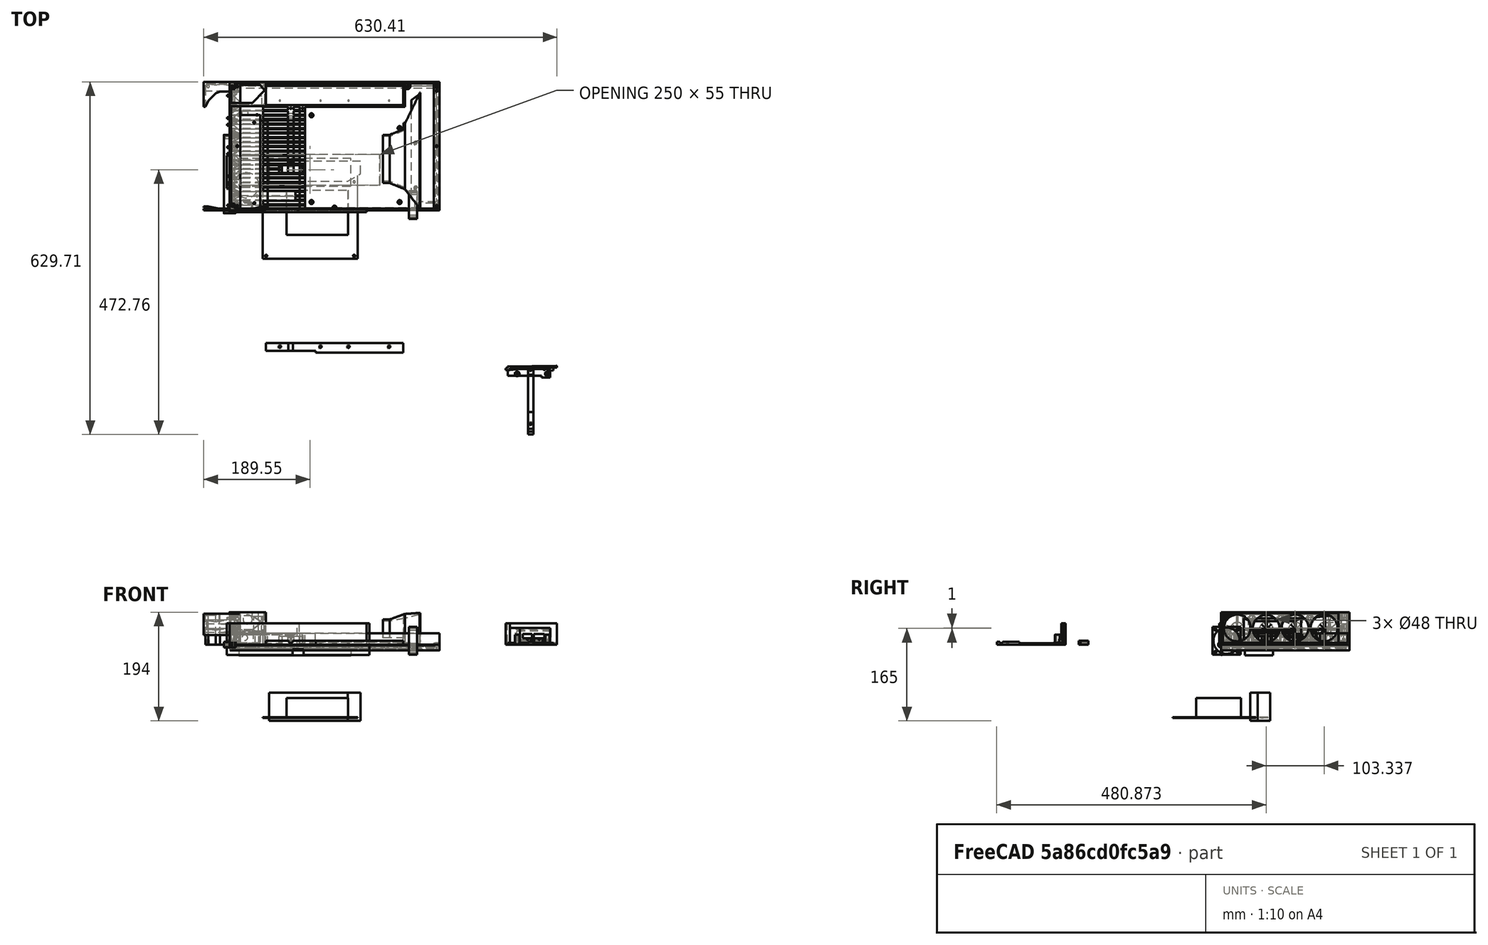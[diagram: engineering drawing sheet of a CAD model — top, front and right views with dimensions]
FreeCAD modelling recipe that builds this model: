
FCSTD DOCUMENT  (FreeCAD 1.0R39109 (Git))
Label: 4_fan_duct_version
License: All rights reserved
LicenseURL: https://en.wikipedia.org/wiki/All_rights_reserved
objects: Sketcher::SketchObject×94, PartDesign::Pad×51, PartDesign::Pocket×39, PartDesign::Plane×24, PartDesign::Body×20, App::Part×20, App::Link×14, PartDesign::Chamfer×13, App::FeaturePython×12, PartDesign::Fillet×4, PartDesign::LinearPattern×3, PartDesign::AdditiveLoft×3, Spreadsheet::Sheet×2, PartDesign::Mirrored×2, PartDesign::SubtractiveLoft×1, Assembly::JointGroup×1, Assembly::AssemblyObject×1
note: 575 computed .brp shape members not serialized (recipe doc carries the construction recipe); baked Part::Feature solids carry a one-line shape summary decoded from their .brp

FEATURE [Spreadsheet::Sheet] Spreadsheet  label="components"
  cells = B1='weight; C1='width; D1='height; E1='depth; F1='corner radius; J1='radius; K1='depth; A2='screen; B2=930; C2(screen_w)=367.9; D2(screen_h)=222.4; E2(screen_glass_d)=1.5; F2(screen_glass_corner_radius)=1; I2='m3 cutout; J2(m3_hole)=3.5; A3='panel; E3(screen_panel_d)=6.5; I3='m3 insert; J3(m3_insert_r)=4.5; K3(m3_insert_depth)=7; A4='pcb; C4(screen_pcb_w)=200; D4(screen_pcb_h)=50; E4(screen_pcb_d)=19; I4='m3 for threading; J4(m3_threadhole)=2.5; I5='m3 countersunk head; J5(m3_countersunk_head)=6; A6='motherboard; B6=790; C6(mb_w)=170; D6(mb_h)=170; E6(mb_d)=51; A7='+cpu and ram and ssd; B7=100; A8='cooler; B8=400; A9='gpu; C9(gpu_w)=68; D9(gpu_h)=160; E9(gpu_d)=20; A11='psu; B11=360; C11(psu_w)=55; D11(psu_h)=170; E11(psu_d)=25; F12='mounting hole spacing; G12='mounting hole dia; A13='fan; C13(fan_w)=17; D13(fan_h)=50; E13(fan_d)=50; F13(fan_spacing)=40; A15='screen frame; C15(frame_w)==screen_w + <<choices>>.bezel * 2 + <<choices>>.margin * 2; D15(frame_h)==screen_h + <<choices>>.bezel * 2 + <<choices>>.margin * 2; E15(frame_d)==screen_panel_d + <<choices>>.frame_protective_height + <<choices>>.frame_support_thickness + <<choices>>.screen_panel_foam_thickness
FEATURE [Spreadsheet::Sheet] Spreadsheet001  label="choices"
  cells = A1='screen margin; B1(margin)=0.55; E1='old metal parts:; F1='alu density; G1=0.0027; H1='g/mm3; A2='bezel width; B2(bezel)=3; F2='frame volume; G2=222697.53; H2==G1 * G2; I2='<11mm thick; A3='corner; B3(corner)=1; F3='heatsink base volume; G3=540524.42; H3==G1 * G3; I3='<10mm thick; A4='frame-panel foam thickenss; B4(screen_panel_foam_thickness)=0.75; F4='original 3mm base; G4=266800; H4==G1 * G4; I4==H2 + H3; A5='frame height over screen; B5(frame_protective_height)=1.5; A6='frame support area thickness; B6(frame_support_thickness)=1.25; C6='<the bottom layer of frame that the foam pads are glued to, has space for the motherboard ports block and possibly the fans?; E7='fins; F7='end fins:; G7(fin_end)=3; I7='25t+25s=229.5-2*e-s; J7==B22 + 170 + 5 + 3; A8='edge screwhole margin; B8(screwhole_edge_margin)=5; E8='thickness; G8(fin_thick)=2; I8='26s = 229.5 - 2e-25t; E9='space; G9=6; I9(fin_gap)==(J7 - 2 * G7 - I10 * G8) / (1 + I10); A10='base height (under mb); B10(base_under_mb_thickness)=1.25; E10='count; G10==(J7 - 2 * G7 - G9) / (G8 + G9); I10(fin_count)=22; A11='base height total; B11(base_max_thickness)=20; A13='exit duct length; B13(exit_w)=19; A14='exit_cone_dia; B14(exit_cone)=24.5; A15='exit_fan_circle_dia; B15(exit_fan_dia)=49; A16='fan gap; B16(fan_gap)=2; A17='exit vane thickness; B17(exit_vane_thinnest)=1; C17(exit_vane_thickest)=3; A18='shroud to mb space; B18(shroud_mb_space)=29; A19='exit duct height; B19(exit_height)=55; A20='shroud_wall_thickness; B20(shroud_wall_thickness)=3; A21='shroud base screws; B21(shroud_base_screw_x)=332.5; C21(shroud_base_screw_y1)=40; D21(shroud_base_screw_y2)=120; A22='motherboard to front edge gap; B22(mb_front_edge_gap)=10; A26='left edge to psu; B26(psu_left_gap)=5; A27='top edge to psu; B27(psu_top_gap)=15; A30='leg; B30(leg_axis_dist_from_front)=75; C30(leg_length)=130; D30(leg_bracket_axis_dist)=42.5; E30(leg_bracket_length)=52.5; F30(leg_bracket_slot_end_dist_from_front)==B30 + D30 + E30; B31(leg_axle_hole_dia)=5.2; C31(leg_width)=10; F31(leg_bracket_slot_start_dist_from_front)=115; C32(leg_betweens)=5; D32(leg_clearance)=0.5
FEATURE [Sketcher::SketchObject] Sketch
  ArcFitTolerance = 1e-06
  AttachmentSupport = -> [XY_Plane001]
  FullyConstrained = true
  MakeInternals = false
  MapMode = 5
  expr: Constraints[10] = <<components>>.psu_h
  expr: Constraints[30] = <<components>>.m3_hole
  expr: Constraints[9] = <<components>>.psu_w
  sketch-geometry (13):
    g0: LineSegment StartX=0 StartY=0 StartZ=0 EndX=55 EndY=0 EndZ=0
    g1: LineSegment StartX=55 StartY=0 StartZ=0 EndX=55 EndY=170 EndZ=0
    g2: LineSegment StartX=55 StartY=170 StartZ=0 EndX=0 EndY=170 EndZ=0
    g3: LineSegment StartX=0 StartY=170 StartZ=0 EndX=0 EndY=0 EndZ=0
    g4: LineSegment [constr] StartX=10.85 StartY=13 StartZ=0 EndX=44.15 EndY=13 EndZ=0
    g5: LineSegment [constr] StartX=44.15 StartY=13 StartZ=0 EndX=44.15 EndY=157 EndZ=0
    g6: LineSegment [constr] StartX=44.15 StartY=157 StartZ=0 EndX=10.85 EndY=157 EndZ=0
    g7: LineSegment [constr] StartX=10.85 StartY=157 StartZ=0 EndX=10.85 EndY=13 EndZ=0
    g8: GeomPoint [constr] X=27.5 Y=85 Z=0
    g9: Circle CenterX=10.85 CenterY=157 CenterZ=0 NormalX=0 NormalY=0 NormalZ=1 AngleXU=0 Radius=1.75
    g10: Circle CenterX=44.15 CenterY=157 CenterZ=0 NormalX=0 NormalY=0 NormalZ=1 AngleXU=0 Radius=1.75
    g11: Circle CenterX=10.85 CenterY=13 CenterZ=0 NormalX=0 NormalY=0 NormalZ=1 AngleXU=0 Radius=1.75
    g12: Circle CenterX=44.15 CenterY=13 CenterZ=0 NormalX=0 NormalY=0 NormalZ=1 AngleXU=0 Radius=1.75
  constraints (31):
    c: Coincident(g0,g1)
    c: Coincident(g1,g2)
    c: Coincident(g2,g3)
    c: Coincident(g3,g0)
    c: Horizontal(g0)
    c: Horizontal(g2)
    c: Vertical(g1)
    c: Vertical(g3)
    c: Coincident(g0,g-1)
    c: DistanceX(g2,g2) = 55
    c: DistanceY(g1,g1) = 170
    c: Coincident(g4,g5)
    c: Coincident(g5,g6)
    c: Coincident(g6,g7)
    c: Coincident(g7,g4)
    c: Horizontal(g4)
    c: Horizontal(g6)
    c: Vertical(g5)
    c: Vertical(g7)
    c: Symmetric(g6,g4,g8)
    c: Distance(g5,g7) = 33.3
    c: Distance(g4,g6) = 144
    c: Symmetric(g2,g0,g8)
    c: Coincident(g9,g6)
    c: Coincident(g10,g5)
    c: Coincident(g11,g4)
    c: Coincident(g12,g4)
    c: Equal(g9,g10)
    c: Equal(g10,g11)
    c: Equal(g11,g12)
    c: Diameter(g11) = 3.5
FEATURE [PartDesign::Pad] Pad
  Direction = (0,0,1)
  Length = 25
  Length2 = 10
  Profile = -> Sketch
  ReferenceAxis = -> Sketch [N_Axis]
  Refine = true
  Suppressed = false
  Type = 0
  expr: Length = <<components>>.psu_d
FEATURE [PartDesign::Plane] DatumPlane
  AttachmentSupport = -> [Pad]
  Length = 92.6491
  MapMode = 5
  Placement = pos=(0,170,0) rot=(0,0.707107,0.707107;3.14159rad)
  ResizeMode = 0
  Width = 62.6491
FEATURE [Sketcher::SketchObject] Sketch001
  ArcFitTolerance = 1e-06
  AttachmentSupport = -> [DatumPlane]
  FullyConstrained = true
  MakeInternals = false
  MapMode = 5
  Placement = pos=(0,170,0) rot=(0,0.707107,0.707107;3.14159rad)
  expr: Constraints[10] = <<components>>.psu_d
  expr: Constraints[9] = <<components>>.psu_w
  sketch-geometry (5):
    g0: LineSegment [constr] StartX=-55 StartY=25 StartZ=0 EndX=-55 EndY=0 EndZ=0
    g1: LineSegment [constr] StartX=-55 StartY=0 StartZ=0 EndX=0 EndY=0 EndZ=0
    g2: LineSegment [constr] StartX=0 StartY=0 StartZ=0 EndX=0 EndY=25 EndZ=0
    g3: LineSegment [constr] StartX=0 StartY=25 StartZ=0 EndX=-55 EndY=25 EndZ=0
    g4: Circle CenterX=-27.5 CenterY=12.5 CenterZ=0 NormalX=0 NormalY=0 NormalZ=1 AngleXU=0 Radius=5
  constraints (13):
    c: Coincident(g0,g1)
    c: Coincident(g1,g2)
    c: Coincident(g2,g3)
    c: Coincident(g3,g0)
    c: Vertical(g0)
    c: Vertical(g2)
    c: Horizontal(g1)
    c: Horizontal(g3)
    c: Coincident(g1,g-1)
    c: DistanceX(g3,g3) = 55
    c: DistanceY(g0,g0) = 25
    c: Diameter(g4) = 10
    c: Symmetric(g0,g1,g4)
FEATURE [PartDesign::Pad] Pad001
  BaseFeature = -> Pad
  Direction = (0,1,-2e-16)
  Length = 7
  Length2 = 10
  Profile = -> Sketch001
  ReferenceAxis = -> Sketch001 [N_Axis]
  Refine = true
  Suppressed = false
  Type = 0
FEATURE [PartDesign::Body] Body
  AllowCompound = false
  Group = -> [Sketch,Pad,DatumPlane,Sketch001,Pad001]
  Origin = -> Origin001
  Tip = -> Pad001
FEATURE [App::Part] Part  label="PSU"
  Group = -> [Body]
  Origin = -> Origin
FEATURE [Sketcher::SketchObject] Sketch002
  ArcFitTolerance = 1e-06
  AttachmentSupport = -> [XY_Plane003]
  FullyConstrained = true
  MakeInternals = false
  MapMode = 5
  expr: Constraints[26] = <<components>>.screen_glass_corner_radius
  expr: Constraints[5] = <<components>>.screen_w
  expr: Constraints[6] = <<components>>.screen_h
  sketch-geometry (12):
    g0: LineSegment StartX=1 StartY=4.954e-13 StartZ=0 EndX=366.9 EndY=4.954e-13 EndZ=0
    g1: LineSegment StartX=367.9 StartY=1 StartZ=0 EndX=367.9 EndY=221.4 EndZ=0
    g2: LineSegment StartX=366.9 StartY=222.4 StartZ=0 EndX=1 EndY=222.4 EndZ=0
    g3: LineSegment StartX=4.954e-13 StartY=221.4 StartZ=0 EndX=4.954e-13 EndY=1 EndZ=0
    g4: ArcOfCircle CenterX=1 CenterY=1 CenterZ=0 NormalX=0 NormalY=0 NormalZ=1 AngleXU=0 Radius=1 StartAngle=3.14159 EndAngle=4.71239
    g5: GeomPoint [constr] X=0 Y=0 Z=0
    g6: ArcOfCircle CenterX=1 CenterY=221.4 CenterZ=0 NormalX=0 NormalY=0 NormalZ=1 AngleXU=0 Radius=1 StartAngle=1.5708 EndAngle=3.14159
    g7: GeomPoint [constr] X=0 Y=222.4 Z=0
    g8: ArcOfCircle CenterX=366.9 CenterY=221.4 CenterZ=0 NormalX=0 NormalY=0 NormalZ=1 AngleXU=0 Radius=1 StartAngle=-3.1388e-12 EndAngle=1.5708
    g9: GeomPoint [constr] X=367.9 Y=222.4 Z=0
    g10: ArcOfCircle CenterX=366.9 CenterY=1 CenterZ=0 NormalX=0 NormalY=0 NormalZ=1 AngleXU=0 Radius=1 StartAngle=4.71239 EndAngle=6.28319
    g11: GeomPoint [constr] X=367.9 Y=0 Z=0
  constraints (27):
    c: Horizontal(g0)
    c: Horizontal(g2)
    c: Vertical(g1)
    c: Vertical(g3)
    c: Coincident(g5,g-1)
    c: DistanceX(g5,g11) = 367.9
    c: DistanceY(g5,g7) = 222.4
    c: PointOnObject(g5,g0)
    c: PointOnObject(g5,g3)
    c: Tangent(g0,g4) = -1.5708
    c: Tangent(g3,g4) = -1.5708
    c: PointOnObject(g7,g3)
    c: PointOnObject(g7,g2)
    c: Tangent(g3,g6) = -1.5708
    c: Tangent(g2,g6) = -1.5708
    c: PointOnObject(g9,g2)
    c: PointOnObject(g9,g1)
    c: Tangent(g2,g8) = -1.5708
    c: Tangent(g1,g8) = -1.5708
    c: PointOnObject(g11,g0)
    c: PointOnObject(g11,g1)
    c: Tangent(g0,g10) = -1.5708
    c: Tangent(g1,g10) = -1.5708
    c: Equal(g4,g6)
    c: Equal(g6,g8)
    c: Equal(g8,g10)
    c: Radius(g4) = 1
FEATURE [PartDesign::Pad] Pad002
  Direction = (0,0,1)
  Length = 1.5
  Length2 = 10
  Profile = -> Sketch002
  ReferenceAxis = -> Sketch002 [N_Axis]
  Refine = true
  Reversed = true
  Suppressed = false
  Type = 0
  expr: Length = <<components>>.screen_glass_d
FEATURE [Sketcher::SketchObject] Sketch003
  ArcFitTolerance = 1e-06
  AttachmentSupport = -> [XY_Plane003]
  FullyConstrained = true
  MakeInternals = false
  MapMode = 5
  expr: Constraints[22] = <<components>>.screen_h - 4
  expr: Constraints[23] = <<components>>.screen_w - 2.5
  sketch-geometry (8):
    g0: LineSegment StartX=6.5 StartY=12.5 StartZ=0 EndX=6.5 EndY=218.4 EndZ=0
    g1: LineSegment StartX=6.5 StartY=218.4 StartZ=0 EndX=365.4 EndY=218.4 EndZ=0
    g2: LineSegment StartX=365.4 StartY=218.4 StartZ=0 EndX=365.4 EndY=12.5 EndZ=0
    g3: LineSegment StartX=365.4 StartY=12.5 StartZ=0 EndX=330.4 EndY=12.5 EndZ=0
    g4: LineSegment StartX=330.4 StartY=12.5 StartZ=0 EndX=330.4 EndY=1 EndZ=0
    g5: LineSegment StartX=330.4 StartY=1 StartZ=0 EndX=41.5 EndY=1 EndZ=0
    g6: LineSegment StartX=41.5 StartY=1 StartZ=0 EndX=41.5 EndY=12.5 EndZ=0
    g7: LineSegment StartX=41.5 StartY=12.5 StartZ=0 EndX=6.5 EndY=12.5 EndZ=0
  constraints (24):
    c: Vertical(g0)
    c: Coincident(g0,g1)
    c: Horizontal(g1)
    c: Coincident(g1,g2)
    c: Vertical(g2)
    c: Coincident(g2,g3)
    c: Horizontal(g3)
    c: Coincident(g3,g4)
    c: Vertical(g4)
    c: Coincident(g4,g5)
    c: Coincident(g5,g6)
    c: Vertical(g6)
    c: Coincident(g6,g7)
    c: Coincident(g7,g0)
    c: Horizontal(g7)
    c: Horizontal(g5)
    c: Equal(g7,g3)
    c: DistanceX(g3,g3) = 35
    c: DistanceY(g2) = 12.5
    c: DistanceY(g4) = 1
    c: Equal(g6,g4)
    c: DistanceX(g0) = 6.5
    c: DistanceY(g0) = 218.4
    c: DistanceX(g1) = 365.4
FEATURE [PartDesign::Pad] Pad003
  BaseFeature = -> Pad002
  Direction = (0,0,1)
  Length = 6.5
  Length2 = 10
  Profile = -> Sketch003
  ReferenceAxis = -> Sketch003 [N_Axis]
  Refine = true
  Reversed = true
  Suppressed = false
  Type = 0
  expr: Length = <<components>>.screen_panel_d
FEATURE [Sketcher::SketchObject] Sketch004
  ArcFitTolerance = 1e-06
  AttachmentSupport = -> [XY_Plane005]
  FullyConstrained = true
  MakeInternals = false
  MapMode = 5
  expr: Constraints[10] = <<components>>.mb_h
  expr: Constraints[9] = <<components>>.mb_w
  sketch-geometry (12):
    g0: LineSegment StartX=0 StartY=0 StartZ=0 EndX=170 EndY=0 EndZ=0
    g1: LineSegment StartX=170 StartY=0 StartZ=0 EndX=170 EndY=170 EndZ=0
    g2: LineSegment StartX=170 StartY=170 StartZ=0 EndX=0 EndY=170 EndZ=0
    g3: LineSegment StartX=0 StartY=170 StartZ=0 EndX=0 EndY=0 EndZ=0
    g4: Circle CenterX=6.35 CenterY=4.8997 CenterZ=0 NormalX=0 NormalY=0 NormalZ=1 AngleXU=0 Radius=2
    g5: Circle CenterX=163.65 CenterY=4.8997 CenterZ=0 NormalX=0 NormalY=0 NormalZ=1 AngleXU=0 Radius=2
    g6: Circle CenterX=6.35 CenterY=159.84 CenterZ=0 NormalX=0 NormalY=0 NormalZ=1 AngleXU=0 Radius=2
    g7: Circle CenterX=163.65 CenterY=136.98 CenterZ=0 NormalX=0 NormalY=0 NormalZ=1 AngleXU=0 Radius=2
    g8: LineSegment [constr] StartX=6.35 StartY=159.84 StartZ=0 EndX=6.35 EndY=4.8997 EndZ=0
    g9: LineSegment [constr] StartX=6.35 StartY=4.8997 StartZ=0 EndX=163.65 EndY=4.8997 EndZ=0
    g10: LineSegment [constr] StartX=163.65 StartY=4.8997 StartZ=0 EndX=163.65 EndY=136.98 EndZ=0
    g11: LineSegment [constr] StartX=163.65 StartY=136.98 StartZ=0 EndX=6.35 EndY=136.98 EndZ=0
  constraints (32):
    c: Coincident(g0,g1)
    c: Coincident(g1,g2)
    c: Coincident(g2,g3)
    c: Coincident(g3,g0)
    c: Horizontal(g0)
    c: Horizontal(g2)
    c: Vertical(g1)
    c: Vertical(g3)
    c: Coincident(g0,g-1)
    c: DistanceX(g2,g2) = 170
    c: DistanceY(g1,g1) = 170
    c: Diameter(g4) = 4
    c: Diameter(g5) = 4
    c: Diameter(g6) = 4
    c: Diameter(g7) = 4
    c: Coincident(g8,g6)
    c: Coincident(g8,g4)
    c: Vertical(g8)
    c: Coincident(g9,g4)
    c: Coincident(g9,g5)
    c: Horizontal(g9)
    c: Coincident(g10,g5)
    c: Coincident(g10,g7)
    c: Vertical(g10)
    c: Distance(g6,g2) = 10.16
    c: Distance(g6,g3) = 6.35
    c: Distance(g7,g1) = 6.35
    c: DistanceY(g5) = 4.8997
    c: Coincident(g11,g7)
    c: PointOnObject(g11,g8)
    c: Horizontal(g11)
    c: Distance(g6,g11) = 22.86
FEATURE [PartDesign::Pad] Pad004
  Direction = (0,0,1)
  Length = 1.6
  Length2 = 10
  Profile = -> Sketch004
  ReferenceAxis = -> Sketch004 [N_Axis]
  Refine = true
  Suppressed = false
  Type = 0
FEATURE [Sketcher::SketchObject] Sketch005
  ArcFitTolerance = 1e-06
  AttachmentSupport = -> [XY_Plane003]
  FullyConstrained = true
  MakeInternals = false
  MapMode = 5
  sketch-geometry (4):
    g0: LineSegment StartX=17 StartY=43 StartZ=0 EndX=217 EndY=43 EndZ=0
    g1: LineSegment StartX=217 StartY=43 StartZ=0 EndX=217 EndY=93 EndZ=0
    g2: LineSegment StartX=217 StartY=93 StartZ=0 EndX=17 EndY=93 EndZ=0
    g3: LineSegment StartX=17 StartY=93 StartZ=0 EndX=17 EndY=43 EndZ=0
  constraints (12):
    c: Coincident(g0,g1)
    c: Coincident(g1,g2)
    c: Coincident(g2,g3)
    c: Coincident(g3,g0)
    c: Horizontal(g0)
    c: Horizontal(g2)
    c: Vertical(g1)
    c: Vertical(g3)
    c: Distance(g1,g3) = 200
    c: Distance(g0,g2) = 50
    c: DistanceX(g0) = 17
    c: DistanceY(g0) = 43
FEATURE [PartDesign::Pad] Pad005
  BaseFeature = -> Pad003
  Direction = (0,0,1)
  Length = 19
  Length2 = 10
  Profile = -> Sketch005
  ReferenceAxis = -> Sketch005 [N_Axis]
  Refine = true
  Reversed = true
  Suppressed = false
  Type = 0
  expr: Length = <<components>>.screen_pcb_d
FEATURE [PartDesign::Body] Body001
  AllowCompound = false
  Group = -> [Sketch002,Pad002,Sketch003,Pad003,Sketch005,Pad005]
  Origin = -> Origin003
  Tip = -> Pad005
FEATURE [App::Part] Part001  label="SCREEN"
  Group = -> [Body001]
  Origin = -> Origin002
FEATURE [Sketcher::SketchObject] Sketch006
  ArcFitTolerance = 1e-06
  AttachmentSupport = -> [XY_Plane007]
  FullyConstrained = false
  MakeInternals = false
  MapMode = 5
  expr: Constraints[20] = <<components>>.frame_w
  expr: Constraints[21] = <<components>>.frame_h
  expr: Constraints[22] = <<choices>>.corner
  sketch-geometry (12):
    g0: LineSegment StartX=1 StartY=1.7071e-12 StartZ=0 EndX=374 EndY=1.7071e-12 EndZ=0
    g1: LineSegment StartX=375 StartY=1 StartZ=0 EndX=375 EndY=228.5 EndZ=0
    g2: LineSegment StartX=374 StartY=229.5 StartZ=0 EndX=1 EndY=229.5 EndZ=0
    g3: LineSegment StartX=1.7071e-12 StartY=228.5 StartZ=0 EndX=1.7071e-12 EndY=1 EndZ=0
    g4: ArcOfCircle CenterX=1 CenterY=1 CenterZ=0 NormalX=0 NormalY=0 NormalZ=1 AngleXU=0 Radius=1 StartAngle=3.14159 EndAngle=4.71239
    g5: ArcOfCircle CenterX=374 CenterY=1 CenterZ=0 NormalX=0 NormalY=0 NormalZ=1 AngleXU=0 Radius=1 StartAngle=4.71239 EndAngle=6.28319
    g6: ArcOfCircle CenterX=374 CenterY=228.5 CenterZ=0 NormalX=0 NormalY=0 NormalZ=1 AngleXU=0 Radius=1 StartAngle=-2.76916e-11 EndAngle=1.5708
    g7: ArcOfCircle CenterX=1 CenterY=228.5 CenterZ=0 NormalX=0 NormalY=0 NormalZ=1 AngleXU=0 Radius=1 StartAngle=1.5708 EndAngle=3.14159
    g8: GeomPoint [constr] X=0 Y=0 Z=0
    g9: GeomPoint [constr] X=375 Y=229.5 Z=0
    g10: GeomPoint [constr] X=14.2421 Y=11.9526 Z=0
    g11: GeomPoint [constr] X=324.973 Y=165.011 Z=0
  constraints (23):
    c: Tangent(g0,g4) = -1.5708
    c: Tangent(g0,g5) = -1.5708
    c: Tangent(g1,g5) = -1.5708
    c: Tangent(g1,g6) = -1.5708
    c: Tangent(g2,g6) = -1.5708
    c: Tangent(g2,g7) = -1.5708
    c: Tangent(g3,g7) = -1.5708
    c: Tangent(g3,g4) = -1.5708
    c: Horizontal(g0)
    c: Horizontal(g2)
    c: Vertical(g1)
    c: Vertical(g3)
    c: Equal(g4,g5)
    c: Equal(g5,g6)
    c: Equal(g6,g7)
    c: PointOnObject(g8,g0)
    c: PointOnObject(g8,g3)
    c: PointOnObject(g9,g1)
    c: PointOnObject(g9,g2)
    c: Coincident(g8,g-1)
    c: DistanceX(g9) = 375
    c: DistanceY(g9) = 229.5
    c: Radius(g6) = 1
FEATURE [PartDesign::Pad] Pad006
  Direction = (0,0,1)
  Length = 10
  Length2 = 10
  Profile = -> Sketch006
  ReferenceAxis = -> Sketch006 [N_Axis]
  Refine = true
  Reversed = true
  Suppressed = false
  Type = 0
  expr: Length = <<components>>.frame_d
FEATURE [Sketcher::SketchObject] Sketch007
  ArcFitTolerance = 1e-06
  AttachmentSupport = -> [XY_Plane007]
  FullyConstrained = true
  MakeInternals = false
  MapMode = 5
  expr: Constraints[19] = <<components>>.screen_w + 2 * <<choices>>.margin
  expr: Constraints[20] = <<components>>.screen_h + 2 * <<choices>>.margin
  expr: Constraints[21] = <<components>>.screen_glass_corner_radius
  expr: Constraints[22] = <<choices>>.bezel
  expr: Constraints[23] = <<choices>>.bezel
  sketch-geometry (10):
    g0: LineSegment StartX=4 StartY=3 StartZ=0 EndX=371 EndY=3 EndZ=0
    g1: LineSegment StartX=372 StartY=4 StartZ=0 EndX=372 EndY=225.5 EndZ=0
    g2: LineSegment StartX=371 StartY=226.5 StartZ=0 EndX=4 EndY=226.5 EndZ=0
    g3: LineSegment StartX=3 StartY=225.5 StartZ=0 EndX=3 EndY=4 EndZ=0
    g4: ArcOfCircle CenterX=4 CenterY=4 CenterZ=0 NormalX=0 NormalY=0 NormalZ=1 AngleXU=0 Radius=1 StartAngle=3.14159 EndAngle=4.71239
    g5: ArcOfCircle CenterX=371 CenterY=4 CenterZ=0 NormalX=0 NormalY=0 NormalZ=1 AngleXU=0 Radius=1 StartAngle=4.71239 EndAngle=6.28319
    g6: ArcOfCircle CenterX=371 CenterY=225.5 CenterZ=0 NormalX=0 NormalY=0 NormalZ=1 AngleXU=0 Radius=1 StartAngle=-1.15e-14 EndAngle=1.5708
    g7: ArcOfCircle CenterX=4 CenterY=225.5 CenterZ=0 NormalX=0 NormalY=0 NormalZ=1 AngleXU=0 Radius=1 StartAngle=1.5708 EndAngle=3.14159
    g8: GeomPoint [constr] X=3 Y=3 Z=0
    g9: GeomPoint [constr] X=372 Y=226.5 Z=0
  constraints (24):
    c: Tangent(g0,g4) = -1.5708
    c: Tangent(g0,g5) = -1.5708
    c: Tangent(g1,g5) = -1.5708
    c: Tangent(g1,g6) = -1.5708
    c: Tangent(g2,g6) = -1.5708
    c: Tangent(g2,g7) = -1.5708
    c: Tangent(g3,g7) = -1.5708
    c: Tangent(g3,g4) = -1.5708
    c: Horizontal(g0)
    c: Horizontal(g2)
    c: Vertical(g1)
    c: Vertical(g3)
    c: Equal(g4,g5)
    c: Equal(g5,g6)
    c: Equal(g6,g7)
    c: PointOnObject(g8,g0)
    c: PointOnObject(g8,g3)
    c: PointOnObject(g9,g1)
    c: PointOnObject(g9,g2)
    c: Distance(g1,g3) = 369
    c: Distance(g2,g0) = 223.5
    c: Radius(g4) = 1
    c: DistanceY(g8) = 3
    c: DistanceX(g8) = 3
FEATURE [PartDesign::Pocket] Pocket
  BaseFeature = -> Pad006
  Direction = (0,0,-1)
  Length = 3
  Length2 = 5
  Profile = -> Sketch007
  ReferenceAxis = -> Sketch007 [N_Axis]
  Refine = true
  Suppressed = false
  Type = 0
  expr: Length = <<choices>>.frame_protective_height + <<components>>.screen_glass_d
FEATURE [Sketcher::SketchObject] Sketch008
  ArcFitTolerance = 1e-06
  AttachmentSupport = -> [XY_Plane007]
  FullyConstrained = true
  MakeInternals = false
  MapMode = 5
  expr: Constraints[10] = <<choices>>.bezel + <<choices>>.margin + 11
  expr: Constraints[11] = <<components>>.frame_h - <<choices>>.bezel - <<choices>>.margin - 3.5
  expr: Constraints[12] = <<choices>>.bezel + <<choices>>.margin + 6
  expr: Constraints[13] = <<components>>.frame_w - <<choices>>.bezel - <<choices>>.margin - 2
  expr: Constraints[9] = <<choices>>.bezel + <<choices>>.margin + 0.8
  sketch-geometry (24):
    g0: LineSegment StartX=10.05 StartY=222.45 StartZ=0 EndX=368.95 EndY=222.45 EndZ=0
    g1: LineSegment StartX=369.45 StartY=221.95 StartZ=0 EndX=369.45 EndY=15.55 EndZ=0
    g2: LineSegment StartX=368.95 StartY=15.05 StartZ=0 EndX=339.95 EndY=15.05 EndZ=0
    g3: LineSegment StartX=339.45 StartY=14.55 StartZ=0 EndX=339.45 EndY=4.85 EndZ=0
    g4: LineSegment StartX=338.95 StartY=4.35 StartZ=0 EndX=40.05 EndY=4.35 EndZ=0
    g5: LineSegment StartX=39.55 StartY=4.85 StartZ=0 EndX=39.55 EndY=14.05 EndZ=0
    g6: LineSegment StartX=39.05 StartY=14.55 StartZ=0 EndX=10.05 EndY=14.55 EndZ=0
    g7: LineSegment StartX=9.55 StartY=15.05 StartZ=0 EndX=9.55 EndY=221.95 EndZ=0
    g8: ArcOfCircle CenterX=10.05 CenterY=221.95 CenterZ=0 NormalX=0 NormalY=0 NormalZ=1 AngleXU=0 Radius=0.5 StartAngle=1.5708 EndAngle=3.14159
    g9: GeomPoint [constr] X=9.55 Y=222.45 Z=0
    g10: ArcOfCircle CenterX=368.95 CenterY=221.95 CenterZ=0 NormalX=0 NormalY=0 NormalZ=1 AngleXU=0 Radius=0.5 StartAngle=-1.87e-14 EndAngle=1.5708
    g11: GeomPoint [constr] X=369.45 Y=222.45 Z=0
    g12: ArcOfCircle CenterX=368.95 CenterY=15.55 CenterZ=0 NormalX=0 NormalY=0 NormalZ=1 AngleXU=0 Radius=0.5 StartAngle=4.71239 EndAngle=6.28319
    g13: GeomPoint [constr] X=369.45 Y=15.05 Z=0
    g14: ArcOfCircle CenterX=339.95 CenterY=14.55 CenterZ=0 NormalX=0 NormalY=0 NormalZ=1 AngleXU=0 Radius=0.5 StartAngle=1.5708 EndAngle=3.14159
    g15: GeomPoint [constr] X=339.45 Y=15.05 Z=0
    g16: ArcOfCircle CenterX=338.95 CenterY=4.85 CenterZ=0 NormalX=0 NormalY=0 NormalZ=1 AngleXU=0 Radius=0.5 StartAngle=4.71239 EndAngle=6.28319
    g17: GeomPoint [constr] X=339.45 Y=4.35 Z=0
    g18: ArcOfCircle CenterX=40.05 CenterY=4.85 CenterZ=0 NormalX=0 NormalY=0 NormalZ=1 AngleXU=0 Radius=0.5 StartAngle=3.14159 EndAngle=4.71239
    g19: GeomPoint [constr] X=39.55 Y=4.35 Z=0
    g20: ArcOfCircle CenterX=39.05 CenterY=14.05 CenterZ=0 NormalX=0 NormalY=0 NormalZ=1 AngleXU=0 Radius=0.5 StartAngle=5e-16 EndAngle=1.5708
    g21: GeomPoint [constr] X=39.55 Y=14.55 Z=0
    g22: ArcOfCircle CenterX=10.05 CenterY=15.05 CenterZ=0 NormalX=0 NormalY=0 NormalZ=1 AngleXU=0 Radius=0.5 StartAngle=3.14159 EndAngle=4.71239
    g23: GeomPoint [constr] X=9.55 Y=14.55 Z=0
  constraints (56):
    c: Horizontal(g0)
    c: Vertical(g1)
    c: Horizontal(g2)
    c: Vertical(g3)
    c: Horizontal(g4)
    c: Vertical(g5)
    c: Horizontal(g6)
    c: Vertical(g7)
    c: DistanceX(g23,g21) = 30
    c: DistanceY(g19) = 4.35
    c: DistanceY(g21) = 14.55
    c: DistanceY(g9) = 222.45
    c: DistanceX(g9) = 9.55
    c: DistanceX(g11) = 369.45
    c: PointOnObject(g9,g7)
    c: PointOnObject(g9,g0)
    c: Tangent(g7,g8) = 1.5708
    c: Tangent(g0,g8) = 1.5708
    c: PointOnObject(g11,g0)
    c: PointOnObject(g11,g1)
    c: Tangent(g0,g10) = 1.5708
    c: Tangent(g1,g10) = 1.5708
    c: PointOnObject(g13,g2)
    c: PointOnObject(g13,g1)
    c: Tangent(g2,g12) = 1.5708
    c: Tangent(g1,g12) = 1.5708
    c: PointOnObject(g15,g2)
    c: PointOnObject(g15,g3)
    c: Tangent(g2,g14) = -1.5708
    c: Tangent(g3,g14) = -1.5708
    c: PointOnObject(g17,g3)
    c: PointOnObject(g17,g4)
    c: Tangent(g3,g16) = 1.5708
    c: Tangent(g4,g16) = 1.5708
    c: PointOnObject(g19,g4)
    c: PointOnObject(g19,g5)
    c: Tangent(g4,g18) = 1.5708
    c: Tangent(g5,g18) = 1.5708
    c: PointOnObject(g21,g5)
    c: PointOnObject(g21,g6)
    c: Tangent(g5,g20) = -1.5708
    c: Tangent(g6,g20) = -1.5708
    c: PointOnObject(g23,g6)
    c: PointOnObject(g23,g7)
    c: Tangent(g6,g22) = 1.5708
    c: Tangent(g7,g22) = 1.5708
    c: Equal(g22,g8)
    c: Radius(g8) = 0.5
    c: Equal(g20,g18)
    c: Equal(g18,g22)
    c: Equal(g16,g14)
    c: Equal(g14,g12)
    c: Equal(g12,g10)
    c: Equal(g10,g8)
    c: PointOnObject(g14,g6)
    c: Equal(g2,g6)
FEATURE [PartDesign::Pocket] Pocket001
  BaseFeature = -> Pocket
  Direction = (0,0,-1)
  Length = 8.75
  Length2 = 5
  Profile = -> Sketch008
  ReferenceAxis = -> Sketch008 [N_Axis]
  Refine = true
  Suppressed = false
  Type = 0
  expr: Length = <<components>>.screen_panel_d + <<choices>>.frame_protective_height + <<choices>>.screen_panel_foam_thickness
FEATURE [Sketcher::SketchObject] Sketch009
  ArcFitTolerance = 1e-06
  AttachmentSupport = -> [XY_Plane007]
  FullyConstrained = true
  MakeInternals = false
  MapMode = 5
  expr: Constraints[22] = <<choices>>.bezel + <<choices>>.margin + 41.5
  expr: Constraints[23] = <<choices>>.bezel + <<choices>>.margin + 15
  sketch-geometry (10):
    g0: LineSegment StartX=19.55 StartY=45.05 StartZ=0 EndX=267.55 EndY=45.05 EndZ=0
    g1: LineSegment StartX=268.55 StartY=46.05 StartZ=0 EndX=268.55 EndY=99.05 EndZ=0
    g2: LineSegment StartX=267.55 StartY=100.05 StartZ=0 EndX=19.55 EndY=100.05 EndZ=0
    g3: LineSegment StartX=18.55 StartY=99.05 StartZ=0 EndX=18.55 EndY=46.05 EndZ=0
    g4: ArcOfCircle CenterX=19.55 CenterY=46.05 CenterZ=0 NormalX=0 NormalY=0 NormalZ=1 AngleXU=0 Radius=1 StartAngle=3.14159 EndAngle=4.71239
    g5: ArcOfCircle CenterX=267.55 CenterY=46.05 CenterZ=0 NormalX=0 NormalY=0 NormalZ=1 AngleXU=0 Radius=1 StartAngle=4.71239 EndAngle=6.28319
    g6: ArcOfCircle CenterX=267.55 CenterY=99.05 CenterZ=0 NormalX=0 NormalY=0 NormalZ=1 AngleXU=0 Radius=1 StartAngle=8e-16 EndAngle=1.5708
    g7: ArcOfCircle CenterX=19.55 CenterY=99.05 CenterZ=0 NormalX=0 NormalY=0 NormalZ=1 AngleXU=0 Radius=1 StartAngle=1.5708 EndAngle=3.14159
    g8: GeomPoint [constr] X=18.55 Y=45.05 Z=0
    g9: GeomPoint [constr] X=268.55 Y=100.05 Z=0
  constraints (24):
    c: Tangent(g0,g4) = -1.5708
    c: Tangent(g0,g5) = -1.5708
    c: Tangent(g1,g5) = -1.5708
    c: Tangent(g1,g6) = -1.5708
    c: Tangent(g2,g6) = -1.5708
    c: Tangent(g2,g7) = -1.5708
    c: Tangent(g3,g7) = -1.5708
    c: Tangent(g3,g4) = -1.5708
    c: Horizontal(g0)
    c: Horizontal(g2)
    c: Vertical(g1)
    c: Vertical(g3)
    c: Equal(g4,g5)
    c: Equal(g5,g6)
    c: Equal(g6,g7)
    c: PointOnObject(g8,g0)
    c: PointOnObject(g8,g3)
    c: PointOnObject(g9,g1)
    c: PointOnObject(g9,g2)
    c: Distance(g1,g3) = 250
    c: Distance(g0,g2) = 55
    c: Radius(g5) = 1
    c: DistanceY(g0) = 45.05
    c: DistanceX(g8) = 18.55
FEATURE [PartDesign::Pocket] Pocket002
  BaseFeature = -> Pocket001
  Direction = (0,0,-1)
  Length = 0
  Length2 = 5
  Profile = -> Sketch009
  ReferenceAxis = -> Sketch009 [N_Axis]
  Refine = true
  Suppressed = false
  Type = 1
FEATURE [Sketcher::SketchObject] Sketch010
  ArcFitTolerance = 1e-06
  AttachmentSupport = -> [XY_Plane005]
  FullyConstrained = false
  MakeInternals = false
  MapMode = 5
  sketch-geometry (11):
    g0: LineSegment [constr] StartX=0 StartY=0 StartZ=0 EndX=170 EndY=0 EndZ=0
    g1: LineSegment [constr] StartX=170 StartY=0 StartZ=0 EndX=170 EndY=170 EndZ=0
    g2: LineSegment [constr] StartX=170 StartY=170 StartZ=0 EndX=0 EndY=170 EndZ=0
    g3: LineSegment [constr] StartX=0 StartY=170 StartZ=0 EndX=0 EndY=0 EndZ=0
    g4: LineSegment StartX=12 StartY=174 StartZ=0 EndX=12 EndY=138 EndZ=0
    g5: LineSegment StartX=175 StartY=174 StartZ=0 EndX=12 EndY=174 EndZ=0
    g6: LineSegment [constr] StartX=175 StartY=138 StartZ=0 EndX=175 EndY=151.25 EndZ=0
    g7: LineSegment StartX=175 StartY=151.25 StartZ=0 EndX=175 EndY=174 EndZ=0
    g8: LineSegment StartX=12 StartY=138 StartZ=0 EndX=151.759 EndY=138 EndZ=0
    g9: LineSegment [constr] StartX=151.759 StartY=138 StartZ=0 EndX=175 EndY=138 EndZ=0
    g10: LineSegment StartX=151.759 StartY=138 StartZ=0 EndX=175 EndY=151.25 EndZ=0
  constraints (29):
    c: Coincident(g0,g1)
    c: Coincident(g1,g2)
    c: Coincident(g2,g3)
    c: Coincident(g3,g0)
    c: Horizontal(g0)
    c: Horizontal(g2)
    c: Vertical(g1)
    c: Vertical(g3)
    c: Distance(g1,g3) = 170
    c: Distance(g0,g2) = 170
    c: Coincident(g0,g-1)
    c: Coincident(g4,g8)
    c: Coincident(g9,g6)
    c: Coincident(g7,g5)
    c: Coincident(g5,g4)
    c: Vertical(g4)
    c: Horizontal(g5)
    c: DistanceX(g4) = 12
    c: Distance(g4,g2) = 4
    c: Distance(g7,g1) = 5
    c: DistanceY(g6,g7) = 36
    c: Coincident(g6,g7)
    c: Vertical(g6)
    c: Vertical(g7)
    c: Coincident(g8,g9)
    c: Horizontal(g8)
    c: Horizontal(g9)
    c: Coincident(g10,g8)
    c: Coincident(g10,g6)
FEATURE [PartDesign::Pad] Pad007
  BaseFeature = -> Pad004
  Direction = (0,0,1)
  Length = 45
  Length2 = 10
  Profile = -> Sketch010
  ReferenceAxis = -> Sketch010 [N_Axis]
  Refine = true
  Suppressed = false
  Type = 0
FEATURE [Sketcher::SketchObject] Sketch011
  ArcFitTolerance = 1e-06
  AttachmentSupport = -> [XY_Plane009]
  FullyConstrained = true
  MakeInternals = false
  MapMode = 5
  expr: Constraints[10] = <<components>>.gpu_w
  expr: Constraints[9] = <<components>>.gpu_h
  sketch-geometry (5):
    g0: LineSegment StartX=0 StartY=0 StartZ=0 EndX=68 EndY=0 EndZ=0
    g1: LineSegment StartX=68 StartY=0 StartZ=0 EndX=68 EndY=160 EndZ=0
    g2: LineSegment StartX=68 StartY=160 StartZ=0 EndX=0 EndY=160 EndZ=0
    g3: LineSegment StartX=0 StartY=160 StartZ=0 EndX=0 EndY=0 EndZ=0
    g4: Circle CenterX=30 CenterY=45 CenterZ=0 NormalX=0 NormalY=0 NormalZ=1 AngleXU=0 Radius=22.5
  constraints (14):
    c: Coincident(g0,g1)
    c: Coincident(g1,g2)
    c: Coincident(g2,g3)
    c: Coincident(g3,g0)
    c: Horizontal(g0)
    c: Horizontal(g2)
    c: Vertical(g1)
    c: Vertical(g3)
    c: Coincident(g0,g-1)
    c: DistanceY(g1,g1) = 160
    c: DistanceX(g2,g2) = 68
    c: Diameter(g4) = 45
    c: DistanceX(g4) = 30
    c: DistanceY(g4) = 45
FEATURE [PartDesign::Pad] Pad009
  Direction = (0,0,1)
  Length = 20
  Length2 = 10
  Profile = -> Sketch011
  ReferenceAxis = -> Sketch011 [N_Axis]
  Refine = true
  Suppressed = false
  Type = 0
  expr: Length = <<components>>.gpu_d
FEATURE [Sketcher::SketchObject] Sketch012
  ArcFitTolerance = 1e-06
  AttachmentSupport = -> [XY_Plane011]
  FullyConstrained = true
  MakeInternals = false
  MapMode = 5
  sketch-geometry (4):
    g0: LineSegment StartX=0 StartY=0 StartZ=0 EndX=15 EndY=0 EndZ=0
    g1: LineSegment StartX=15 StartY=0 StartZ=0 EndX=15 EndY=50 EndZ=0
    g2: LineSegment StartX=15 StartY=50 StartZ=0 EndX=0 EndY=50 EndZ=0
    g3: LineSegment StartX=0 StartY=50 StartZ=0 EndX=0 EndY=0 EndZ=0
  constraints (11):
    c: Coincident(g0,g1)
    c: Coincident(g1,g2)
    c: Coincident(g2,g3)
    c: Coincident(g3,g0)
    c: Horizontal(g0)
    c: Horizontal(g2)
    c: Vertical(g1)
    c: Vertical(g3)
    c: Distance(g1,g3) = 15
    c: Distance(g0,g2) = 50
    c: Coincident(g0,g-1)
FEATURE [PartDesign::Pad] Pad010
  Direction = (0,0,1)
  Length = 50
  Length2 = 10
  Profile = -> Sketch012
  ReferenceAxis = -> Sketch012 [N_Axis]
  Refine = true
  Suppressed = false
  Type = 0
FEATURE [Sketcher::SketchObject] Sketch013
  ArcFitTolerance = 1e-06
  AttachmentSupport = -> [YZ_Plane011]
  FullyConstrained = true
  MakeInternals = false
  MapMode = 5
  Placement = pos=(0,0,0) rot=(0.57735,0.57735,0.57735;2.0944rad)
  expr: Constraints[20] = <<components>>.m3_hole
  expr: Constraints[9] = <<components>>.fan_spacing
  sketch-geometry (10):
    g0: LineSegment [constr] StartX=5 StartY=5 StartZ=0 EndX=45 EndY=5 EndZ=0
    g1: LineSegment [constr] StartX=45 StartY=5 StartZ=0 EndX=45 EndY=45 EndZ=0
    g2: LineSegment [constr] StartX=45 StartY=45 StartZ=0 EndX=5 EndY=45 EndZ=0
    g3: LineSegment [constr] StartX=5 StartY=45 StartZ=0 EndX=5 EndY=5 EndZ=0
    g4: GeomPoint [constr] X=25 Y=25 Z=0
    g5: Circle CenterX=5 CenterY=45 CenterZ=0 NormalX=0 NormalY=0 NormalZ=1 AngleXU=0 Radius=1.75
    g6: Circle CenterX=45 CenterY=45 CenterZ=0 NormalX=0 NormalY=0 NormalZ=1 AngleXU=0 Radius=1.75
    g7: Circle CenterX=45 CenterY=5 CenterZ=0 NormalX=0 NormalY=0 NormalZ=1 AngleXU=0 Radius=1.75
    g8: Circle CenterX=5 CenterY=5 CenterZ=0 NormalX=0 NormalY=0 NormalZ=1 AngleXU=0 Radius=1.75
    g9: Circle CenterX=25 CenterY=25 CenterZ=0 NormalX=0 NormalY=0 NormalZ=1 AngleXU=0 Radius=23.5
  constraints (23):
    c: Coincident(g0,g1)
    c: Coincident(g1,g2)
    c: Coincident(g2,g3)
    c: Coincident(g3,g0)
    c: Horizontal(g0)
    c: Horizontal(g2)
    c: Vertical(g1)
    c: Vertical(g3)
    c: Symmetric(g2,g0,g4)
    c: Distance(g1,g3) = 40
    c: Equal(g3,g0)
    c: DistanceX(g4) = 25
    c: DistanceY(g4) = 25
    c: Coincident(g5,g2)
    c: Coincident(g6,g1)
    c: Coincident(g7,g0)
    c: Coincident(g8,g0)
    c: Equal(g5,g6)
    c: Equal(g6,g8)
    c: Equal(g8,g7)
    c: Diameter(g6) = 3.5
    c: Coincident(g9,g4)
    c: Diameter(g9) = 47
FEATURE [PartDesign::Pocket] Pocket003
  BaseFeature = -> Pad010
  Direction = (-1,0,0)
  Length = 5
  Length2 = 5
  Profile = -> Sketch013
  ReferenceAxis = -> Sketch013 [N_Axis]
  Refine = true
  Reversed = true
  Suppressed = false
  Type = 1
FEATURE [PartDesign::Body] Body005
  AllowCompound = false
  Group = -> [Sketch012,Pad010,Sketch013,Pocket003]
  Origin = -> Origin011
  Placement = pos=(320,-15,-18) rot=(0,0,1;0rad)
  Tip = -> Pocket003
FEATURE [App::Part] Part005  label="FAN"
  Group = -> [Body005]
  Origin = -> Origin010
FEATURE [Sketcher::SketchObject] Sketch014
  ArcFitTolerance = 1e-06
  AttachmentSupport = -> [XY_Plane013]
  FullyConstrained = true
  MakeInternals = false
  MapMode = 5
  expr: Constraints[20] = <<components>>.frame_w
  expr: Constraints[21] = <<components>>.frame_h
  expr: Constraints[22] = <<choices>>.corner
  expr: Constraints[25] = <<choices>>.shroud_base_screw_x
  expr: Constraints[26] = <<choices>>.shroud_base_screw_y2
  expr: Constraints[30] = <<choices>>.shroud_base_screw_y1
  expr: Constraints[31] = <<components>>.m3_threadhole
  expr: Constraints[33] = <<components>>.m3_hole
  expr: Constraints[34] = <<components>>.frame_w / 2
  sketch-geometry (14):
    g0: LineSegment StartX=1 StartY=0 StartZ=0 EndX=374 EndY=0 EndZ=0
    g1: LineSegment StartX=375 StartY=1 StartZ=0 EndX=375 EndY=228.5 EndZ=0
    g2: LineSegment StartX=374 StartY=229.5 StartZ=0 EndX=1 EndY=229.5 EndZ=0
    g3: LineSegment StartX=0 StartY=228.5 StartZ=0 EndX=0 EndY=1 EndZ=0
    g4: ArcOfCircle CenterX=1 CenterY=1 CenterZ=0 NormalX=0 NormalY=0 NormalZ=1 AngleXU=0 Radius=1 StartAngle=3.14159 EndAngle=4.71239
    g5: ArcOfCircle CenterX=374 CenterY=1 CenterZ=0 NormalX=0 NormalY=0 NormalZ=1 AngleXU=0 Radius=1 StartAngle=4.71239 EndAngle=6.28319
    g6: ArcOfCircle CenterX=374 CenterY=228.5 CenterZ=0 NormalX=0 NormalY=0 NormalZ=1 AngleXU=0 Radius=1 StartAngle=1.7e-15 EndAngle=1.5708
    g7: ArcOfCircle CenterX=1 CenterY=228.5 CenterZ=0 NormalX=0 NormalY=0 NormalZ=1 AngleXU=0 Radius=1 StartAngle=1.5708 EndAngle=3.14159
    g8: GeomPoint [constr] X=0 Y=0 Z=0
    g9: GeomPoint [constr] X=375 Y=229.5 Z=0
    g10: LineSegment [constr] StartX=332.5 StartY=0 StartZ=0 EndX=332.5 EndY=120 EndZ=0
    g11: Circle CenterX=332.5 CenterY=120 CenterZ=0 NormalX=0 NormalY=0 NormalZ=1 AngleXU=0 Radius=1.25
    g12: Circle CenterX=332.5 CenterY=40 CenterZ=0 NormalX=0 NormalY=0 NormalZ=1 AngleXU=0 Radius=1.25
    g13: Circle CenterX=187.5 CenterY=5 CenterZ=0 NormalX=0 NormalY=0 NormalZ=1 AngleXU=0 Radius=1.75
  constraints (35):
    c: Tangent(g0,g4) = -1.5708
    c: Tangent(g0,g5) = -1.5708
    c: Tangent(g1,g5) = -1.5708
    c: Tangent(g1,g6) = -1.5708
    c: Tangent(g2,g6) = -1.5708
    c: Tangent(g2,g7) = -1.5708
    c: Tangent(g3,g7) = -1.5708
    c: Tangent(g3,g4) = -1.5708
    c: Horizontal(g0)
    c: Horizontal(g2)
    c: Vertical(g1)
    c: Vertical(g3)
    c: Equal(g4,g5)
    c: Equal(g5,g6)
    c: Equal(g6,g7)
    c: PointOnObject(g8,g0)
    c: PointOnObject(g8,g3)
    c: PointOnObject(g9,g1)
    c: PointOnObject(g9,g2)
    c: Coincident(g8,g-1)
    c: DistanceX(g9) = 375
    c: DistanceY(g9) = 229.5
    c: Radius(g5) = 1
    c: PointOnObject(g10,g0)
    c: Vertical(g10)
    c: DistanceX(g10) = 332.5
    c: DistanceY(g10) = 120
    c: Coincident(g11,g10)
    c: PointOnObject(g12,g10)
    c: Equal(g12,g11)
    c: DistanceY(g12) = 40
    c: Diameter(g11) = 2.5
    c: DistanceY(g13) = 5
    c: Diameter(g13) = 3.5
    c: DistanceX(g13) = 187.5
FEATURE [PartDesign::Pad] Pad011
  Direction = (0,0,1)
  Length = 1.5
  Length2 = 10
  Profile = -> Sketch014
  ReferenceAxis = -> Sketch014 [N_Axis]
  Refine = true
  Suppressed = false
  Type = 0
FEATURE [Sketcher::SketchObject] Sketch015
  ArcFitTolerance = 1e-06
  AttachmentSupport = -> [XY_Plane015]
  FullyConstrained = true
  MakeInternals = false
  MapMode = 5
  expr: Constraints[18] = <<choices>>.corner
  expr: Constraints[7] = <<choices>>.exit_w
  expr: Constraints[8] = <<components>>.frame_h
  sketch-geometry (8):
    g0: LineSegment StartX=0 StartY=0 StartZ=0 EndX=18 EndY=0 EndZ=0
    g1: LineSegment StartX=19 StartY=1 StartZ=0 EndX=19 EndY=228.5 EndZ=0
    g2: LineSegment StartX=18 StartY=229.5 StartZ=0 EndX=0 EndY=229.5 EndZ=0
    g3: LineSegment StartX=0 StartY=229.5 StartZ=0 EndX=0 EndY=0 EndZ=0
    g4: ArcOfCircle CenterX=18 CenterY=228.5 CenterZ=0 NormalX=0 NormalY=0 NormalZ=1 AngleXU=0 Radius=1 StartAngle=9.6e-15 EndAngle=1.5708
    g5: GeomPoint [constr] X=19 Y=229.5 Z=0
    g6: ArcOfCircle CenterX=18 CenterY=1 CenterZ=0 NormalX=0 NormalY=0 NormalZ=1 AngleXU=0 Radius=1 StartAngle=4.71239 EndAngle=6.28319
    g7: GeomPoint [constr] X=19 Y=0 Z=0
  constraints (19):
    c: Coincident(g2,g3)
    c: Coincident(g3,g0)
    c: Horizontal(g0)
    c: Horizontal(g2)
    c: Vertical(g1)
    c: Vertical(g3)
    c: Coincident(g0,g-1)
    c: DistanceX(g2,g5) = 19
    c: DistanceY(g7,g5) = 229.5
    c: PointOnObject(g5,g1)
    c: PointOnObject(g5,g2)
    c: Tangent(g1,g4) = -1.5708
    c: Tangent(g2,g4) = -1.5708
    c: PointOnObject(g7,g0)
    c: PointOnObject(g7,g1)
    c: Tangent(g0,g6) = -1.5708
    c: Tangent(g1,g6) = -1.5708
    c: Equal(g4,g6)
    c: Radius(g4) = 1
FEATURE [PartDesign::Pad] Pad012
  Direction = (0,0,1)
  Length = 55
  Length2 = 10
  Profile = -> Sketch015
  ReferenceAxis = -> Sketch015 [N_Axis]
  Refine = true
  Suppressed = false
  Type = 0
  expr: Length = <<choices>>.exit_height
FEATURE [Sketcher::SketchObject] Sketch016  label="motherboard standoffs"
  ArcFitTolerance = 1e-06
  AttachmentSupport = -> [XY_Plane013]
  FullyConstrained = false
  MakeInternals = false
  MapMode = 5
  expr: Constraints[10] = <<components>>.frame_w
  expr: Constraints[21] = <<choices>>.shroud_mb_space + <<components>>.fan_w + <<choices>>.exit_w
  expr: Constraints[42] = <<components>>.m3_threadhole
  expr: Constraints[51] = <<choices>>.mb_front_edge_gap
  expr: Constraints[57] = <<components>>.frame_w / 2
  expr: Constraints[62] = <<choices>>.screwhole_edge_margin
  expr: Constraints[63] = <<components>>.m3_hole
  expr: Constraints[9] = <<components>>.frame_h
  sketch-geometry (25):
    g0: LineSegment [constr] StartX=0 StartY=0 StartZ=0 EndX=375 EndY=0 EndZ=0
    g1: LineSegment [constr] StartX=375 StartY=0 StartZ=0 EndX=375 EndY=229.5 EndZ=0
    g2: LineSegment [constr] StartX=375 StartY=229.5 StartZ=0 EndX=0 EndY=229.5 EndZ=0
    g3: LineSegment [constr] StartX=0 StartY=229.5 StartZ=0 EndX=0 EndY=0 EndZ=0
    g4: LineSegment [constr] StartX=140 StartY=180 StartZ=0 EndX=140 EndY=10 EndZ=0
    g5: LineSegment [constr] StartX=140 StartY=10 StartZ=0 EndX=310 EndY=10 EndZ=0
    g6: LineSegment [constr] StartX=310 StartY=10 StartZ=0 EndX=310 EndY=180 EndZ=0
    g7: LineSegment [constr] StartX=310 StartY=180 StartZ=0 EndX=140 EndY=180 EndZ=0
    g8: LineSegment [constr] StartX=146.35 StartY=169.84 StartZ=0 EndX=146.35 EndY=14.8997 EndZ=0
    g9: LineSegment [constr] StartX=146.35 StartY=14.8997 StartZ=0 EndX=303.65 EndY=14.8997 EndZ=0
    g10: LineSegment [constr] StartX=303.65 StartY=14.8997 StartZ=0 EndX=303.65 EndY=146.98 EndZ=0
    g11: LineSegment [constr] StartX=303.65 StartY=146.98 StartZ=0 EndX=146.35 EndY=146.98 EndZ=0
    g12: Circle CenterX=146.35 CenterY=169.84 CenterZ=0 NormalX=0 NormalY=0 NormalZ=1 AngleXU=0 Radius=1.25
    g13: Circle CenterX=303.65 CenterY=146.98 CenterZ=0 NormalX=0 NormalY=0 NormalZ=1 AngleXU=0 Radius=1.25
    g14: Circle CenterX=303.65 CenterY=14.8997 CenterZ=0 NormalX=0 NormalY=0 NormalZ=1 AngleXU=0 Radius=1.25
    g15: Circle CenterX=146.35 CenterY=14.8997 CenterZ=0 NormalX=0 NormalY=0 NormalZ=1 AngleXU=0 Radius=1.25
    g16: Circle CenterX=146.35 CenterY=169.84 CenterZ=0 NormalX=0 NormalY=0 NormalZ=1 AngleXU=0 Radius=3.5
    g17: Circle CenterX=303.65 CenterY=146.98 CenterZ=0 NormalX=0 NormalY=0 NormalZ=1 AngleXU=0 Radius=3.5
    g18: Circle CenterX=303.65 CenterY=14.8997 CenterZ=0 NormalX=0 NormalY=0 NormalZ=1 AngleXU=0 Radius=3.5
    g19: Circle CenterX=146.35 CenterY=14.8997 CenterZ=0 NormalX=0 NormalY=0 NormalZ=1 AngleXU=0 Radius=3.5
    g20: Circle CenterX=187.5 CenterY=5 CenterZ=0 NormalX=0 NormalY=0 NormalZ=1 AngleXU=0 Radius=1.75
    g21: ArcOfCircle CenterX=187.5 CenterY=5 CenterZ=0 NormalX=0 NormalY=0 NormalZ=1 AngleXU=0 Radius=3.5 StartAngle=2e-16 EndAngle=3.14609
    g22: LineSegment StartX=191 StartY=5 StartZ=0 EndX=191 EndY=0 EndZ=0
    g23: LineSegment StartX=184 StartY=4.98426 StartZ=0 EndX=184.022 EndY=0 EndZ=0
    g24: LineSegment StartX=184.022 StartY=0 StartZ=0 EndX=191 EndY=0 EndZ=0
  constraints (64):
    c: Coincident(g0,g1)
    c: Coincident(g1,g2)
    c: Coincident(g2,g3)
    c: Coincident(g3,g0)
    c: Horizontal(g0)
    c: Horizontal(g2)
    c: Vertical(g1)
    c: Vertical(g3)
    c: Coincident(g0,g-1)
    c: DistanceY(g1,g1) = 229.5
    c: DistanceX(g2,g2) = 375
    c: Coincident(g4,g5)
    c: Coincident(g5,g6)
    c: Coincident(g6,g7)
    c: Coincident(g7,g4)
    c: Vertical(g4)
    c: Vertical(g6)
    c: Horizontal(g5)
    c: Horizontal(g7)
    c: Distance(g4,g6) = 170
    c: Distance(g5,g7) = 170
    c: Distance(g5,g1) = 65
    c: Vertical(g8)
    c: Coincident(g8,g9)
    c: Horizontal(g9)
    c: Coincident(g9,g10)
    c: Vertical(g10)
    c: Coincident(g10,g11)
    c: PointOnObject(g11,g8)
    c: Horizontal(g11)
    c: Distance(g8,g5) = 4.8997
    c: Distance(g8,g4) = 6.35
    c: Distance(g9,g6) = 6.35
    c: Distance(g8,g7) = 10.16
    c: Distance(g8,g11) = 22.86
    c: Coincident(g12,g8)
    c: Coincident(g13,g10)
    c: Coincident(g14,g9)
    c: Coincident(g15,g8)
    c: Equal(g12,g15)
    c: Equal(g15,g13)
    c: Equal(g13,g14)
    c: Diameter(g12) = 2.5
    c: Diameter(g16) = 7
    c: Coincident(g16,g8)
    c: Coincident(g17,g10)
    c: Coincident(g18,g9)
    c: Coincident(g19,g8)
    c: Equal(g18,g19)
    c: Equal(g19,g17)
    c: Equal(g17,g16)
    c: Distance(g4,g0) = 10
    c: Tangent(g21,g22) = 1.5708
    c: Tangent(g21,g23) = -1.5708
    c: Coincident(g21,g20)
    c: Vertical(g22)
    c: Equal(g19,g21)
    c: DistanceX(g20) = 187.5
    c: Coincident(g24,g23)
    c: Coincident(g24,g22)
    c: Horizontal(g24)
    c: PointOnObject(g23,g0)
    c: DistanceY(g20) = 5
    c: Diameter(g20) = 3.5
FEATURE [PartDesign::Pad] Pad013  label="mb_standoffs"
  BaseFeature = -> Pad011
  Direction = (0,0,1)
  Length = 7.25
  Length2 = 10
  Profile = -> Sketch016
  ReferenceAxis = -> Sketch016 [N_Axis]
  Refine = true
  Suppressed = false
  Type = 0
  expr: Length = <<choices>>.base_under_mb_thickness + 6
FEATURE [Sketcher::SketchObject] Sketch017
  ArcFitTolerance = 1e-06
  AttachmentSupport = -> [XY_Plane013]
  FullyConstrained = false
  MakeInternals = false
  MapMode = 5
  expr: Constraints[121] = <<choices>>.corner
  expr: Constraints[17] = <<components>>.fan_w + <<choices>>.exit_w + <<choices>>.shroud_mb_space + <<components>>.mb_w + 5
  expr: Constraints[31] = <<components>>.frame_h
  expr: Constraints[37] = <<choices>>.corner
  expr: Constraints[45] = <<choices>>.corner
  expr: Constraints[8] = <<components>>.frame_w
  expr: Constraints[9] = <<choices>>.mb_front_edge_gap + 170 + 5 + 3
  sketch-geometry (57):
    g0: LineSegment [constr] StartX=0 StartY=0 StartZ=0 EndX=375 EndY=0 EndZ=0
    g1: LineSegment [constr] StartX=375 StartY=0 StartZ=0 EndX=375 EndY=188 EndZ=0
    g2: LineSegment [constr] StartX=375 StartY=188 StartZ=0 EndX=0 EndY=188 EndZ=0
    g3: LineSegment [constr] StartX=0 StartY=188 StartZ=0 EndX=0 EndY=0 EndZ=0
    g4: LineSegment StartX=1 StartY=0 StartZ=0 EndX=374 EndY=0 EndZ=0
    g5: LineSegment StartX=375 StartY=1 StartZ=0 EndX=375 EndY=3 EndZ=0
    g6: LineSegment StartX=375 StartY=3 StartZ=0 EndX=135 EndY=3 EndZ=0
    g7: ArcOfCircle CenterX=1 CenterY=1 CenterZ=0 NormalX=0 NormalY=0 NormalZ=1 AngleXU=0 Radius=1 StartAngle=3.14159 EndAngle=4.71239
    g8: GeomPoint [constr] X=0 Y=0 Z=0
    g9: GeomPoint [constr] X=0 Y=188 Z=0
    g10: ArcOfCircle CenterX=374 CenterY=1 CenterZ=0 NormalX=0 NormalY=0 NormalZ=1 AngleXU=0 Radius=1 StartAngle=4.71239 EndAngle=6.28319
    g11: GeomPoint [constr] X=375 Y=0 Z=0
    g12: LineSegment StartX=375 StartY=228.5 StartZ=0 EndX=375 EndY=226.5 EndZ=0
    g13: LineSegment [constr] StartX=2 StartY=221.5 StartZ=0 EndX=2 EndY=192.907 EndZ=0
    g14: ArcOfCircle CenterX=1 CenterY=228.5 CenterZ=0 NormalX=0 NormalY=0 NormalZ=1 AngleXU=0 Radius=1 StartAngle=1.5708 EndAngle=3.14159
    g15: GeomPoint [constr] X=0 Y=229.5 Z=0
    g16: ArcOfCircle [constr] CenterX=7 CenterY=221.5 CenterZ=0 NormalX=0 NormalY=0 NormalZ=1 AngleXU=0 Radius=5 StartAngle=1.5708 EndAngle=3.14159
    g17: GeomPoint [constr] X=2 Y=226.5 Z=0
    g18: ArcOfCircle CenterX=374 CenterY=228.5 CenterZ=0 NormalX=0 NormalY=0 NormalZ=1 AngleXU=0 Radius=1 StartAngle=5.5e-15 EndAngle=1.5708
    g19: GeomPoint [constr] X=375 Y=229.5 Z=0
    g20: ArcOfCircle [constr] CenterX=7 CenterY=192.907 CenterZ=0 NormalX=0 NormalY=0 NormalZ=1 AngleXU=0 Radius=5 StartAngle=3.14159 EndAngle=4.90523
    g21: GeomPoint [constr] X=2 Y=188 Z=0
    g22: LineSegment StartX=313 StartY=226.5 StartZ=0 EndX=313 EndY=185 EndZ=0
    g23: LineSegment StartX=313 StartY=185 StartZ=0 EndX=310 EndY=185 EndZ=0
    g24: LineSegment StartX=310 StartY=185 StartZ=0 EndX=310 EndY=226.5 EndZ=0
    g25: LineSegment StartX=375 StartY=226.5 StartZ=0 EndX=313 EndY=226.5 EndZ=0
    g26: LineSegment [constr] StartX=313 StartY=226.5 StartZ=0 EndX=310 EndY=226.5 EndZ=0
    g27: LineSegment StartX=1 StartY=229.5 StartZ=0 EndX=308.406 EndY=229.5 EndZ=0
    g28: LineSegment [constr] StartX=308.406 StartY=229.5 StartZ=0 EndX=310 EndY=229.5 EndZ=0
    g29: LineSegment StartX=310 StartY=229.5 StartZ=0 EndX=374 EndY=229.5 EndZ=0
    g30: LineSegment [constr] StartX=310 StartY=226.5 StartZ=0 EndX=307.803 EndY=226.5 EndZ=0
    g31: LineSegment StartX=308.406 StartY=229.5 StartZ=0 EndX=307.803 EndY=226.5 EndZ=0
    g32: LineSegment StartX=310 StartY=229.5 StartZ=0 EndX=310 EndY=226.5 EndZ=0
    g33: LineSegment StartX=58 StartY=226.5 StartZ=0 EndX=7 EndY=226.5 EndZ=0
    g34: LineSegment StartX=307.803 StartY=226.5 StartZ=0 EndX=65 EndY=226.5 EndZ=0
    g35: LineSegment [constr] StartX=65 StartY=226.5 StartZ=0 EndX=63 EndY=226.5 EndZ=0
    g36: LineSegment StartX=58 StartY=188 StartZ=0 EndX=7.95824 EndY=188 EndZ=0
    g37: LineSegment StartX=135 StartY=188 StartZ=0 EndX=65 EndY=188 EndZ=0
    g38: LineSegment [constr] StartX=65 StartY=188 StartZ=0 EndX=63 EndY=188 EndZ=0
    g39: LineSegment StartX=63 StartY=221.5 StartZ=0 EndX=63 EndY=193 EndZ=0
    g40: LineSegment StartX=65 StartY=188 StartZ=0 EndX=65 EndY=226.5 EndZ=0
    g41: ArcOfCircle CenterX=58 CenterY=193 CenterZ=0 NormalX=0 NormalY=0 NormalZ=1 AngleXU=0 Radius=5 StartAngle=4.71239 EndAngle=6.28319
    g42: GeomPoint [constr] X=63 Y=188 Z=0
    g43: ArcOfCircle CenterX=58 CenterY=221.5 CenterZ=0 NormalX=0 NormalY=0 NormalZ=1 AngleXU=0 Radius=5 StartAngle=1.3e-15 EndAngle=1.5708
    g44: GeomPoint [constr] X=63 Y=226.5 Z=0
    g45: LineSegment StartX=135 StartY=3 StartZ=0 EndX=135 EndY=185 EndZ=0
    g46: LineSegment [constr] StartX=135 StartY=185 StartZ=0 EndX=135 EndY=188 EndZ=0
    g47: LineSegment StartX=135 StartY=188 StartZ=0 EndX=152 EndY=188 EndZ=0
    g48: LineSegment StartX=153 StartY=187 StartZ=0 EndX=153 EndY=185 EndZ=0
    g49: LineSegment StartX=153 StartY=185 StartZ=0 EndX=135 EndY=185 EndZ=0
    g50: ArcOfCircle CenterX=152 CenterY=187 CenterZ=0 NormalX=0 NormalY=0 NormalZ=1 AngleXU=0 Radius=1 StartAngle=1e-14 EndAngle=1.5708
    g51: GeomPoint [constr] X=153 Y=188 Z=0
    g52: LineSegment StartX=0 StartY=228.5 StartZ=0 EndX=0 EndY=226.5 EndZ=0
    g53: LineSegment [constr] StartX=0 StartY=226.5 StartZ=0 EndX=0 EndY=188 EndZ=0
    g54: LineSegment StartX=0 StartY=188 StartZ=0 EndX=-6e-16 EndY=1 EndZ=0
    g55: LineSegment StartX=0 StartY=226.5 StartZ=0 EndX=7 EndY=226.5 EndZ=0
    g56: LineSegment StartX=0 StartY=188 StartZ=0 EndX=7.95824 EndY=188 EndZ=0
  constraints (135):
    c: Coincident(g0,g1)
    c: Coincident(g2,g3)
    c: Coincident(g3,g0)
    c: Horizontal(g0)
    c: Horizontal(g2)
    c: Vertical(g1)
    c: Vertical(g3)
    c: Coincident(g0,g-1)
    c: DistanceX(g2,g2) = 375
    c: DistanceY(g1,g1) = 188
    c: Coincident(g9,g2)
    c: Coincident(g8,g0)
    c: Coincident(g11,g0)
    c: PointOnObject(g5,g1)
    c: Coincident(g5,g6)
    c: Horizontal(g6)
    c: Coincident(g6,g45)
    c: Distance(g6,g1) = 240
    c: PointOnObject(g8,g4)
    c: Tangent(g4,g7) = -1.5708
    c: Coincident(g54,g7) = -1.5708
    c: PointOnObject(g11,g5)
    c: PointOnObject(g11,g4)
    c: Tangent(g5,g10) = -1.5708
    c: Tangent(g4,g10) = -1.5708
    c: PointOnObject(g46,g2)
    c: Coincident(g37,g46)
    c: Radius(g10) = 1
    c: Coincident(g2,g1)
    c: DistanceY(g6) = 3
    c: DistanceX(g21) = 2
    c: DistanceY(g15) = 229.5
    c: Coincident(g12,g25)
    c: Vertical(g13)
    c: Coincident(g52,g14) = -1.5708
    c: Coincident(g27,g14) = 1.5708
    c: Equal(g14,g7)
    c: Radius(g7) = 1
    c: PointOnObject(g17,g13)
    c: Tangent(g13,g16) = -1.5708
    c: Vertical(g12)
    c: PointOnObject(g12,g1)
    c: PointOnObject(g19,g12)
    c: Coincident(g29,g18) = 1.5708
    c: Tangent(g12,g18) = 1.5708
    c: Radius(g18) = 1
    c: PointOnObject(g21,g13)
    c: Coincident(g36,g20) = 1.5708
    c: Tangent(g13,g20) = -1.5708
    c: Equal(g20,g16)
    c: Radius(g16) = 5
    c: Vertical(g22)
    c: Coincident(g22,g23)
    c: Horizontal(g23)
    c: Coincident(g23,g24)
    c: Vertical(g24)
    c: Coincident(g26,g30)
    c: Coincident(g25,g26)
    c: Horizontal(g25)
    c: Horizontal(g26)
    c: PointOnObject(g17,g25)
    c: Coincident(g25,g22)
    c: Coincident(g30,g24)
    c: Distance(g22,g1) = 62
    c: Distance(g46,g23) = 3
    c: DistanceX(g23,g23) = 3
    c: Coincident(g27,g28)
    c: Horizontal(g27)
    c: Distance(g17,g27) = 3
    c: PointOnObject(g15,g27)
    c: PointOnObject(g19,g27)
    c: Coincident(g28,g29)
    c: Horizontal(g28)
    c: Horizontal(g29)
    c: Coincident(g30,g34)
    c: Horizontal(g30)
    c: Coincident(g31,g27)
    c: Coincident(g31,g30)
    c: Coincident(g32,g28)
    c: Coincident(g32,g24)
    c: Vertical(g32)
    c: Coincident(g35,g44)
    c: Horizontal(g33)
    c: Coincident(g34,g35)
    c: Horizontal(g34)
    c: Horizontal(g35)
    c: Coincident(g38,g42)
    c: Horizontal(g36)
    c: Coincident(g37,g38)
    c: Horizontal(g37)
    c: Horizontal(g38)
    c: PointOnObject(g21,g37)
    c: Vertical(g39)
    c: Coincident(g40,g37)
    c: Coincident(g40,g34)
    c: Vertical(g40)
    c: Distance(g42,g40) = 2
    c: DistanceX(g34) = 65
    c: PointOnObject(g42,g36)
    c: PointOnObject(g42,g39)
    c: Tangent(g36,g41) = 1.5708
    c: Tangent(g39,g41) = 1.5708
    c: PointOnObject(g44,g39)
    c: Tangent(g39,g43) = 1.5708
    c: Equal(g16,g43)
    c: Equal(g43,g41)
    c: Coincident(g45,g46)
    c: Vertical(g45)
    c: Vertical(g46)
    c: Coincident(g37,g47)
    c: PointOnObject(g51,g2)
    c: Vertical(g48)
    c: Coincident(g48,g49)
    c: Coincident(g49,g45)
    c: Horizontal(g49)
    c: DistanceY(g48,g51) = 3
    c: DistanceX(g47,g51) = 18
    c: PointOnObject(g51,g47)
    c: PointOnObject(g51,g48)
    c: Tangent(g47,g50) = 1.5708
    c: Tangent(g48,g50) = 1.5708
    c: Radius(g50) = 1
    c: Tangent(g43,g33) = -1.5708
    c: Tangent(g16,g33) = -1.5708
    c: Distance(g16,g27) = 3
    c: Coincident(g52,g53)
    c: PointOnObject(g8,g52)
    c: PointOnObject(g9,g52)
    c: PointOnObject(g15,g52)
    c: Coincident(g53,g54)
    c: Coincident(g55,g52)
    c: Tangent(g55,g16) = 1.5708
    c: Coincident(g56,g53)
    c: Coincident(g56,g20)
    c: Horizontal(g56)
FEATURE [PartDesign::Pad] Pad014  label="thick_area"
  BaseFeature = -> Pad013
  Direction = (0,0,1)
  Length = 20
  Length2 = 10
  Profile = -> Sketch017
  ReferenceAxis = -> Sketch017 [N_Axis]
  Refine = true
  Suppressed = false
  Type = 0
  expr: Length = <<choices>>.base_max_thickness
FEATURE [Sketcher::SketchObject] Sketch018
  ArcFitTolerance = 1e-06
  AttachmentSupport = -> [XY_Plane013]
  FullyConstrained = true
  MakeInternals = false
  MapMode = 5
  expr: Constraints[30] = <<components>>.m3_hole
  expr: Constraints[31] = <<choices>>.psu_left_gap
  sketch-geometry (14):
    g0: LineSegment [constr] StartX=60 StartY=183 StartZ=0 EndX=5 EndY=183 EndZ=0
    g1: LineSegment [constr] StartX=5 StartY=183 StartZ=0 EndX=5 EndY=13 EndZ=0
    g2: LineSegment [constr] StartX=5 StartY=13 StartZ=0 EndX=60 EndY=13 EndZ=0
    g3: LineSegment [constr] StartX=60 StartY=13 StartZ=0 EndX=60 EndY=183 EndZ=0
    g4: GeomPoint [constr] X=32.5 Y=98 Z=0
    g5: LineSegment [constr] StartX=49.15 StartY=170 StartZ=0 EndX=15.85 EndY=170 EndZ=0
    g6: LineSegment [constr] StartX=15.85 StartY=170 StartZ=0 EndX=15.85 EndY=26 EndZ=0
    g7: LineSegment [constr] StartX=15.85 StartY=26 StartZ=0 EndX=49.15 EndY=26 EndZ=0
    g8: LineSegment [constr] StartX=49.15 StartY=26 StartZ=0 EndX=49.15 EndY=170 EndZ=0
    g9: GeomPoint [constr] X=32.5 Y=98 Z=0
    g10: Circle CenterX=15.85 CenterY=170 CenterZ=0 NormalX=0 NormalY=0 NormalZ=1 AngleXU=0 Radius=1.75
    g11: Circle CenterX=49.15 CenterY=170 CenterZ=0 NormalX=0 NormalY=0 NormalZ=1 AngleXU=0 Radius=1.75
    g12: Circle CenterX=15.85 CenterY=26 CenterZ=0 NormalX=0 NormalY=0 NormalZ=1 AngleXU=0 Radius=1.75
    g13: Circle CenterX=49.15 CenterY=26 CenterZ=0 NormalX=0 NormalY=0 NormalZ=1 AngleXU=0 Radius=1.75
  constraints (33):
    c: Coincident(g0,g1)
    c: Coincident(g1,g2)
    c: Coincident(g2,g3)
    c: Coincident(g3,g0)
    c: Horizontal(g0)
    c: Horizontal(g2)
    c: Vertical(g1)
    c: Vertical(g3)
    c: Symmetric(g2,g0,g4)
    c: Coincident(g5,g6)
    c: Coincident(g6,g7)
    c: Coincident(g7,g8)
    c: Coincident(g8,g5)
    c: Horizontal(g5)
    c: Horizontal(g7)
    c: Vertical(g6)
    c: Vertical(g8)
    c: Symmetric(g7,g5,g9)
    c: Coincident(g9,g4)
    c: DistanceX(g5,g5) = 33.3
    c: DistanceY(g6,g6) = 144
    c: DistanceY(g1,g1) = 170
    c: DistanceX(g0,g0) = 55
    c: Coincident(g10,g5)
    c: Coincident(g11,g5)
    c: Coincident(g12,g6)
    c: Coincident(g13,g7)
    c: Equal(g10,g11)
    c: Equal(g11,g12)
    c: Equal(g12,g13)
    c: Diameter(g10) = 3.5
    c: DistanceX(g-2,g1) = 5
    c: DistanceY(g1) = 13
FEATURE [PartDesign::Pocket] Pocket004  label="psu_mounts"
  BaseFeature = -> Pad014
  Direction = (0,0,-1)
  Length = 5
  Length2 = 5
  Profile = -> Sketch018
  ReferenceAxis = -> Sketch018 [N_Axis]
  Refine = true
  Reversed = true
  Suppressed = false
  Type = 1
FEATURE [Sketcher::SketchObject] Sketch019
  ArcFitTolerance = 1e-06
  AttachmentSupport = -> [XY_Plane013]
  FullyConstrained = true
  MakeInternals = false
  MapMode = 5
  expr: Constraints[10] = <<components>>.frame_h
  expr: Constraints[20] = <<choices>>.mb_front_edge_gap + 170 + 5 + 3
  expr: Constraints[21] = <<choices>>.exit_w + <<components>>.fan_w + <<choices>>.shroud_mb_space
  expr: Constraints[9] = <<components>>.frame_w
  sketch-geometry (8):
    g0: LineSegment [constr] StartX=0 StartY=0 StartZ=0 EndX=375 EndY=0 EndZ=0
    g1: LineSegment [constr] StartX=375 StartY=0 StartZ=0 EndX=375 EndY=229.5 EndZ=0
    g2: LineSegment [constr] StartX=375 StartY=229.5 StartZ=0 EndX=0 EndY=229.5 EndZ=0
    g3: LineSegment [constr] StartX=0 StartY=229.5 StartZ=0 EndX=0 EndY=0 EndZ=0
    g4: LineSegment StartX=65 StartY=188 StartZ=0 EndX=310 EndY=188 EndZ=0
    g5: LineSegment StartX=310 StartY=188 StartZ=0 EndX=310 EndY=229.5 EndZ=0
    g6: LineSegment StartX=310 StartY=229.5 StartZ=0 EndX=65 EndY=229.5 EndZ=0
    g7: LineSegment StartX=65 StartY=229.5 StartZ=0 EndX=65 EndY=188 EndZ=0
  constraints (23):
    c: Coincident(g0,g1)
    c: Coincident(g1,g2)
    c: Coincident(g2,g3)
    c: Coincident(g3,g0)
    c: Horizontal(g0)
    c: Horizontal(g2)
    c: Vertical(g1)
    c: Vertical(g3)
    c: Coincident(g0,g-1)
    c: DistanceX(g2,g2) = 375
    c: DistanceY(g1,g1) = 229.5
    c: Coincident(g4,g5)
    c: Coincident(g5,g6)
    c: Coincident(g6,g7)
    c: Coincident(g7,g4)
    c: Horizontal(g4)
    c: Horizontal(g6)
    c: Vertical(g5)
    c: Vertical(g7)
    c: PointOnObject(g5,g2)
    c: Distance(g4,g0) = 188
    c: Distance(g4,g1) = 65
    c: DistanceX(g6) = 65
FEATURE [PartDesign::Pocket] Pocket005  label="back_hole"
  BaseFeature = -> Pocket004
  Direction = (0,0,-1)
  Length = 5
  Length2 = 5
  Profile = -> Sketch019
  ReferenceAxis = -> Sketch019 [N_Axis]
  Refine = true
  Reversed = true
  Suppressed = false
  Type = 1
FEATURE [Sketcher::SketchObject] Sketch020
  ArcFitTolerance = 1e-06
  AttachmentSupport = -> [XY_Plane013]
  FullyConstrained = false
  MakeInternals = false
  MapMode = 5
  expr: Constraints[20] = <<choices>>.fin_gap
  expr: Constraints[21] = <<choices>>.fin_end
  expr: Constraints[9] = <<components>>.frame_h
  sketch-geometry (8):
    g0: LineSegment [constr] StartX=0 StartY=0 StartZ=0 EndX=125.373 EndY=0 EndZ=0
    g1: LineSegment [constr] StartX=125.373 StartY=0 StartZ=0 EndX=125.373 EndY=229.5 EndZ=0
    g2: LineSegment [constr] StartX=125.373 StartY=229.5 StartZ=0 EndX=0 EndY=229.5 EndZ=0
    g3: LineSegment [constr] StartX=0 StartY=229.5 StartZ=0 EndX=0 EndY=0 EndZ=0
    g4: LineSegment StartX=0 StartY=3 StartZ=0 EndX=125.373 EndY=3 EndZ=0
    g5: LineSegment StartX=125.373 StartY=3 StartZ=0 EndX=125.373 EndY=9 EndZ=0
    g6: LineSegment StartX=125.373 StartY=9 StartZ=0 EndX=0 EndY=9 EndZ=0
    g7: LineSegment StartX=0 StartY=9 StartZ=0 EndX=0 EndY=3 EndZ=0
  constraints (22):
    c: Coincident(g0,g1)
    c: Coincident(g1,g2)
    c: Coincident(g2,g3)
    c: Coincident(g3,g0)
    c: Horizontal(g0)
    c: Horizontal(g2)
    c: Vertical(g1)
    c: Vertical(g3)
    c: Coincident(g0,g-1)
    c: DistanceY(g1,g1) = 229.5
    c: Coincident(g4,g5)
    c: Coincident(g5,g6)
    c: Coincident(g6,g7)
    c: Coincident(g7,g4)
    c: Horizontal(g4)
    c: Horizontal(g6)
    c: Vertical(g5)
    c: Vertical(g7)
    c: PointOnObject(g4,g3)
    c: PointOnObject(g5,g1)
    c: DistanceY(g5,g5) = 6
    c: Distance(g4,g0) = 3
FEATURE [PartDesign::Pocket] Pocket006
  BaseFeature = -> Pocket005
  Direction = (0,0,-1)
  Length = 18
  Length2 = 5
  Profile = -> Sketch020
  ReferenceAxis = -> Sketch020 [N_Axis]
  Refine = true
  Reversed = true
  Suppressed = false
  Type = 0
  expr: Length = <<choices>>.base_max_thickness - 2
FEATURE [PartDesign::Plane] DatumPlane001  label="just_above_base_thinnest"
  AttachmentOffset = pos=(0,0,2) rot=(0,0,1;0rad)
  AttachmentSupport = -> [XY_Plane013]
  Length = 463.812
  MapMode = 5
  Placement = pos=(0,0,2) rot=(0,0,1;0rad)
  ResizeMode = 0
  Width = 318.312
FEATURE [Sketcher::SketchObject] Sketch021
  ArcFitTolerance = 1e-06
  AttachmentSupport = -> [DatumPlane001]
  FullyConstrained = true
  MakeInternals = false
  MapMode = 5
  Placement = pos=(0,0,2) rot=(0,0,1;0rad)
  expr: Constraints[19] = <<choices>>.fin_gap
  expr: Constraints[20] = <<choices>>.fin_end
  expr: Constraints[21] = <<choices>>.psu_left_gap + <<components>>.psu_w
  expr: Constraints[22] = <<components>>.frame_w - <<components>>.fan_w - <<choices>>.exit_w - <<choices>>.shroud_mb_space - 170 - 5
  expr: Constraints[9] = <<components>>.frame_h
  sketch-geometry (8):
    g0: LineSegment [constr] StartX=0 StartY=0 StartZ=0 EndX=135 EndY=0 EndZ=0
    g1: LineSegment [constr] StartX=135 StartY=0 StartZ=0 EndX=135 EndY=229.5 EndZ=0
    g2: LineSegment [constr] StartX=135 StartY=229.5 StartZ=0 EndX=0 EndY=229.5 EndZ=0
    g3: LineSegment [constr] StartX=0 StartY=229.5 StartZ=0 EndX=0 EndY=0 EndZ=0
    g4: LineSegment StartX=60 StartY=3 StartZ=0 EndX=135 EndY=3 EndZ=0
    g5: LineSegment StartX=135 StartY=3 StartZ=0 EndX=135 EndY=9 EndZ=0
    g6: LineSegment StartX=135 StartY=9 StartZ=0 EndX=60 EndY=9 EndZ=0
    g7: LineSegment StartX=60 StartY=9 StartZ=0 EndX=60 EndY=3 EndZ=0
  constraints (23):
    c: Coincident(g0,g1)
    c: Coincident(g1,g2)
    c: Coincident(g2,g3)
    c: Coincident(g3,g0)
    c: Horizontal(g0)
    c: Horizontal(g2)
    c: Vertical(g1)
    c: Vertical(g3)
    c: Coincident(g0,g-1)
    c: DistanceY(g1,g1) = 229.5
    c: Coincident(g4,g5)
    c: Coincident(g5,g6)
    c: Coincident(g6,g7)
    c: Coincident(g7,g4)
    c: Horizontal(g4)
    c: Horizontal(g6)
    c: Vertical(g5)
    c: Vertical(g7)
    c: PointOnObject(g5,g1)
    c: DistanceY(g5,g5) = 6
    c: Distance(g4,g0) = 3
    c: Distance(g4,g3) = 60
    c: DistanceX(g0) = 135
FEATURE [PartDesign::Pocket] Pocket007
  BaseFeature = -> Pocket006
  Direction = (0,0,-1)
  Length = 5
  Length2 = 5
  Profile = -> Sketch021
  ReferenceAxis = -> Sketch021 [N_Axis]
  Refine = true
  Reversed = true
  Suppressed = false
  Type = 1
FEATURE [PartDesign::LinearPattern] LinearPattern
  BaseFeature = -> Pocket007
  Direction = -> Sketch020 [V_Axis]
  Length = 176
  Mode = 1
  Occurrences = 23
  Offset = 8
  Originals = -> [Pocket006,Pocket007]
  Refine = true
  Suppressed = false
  TransformMode = 0
  expr: Occurrences = <<choices>>.fin_count + 1
  expr: Offset = <<choices>>.fin_thick + <<choices>>.fin_gap
FEATURE [Sketcher::SketchObject] Sketch022
  ArcFitTolerance = 1e-06
  AttachmentSupport = -> [YZ_Plane015]
  FullyConstrained = true
  MakeInternals = false
  MapMode = 5
  Placement = pos=(0,0,0) rot=(0.57735,0.57735,0.57735;2.0944rad)
  expr: Constraints[21] = <<components>>.frame_h
  expr: Constraints[9] = <<choices>>.base_max_thickness - 3
  sketch-geometry (8):
    g0: LineSegment StartX=0 StartY=0 StartZ=0 EndX=3 EndY=0 EndZ=0
    g1: LineSegment StartX=3 StartY=0 StartZ=0 EndX=3 EndY=17 EndZ=0
    g2: LineSegment StartX=3 StartY=17 StartZ=0 EndX=0 EndY=17 EndZ=0
    g3: LineSegment StartX=0 StartY=17 StartZ=0 EndX=0 EndY=0 EndZ=0
    g4: LineSegment StartX=226.5 StartY=0 StartZ=0 EndX=229.5 EndY=0 EndZ=0
    g5: LineSegment StartX=229.5 StartY=0 StartZ=0 EndX=229.5 EndY=17 EndZ=0
    g6: LineSegment StartX=229.5 StartY=17 StartZ=0 EndX=226.5 EndY=17 EndZ=0
    g7: LineSegment StartX=226.5 StartY=17 StartZ=0 EndX=226.5 EndY=0 EndZ=0
  constraints (23):
    c: Coincident(g0,g1)
    c: Coincident(g1,g2)
    c: Coincident(g2,g3)
    c: Coincident(g3,g0)
    c: Horizontal(g0)
    c: Horizontal(g2)
    c: Vertical(g1)
    c: Vertical(g3)
    c: Distance(g1,g3) = 3
    c: Distance(g0,g2) = 17
    c: Coincident(g0,g-1)
    c: Coincident(g4,g5)
    c: Coincident(g5,g6)
    c: Coincident(g6,g7)
    c: Coincident(g7,g4)
    c: Horizontal(g4)
    c: Horizontal(g6)
    c: Vertical(g5)
    c: Vertical(g7)
    c: Distance(g5,g7) = 3
    c: PointOnObject(g4,g-1)
    c: DistanceX(g4) = 229.5
    c: PointOnObject(g6,g2)
FEATURE [PartDesign::Plane] DatumPlane002
  AttachmentOffset = pos=(0,0,19) rot=(0,0,1;0rad)
  AttachmentSupport = -> [YZ_Plane015]
  Length = 283.038
  MapMode = 5
  Placement = pos=(19,0,0) rot=(0.57735,0.57735,0.57735;2.0944rad)
  ResizeMode = 0
  Width = 108.538
  expr: .AttachmentOffset.Base.z = <<choices>>.exit_w
FEATURE [Sketcher::SketchObject] Sketch023
  ArcFitTolerance = 1e-06
  AttachmentSupport = -> [YZ_Plane015]
  FullyConstrained = true
  MakeInternals = false
  MapMode = 5
  Placement = pos=(0,0,0) rot=(0.57735,0.57735,0.57735;2.0944rad)
  expr: Constraints[104] = <<components>>.fan_spacing
  expr: Constraints[10] = <<choices>>.exit_height
  expr: Constraints[136] = <<components>>.m3_hole
  expr: Constraints[137] = <<choices>>.fan_gap
  expr: Constraints[138] = <<choices>>.fan_gap
  expr: Constraints[139] = <<choices>>.fan_gap
  expr: Constraints[21] = <<choices>>.exit_height
  expr: Constraints[32] = <<choices>>.exit_height
  expr: Constraints[43] = <<choices>>.exit_height
  expr: Constraints[56] = <<choices>>.exit_fan_dia
  sketch-geometry (60):
    g0: LineSegment [constr] StartX=4 StartY=0 StartZ=0 EndX=54 EndY=0 EndZ=0
    g1: LineSegment [constr] StartX=54 StartY=0 StartZ=0 EndX=54 EndY=55 EndZ=0
    g2: LineSegment [constr] StartX=54 StartY=55 StartZ=0 EndX=4 EndY=55 EndZ=0
    g3: LineSegment [constr] StartX=4 StartY=55 StartZ=0 EndX=4 EndY=0 EndZ=0
    g4: GeomPoint [constr] X=29 Y=27.5 Z=0
    g5: LineSegment [constr] StartX=56 StartY=0 StartZ=0 EndX=106 EndY=0 EndZ=0
    g6: LineSegment [constr] StartX=106 StartY=0 StartZ=0 EndX=106 EndY=55 EndZ=0
    g7: LineSegment [constr] StartX=106 StartY=55 StartZ=0 EndX=56 EndY=55 EndZ=0
    g8: LineSegment [constr] StartX=56 StartY=55 StartZ=0 EndX=56 EndY=0 EndZ=0
    g9: GeomPoint [constr] X=81 Y=27.5 Z=0
    g10: LineSegment [constr] StartX=108 StartY=0 StartZ=0 EndX=158 EndY=0 EndZ=0
    g11: LineSegment [constr] StartX=158 StartY=0 StartZ=0 EndX=158 EndY=55 EndZ=0
    g12: LineSegment [constr] StartX=158 StartY=55 StartZ=0 EndX=108 EndY=55 EndZ=0
    g13: LineSegment [constr] StartX=108 StartY=55 StartZ=0 EndX=108 EndY=0 EndZ=0
    g14: GeomPoint [constr] X=133 Y=27.5 Z=0
    g15: LineSegment [constr] StartX=160 StartY=0 StartZ=0 EndX=210 EndY=0 EndZ=0
    g16: LineSegment [constr] StartX=210 StartY=0 StartZ=0 EndX=210 EndY=55 EndZ=0
    g17: LineSegment [constr] StartX=210 StartY=55 StartZ=0 EndX=160 EndY=55 EndZ=0
    g18: LineSegment [constr] StartX=160 StartY=55 StartZ=0 EndX=160 EndY=0 EndZ=0
    g19: GeomPoint [constr] X=185 Y=27.5 Z=0
    g20: Circle CenterX=29 CenterY=27.5 CenterZ=0 NormalX=0 NormalY=0 NormalZ=1 AngleXU=0 Radius=24.5
    g21: Circle CenterX=81 CenterY=27.5 CenterZ=0 NormalX=0 NormalY=0 NormalZ=1 AngleXU=0 Radius=24.5
    g22: Circle CenterX=133 CenterY=27.5 CenterZ=0 NormalX=0 NormalY=0 NormalZ=1 AngleXU=0 Radius=24.5
    g23: Circle CenterX=185 CenterY=27.5 CenterZ=0 NormalX=0 NormalY=0 NormalZ=1 AngleXU=0 Radius=24.5
    g24: LineSegment [constr] StartX=49 StartY=7.5 StartZ=0 EndX=49 EndY=47.5 EndZ=0
    g25: LineSegment [constr] StartX=49 StartY=47.5 StartZ=0 EndX=9 EndY=47.5 EndZ=0
    g26: LineSegment [constr] StartX=9 StartY=47.5 StartZ=0 EndX=9 EndY=7.5 EndZ=0
    g27: LineSegment [constr] StartX=9 StartY=7.5 StartZ=0 EndX=49 EndY=7.5 EndZ=0
    g28: GeomPoint [constr] X=29 Y=27.5 Z=0
    g29: LineSegment [constr] StartX=101 StartY=7.5 StartZ=0 EndX=101 EndY=47.5 EndZ=0
    g30: LineSegment [constr] StartX=101 StartY=47.5 StartZ=0 EndX=61 EndY=47.5 EndZ=0
    g31: LineSegment [constr] StartX=61 StartY=47.5 StartZ=0 EndX=61 EndY=7.5 EndZ=0
    g32: LineSegment [constr] StartX=61 StartY=7.5 StartZ=0 EndX=101 EndY=7.5 EndZ=0
    g33: GeomPoint [constr] X=81 Y=27.5 Z=0
    g34: LineSegment [constr] StartX=153 StartY=7.5 StartZ=0 EndX=153 EndY=47.5 EndZ=0
    g35: LineSegment [constr] StartX=153 StartY=47.5 StartZ=0 EndX=113 EndY=47.5 EndZ=0
    g36: LineSegment [constr] StartX=113 StartY=47.5 StartZ=0 EndX=113 EndY=7.5 EndZ=0
    g37: LineSegment [constr] StartX=113 StartY=7.5 StartZ=0 EndX=153 EndY=7.5 EndZ=0
    g38: GeomPoint [constr] X=133 Y=27.5 Z=0
    g39: LineSegment [constr] StartX=205 StartY=7.5 StartZ=0 EndX=205 EndY=47.5 EndZ=0
    g40: LineSegment [constr] StartX=205 StartY=47.5 StartZ=0 EndX=165 EndY=47.5 EndZ=0
    g41: LineSegment [constr] StartX=165 StartY=47.5 StartZ=0 EndX=165 EndY=7.5 EndZ=0
    g42: LineSegment [constr] StartX=165 StartY=7.5 StartZ=0 EndX=205 EndY=7.5 EndZ=0
    g43: GeomPoint [constr] X=185 Y=27.5 Z=0
    g44: Circle [constr] CenterX=9 CenterY=47.5 CenterZ=0 NormalX=0 NormalY=0 NormalZ=1 AngleXU=0 Radius=1.75
    g45: Circle [constr] CenterX=49 CenterY=47.5 CenterZ=0 NormalX=0 NormalY=0 NormalZ=1 AngleXU=0 Radius=1.75
    g46: Circle [constr] CenterX=61 CenterY=47.5 CenterZ=0 NormalX=0 NormalY=0 NormalZ=1 AngleXU=0 Radius=1.75
    g47: Circle [constr] CenterX=9 CenterY=7.5 CenterZ=0 NormalX=0 NormalY=0 NormalZ=1 AngleXU=0 Radius=1.75
    g48: Circle [constr] CenterX=49 CenterY=7.5 CenterZ=0 NormalX=0 NormalY=0 NormalZ=1 AngleXU=0 Radius=1.75
    g49: Circle [constr] CenterX=61 CenterY=7.5 CenterZ=0 NormalX=0 NormalY=0 NormalZ=1 AngleXU=0 Radius=1.75
    g50: Circle [constr] CenterX=101 CenterY=7.5 CenterZ=0 NormalX=0 NormalY=0 NormalZ=1 AngleXU=0 Radius=1.75
    g51: Circle [constr] CenterX=113 CenterY=7.5 CenterZ=0 NormalX=0 NormalY=0 NormalZ=1 AngleXU=0 Radius=1.75
    g52: Circle [constr] CenterX=153 CenterY=7.5 CenterZ=0 NormalX=0 NormalY=0 NormalZ=1 AngleXU=0 Radius=1.75
    g53: Circle [constr] CenterX=165 CenterY=7.5 CenterZ=0 NormalX=0 NormalY=0 NormalZ=1 AngleXU=0 Radius=1.75
    g54: Circle [constr] CenterX=205 CenterY=7.5 CenterZ=0 NormalX=0 NormalY=0 NormalZ=1 AngleXU=0 Radius=1.75
    g55: Circle [constr] CenterX=205 CenterY=47.5 CenterZ=0 NormalX=0 NormalY=0 NormalZ=1 AngleXU=0 Radius=1.75
    g56: Circle [constr] CenterX=165 CenterY=47.5 CenterZ=0 NormalX=0 NormalY=0 NormalZ=1 AngleXU=0 Radius=1.75
    g57: Circle [constr] CenterX=153 CenterY=47.5 CenterZ=0 NormalX=0 NormalY=0 NormalZ=1 AngleXU=0 Radius=1.75
    g58: Circle [constr] CenterX=113 CenterY=47.5 CenterZ=0 NormalX=0 NormalY=0 NormalZ=1 AngleXU=0 Radius=1.75
    g59: Circle [constr] CenterX=101 CenterY=47.5 CenterZ=0 NormalX=0 NormalY=0 NormalZ=1 AngleXU=0 Radius=1.75
  constraints (140):
    c: Coincident(g0,g1)
    c: Coincident(g1,g2)
    c: Coincident(g2,g3)
    c: Coincident(g3,g0)
    c: Horizontal(g0)
    c: Horizontal(g2)
    c: Vertical(g1)
    c: Vertical(g3)
    c: Symmetric(g2,g0,g4)
    c: Distance(g1,g3) = 50
    c: Distance(g0,g2) = 55
    c: Coincident(g5,g6)
    c: Coincident(g6,g7)
    c: Coincident(g7,g8)
    c: Coincident(g8,g5)
    c: Horizontal(g5)
    c: Horizontal(g7)
    c: Vertical(g6)
    c: Vertical(g8)
    c: Symmetric(g7,g5,g9)
    c: Distance(g6,g8) = 50
    c: Distance(g5,g7) = 55
    c: Coincident(g10,g11)
    c: Coincident(g11,g12)
    c: Coincident(g12,g13)
    c: Coincident(g13,g10)
    c: Horizontal(g10)
    c: Horizontal(g12)
    c: Vertical(g11)
    c: Vertical(g13)
    c: Symmetric(g12,g10,g14)
    c: Distance(g11,g13) = 50
    c: Distance(g10,g12) = 55
    c: Coincident(g15,g16)
    c: Coincident(g16,g17)
    c: Coincident(g17,g18)
    c: Coincident(g18,g15)
    c: Horizontal(g15)
    c: Horizontal(g17)
    c: Vertical(g16)
    c: Vertical(g18)
    c: Symmetric(g17,g15,g19)
    c: Distance(g16,g18) = 50
    c: Distance(g15,g17) = 55
    c: PointOnObject(g0,g-1)
    c: PointOnObject(g5,g-1)
    c: PointOnObject(g10,g-1)
    c: PointOnObject(g15,g-1)
    c: DistanceX(g0) = 4
    c: Coincident(g20,g4)
    c: Coincident(g21,g9)
    c: Coincident(g22,g14)
    c: Coincident(g23,g19)
    c: Equal(g23,g22)
    c: Equal(g22,g21)
    c: Equal(g21,g20)
    c: Diameter(g20) = 49
    c: Coincident(g24,g25)
    c: Coincident(g25,g26)
    c: Coincident(g26,g27)
    c: Coincident(g27,g24)
    c: Vertical(g24)
    c: Vertical(g26)
    c: Horizontal(g25)
    c: Horizontal(g27)
    c: Symmetric(g26,g24,g28)
    c: Coincident(g28,g4)
    c: Coincident(g29,g30)
    c: Coincident(g30,g31)
    c: Coincident(g31,g32)
    c: Coincident(g32,g29)
    c: Vertical(g29)
    c: Vertical(g31)
    c: Horizontal(g30)
    c: Horizontal(g32)
    c: Symmetric(g31,g29,g33)
    c: Coincident(g33,g9)
    c: Coincident(g34,g35)
    c: Coincident(g35,g36)
    c: Coincident(g36,g37)
    c: Coincident(g37,g34)
    c: Vertical(g34)
    c: Vertical(g36)
    c: Horizontal(g35)
    c: Horizontal(g37)
    c: Symmetric(g36,g34,g38)
    c: Coincident(g38,g14)
    c: Coincident(g39,g40)
    c: Coincident(g40,g41)
    c: Coincident(g41,g42)
    c: Coincident(g42,g39)
    c: Vertical(g39)
    c: Vertical(g41)
    c: Horizontal(g40)
    c: Horizontal(g42)
    c: Symmetric(g41,g39,g43)
    c: Coincident(g43,g19)
    c: Equal(g40,g39)
    c: Equal(g39,g35)
    c: Equal(g35,g34)
    c: Equal(g34,g30)
    c: Equal(g30,g29)
    c: Equal(g29,g25)
    c: Equal(g25,g24)
    c: DistanceX(g25,g25) = 40
    c: Coincident(g44,g25)
    c: Coincident(g45,g24)
    c: Coincident(g46,g30)
    c: Coincident(g47,g26)
    c: Coincident(g48,g24)
    c: Coincident(g49,g31)
    c: Coincident(g50,g29)
    c: Coincident(g51,g36)
    c: Coincident(g52,g34)
    c: Coincident(g53,g41)
    c: Coincident(g54,g39)
    c: Coincident(g55,g39)
    c: Coincident(g56,g40)
    c: Coincident(g57,g34)
    c: Coincident(g58,g35)
    c: Coincident(g59,g29)
    c: Equal(g44,g45)
    c: Equal(g45,g46)
    c: Equal(g46,g47)
    c: Equal(g47,g48)
    c: Equal(g48,g49)
    c: Equal(g49,g50)
    c: Equal(g50,g51)
    c: Equal(g51,g52)
    c: Equal(g52,g53)
    c: Equal(g53,g54)
    c: Equal(g54,g55)
    c: Equal(g55,g56)
    c: Equal(g56,g57)
    c: Equal(g57,g58)
    c: Equal(g58,g59)
    c: Diameter(g47) = 3.5
    c: Distance(g1,g8) = 2
    c: Distance(g6,g13) = 2
    c: Distance(g11,g18) = 2
FEATURE [Sketcher::SketchObject] Sketch024  label="fanholes"
  ArcFitTolerance = 1e-06
  AttachmentSupport = -> [YZ_Plane015]
  FullyConstrained = true
  MakeInternals = false
  MapMode = 5
  Placement = pos=(0,0,0) rot=(0.57735,0.57735,0.57735;2.0944rad)
  expr: Constraints[104] = <<components>>.fan_spacing
  expr: Constraints[10] = <<choices>>.exit_height
  expr: Constraints[137] = <<choices>>.fan_gap
  expr: Constraints[138] = <<choices>>.fan_gap
  expr: Constraints[139] = <<choices>>.fan_gap
  expr: Constraints[21] = <<choices>>.exit_height
  expr: Constraints[32] = <<choices>>.exit_height
  expr: Constraints[43] = <<choices>>.exit_height
  expr: Constraints[56] = <<choices>>.exit_fan_dia
  sketch-geometry (60):
    g0: LineSegment [constr] StartX=4 StartY=0 StartZ=0 EndX=54 EndY=0 EndZ=0
    g1: LineSegment [constr] StartX=54 StartY=0 StartZ=0 EndX=54 EndY=55 EndZ=0
    g2: LineSegment [constr] StartX=54 StartY=55 StartZ=0 EndX=4 EndY=55 EndZ=0
    g3: LineSegment [constr] StartX=4 StartY=55 StartZ=0 EndX=4 EndY=0 EndZ=0
    g4: GeomPoint [constr] X=29 Y=27.5 Z=0
    g5: LineSegment [constr] StartX=56 StartY=0 StartZ=0 EndX=106 EndY=0 EndZ=0
    g6: LineSegment [constr] StartX=106 StartY=0 StartZ=0 EndX=106 EndY=55 EndZ=0
    g7: LineSegment [constr] StartX=106 StartY=55 StartZ=0 EndX=56 EndY=55 EndZ=0
    g8: LineSegment [constr] StartX=56 StartY=55 StartZ=0 EndX=56 EndY=0 EndZ=0
    g9: GeomPoint [constr] X=81 Y=27.5 Z=0
    g10: LineSegment [constr] StartX=108 StartY=0 StartZ=0 EndX=158 EndY=0 EndZ=0
    g11: LineSegment [constr] StartX=158 StartY=0 StartZ=0 EndX=158 EndY=55 EndZ=0
    g12: LineSegment [constr] StartX=158 StartY=55 StartZ=0 EndX=108 EndY=55 EndZ=0
    g13: LineSegment [constr] StartX=108 StartY=55 StartZ=0 EndX=108 EndY=0 EndZ=0
    g14: GeomPoint [constr] X=133 Y=27.5 Z=0
    g15: LineSegment [constr] StartX=160 StartY=0 StartZ=0 EndX=210 EndY=0 EndZ=0
    g16: LineSegment [constr] StartX=210 StartY=0 StartZ=0 EndX=210 EndY=55 EndZ=0
    g17: LineSegment [constr] StartX=210 StartY=55 StartZ=0 EndX=160 EndY=55 EndZ=0
    g18: LineSegment [constr] StartX=160 StartY=55 StartZ=0 EndX=160 EndY=0 EndZ=0
    g19: GeomPoint [constr] X=185 Y=27.5 Z=0
    g20: Circle [constr] CenterX=29 CenterY=27.5 CenterZ=0 NormalX=0 NormalY=0 NormalZ=1 AngleXU=0 Radius=24.5
    g21: Circle [constr] CenterX=81 CenterY=27.5 CenterZ=0 NormalX=0 NormalY=0 NormalZ=1 AngleXU=0 Radius=24.5
    g22: Circle [constr] CenterX=133 CenterY=27.5 CenterZ=0 NormalX=0 NormalY=0 NormalZ=1 AngleXU=0 Radius=24.5
    g23: Circle [constr] CenterX=185 CenterY=27.5 CenterZ=0 NormalX=0 NormalY=0 NormalZ=1 AngleXU=0 Radius=24.5
    g24: LineSegment [constr] StartX=49 StartY=7.5 StartZ=0 EndX=49 EndY=47.5 EndZ=0
    g25: LineSegment [constr] StartX=49 StartY=47.5 StartZ=0 EndX=9 EndY=47.5 EndZ=0
    g26: LineSegment [constr] StartX=9 StartY=47.5 StartZ=0 EndX=9 EndY=7.5 EndZ=0
    g27: LineSegment [constr] StartX=9 StartY=7.5 StartZ=0 EndX=49 EndY=7.5 EndZ=0
    g28: GeomPoint [constr] X=29 Y=27.5 Z=0
    g29: LineSegment [constr] StartX=101 StartY=7.5 StartZ=0 EndX=101 EndY=47.5 EndZ=0
    g30: LineSegment [constr] StartX=101 StartY=47.5 StartZ=0 EndX=61 EndY=47.5 EndZ=0
    g31: LineSegment [constr] StartX=61 StartY=47.5 StartZ=0 EndX=61 EndY=7.5 EndZ=0
    g32: LineSegment [constr] StartX=61 StartY=7.5 StartZ=0 EndX=101 EndY=7.5 EndZ=0
    g33: GeomPoint [constr] X=81 Y=27.5 Z=0
    g34: LineSegment [constr] StartX=153 StartY=7.5 StartZ=0 EndX=153 EndY=47.5 EndZ=0
    g35: LineSegment [constr] StartX=153 StartY=47.5 StartZ=0 EndX=113 EndY=47.5 EndZ=0
    g36: LineSegment [constr] StartX=113 StartY=47.5 StartZ=0 EndX=113 EndY=7.5 EndZ=0
    g37: LineSegment [constr] StartX=113 StartY=7.5 StartZ=0 EndX=153 EndY=7.5 EndZ=0
    g38: GeomPoint [constr] X=133 Y=27.5 Z=0
    g39: LineSegment [constr] StartX=205 StartY=7.5 StartZ=0 EndX=205 EndY=47.5 EndZ=0
    g40: LineSegment [constr] StartX=205 StartY=47.5 StartZ=0 EndX=165 EndY=47.5 EndZ=0
    g41: LineSegment [constr] StartX=165 StartY=47.5 StartZ=0 EndX=165 EndY=7.5 EndZ=0
    g42: LineSegment [constr] StartX=165 StartY=7.5 StartZ=0 EndX=205 EndY=7.5 EndZ=0
    g43: GeomPoint [constr] X=185 Y=27.5 Z=0
    g44: Circle CenterX=9 CenterY=47.5 CenterZ=0 NormalX=0 NormalY=0 NormalZ=1 AngleXU=0 Radius=1.5
    g45: Circle CenterX=49 CenterY=47.5 CenterZ=0 NormalX=0 NormalY=0 NormalZ=1 AngleXU=0 Radius=1.5
    g46: Circle CenterX=61 CenterY=47.5 CenterZ=0 NormalX=0 NormalY=0 NormalZ=1 AngleXU=0 Radius=1.5
    g47: Circle CenterX=9 CenterY=7.5 CenterZ=0 NormalX=0 NormalY=0 NormalZ=1 AngleXU=0 Radius=1.5
    g48: Circle CenterX=49 CenterY=7.5 CenterZ=0 NormalX=0 NormalY=0 NormalZ=1 AngleXU=0 Radius=1.5
    g49: Circle CenterX=61 CenterY=7.5 CenterZ=0 NormalX=0 NormalY=0 NormalZ=1 AngleXU=0 Radius=1.5
    g50: Circle CenterX=101 CenterY=7.5 CenterZ=0 NormalX=0 NormalY=0 NormalZ=1 AngleXU=0 Radius=1.5
    g51: Circle CenterX=113 CenterY=7.5 CenterZ=0 NormalX=0 NormalY=0 NormalZ=1 AngleXU=0 Radius=1.5
    g52: Circle CenterX=153 CenterY=7.5 CenterZ=0 NormalX=0 NormalY=0 NormalZ=1 AngleXU=0 Radius=1.5
    g53: Circle CenterX=165 CenterY=7.5 CenterZ=0 NormalX=0 NormalY=0 NormalZ=1 AngleXU=0 Radius=1.5
    g54: Circle CenterX=205 CenterY=7.5 CenterZ=0 NormalX=0 NormalY=0 NormalZ=1 AngleXU=0 Radius=1.5
    g55: Circle CenterX=205 CenterY=47.5 CenterZ=0 NormalX=0 NormalY=0 NormalZ=1 AngleXU=0 Radius=1.5
    g56: Circle CenterX=165 CenterY=47.5 CenterZ=0 NormalX=0 NormalY=0 NormalZ=1 AngleXU=0 Radius=1.5
    g57: Circle CenterX=153 CenterY=47.5 CenterZ=0 NormalX=0 NormalY=0 NormalZ=1 AngleXU=0 Radius=1.5
    g58: Circle CenterX=113 CenterY=47.5 CenterZ=0 NormalX=0 NormalY=0 NormalZ=1 AngleXU=0 Radius=1.5
    g59: Circle CenterX=101 CenterY=47.5 CenterZ=0 NormalX=0 NormalY=0 NormalZ=1 AngleXU=0 Radius=1.5
  constraints (140):
    c: Coincident(g0,g1)
    c: Coincident(g1,g2)
    c: Coincident(g2,g3)
    c: Coincident(g3,g0)
    c: Horizontal(g0)
    c: Horizontal(g2)
    c: Vertical(g1)
    c: Vertical(g3)
    c: Symmetric(g2,g0,g4)
    c: Distance(g1,g3) = 50
    c: Distance(g0,g2) = 55
    c: Coincident(g5,g6)
    c: Coincident(g6,g7)
    c: Coincident(g7,g8)
    c: Coincident(g8,g5)
    c: Horizontal(g5)
    c: Horizontal(g7)
    c: Vertical(g6)
    c: Vertical(g8)
    c: Symmetric(g7,g5,g9)
    c: Distance(g6,g8) = 50
    c: Distance(g5,g7) = 55
    c: Coincident(g10,g11)
    c: Coincident(g11,g12)
    c: Coincident(g12,g13)
    c: Coincident(g13,g10)
    c: Horizontal(g10)
    c: Horizontal(g12)
    c: Vertical(g11)
    c: Vertical(g13)
    c: Symmetric(g12,g10,g14)
    c: Distance(g11,g13) = 50
    c: Distance(g10,g12) = 55
    c: Coincident(g15,g16)
    c: Coincident(g16,g17)
    c: Coincident(g17,g18)
    c: Coincident(g18,g15)
    c: Horizontal(g15)
    c: Horizontal(g17)
    c: Vertical(g16)
    c: Vertical(g18)
    c: Symmetric(g17,g15,g19)
    c: Distance(g16,g18) = 50
    c: Distance(g15,g17) = 55
    c: PointOnObject(g0,g-1)
    c: PointOnObject(g5,g-1)
    c: PointOnObject(g10,g-1)
    c: PointOnObject(g15,g-1)
    c: DistanceX(g0) = 4
    c: Coincident(g20,g4)
    c: Coincident(g21,g9)
    c: Coincident(g22,g14)
    c: Coincident(g23,g19)
    c: Equal(g23,g22)
    c: Equal(g22,g21)
    c: Equal(g21,g20)
    c: Diameter(g20) = 49
    c: Coincident(g24,g25)
    c: Coincident(g25,g26)
    c: Coincident(g26,g27)
    c: Coincident(g27,g24)
    c: Vertical(g24)
    c: Vertical(g26)
    c: Horizontal(g25)
    c: Horizontal(g27)
    c: Symmetric(g26,g24,g28)
    c: Coincident(g28,g4)
    c: Coincident(g29,g30)
    c: Coincident(g30,g31)
    c: Coincident(g31,g32)
    c: Coincident(g32,g29)
    c: Vertical(g29)
    c: Vertical(g31)
    c: Horizontal(g30)
    c: Horizontal(g32)
    c: Symmetric(g31,g29,g33)
    c: Coincident(g33,g9)
    c: Coincident(g34,g35)
    c: Coincident(g35,g36)
    c: Coincident(g36,g37)
    c: Coincident(g37,g34)
    c: Vertical(g34)
    c: Vertical(g36)
    c: Horizontal(g35)
    c: Horizontal(g37)
    c: Symmetric(g36,g34,g38)
    c: Coincident(g38,g14)
    c: Coincident(g39,g40)
    c: Coincident(g40,g41)
    c: Coincident(g41,g42)
    c: Coincident(g42,g39)
    c: Vertical(g39)
    c: Vertical(g41)
    c: Horizontal(g40)
    c: Horizontal(g42)
    c: Symmetric(g41,g39,g43)
    c: Coincident(g43,g19)
    c: Equal(g40,g39)
    c: Equal(g39,g35)
    c: Equal(g35,g34)
    c: Equal(g34,g30)
    c: Equal(g30,g29)
    c: Equal(g29,g25)
    c: Equal(g25,g24)
    c: DistanceX(g25,g25) = 40
    c: Coincident(g44,g25)
    c: Coincident(g45,g24)
    c: Coincident(g46,g30)
    c: Coincident(g47,g26)
    c: Coincident(g48,g24)
    c: Coincident(g49,g31)
    c: Coincident(g50,g29)
    c: Coincident(g51,g36)
    c: Coincident(g52,g34)
    c: Coincident(g53,g41)
    c: Coincident(g54,g39)
    c: Coincident(g55,g39)
    c: Coincident(g56,g40)
    c: Coincident(g57,g34)
    c: Coincident(g58,g35)
    c: Coincident(g59,g29)
    c: Equal(g44,g45)
    c: Equal(g45,g46)
    c: Equal(g46,g47)
    c: Equal(g47,g48)
    c: Equal(g48,g49)
    c: Equal(g49,g50)
    c: Equal(g50,g51)
    c: Equal(g51,g52)
    c: Equal(g52,g53)
    c: Equal(g53,g54)
    c: Equal(g54,g55)
    c: Equal(g55,g56)
    c: Equal(g56,g57)
    c: Equal(g57,g58)
    c: Equal(g58,g59)
    c: Diameter(g47) = 3
    c: Distance(g1,g8) = 2
    c: Distance(g6,g13) = 2
    c: Distance(g11,g18) = 2
FEATURE [Sketcher::SketchObject] Sketch025
  ArcFitTolerance = 1e-06
  AttachmentSupport = -> [DatumPlane002]
  FullyConstrained = true
  MakeInternals = false
  MapMode = 5
  Placement = pos=(19,0,0) rot=(0.57735,0.57735,0.57735;2.0944rad)
  expr: Constraints[89] = <<choices>>.exit_vane_thinnest
  expr: Constraints[90] = <<choices>>.exit_height - <<choices>>.exit_vane_thinnest * 2
  expr: Constraints[91] = 3 + <<choices>>.exit_vane_thinnest
  expr: Constraints[92] = <<choices>>.exit_vane_thinnest
  expr: Constraints[93] = <<choices>>.exit_vane_thinnest
  expr: Constraints[94] = <<choices>>.exit_vane_thinnest
  expr: Constraints[95] = 50 + <<choices>>.fan_gap
  sketch-geometry (40):
    g0: LineSegment StartX=5 StartY=1 StartZ=0 EndX=54 EndY=1 EndZ=0
    g1: LineSegment StartX=55 StartY=2 StartZ=0 EndX=55 EndY=53 EndZ=0
    g2: LineSegment StartX=54 StartY=54 StartZ=0 EndX=5 EndY=54 EndZ=0
    g3: LineSegment StartX=4 StartY=53 StartZ=0 EndX=4 EndY=2 EndZ=0
    g4: ArcOfCircle CenterX=5 CenterY=2 CenterZ=0 NormalX=0 NormalY=0 NormalZ=1 AngleXU=0 Radius=1 StartAngle=3.14159 EndAngle=4.71239
    g5: ArcOfCircle CenterX=54 CenterY=2 CenterZ=0 NormalX=0 NormalY=0 NormalZ=1 AngleXU=0 Radius=1 StartAngle=4.71239 EndAngle=6.28319
    g6: ArcOfCircle CenterX=54 CenterY=53 CenterZ=0 NormalX=0 NormalY=0 NormalZ=1 AngleXU=0 Radius=1 StartAngle=0 EndAngle=1.5708
    g7: ArcOfCircle CenterX=5 CenterY=53 CenterZ=0 NormalX=0 NormalY=0 NormalZ=1 AngleXU=0 Radius=1 StartAngle=1.5708 EndAngle=3.14159
    g8: GeomPoint [constr] X=4 Y=1 Z=0
    g9: GeomPoint [constr] X=55 Y=54 Z=0
    g10: LineSegment StartX=56 StartY=53 StartZ=0 EndX=56 EndY=2 EndZ=0
    g11: LineSegment StartX=57 StartY=1 StartZ=0 EndX=106 EndY=1 EndZ=0
    g12: LineSegment StartX=107 StartY=2 StartZ=0 EndX=107 EndY=53 EndZ=0
    g13: LineSegment StartX=106 StartY=54 StartZ=0 EndX=57 EndY=54 EndZ=0
    g14: ArcOfCircle CenterX=57 CenterY=53 CenterZ=0 NormalX=0 NormalY=0 NormalZ=1 AngleXU=0 Radius=1 StartAngle=1.5708 EndAngle=3.14159
    g15: ArcOfCircle CenterX=57 CenterY=2 CenterZ=0 NormalX=0 NormalY=0 NormalZ=1 AngleXU=0 Radius=1 StartAngle=3.14159 EndAngle=4.71239
    g16: ArcOfCircle CenterX=106 CenterY=2 CenterZ=0 NormalX=0 NormalY=0 NormalZ=1 AngleXU=0 Radius=1 StartAngle=4.71239 EndAngle=6.28319
    g17: ArcOfCircle CenterX=106 CenterY=53 CenterZ=0 NormalX=0 NormalY=0 NormalZ=1 AngleXU=0 Radius=1 StartAngle=-9e-16 EndAngle=1.5708
    g18: GeomPoint [constr] X=56 Y=54 Z=0
    g19: GeomPoint [constr] X=107 Y=1 Z=0
    g20: LineSegment StartX=109 StartY=1 StartZ=0 EndX=158 EndY=1 EndZ=0
    g21: LineSegment StartX=159 StartY=2 StartZ=0 EndX=159 EndY=53 EndZ=0
    g22: LineSegment StartX=158 StartY=54 StartZ=0 EndX=109 EndY=54 EndZ=0
    g23: LineSegment StartX=108 StartY=53 StartZ=0 EndX=108 EndY=2 EndZ=0
    g24: ArcOfCircle CenterX=109 CenterY=2 CenterZ=0 NormalX=0 NormalY=0 NormalZ=1 AngleXU=0 Radius=1 StartAngle=3.14159 EndAngle=4.71239
    g25: ArcOfCircle CenterX=158 CenterY=2 CenterZ=0 NormalX=0 NormalY=0 NormalZ=1 AngleXU=0 Radius=1 StartAngle=4.71239 EndAngle=6.28319
    g26: ArcOfCircle CenterX=158 CenterY=53 CenterZ=0 NormalX=0 NormalY=0 NormalZ=1 AngleXU=0 Radius=1 StartAngle=-1.8e-15 EndAngle=1.5708
    g27: ArcOfCircle CenterX=109 CenterY=53 CenterZ=0 NormalX=0 NormalY=0 NormalZ=1 AngleXU=0 Radius=1 StartAngle=1.5708 EndAngle=3.14159
    g28: GeomPoint [constr] X=108 Y=1 Z=0
    g29: GeomPoint [constr] X=159 Y=54 Z=0
    g30: LineSegment StartX=160 StartY=53 StartZ=0 EndX=160 EndY=2 EndZ=0
    g31: LineSegment StartX=161 StartY=1 StartZ=0 EndX=210 EndY=1 EndZ=0
    g32: LineSegment StartX=211 StartY=2 StartZ=0 EndX=211 EndY=53 EndZ=0
    g33: LineSegment StartX=210 StartY=54 StartZ=0 EndX=161 EndY=54 EndZ=0
    g34: ArcOfCircle CenterX=161 CenterY=53 CenterZ=0 NormalX=0 NormalY=0 NormalZ=1 AngleXU=0 Radius=1 StartAngle=1.5708 EndAngle=3.14159
    g35: ArcOfCircle CenterX=161 CenterY=2 CenterZ=0 NormalX=0 NormalY=0 NormalZ=1 AngleXU=0 Radius=1 StartAngle=3.14159 EndAngle=4.71239
    g36: ArcOfCircle CenterX=210 CenterY=2 CenterZ=0 NormalX=0 NormalY=0 NormalZ=1 AngleXU=0 Radius=1 StartAngle=4.71239 EndAngle=6.28319
    g37: ArcOfCircle CenterX=210 CenterY=53 CenterZ=0 NormalX=0 NormalY=0 NormalZ=1 AngleXU=0 Radius=1 StartAngle=1.9e-15 EndAngle=1.5708
    g38: GeomPoint [constr] X=160 Y=54 Z=0
    g39: GeomPoint [constr] X=211 Y=1 Z=0
  constraints (96):
    c: Tangent(g0,g4) = -1.5708
    c: Tangent(g0,g5) = -1.5708
    c: Tangent(g1,g5) = -1.5708
    c: Tangent(g1,g6) = -1.5708
    c: Tangent(g2,g6) = -1.5708
    c: Tangent(g2,g7) = -1.5708
    c: Tangent(g3,g7) = -1.5708
    c: Tangent(g3,g4) = -1.5708
    c: Horizontal(g0)
    c: Horizontal(g2)
    c: Vertical(g1)
    c: Vertical(g3)
    c: Equal(g4,g5)
    c: Equal(g5,g6)
    c: Equal(g6,g7)
    c: PointOnObject(g8,g0)
    c: PointOnObject(g8,g3)
    c: PointOnObject(g9,g1)
    c: PointOnObject(g9,g2)
    c: Tangent(g10,g14) = -1.5708
    c: Tangent(g10,g15) = -1.5708
    c: Tangent(g11,g15) = -1.5708
    c: Tangent(g11,g16) = -1.5708
    c: Tangent(g12,g16) = -1.5708
    c: Tangent(g12,g17) = -1.5708
    c: Tangent(g13,g17) = -1.5708
    c: Tangent(g13,g14) = -1.5708
    c: Vertical(g10)
    c: Vertical(g12)
    c: Horizontal(g11)
    c: Horizontal(g13)
    c: Equal(g14,g15)
    c: Equal(g15,g16)
    c: Equal(g16,g17)
    c: PointOnObject(g18,g10)
    c: PointOnObject(g18,g13)
    c: PointOnObject(g19,g11)
    c: PointOnObject(g19,g12)
    c: Tangent(g20,g24) = -1.5708
    c: Tangent(g20,g25) = -1.5708
    c: Tangent(g21,g25) = -1.5708
    c: Tangent(g21,g26) = -1.5708
    c: Tangent(g22,g26) = -1.5708
    c: Tangent(g22,g27) = -1.5708
    c: Tangent(g23,g27) = -1.5708
    c: Tangent(g23,g24) = -1.5708
    c: Horizontal(g20)
    c: Horizontal(g22)
    c: Vertical(g21)
    c: Vertical(g23)
    c: Equal(g24,g25)
    c: Equal(g25,g26)
    c: Equal(g26,g27)
    c: PointOnObject(g28,g20)
    c: PointOnObject(g28,g23)
    c: PointOnObject(g29,g21)
    c: PointOnObject(g29,g22)
    c: Tangent(g30,g34) = -1.5708
    c: Tangent(g30,g35) = -1.5708
    c: Tangent(g31,g35) = -1.5708
    c: Tangent(g31,g36) = -1.5708
    c: Tangent(g32,g36) = -1.5708
    c: Tangent(g32,g37) = -1.5708
    c: Tangent(g33,g37) = -1.5708
    c: Tangent(g33,g34) = -1.5708
    c: Vertical(g30)
    c: Vertical(g32)
    c: Horizontal(g31)
    c: Horizontal(g33)
    c: Equal(g34,g35)
    c: Equal(g35,g36)
    c: Equal(g36,g37)
    c: PointOnObject(g38,g30)
    c: PointOnObject(g38,g33)
    c: PointOnObject(g39,g31)
    c: PointOnObject(g39,g32)
    c: Equal(g7,g14)
    c: Equal(g14,g27)
    c: Equal(g27,g34)
    c: Radius(g34) = 1
    c: Equal(g2,g13)
    c: Equal(g13,g22)
    c: Equal(g22,g33)
    c: Equal(g1,g10)
    c: Equal(g10,g23)
    c: Equal(g23,g30)
    c: PointOnObject(g11,g0)
    c: PointOnObject(g20,g11)
    c: PointOnObject(g31,g20)
    c: DistanceY(g0) = 1
    c: Distance(g2,g0) = 53
    c: DistanceX(g3) = 4
    c: Distance(g1,g10) = 1
    c: Distance(g12,g23) = 1
    c: Distance(g29,g30) = 1
    c: Distance(g3,g10) = 52
FEATURE [Sketcher::SketchObject] Sketch026
  ArcFitTolerance = 1e-06
  AttachmentSupport = -> [DatumPlane002]
  FullyConstrained = true
  MakeInternals = false
  MapMode = 5
  Placement = pos=(19,0,0) rot=(0.57735,0.57735,0.57735;2.0944rad)
  expr: Constraints[31] = 4 - 0.5 * <<choices>>.fan_gap
  expr: Constraints[32] = <<choices>>.exit_vane_thinnest
  expr: Constraints[34] = <<choices>>.exit_height
  expr: Constraints[35] = 50 + <<choices>>.fan_gap
  sketch-geometry (12):
    g0: LineSegment StartX=3 StartY=27 StartZ=0 EndX=28.5 EndY=27 EndZ=0
    g1: LineSegment StartX=28.5 StartY=27 StartZ=0 EndX=28.5 EndY=0 EndZ=0
    g2: LineSegment StartX=28.5 StartY=0 StartZ=0 EndX=29.5 EndY=0 EndZ=0
    g3: LineSegment StartX=29.5 StartY=0 StartZ=0 EndX=29.5 EndY=27 EndZ=0
    g4: LineSegment StartX=29.5 StartY=27 StartZ=0 EndX=55 EndY=27 EndZ=0
    g5: LineSegment StartX=55 StartY=27 StartZ=0 EndX=55 EndY=28 EndZ=0
    g6: LineSegment StartX=55 StartY=28 StartZ=0 EndX=29.5 EndY=28 EndZ=0
    g7: LineSegment StartX=29.5 StartY=28 StartZ=0 EndX=29.5 EndY=55 EndZ=0
    g8: LineSegment StartX=29.5 StartY=55 StartZ=0 EndX=28.5 EndY=55 EndZ=0
    g9: LineSegment StartX=28.5 StartY=55 StartZ=0 EndX=28.5 EndY=28 EndZ=0
    g10: LineSegment StartX=28.5 StartY=28 StartZ=0 EndX=3 EndY=28 EndZ=0
    g11: LineSegment StartX=3 StartY=28 StartZ=0 EndX=3 EndY=27 EndZ=0
  constraints (36):
    c: Horizontal(g0)
    c: Coincident(g0,g1)
    c: Vertical(g1)
    c: Coincident(g1,g2)
    c: PointOnObject(g2,g-1)
    c: Horizontal(g2)
    c: Coincident(g2,g3)
    c: Vertical(g3)
    c: Coincident(g3,g4)
    c: Horizontal(g4)
    c: Coincident(g4,g5)
    c: Vertical(g5)
    c: Coincident(g5,g6)
    c: Horizontal(g6)
    c: Coincident(g6,g7)
    c: Vertical(g7)
    c: Coincident(g7,g8)
    c: Horizontal(g8)
    c: Coincident(g8,g9)
    c: Vertical(g9)
    c: Coincident(g9,g10)
    c: Horizontal(g10)
    c: Coincident(g10,g11)
    c: Coincident(g11,g0)
    c: Vertical(g11)
    c: Equal(g10,g0)
    c: Equal(g6,g4)
    c: Equal(g4,g0)
    c: Equal(g7,g9)
    c: Equal(g9,g1)
    c: Equal(g1,g3)
    c: DistanceX(g0) = 3
    c: DistanceY(g11,g11) = 1
    c: Equal(g2,g5)
    c: DistanceY(g7) = 55
    c: Distance(g5,g11) = 52
FEATURE [Sketcher::SketchObject] Sketch027
  ArcFitTolerance = 1e-06
  AttachmentSupport = -> [YZ_Plane015]
  FullyConstrained = true
  MakeInternals = false
  MapMode = 5
  Placement = pos=(0,0,0) rot=(0.57735,0.57735,0.57735;2.0944rad)
  expr: Constraints[20] = <<choices>>.exit_height / 2
  expr: Constraints[22] = <<choices>>.exit_cone
  expr: Constraints[24] = <<choices>>.exit_height
  expr: Constraints[31] = <<choices>>.exit_vane_thickest
  expr: Constraints[49] = <<choices>>.exit_vane_thickest
  sketch-geometry (16):
    g0: ArcOfCircle CenterX=29 CenterY=27.5 CenterZ=0 NormalX=0 NormalY=0 NormalZ=1 AngleXU=0 Radius=12.25 StartAngle=3.26435 EndAngle=4.58963
    g1: LineSegment StartX=4 StartY=29 StartZ=0 EndX=16.8422 EndY=29 EndZ=0
    g2: LineSegment StartX=4 StartY=29 StartZ=0 EndX=4 EndY=26 EndZ=0
    g3: LineSegment StartX=4 StartY=26 StartZ=0 EndX=16.8422 EndY=26 EndZ=0
    g4: LineSegment StartX=27.5 StartY=15.3422 StartZ=0 EndX=27.5 EndY=0 EndZ=0
    g5: LineSegment StartX=27.5 StartY=0 StartZ=0 EndX=30.5 EndY=0 EndZ=0
    g6: LineSegment StartX=30.5 StartY=0 StartZ=0 EndX=30.5 EndY=15.3422 EndZ=0
    g7: LineSegment StartX=41.1578 StartY=26 StartZ=0 EndX=55 EndY=26 EndZ=0
    g8: LineSegment StartX=55 StartY=26 StartZ=0 EndX=55 EndY=29 EndZ=0
    g9: LineSegment StartX=55 StartY=29 StartZ=0 EndX=41.1578 EndY=29 EndZ=0
    g10: LineSegment StartX=30.5 StartY=39.6578 StartZ=0 EndX=30.5 EndY=55 EndZ=0
    g11: LineSegment StartX=30.5 StartY=55 StartZ=0 EndX=27.5 EndY=55 EndZ=0
    g12: LineSegment StartX=27.5 StartY=55 StartZ=0 EndX=27.5 EndY=39.6578 EndZ=0
    g13: ArcOfCircle CenterX=29 CenterY=27.5 CenterZ=0 NormalX=0 NormalY=0 NormalZ=1 AngleXU=0 Radius=12.25 StartAngle=4.83515 EndAngle=6.16043
    g14: ArcOfCircle CenterX=29 CenterY=27.5 CenterZ=0 NormalX=0 NormalY=0 NormalZ=1 AngleXU=0 Radius=12.25 StartAngle=1.69355 EndAngle=3.01884
    g15: ArcOfCircle CenterX=29 CenterY=27.5 CenterZ=0 NormalX=0 NormalY=0 NormalZ=1 AngleXU=0 Radius=12.25 StartAngle=0.122757 EndAngle=1.44804
  constraints (50):
    c: Horizontal(g1)
    c: Coincident(g1,g2)
    c: Vertical(g2)
    c: Coincident(g2,g3)
    c: Horizontal(g3)
    c: PointOnObject(g4,g-1)
    c: Vertical(g4)
    c: Coincident(g4,g5)
    c: PointOnObject(g5,g-1)
    c: Coincident(g5,g6)
    c: PointOnObject(g6,g13)
    c: Horizontal(g7)
    c: Coincident(g7,g8)
    c: Vertical(g8)
    c: Coincident(g8,g9)
    c: Horizontal(g9)
    c: Vertical(g10)
    c: Coincident(g10,g11)
    c: Coincident(g11,g12)
    c: Vertical(g12)
    c: DistanceY(g0) = 27.5
    c: DistanceX(g0) = 29
    c: Diameter(g0) = 24.5
    c: Horizontal(g11)
    c: DistanceY(g11) = 55
    c: Vertical(g6)
    c: Symmetric(g6,g12,g0)
    c: PointOnObject(g12,g4)
    c: PointOnObject(g6,g10)
    c: PointOnObject(g9,g1)
    c: PointOnObject(g3,g7)
    c: Distance(g1,g3) = 3
    c: Symmetric(g3,g9,g0)
    c: DistanceX(g2) = 4
    c: DistanceX(g7) = 55
    c: Coincident(g14,g1)
    c: Coincident(g0,g3)
    c: Equal(g0,g13)
    c: Coincident(g0,g4)
    c: PointOnObject(g13,g6)
    c: Coincident(g0,g13)
    c: Equal(g13,g14)
    c: Coincident(g15,g10)
    c: PointOnObject(g14,g12)
    c: Coincident(g13,g14)
    c: Equal(g13,g15)
    c: Coincident(g13,g7)
    c: PointOnObject(g15,g9)
    c: Coincident(g13,g15)
    c: Distance(g5) = 3
FEATURE [Sketcher::SketchObject] Sketch028
  ArcFitTolerance = 1e-06
  AttachmentSupport = -> [DatumPlane002]
  FullyConstrained = false
  MakeInternals = false
  MapMode = 5
  Placement = pos=(19,0,0) rot=(0.57735,0.57735,0.57735;2.0944rad)
  expr: Constraints[7] = <<components>>.frame_h - 12.5
  sketch-geometry (15):
    g0: ArcOfCircle CenterX=229.5 CenterY=40 CenterZ=0 NormalX=0 NormalY=0 NormalZ=1 AngleXU=0 Radius=3.5 StartAngle=4.71239 EndAngle=7.85398
    g1: ArcOfCircle CenterX=217 CenterY=40 CenterZ=0 NormalX=0 NormalY=0 NormalZ=1 AngleXU=0 Radius=3.5 StartAngle=1.5708 EndAngle=4.71239
    g2: LineSegment StartX=229.5 StartY=36.5 StartZ=0 EndX=217 EndY=36.5 EndZ=0
    g3: LineSegment StartX=229.5 StartY=43.5 StartZ=0 EndX=217 EndY=43.5 EndZ=0
    g4: LineSegment [constr] StartX=217 StartY=40 StartZ=0 EndX=217 EndY=56.7823 EndZ=0
    g5: LineSegment [constr] StartX=229.5 StartY=40 StartZ=0 EndX=229.5 EndY=56.7823 EndZ=0
    g6: LineSegment [constr] StartX=229.5 StartY=56.7823 StartZ=0 EndX=217 EndY=56.7823 EndZ=0
    g7: ArcOfCircle CenterX=217 CenterY=25 CenterZ=0 NormalX=0 NormalY=0 NormalZ=1 AngleXU=0 Radius=3.5 StartAngle=1.5708 EndAngle=4.71239
    g8: ArcOfCircle CenterX=229.5 CenterY=25 CenterZ=0 NormalX=0 NormalY=0 NormalZ=1 AngleXU=0 Radius=3.5 StartAngle=4.71239 EndAngle=7.85398
    g9: LineSegment StartX=217 StartY=28.5 StartZ=0 EndX=229.5 EndY=28.5 EndZ=0
    g10: LineSegment StartX=217 StartY=21.5 StartZ=0 EndX=229.5 EndY=21.5 EndZ=0
    g11: ArcOfCircle [constr] CenterX=217 CenterY=40 CenterZ=0 NormalX=0 NormalY=0 NormalZ=1 AngleXU=0 Radius=2.5 StartAngle=1.5708 EndAngle=4.71239
    g12: ArcOfCircle [constr] CenterX=229.5 CenterY=40 CenterZ=0 NormalX=0 NormalY=0 NormalZ=1 AngleXU=0 Radius=2.5 StartAngle=4.71239 EndAngle=7.85398
    g13: LineSegment [constr] StartX=217 StartY=42.5 StartZ=0 EndX=229.5 EndY=42.5 EndZ=0
    g14: LineSegment [constr] StartX=217 StartY=37.5 StartZ=0 EndX=229.5 EndY=37.5 EndZ=0
  constraints (37):
    c: Tangent(g0,g2) = 1.5708
    c: Tangent(g0,g3) = -1.5708
    c: Tangent(g1,g2) = 1.5708
    c: Tangent(g1,g3) = -1.5708
    c: Equal(g0,g1)
    c: Radius(g0) = 3.5
    c: Horizontal(g2)
    c: DistanceX(g1) = 217
    c: DistanceY(g1) = 40
    c: Coincident(g4,g1)
    c: Vertical(g4)
    c: Coincident(g5,g0)
    c: Vertical(g5)
    c: Coincident(g6,g5)
    c: Coincident(g6,g4)
    c: Horizontal(g6)
    c: Tangent(g7,g9) = 1.5708
    c: Tangent(g7,g10) = -1.5708
    c: Tangent(g8,g9) = 1.5708
    c: Tangent(g8,g10) = -1.5708
    c: Equal(g7,g8)
    c: Radius(g7) = 3.5
    c: PointOnObject(g7,g4)
    c: PointOnObject(g8,g5)
    c: Horizontal(g9)
    c: Tangent(g11,g13) = 1.5708
    c: Tangent(g11,g14) = -1.5708
    c: Tangent(g12,g13) = 1.5708
    c: Tangent(g12,g14) = -1.5708
    c: Equal(g11,g12)
    c: Horizontal(g14)
    c: Radius(g11) = 2.5
    c: PointOnObject(g11,g4)
    c: PointOnObject(g12,g5)
    c: DistanceY(g7) = 25
    c: DistanceY(g11) = 40
    c: DistanceX(g6,g6) = 12.5
FEATURE [Sketcher::SketchObject] Sketch030
  ArcFitTolerance = 1e-06
  AttachmentSupport = -> [YZ_Plane018]
  FullyConstrained = true
  MakeInternals = false
  MapMode = 5
  Placement = pos=(0,0,0) rot=(0.57735,0.57735,0.57735;2.0944rad)
  expr: Constraints[12] = <<components>>.m3_threadhole
  expr: Constraints[13] = <<choices>>.leg_axle_hole_dia
  expr: Constraints[14] = <<choices>>.leg_bracket_axis_dist
  expr: Constraints[8] = <<choices>>.leg_length
  sketch-geometry (7):
    g0: ArcOfCircle CenterX=0 CenterY=0 CenterZ=0 NormalX=0 NormalY=0 NormalZ=1 AngleXU=0 Radius=5 StartAngle=1.5708 EndAngle=4.71239
    g1: ArcOfCircle CenterX=130 CenterY=-5e-16 CenterZ=0 NormalX=0 NormalY=0 NormalZ=1 AngleXU=0 Radius=5 StartAngle=4.71239 EndAngle=7.85398
    g2: LineSegment StartX=-2.328e-13 StartY=5 StartZ=0 EndX=130 EndY=5 EndZ=0
    g3: LineSegment StartX=1.501e-13 StartY=-5 StartZ=0 EndX=130 EndY=-5 EndZ=0
    g4: Circle CenterX=0 CenterY=0 CenterZ=0 NormalX=0 NormalY=0 NormalZ=1 AngleXU=0 Radius=2.6
    g5: Circle [constr] CenterX=42.5 CenterY=0 CenterZ=0 NormalX=0 NormalY=0 NormalZ=1 AngleXU=0 Radius=1.25
    g6: Circle CenterX=130 CenterY=-5e-16 CenterZ=0 NormalX=0 NormalY=0 NormalZ=1 AngleXU=0 Radius=1.25
  constraints (16):
    c: Tangent(g0,g2) = 1.5708
    c: Tangent(g0,g3) = -1.5708
    c: Tangent(g1,g2) = 1.5708
    c: Tangent(g1,g3) = -1.5708
    c: Equal(g0,g1)
    c: Horizontal(g3)
    c: Radius(g0) = 5
    c: Coincident(g0,g-1)
    c: DistanceX(g2,g2) = 130
    c: Coincident(g4,g0)
    c: PointOnObject(g5,g-1)
    c: Coincident(g6,g1)
    c: Diameter(g6) = 2.5
    c: Diameter(g4) = 5.2
    c: DistanceX(g5) = 42.5
    c: Equal(g5,g6)
FEATURE [PartDesign::Pad] Pad015
  Direction = (1,0,0)
  Length = 10
  Length2 = 10
  Placement = pos=(0,0,0) rot=(1,1,1;2.0944rad)
  Profile = -> Sketch030 [Edge5,Edge1,Edge2,Edge4,Edge3]
  ReferenceAxis = -> Sketch030 [N_Axis]
  Refine = true
  Suppressed = false
  Type = 0
  expr: Length = <<choices>>.leg_width
FEATURE [Sketcher::SketchObject] Sketch031
  ArcFitTolerance = 1e-06
  AttachmentSupport = -> [YZ_Plane020]
  FullyConstrained = true
  MakeInternals = false
  MapMode = 5
  Placement = pos=(0,0,0) rot=(0.57735,0.57735,0.57735;2.0944rad)
  expr: Constraints[13] = <<components>>.m3_hole
  expr: Constraints[14] = <<choices>>.leg_axle_hole_dia
  expr: Constraints[15] = <<choices>>.leg_bracket_axis_dist
  expr: Constraints[8] = <<choices>>.leg_length
  sketch-geometry (7):
    g0: ArcOfCircle CenterX=0 CenterY=0 CenterZ=0 NormalX=0 NormalY=0 NormalZ=1 AngleXU=0 Radius=5 StartAngle=1.5708 EndAngle=4.71239
    g1: ArcOfCircle CenterX=130 CenterY=-3e-16 CenterZ=0 NormalX=0 NormalY=0 NormalZ=1 AngleXU=0 Radius=5 StartAngle=4.71239 EndAngle=7.85398
    g2: LineSegment StartX=1.346e-13 StartY=5 StartZ=0 EndX=130 EndY=5 EndZ=0
    g3: LineSegment StartX=-9e-16 StartY=-5 StartZ=0 EndX=130 EndY=-5 EndZ=0
    g4: Circle CenterX=0 CenterY=0 CenterZ=0 NormalX=0 NormalY=0 NormalZ=1 AngleXU=0 Radius=2.6
    g5: Circle CenterX=42.5 CenterY=0 CenterZ=0 NormalX=0 NormalY=0 NormalZ=1 AngleXU=0 Radius=1.75
    g6: Circle CenterX=130 CenterY=-3e-16 CenterZ=0 NormalX=0 NormalY=0 NormalZ=1 AngleXU=0 Radius=1.75
  constraints (16):
    c: Tangent(g0,g2) = 1.5708
    c: Tangent(g0,g3) = -1.5708
    c: Tangent(g1,g2) = 1.5708
    c: Tangent(g1,g3) = -1.5708
    c: Equal(g0,g1)
    c: Horizontal(g3)
    c: Radius(g0) = 5
    c: Coincident(g0,g-1)
    c: Distance(g2) = 130
    c: Coincident(g4,g0)
    c: PointOnObject(g5,g-1)
    c: Coincident(g6,g1)
    c: Equal(g6,g5)
    c: Diameter(g5) = 3.5
    c: Diameter(g4) = 5.2
    c: DistanceX(g5) = 42.5
FEATURE [Sketcher::SketchObject] Sketch032
  ArcFitTolerance = 1e-06
  AttachmentSupport = -> [YZ_Plane022]
  FullyConstrained = true
  MakeInternals = false
  MapMode = 5
  Placement = pos=(0,0,0) rot=(0.57735,0.57735,0.57735;2.0944rad)
  expr: Constraints[12] = <<components>>.m3_hole
  expr: Constraints[8] = <<choices>>.leg_bracket_length
  sketch-geometry (6):
    g0: ArcOfCircle CenterX=0 CenterY=0 CenterZ=0 NormalX=0 NormalY=0 NormalZ=1 AngleXU=0 Radius=5 StartAngle=1.5708 EndAngle=4.71239
    g1: ArcOfCircle CenterX=52.5 CenterY=4e-16 CenterZ=0 NormalX=0 NormalY=0 NormalZ=1 AngleXU=0 Radius=5 StartAngle=4.71239 EndAngle=7.85398
    g2: LineSegment StartX=-2.8097e-12 StartY=5 StartZ=0 EndX=52.5 EndY=5 EndZ=0
    g3: LineSegment StartX=-9e-16 StartY=-5 StartZ=0 EndX=52.5 EndY=-5 EndZ=0
    g4: Circle CenterX=0 CenterY=0 CenterZ=0 NormalX=0 NormalY=0 NormalZ=1 AngleXU=0 Radius=2.65
    g5: Circle CenterX=52.5 CenterY=4e-16 CenterZ=0 NormalX=0 NormalY=0 NormalZ=1 AngleXU=0 Radius=1.75
  constraints (13):
    c: Tangent(g0,g2) = 1.5708
    c: Tangent(g0,g3) = -1.5708
    c: Tangent(g1,g2) = 1.5708
    c: Tangent(g1,g3) = -1.5708
    c: Equal(g0,g1)
    c: Horizontal(g3)
    c: Radius(g0) = 5
    c: Coincident(g0,g-1)
    c: DistanceX(g2,g2) = 52.5
    c: Coincident(g4,g0)
    c: Coincident(g5,g1)
    c: Diameter(g4) = 5.3
    c: Diameter(g5) = 3.5
FEATURE [PartDesign::Pad] Pad017
  Direction = (1,0,0)
  Length = 4.8
  Length2 = 10
  Placement = pos=(0,0,0) rot=(1,1,1;2.0944rad)
  Profile = -> Sketch032
  ReferenceAxis = -> Sketch032 [N_Axis]
  Refine = true
  Suppressed = false
  Type = 0
FEATURE [Sketcher::SketchObject] Sketch033
  ArcFitTolerance = 1e-06
  AttachmentSupport = -> [YZ_Plane024]
  FullyConstrained = true
  MakeInternals = false
  MapMode = 5
  Placement = pos=(0,0,0) rot=(0.57735,0.57735,0.57735;2.0944rad)
  expr: Constraints[2] = <<components>>.m3_hole
  sketch-geometry (2):
    g0: Circle CenterX=0 CenterY=0 CenterZ=0 NormalX=0 NormalY=0 NormalZ=1 AngleXU=0 Radius=5
    g1: Circle CenterX=0 CenterY=0 CenterZ=0 NormalX=0 NormalY=0 NormalZ=1 AngleXU=0 Radius=1.75
  constraints (4):
    c: Coincident(g0,g-1)
    c: Coincident(g1,g0)
    c: Diameter(g1) = 3.5
    c: Diameter(g0) = 10
FEATURE [PartDesign::Pad] Pad018
  Direction = (1,0,0)
  Length = 11
  Length2 = 10
  Placement = pos=(0,0,0) rot=(1,1,1;2.0944rad)
  Profile = -> Sketch033
  ReferenceAxis = -> Sketch033 [N_Axis]
  Refine = true
  Suppressed = false
  Type = 0
  expr: Length = 2 * (<<choices>>.leg_betweens + <<choices>>.leg_clearance)
FEATURE [PartDesign::Body] Body011
  AllowCompound = false
  Group = -> [Sketch033,Pad018]
  Origin = -> Origin024
  Tip = -> Pad018
FEATURE [App::Part] Part011  label="FOOT"
  Group = -> [Body011]
  Origin = -> Origin023
FEATURE [Sketcher::SketchObject] Sketch034
  ArcFitTolerance = 1e-06
  AttachmentSupport = -> [YZ_Plane026]
  FullyConstrained = true
  MakeInternals = false
  MapMode = 5
  Placement = pos=(0,0,0) rot=(0.57735,0.57735,0.57735;2.0944rad)
  expr: Constraints[2] = <<components>>.m3_hole
  expr: Constraints[3] = <<choices>>.leg_axle_hole_dia - 0.4
  sketch-geometry (2):
    g0: Circle CenterX=0 CenterY=0 CenterZ=0 NormalX=0 NormalY=0 NormalZ=1 AngleXU=0 Radius=1.75
    g1: Circle CenterX=0 CenterY=0 CenterZ=0 NormalX=0 NormalY=0 NormalZ=1 AngleXU=0 Radius=2.4
  constraints (4):
    c: Coincident(g0,g-1)
    c: Coincident(g1,g0)
    c: Diameter(g0) = 3.5
    c: Diameter(g1) = 4.8
FEATURE [PartDesign::Pad] Pad019
  Direction = (1,0,0)
  Length = 11
  Length2 = 10
  Placement = pos=(0,0,0) rot=(1,1,1;2.0944rad)
  Profile = -> Sketch034
  ReferenceAxis = -> Sketch034 [N_Axis]
  Refine = true
  Suppressed = false
  Type = 0
  expr: Length = 2 * <<choices>>.leg_betweens + 1
FEATURE [PartDesign::Body] Body012
  AllowCompound = false
  Group = -> [Sketch034,Pad019]
  Origin = -> Origin026
  Tip = -> Pad019
FEATURE [App::Part] Part012  label="LEG_BRACKET_AXLE"
  Group = -> [Body012]
  Origin = -> Origin025
FEATURE [Sketcher::SketchObject] Sketch035
  ArcFitTolerance = 1e-06
  AttachmentSupport = -> [XY_Plane013]
  FullyConstrained = false
  MakeInternals = false
  MapMode = 5
  expr: Constraints[10] = <<components>>.frame_w - 62
  expr: Constraints[8] = 170 + <<choices>>.mb_front_edge_gap + 5 + 3
  sketch-geometry (4):
    g0: LineSegment StartX=127.279 StartY=188 StartZ=0 EndX=127.279 EndY=185 EndZ=0
    g1: LineSegment StartX=127.279 StartY=185 StartZ=0 EndX=313 EndY=185 EndZ=0
    g2: LineSegment StartX=313 StartY=185 StartZ=0 EndX=313 EndY=188 EndZ=0
    g3: LineSegment StartX=313 StartY=188 StartZ=0 EndX=127.279 EndY=188 EndZ=0
  constraints (11):
    c: Coincident(g0,g1)
    c: Coincident(g1,g2)
    c: Coincident(g2,g3)
    c: Coincident(g3,g0)
    c: Vertical(g0)
    c: Vertical(g2)
    c: Horizontal(g1)
    c: Horizontal(g3)
    c: DistanceY(g0) = 188
    c: DistanceY(g0,g0) = 3
    c: DistanceX(g2) = 313
FEATURE [PartDesign::Pad] Pad020  label="lip in front of rear ports"
  BaseFeature = -> LinearPattern
  Direction = (0,0,1)
  Length = 4.25
  Length2 = 10
  Profile = -> Sketch035
  ReferenceAxis = -> Sketch035 [N_Axis]
  Refine = true
  Suppressed = false
  Type = 0
  expr: Length = 3 + <<choices>>.base_under_mb_thickness
FEATURE [Sketcher::SketchObject] Sketch036
  ArcFitTolerance = 1e-06
  AttachmentSupport = -> [YZ_Plane015]
  FullyConstrained = true
  MakeInternals = false
  MapMode = 5
  Placement = pos=(0,0,0) rot=(0.57735,0.57735,0.57735;2.0944rad)
  expr: Constraints[10] = <<components>>.frame_h
  expr: Constraints[32] = 4 + 4 * <<components>>.fan_h + 4 * <<choices>>.fan_gap
  expr: Constraints[9] = <<choices>>.exit_height
  sketch-geometry (12):
    g0: LineSegment [constr] StartX=0 StartY=0 StartZ=0 EndX=229.5 EndY=0 EndZ=0
    g1: LineSegment [constr] StartX=229.5 StartY=0 StartZ=0 EndX=229.5 EndY=55 EndZ=0
    g2: LineSegment [constr] StartX=229.5 StartY=55 StartZ=0 EndX=0 EndY=55 EndZ=0
    g3: LineSegment [constr] StartX=0 StartY=55 StartZ=0 EndX=0 EndY=0 EndZ=0
    g4: LineSegment StartX=229.5 StartY=0 StartZ=0 EndX=229.5 EndY=55 EndZ=0
    g5: LineSegment StartX=229.5 StartY=55 StartZ=0 EndX=212 EndY=55 EndZ=0
    g6: LineSegment StartX=212 StartY=55 StartZ=0 EndX=212 EndY=0 EndZ=0
    g7: LineSegment StartX=212 StartY=0 StartZ=0 EndX=229.5 EndY=0 EndZ=0
    g8: LineSegment StartX=0 StartY=0 StartZ=0 EndX=3 EndY=0 EndZ=0
    g9: LineSegment StartX=3 StartY=0 StartZ=0 EndX=3 EndY=55 EndZ=0
    g10: LineSegment StartX=3 StartY=55 StartZ=0 EndX=0 EndY=55 EndZ=0
    g11: LineSegment StartX=0 StartY=55 StartZ=0 EndX=0 EndY=0 EndZ=0
  constraints (33):
    c: Coincident(g0,g1)
    c: Coincident(g1,g2)
    c: Coincident(g2,g3)
    c: Coincident(g3,g0)
    c: Horizontal(g0)
    c: Horizontal(g2)
    c: Vertical(g1)
    c: Vertical(g3)
    c: Coincident(g0,g-1)
    c: DistanceY(g1,g1) = 55
    c: DistanceX(g1) = 229.5
    c: Coincident(g4,g5)
    c: Coincident(g5,g6)
    c: Coincident(g6,g7)
    c: Coincident(g7,g4)
    c: Vertical(g4)
    c: Vertical(g6)
    c: Horizontal(g5)
    c: Horizontal(g7)
    c: Coincident(g4,g0)
    c: PointOnObject(g5,g2)
    c: Coincident(g8,g9)
    c: Coincident(g9,g10)
    c: Coincident(g10,g11)
    c: Coincident(g11,g8)
    c: Horizontal(g8)
    c: Horizontal(g10)
    c: Vertical(g9)
    c: Vertical(g11)
    c: Coincident(g8,g0)
    c: PointOnObject(g9,g2)
    c: DistanceX(g9) = 3
    c: DistanceX(g5) = 212
FEATURE [PartDesign::Pad] Pad021
  BaseFeature = -> Pad012
  Direction = (1,0,0)
  Length = 46
  Length2 = 10
  Profile = -> Sketch036
  ReferenceAxis = -> Sketch036 [N_Axis]
  Refine = true
  Reversed = true
  Suppressed = false
  Type = 0
  expr: Length = 65 - <<choices>>.exit_w
FEATURE [PartDesign::Plane] DatumPlane003
  AttachmentOffset = pos=(0,0,-25) rot=(0,0,1;0rad)
  AttachmentSupport = -> [YZ_Plane015]
  Length = 283.038
  MapMode = 5
  Placement = pos=(-25,0,0) rot=(0.57735,0.57735,0.57735;2.0944rad)
  ResizeMode = 0
  Width = 108.538
FEATURE [PartDesign::Plane] DatumPlane004
  AttachmentOffset = pos=(0,0,-47) rot=(0,0,1;0rad)
  AttachmentSupport = -> [YZ_Plane015]
  Length = 283.038
  MapMode = 5
  Placement = pos=(-47,0,0) rot=(0.57735,0.57735,0.57735;2.0944rad)
  ResizeMode = 0
  Width = 108.538
FEATURE [Sketcher::SketchObject] Sketch041
  ArcFitTolerance = 1e-06
  AttachmentSupport = -> [DatumPlane004]
  FullyConstrained = false
  MakeInternals = false
  MapMode = 5
  Placement = pos=(-47,0,0) rot=(0.57735,0.57735,0.57735;2.0944rad)
  expr: Constraints[9] = <<choices>>.base_max_thickness - 3
  sketch-geometry (4):
    g0: LineSegment StartX=0 StartY=0 StartZ=0 EndX=453.094 EndY=0 EndZ=0
    g1: LineSegment StartX=453.094 StartY=0 StartZ=0 EndX=453.094 EndY=17 EndZ=0
    g2: LineSegment StartX=453.094 StartY=17 StartZ=0 EndX=0 EndY=17 EndZ=0
    g3: LineSegment StartX=0 StartY=17 StartZ=0 EndX=0 EndY=0 EndZ=0
  constraints (10):
    c: Coincident(g0,g1)
    c: Coincident(g1,g2)
    c: Coincident(g2,g3)
    c: Coincident(g3,g0)
    c: Horizontal(g0)
    c: Horizontal(g2)
    c: Vertical(g1)
    c: Vertical(g3)
    c: Coincident(g0,g-1)
    c: DistanceY(g3,g3) = 17
FEATURE [Sketcher::SketchObject] Sketch042
  ArcFitTolerance = 1e-06
  AttachmentSupport = -> [XY_Plane005]
  FullyConstrained = true
  MakeInternals = false
  MapMode = 5
  sketch-geometry (8):
    g0: LineSegment [constr] StartX=0 StartY=0 StartZ=0 EndX=170 EndY=0 EndZ=0
    g1: LineSegment [constr] StartX=170 StartY=0 StartZ=0 EndX=170 EndY=170 EndZ=0
    g2: LineSegment [constr] StartX=170 StartY=170 StartZ=0 EndX=0 EndY=170 EndZ=0
    g3: LineSegment [constr] StartX=0 StartY=170 StartZ=0 EndX=0 EndY=0 EndZ=0
    g4: LineSegment StartX=43 StartY=122 StartZ=0 EndX=43 EndY=42 EndZ=0
    g5: LineSegment StartX=43 StartY=42 StartZ=0 EndX=153 EndY=42 EndZ=0
    g6: LineSegment StartX=153 StartY=42 StartZ=0 EndX=153 EndY=122 EndZ=0
    g7: LineSegment StartX=153 StartY=122 StartZ=0 EndX=43 EndY=122 EndZ=0
  constraints (23):
    c: Coincident(g0,g1)
    c: Coincident(g1,g2)
    c: Coincident(g2,g3)
    c: Coincident(g3,g0)
    c: Horizontal(g0)
    c: Horizontal(g2)
    c: Vertical(g1)
    c: Vertical(g3)
    c: Distance(g1,g3) = 170
    c: Distance(g0,g2) = 170
    c: Coincident(g0,g-1)
    c: Coincident(g4,g5)
    c: Coincident(g5,g6)
    c: Coincident(g6,g7)
    c: Coincident(g7,g4)
    c: Vertical(g4)
    c: Vertical(g6)
    c: Horizontal(g5)
    c: Horizontal(g7)
    c: Distance(g4,g6) = 110
    c: Distance(g5,g7) = 80
    c: Distance(g5,g1) = 17
    c: DistanceY(g5) = 42
FEATURE [PartDesign::Pad] Pad022
  BaseFeature = -> Pad007
  Direction = (0,0,1)
  Length = 36
  Length2 = 10
  Profile = -> Sketch042
  ReferenceAxis = -> Sketch042 [N_Axis]
  Refine = true
  Suppressed = false
  Type = 0
FEATURE [Sketcher::SketchObject] Sketch043
  ArcFitTolerance = 1e-06
  AttachmentSupport = -> [XY_Plane015]
  FullyConstrained = false
  MakeInternals = false
  MapMode = 5
  expr: Constraints[10] = <<choices>>.shroud_mb_space + <<components>>.fan_w
  expr: Constraints[22] = <<components>>.fan_w
  expr: Constraints[26] = 4 + 4 * <<components>>.fan_h + 4 * <<choices>>.fan_gap
  expr: Constraints[9] = <<components>>.frame_h
  sketch-geometry (12):
    g0: LineSegment [constr] StartX=0 StartY=229.5 StartZ=0 EndX=-46 EndY=229.5 EndZ=0
    g1: LineSegment [constr] StartX=-46 StartY=229.5 StartZ=0 EndX=-46 EndY=0 EndZ=0
    g2: LineSegment [constr] StartX=-46 StartY=0 StartZ=0 EndX=0 EndY=0 EndZ=0
    g3: LineSegment [constr] StartX=0 StartY=0 StartZ=0 EndX=0 EndY=229.5 EndZ=0
    g4: LineSegment StartX=-46 StartY=224.5 StartZ=0 EndX=0 EndY=224.5 EndZ=0
    g5: LineSegment StartX=0 StartY=224.5 StartZ=0 EndX=0 EndY=212 EndZ=0
    g6: LineSegment StartX=0 StartY=212 StartZ=0 EndX=-17 EndY=212 EndZ=0
    g7: LineSegment StartX=-17 StartY=212 StartZ=0 EndX=-24.2296 EndY=209.005 EndZ=0
    g8: LineSegment StartX=-46 StartY=185 StartZ=0 EndX=-46 EndY=224.5 EndZ=0
    g9: LineSegment StartX=-37.554 StartY=195.681 StartZ=0 EndX=-24.2296 EndY=209.005 EndZ=0
    g10: LineSegment StartX=-46 StartY=185 StartZ=0 EndX=-43 EndY=185 EndZ=0
    g11: LineSegment StartX=-43 StartY=185 StartZ=0 EndX=-37.554 EndY=195.681 EndZ=0
  constraints (33):
    c: Coincident(g0,g1)
    c: Coincident(g1,g2)
    c: Coincident(g2,g3)
    c: Coincident(g3,g0)
    c: Horizontal(g0)
    c: Horizontal(g2)
    c: Vertical(g1)
    c: Vertical(g3)
    c: Coincident(g2,g-1)
    c: DistanceY(g1,g1) = 229.5
    c: DistanceX(g0,g0) = 46
    c: PointOnObject(g4,g1)
    c: PointOnObject(g4,g3)
    c: Horizontal(g4)
    c: Coincident(g4,g5)
    c: PointOnObject(g5,g3)
    c: Coincident(g5,g6)
    c: Horizontal(g6)
    c: Coincident(g6,g7)
    c: PointOnObject(g8,g1)
    c: Coincident(g8,g4)
    c: Distance(g4,g0) = 5
    c: DistanceX(g6,g6) = 17
    c: Angle(g7) = -2.74889
    c: Coincident(g9,g7)
    c: Angle(g9) = 0.785398
    c: DistanceY(g5) = 212
    c: Coincident(g8,g10)
    c: Horizontal(g10)
    c: Coincident(g10,g11)
    c: Coincident(g11,g9)
    c: DistanceY(g10) = 185
    c: DistanceX(g10,g10) = 3
FEATURE [PartDesign::Pad] Pad023
  BaseFeature = -> Pad021
  Direction = (0,0,1)
  Length = 55
  Length2 = 10
  Profile = -> Sketch043
  ReferenceAxis = -> Sketch043 [N_Axis]
  Refine = true
  Suppressed = false
  Type = 0
  expr: Length = <<choices>>.exit_height
FEATURE [PartDesign::Fillet] Fillet
  Base = -> Pad023 [Edge24]
  BaseFeature = -> Pad023
  Radius = 1
  Refine = true
  SupportTransform = false
  Suppressed = false
  UseAllEdges = false
  expr: Radius = <<choices>>.corner
FEATURE [PartDesign::Pocket] Pocket008
  BaseFeature = -> Fillet
  Direction = (-1,0,0)
  Length = 5
  Length2 = 5
  Midplane = true
  Profile = -> Sketch022
  ReferenceAxis = -> Sketch022 [N_Axis]
  Refine = true
  Suppressed = false
  Type = 1
FEATURE [PartDesign::SubtractiveLoft] SubtractiveLoft
  BaseFeature = -> Pocket008
  Closed = false
  Profile = -> Sketch023
  Refine = true
  Ruled = false
  Sections = -> [Sketch025]
  Suppressed = false
FEATURE [PartDesign::AdditiveLoft] AdditiveLoft
  BaseFeature = -> SubtractiveLoft
  Closed = false
  Profile = -> Sketch026
  Refine = true
  Ruled = false
  Sections = -> [Sketch027]
  Suppressed = false
FEATURE [PartDesign::LinearPattern] LinearPattern001
  BaseFeature = -> AdditiveLoft
  Direction = -> Sketch026 [H_Axis]
  Length = 156
  Mode = 1
  Occurrences = 4
  Offset = 52
  Originals = -> [AdditiveLoft]
  Refine = true
  Suppressed = false
  TransformMode = 0
  expr: Offset = <<choices>>.fan_gap + 50
FEATURE [PartDesign::Pocket] Pocket011
  BaseFeature = -> LinearPattern001
  Direction = (-1,0,0)
  Length = 3.9
  Length2 = 5
  Profile = -> Sketch041
  ReferenceAxis = -> Sketch041 [N_Axis]
  Refine = true
  Reversed = true
  Suppressed = false
  Type = 0
FEATURE [Sketcher::SketchObject] Sketch044  label="bottom plate screwholes"
  ArcFitTolerance = 1e-06
  AttachmentSupport = -> [XY_Plane015]
  FullyConstrained = false
  MakeInternals = false
  MapMode = 5
  expr: Constraints[10] = <<choices>>.screwhole_edge_margin + 3
  expr: Constraints[11] = <<choices>>.exit_w - <<choices>>.screwhole_edge_margin
  expr: Constraints[14] = <<components>>.m3_hole
  expr: Constraints[16] = <<components>>.m3_insert_r
  expr: Constraints[23] = <<components>>.fan_w + <<choices>>.exit_w + <<choices>>.shroud_mb_space - 2 * <<choices>>.screwhole_edge_margin - 3
  expr: Constraints[5] = <<components>>.frame_h
  expr: Constraints[6] = <<choices>>.screwhole_edge_margin + 3
  sketch-geometry (9):
    g0: Circle CenterX=14 CenterY=8 CenterZ=0 NormalX=0 NormalY=0 NormalZ=1 AngleXU=0 Radius=1.75
    g1: Circle CenterX=14 CenterY=221.5 CenterZ=0 NormalX=0 NormalY=0 NormalZ=1 AngleXU=0 Radius=3
    g2: LineSegment [constr] StartX=14 StartY=221.5 StartZ=0 EndX=14 EndY=8 EndZ=0
    g3: LineSegment [constr] StartX=-60.7131 StartY=0 StartZ=0 EndX=-60.7131 EndY=229.5 EndZ=0
    g4: LineSegment [constr] StartX=14 StartY=221.5 StartZ=0 EndX=-60.7131 EndY=221.5 EndZ=0
    g5: Circle CenterX=14 CenterY=114.75 CenterZ=0 NormalX=0 NormalY=0 NormalZ=1 AngleXU=0 Radius=1.75
    g6: Circle CenterX=14 CenterY=213.5 CenterZ=0 NormalX=0 NormalY=0 NormalZ=1 AngleXU=0 Radius=2.25
    g7: Circle CenterX=14 CenterY=221.5 CenterZ=0 NormalX=0 NormalY=0 NormalZ=1 AngleXU=0 Radius=1.75
    g8: Circle CenterX=-38 CenterY=221.5 CenterZ=0 NormalX=0 NormalY=0 NormalZ=1 AngleXU=0 Radius=2.25
  constraints (24):
    c: Coincident(g2,g1)
    c: Coincident(g2,g0)
    c: Vertical(g2)
    c: PointOnObject(g3,g-1)
    c: Vertical(g3)
    c: DistanceY(g3,g3) = 229.5
    c: DistanceY(g0) = 8
    c: Coincident(g4,g1)
    c: PointOnObject(g4,g3)
    c: Horizontal(g4)
    c: Distance(g3,g4) = 8
    c: DistanceX(g0) = 14
    c: Equal(g5,g0)
    c: Diameter(g1) = 6
    c: Diameter(g0) = 3.5
    c: PointOnObject(g6,g2)
    c: Diameter(g6) = 4.5
    c: Distance(g1,g6) = 8
    c: Symmetric(g2,g2,g5)
    c: Coincident(g7,g1)
    c: Equal(g7,g5)
    c: PointOnObject(g8,g4)
    c: Equal(g6,g8)
    c: Distance(g8,g2) = 52
FEATURE [Sketcher::SketchObject] Sketch045
  ArcFitTolerance = 1e-06
  AttachmentSupport = -> [XY_Plane013]
  FullyConstrained = false
  MakeInternals = false
  MapMode = 5
  expr: Constraints[19] = <<choices>>.corner
  expr: Constraints[26] = 3 + <<choices>>.screwhole_edge_margin
  expr: Constraints[29] = <<components>>.fan_w + <<choices>>.exit_w + <<choices>>.shroud_mb_space - <<choices>>.screwhole_edge_margin - 3
  expr: Constraints[39] = <<components>>.frame_h
  expr: Constraints[52] = <<choices>>.corner
  expr: Constraints[7] = <<choices>>.screwhole_edge_margin * 2
  expr: Constraints[8] = <<components>>.frame_h
  expr: Constraints[9] = <<components>>.frame_w
  sketch-geometry (21):
    g0: LineSegment StartX=365 StartY=0 StartZ=0 EndX=374 EndY=0 EndZ=0
    g1: LineSegment StartX=375 StartY=1 StartZ=0 EndX=375 EndY=228.5 EndZ=0
    g2: LineSegment StartX=374 StartY=229.5 StartZ=0 EndX=365 EndY=229.5 EndZ=0
    g3: LineSegment StartX=365 StartY=229.5 StartZ=0 EndX=365 EndY=0 EndZ=0
    g4: ArcOfCircle CenterX=374 CenterY=1 CenterZ=0 NormalX=0 NormalY=0 NormalZ=1 AngleXU=0 Radius=1 StartAngle=4.71239 EndAngle=6.28319
    g5: GeomPoint [constr] X=375 Y=0 Z=0
    g6: ArcOfCircle CenterX=374 CenterY=228.5 CenterZ=0 NormalX=0 NormalY=0 NormalZ=1 AngleXU=0 Radius=1 StartAngle=-3.6e-15 EndAngle=1.5708
    g7: GeomPoint [constr] X=375 Y=229.5 Z=0
    g8: LineSegment StartX=323 StartY=221.5 StartZ=0 EndX=323 EndY=228.5 EndZ=0
    g9: LineSegment StartX=323 StartY=228.5 StartZ=0 EndX=313 EndY=228.5 EndZ=0
    g10: LineSegment StartX=313 StartY=228.5 StartZ=0 EndX=313 EndY=221.5 EndZ=0
    g11: LineSegment StartX=0 StartY=228.5 StartZ=0 EndX=0 EndY=185.5 EndZ=0
    g12: LineSegment StartX=0 StartY=185.5 StartZ=0 EndX=10 EndY=185.5 EndZ=0
    g13: LineSegment StartX=10 StartY=185.5 StartZ=0 EndX=10 EndY=229.5 EndZ=0
    g14: LineSegment StartX=10 StartY=229.5 StartZ=0 EndX=1 EndY=229.5 EndZ=0
    g15: ArcOfCircle [constr] CenterX=318 CenterY=221.5 CenterZ=0 NormalX=0 NormalY=0 NormalZ=1 AngleXU=0 Radius=5 StartAngle=3.14159 EndAngle=4.71239
    g16: ArcOfCircle CenterX=318 CenterY=221.5 CenterZ=0 NormalX=0 NormalY=0 NormalZ=1 AngleXU=0 Radius=5 StartAngle=4.71239 EndAngle=6.28319
    g17: LineSegment StartX=313 StartY=221.5 StartZ=0 EndX=313 EndY=216.5 EndZ=0
    g18: LineSegment StartX=313 StartY=216.5 StartZ=0 EndX=318 EndY=216.5 EndZ=0
    g19: ArcOfCircle CenterX=1 CenterY=228.5 CenterZ=0 NormalX=0 NormalY=0 NormalZ=1 AngleXU=0 Radius=1 StartAngle=1.5708 EndAngle=3.14159
    g20: GeomPoint [constr] X=0 Y=229.5 Z=0
  constraints (54):
    c: Coincident(g2,g3)
    c: Coincident(g3,g0)
    c: Horizontal(g0)
    c: Horizontal(g2)
    c: Vertical(g1)
    c: Vertical(g3)
    c: PointOnObject(g0,g-1)
    c: DistanceX(g2,g7) = 10
    c: DistanceY(g5,g7) = 229.5
    c: DistanceX(g5) = 375
    c: PointOnObject(g5,g0)
    c: PointOnObject(g5,g1)
    c: Tangent(g0,g4) = -1.5708
    c: Tangent(g1,g4) = -1.5708
    c: PointOnObject(g7,g1)
    c: PointOnObject(g7,g2)
    c: Tangent(g1,g6) = -1.5708
    c: Tangent(g2,g6) = -1.5708
    c: Equal(g4,g6)
    c: Radius(g4) = 1
    c: Coincident(g8,g9)
    c: Coincident(g9,g10)
    c: Horizontal(g9)
    c: Vertical(g8)
    c: Vertical(g10)
    c: Distance(g8,g2) = 1
    c: Distance(g15,g2) = 8
    c: Tangent(g16,g8) = -1.5708
    c: Tangent(g15,g10) = -1.5708
    c: Distance(g15,g1) = 57
    c: Coincident(g11,g12)
    c: Coincident(g12,g13)
    c: Coincident(g13,g14)
    c: Vertical(g11)
    c: Vertical(g13)
    c: Horizontal(g12)
    c: Horizontal(g14)
    c: Distance(g20,g13) = 10
    c: Distance(g12,g20) = 44
    c: DistanceY(g20) = 229.5
    c: Coincident(g15,g16)
    c: Coincident(g15,g16)
    c: Diameter(g15) = 10
    c: Coincident(g10,g17)
    c: Vertical(g17)
    c: Coincident(g17,g18)
    c: Coincident(g18,g15)
    c: Horizontal(g18)
    c: PointOnObject(g20,g11)
    c: PointOnObject(g20,g14)
    c: Tangent(g11,g19) = -1.5708
    c: Tangent(g14,g19) = -1.5708
    c: Radius(g19) = 1
    c: PointOnObject(g11,g-2)
FEATURE [PartDesign::Pad] Pad024  label="3mm thick at the right end"
  BaseFeature = -> Pad020
  Direction = (0,0,1)
  Length = 3
  Length2 = 10
  Profile = -> Sketch045
  ReferenceAxis = -> Sketch045 [N_Axis]
  Refine = true
  Suppressed = false
  Type = 0
FEATURE [Sketcher::SketchObject] Sketch046
  ArcFitTolerance = 1e-06
  AttachmentSupport = -> [XY_Plane013]
  FullyConstrained = true
  MakeInternals = false
  MapMode = 5
  expr: Constraints[19] = <<components>>.fan_w + <<choices>>.exit_w + <<choices>>.shroud_mb_space - 2 * <<choices>>.screwhole_edge_margin - 3
  expr: Constraints[25] = <<choices>>.screwhole_edge_margin
  expr: Constraints[26] = <<choices>>.screwhole_edge_margin + 3
  expr: Constraints[2] = <<components>>.frame_h
  expr: Constraints[3] = <<components>>.frame_w - <<choices>>.screwhole_edge_margin
  expr: Constraints[6] = <<components>>.m3_hole
  expr: Constraints[7] = 3 + <<choices>>.screwhole_edge_margin
  expr: Constraints[8] = 3 + <<choices>>.screwhole_edge_margin
  sketch-geometry (10):
    g0: LineSegment [constr] StartX=370 StartY=0 StartZ=0 EndX=370 EndY=229.5 EndZ=0
    g1: Circle CenterX=370 CenterY=221.5 CenterZ=0 NormalX=0 NormalY=0 NormalZ=1 AngleXU=0 Radius=3
    g2: Circle CenterX=370 CenterY=8 CenterZ=0 NormalX=0 NormalY=0 NormalZ=1 AngleXU=0 Radius=1.75
    g3: Circle CenterX=370 CenterY=114.75 CenterZ=0 NormalX=0 NormalY=0 NormalZ=1 AngleXU=0 Radius=1.75
    g4: Circle CenterX=370 CenterY=213.5 CenterZ=0 NormalX=0 NormalY=0 NormalZ=1 AngleXU=0 Radius=1.75
    g5: Circle CenterX=318 CenterY=221.5 CenterZ=0 NormalX=0 NormalY=0 NormalZ=1 AngleXU=0 Radius=1.75
    g6: LineSegment [constr] StartX=318 StartY=221.5 StartZ=0 EndX=370 EndY=221.5 EndZ=0
    g7: LineSegment [constr] StartX=5 StartY=0 StartZ=0 EndX=5 EndY=221.5 EndZ=0
    g8: Circle CenterX=5 CenterY=8 CenterZ=0 NormalX=0 NormalY=0 NormalZ=1 AngleXU=0 Radius=1.75
    g9: Circle CenterX=5 CenterY=221.5 CenterZ=0 NormalX=0 NormalY=0 NormalZ=1 AngleXU=0 Radius=1.75
  constraints (29):
    c: PointOnObject(g0,g-1)
    c: Vertical(g0)
    c: DistanceY(g0,g0) = 229.5
    c: DistanceX(g0) = 370
    c: PointOnObject(g1,g0)
    c: PointOnObject(g2,g0)
    c: Diameter(g2) = 3.5
    c: DistanceY(g2) = 8
    c: Distance(g1,g0) = 8
    c: Symmetric(g0,g0,g3)
    c: Equal(g2,g3)
    c: PointOnObject(g4,g0)
    c: Equal(g3,g4)
    c: Distance(g4,g1) = 8
    c: Diameter(g1) = 6
    c: Equal(g5,g4)
    c: Coincident(g6,g5)
    c: Coincident(g6,g1)
    c: Horizontal(g6)
    c: DistanceX(g6,g6) = 52
    c: PointOnObject(g7,g-1)
    c: Vertical(g7)
    c: PointOnObject(g8,g7)
    c: Equal(g8,g9)
    c: Equal(g9,g4)
    c: DistanceX(g8) = 5
    c: DistanceY(g8) = 8
    c: Coincident(g7,g9)
    c: PointOnObject(g7,g6)
FEATURE [PartDesign::Pocket] Pocket012  label="right end screwholes"
  BaseFeature = -> Pad024
  Direction = (0,0,-1)
  Length = 5
  Length2 = 5
  Midplane = true
  Profile = -> Sketch046
  ReferenceAxis = -> Sketch046 [N_Axis]
  Refine = true
  Suppressed = false
  Type = 1
FEATURE [PartDesign::Chamfer] Chamfer001
  Angle = 45
  Base = -> Pocket012 [Edge662,Edge665,Edge667,Edge669,Edge670,Edge664]
  BaseFeature = -> Pocket012
  ChamferType = 0
  FlipDirection = false
  Refine = true
  Size = 1.75
  Size2 = 1
  SupportTransform = false
  Suppressed = false
  UseAllEdges = false
FEATURE [PartDesign::Pocket] Pocket013
  BaseFeature = -> Pocket011
  Direction = (0,0,-1)
  Length = 48
  Length2 = 5
  Profile = -> Sketch044 [Edge2]
  ReferenceAxis = -> Sketch044 [N_Axis]
  Refine = true
  Reversed = true
  Suppressed = false
  Type = 0
FEATURE [PartDesign::Pocket] Pocket014
  BaseFeature = -> Pocket013
  Direction = (0,0,-1)
  Length = 5
  Length2 = 5
  Profile = -> Sketch044 [Edge5]
  ReferenceAxis = -> Sketch044 [N_Axis]
  Refine = true
  Reversed = true
  Suppressed = false
  Type = 1
FEATURE [PartDesign::Pocket] Pocket015
  BaseFeature = -> Pocket014
  Direction = (0,0,-1)
  Length = 7
  Length2 = 5
  Profile = -> Sketch044 [Edge4]
  ReferenceAxis = -> Sketch044 [N_Axis]
  Refine = true
  Reversed = true
  Suppressed = false
  Type = 0
  expr: Length = <<components>>.m3_insert_depth
FEATURE [PartDesign::Pocket] Pocket016
  BaseFeature = -> Pocket015
  Direction = (0,0,-1)
  Length = 10
  Length2 = 5
  Profile = -> Sketch044 [Edge3,Edge1]
  ReferenceAxis = -> Sketch044 [N_Axis]
  Refine = true
  Reversed = true
  Suppressed = false
  Type = 0
FEATURE [PartDesign::Plane] DatumPlane005
  AttachmentOffset = pos=(0,0,1) rot=(0,0,1;0rad)
  AttachmentSupport = -> [XY_Plane015]
  Length = 97.8846
  MapMode = 5
  Placement = pos=(0,0,1) rot=(0,0,1;0rad)
  ResizeMode = 0
  Width = 281.385
FEATURE [Sketcher::SketchObject] Sketch047  label="bottom plate screwholes001"
  ArcFitTolerance = 1e-06
  AttachmentSupport = -> [DatumPlane005]
  FullyConstrained = false
  MakeInternals = false
  MapMode = 5
  Placement = pos=(0,0,1) rot=(0,0,1;0rad)
  expr: Constraints[10] = <<choices>>.screwhole_edge_margin + 3
  expr: Constraints[11] = <<choices>>.exit_w - <<choices>>.screwhole_edge_margin
  expr: Constraints[16] = <<components>>.m3_insert_r
  expr: Constraints[5] = <<components>>.frame_h
  expr: Constraints[6] = <<choices>>.screwhole_edge_margin + 3
  sketch-geometry (8):
    g0: Circle CenterX=14 CenterY=8 CenterZ=0 NormalX=0 NormalY=0 NormalZ=1 AngleXU=0 Radius=2.75
    g1: Circle [constr] CenterX=14 CenterY=221.5 CenterZ=0 NormalX=0 NormalY=0 NormalZ=1 AngleXU=0 Radius=3
    g2: LineSegment [constr] StartX=14 StartY=221.5 StartZ=0 EndX=14 EndY=8 EndZ=0
    g3: LineSegment [constr] StartX=-60.7131 StartY=0 StartZ=0 EndX=-60.7131 EndY=229.5 EndZ=0
    g4: LineSegment [constr] StartX=14 StartY=221.5 StartZ=0 EndX=-60.7131 EndY=221.5 EndZ=0
    g5: Circle CenterX=14 CenterY=114.75 CenterZ=0 NormalX=0 NormalY=0 NormalZ=1 AngleXU=0 Radius=2.75
    g6: Circle [constr] CenterX=14 CenterY=213.5 CenterZ=0 NormalX=0 NormalY=0 NormalZ=1 AngleXU=0 Radius=2.25
    g7: Circle [constr] CenterX=14 CenterY=221.5 CenterZ=0 NormalX=0 NormalY=0 NormalZ=1 AngleXU=0 Radius=2.75
  constraints (21):
    c: Coincident(g2,g1)
    c: Coincident(g2,g0)
    c: Vertical(g2)
    c: PointOnObject(g3,g-1)
    c: Vertical(g3)
    c: DistanceY(g3,g3) = 229.5
    c: DistanceY(g0) = 8
    c: Coincident(g4,g1)
    c: PointOnObject(g4,g3)
    c: Horizontal(g4)
    c: Distance(g3,g4) = 8
    c: DistanceX(g0) = 14
    c: Equal(g5,g0)
    c: Diameter(g1) = 6
    c: Diameter(g0) = 5.5
    c: PointOnObject(g6,g2)
    c: Diameter(g6) = 4.5
    c: Distance(g1,g6) = 8
    c: Symmetric(g2,g2,g5)
    c: Coincident(g7,g1)
    c: Equal(g7,g5)
FEATURE [PartDesign::Pocket] Pocket017
  BaseFeature = -> Pocket016
  Direction = (0,0,-1)
  Length = 4
  Length2 = 5
  Profile = -> Sketch047
  ReferenceAxis = -> Sketch047 [N_Axis]
  Refine = true
  Reversed = true
  Suppressed = false
  Type = 0
FEATURE [PartDesign::Plane] DatumPlane006
  AttachmentOffset = pos=(0,0,27.5) rot=(0,0,1;0rad)
  AttachmentSupport = -> [XY_Plane015]
  Length = 97.8846
  MapMode = 5
  Placement = pos=(0,0,27.5) rot=(0,0,1;0rad)
  ResizeMode = 0
  Width = 281.385
  expr: .AttachmentOffset.Base.z = <<choices>>.exit_height / 2
FEATURE [PartDesign::Mirrored] Mirrored
  BaseFeature = -> Pocket017
  MirrorPlane = -> DatumPlane006
  Originals = -> [Pocket016,Pocket017]
  Refine = true
  Suppressed = false
  TransformMode = 0
FEATURE [App::Link] BASE  label="BASE001"
  LinkPlacement = pos=(433.794,-467.207,-15.3394) rot=(0.075569,0.096295,0.99248;0.012724rad)
  LinkedObject = -> Part006
  Placement = pos=(433.794,-467.207,-15.3394) rot=(0.075569,0.096295,0.99248;0.012724rad)
FEATURE [App::FeaturePython] GroundedJoint  # Assembly grounded joint (typed FeaturePython)
  ObjectToGround = -> BASE
  Placement = pos=(433.794,-467.207,-15.3394) rot=(0.075569,0.096295,0.99248;0.012724rad)
FEATURE [PartDesign::Fillet] Fillet001
  Base = -> Chamfer001 [Edge135]
  BaseFeature = -> Chamfer001
  Radius = 1
  Refine = true
  SupportTransform = false
  Suppressed = false
  UseAllEdges = false
  expr: Radius = <<choices>>.corner
FEATURE [Sketcher::SketchObject] Sketch048
  ArcFitTolerance = 1e-06
  AttachmentSupport = -> [XY_Plane013]
  FullyConstrained = false
  MakeInternals = false
  MapMode = 5
  expr: Constraints[18] = <<choices>>.leg_betweens
  expr: Constraints[19] = <<components>>.frame_w - <<components>>.fan_w - <<choices>>.exit_w - <<choices>>.shroud_mb_space - 170 - 14.5 + <<choices>>.leg_betweens
  expr: Constraints[20] = <<choices>>.leg_width + 2 * <<choices>>.leg_clearance
  expr: Constraints[34] = <<choices>>.leg_bracket_slot_end_dist_from_front + 10 + 1 + 5 + 1
  expr: Constraints[38] = <<components>>.m3_threadhole
  expr: Constraints[41] = <<components>>.m3_threadhole
  sketch-geometry (22):
    g0: LineSegment StartX=130.5 StartY=65.1827 StartZ=0 EndX=125.5 EndY=65.1827 EndZ=0
    g1: LineSegment StartX=125.5 StartY=65.1827 StartZ=0 EndX=125.5 EndY=82.1827 EndZ=0
    g2: LineSegment StartX=125.5 StartY=82.1827 StartZ=0 EndX=130.5 EndY=82.1827 EndZ=0
    g3: LineSegment StartX=130.5 StartY=82.1827 StartZ=0 EndX=130.5 EndY=65.1827 EndZ=0
    g4: LineSegment StartX=114.5 StartY=65.1827 StartZ=0 EndX=109.5 EndY=65.1827 EndZ=0
    g5: LineSegment StartX=114.5 StartY=187 StartZ=0 EndX=114.5 EndY=65.1827 EndZ=0
    g6: LineSegment StartX=109.5 StartY=65.1827 StartZ=0 EndX=104.5 EndY=65.1827 EndZ=0
    g7: LineSegment StartX=104.5 StartY=65.1827 StartZ=0 EndX=104.5 EndY=187 EndZ=0
    g8: LineSegment [constr] StartX=114.5 StartY=65.1827 StartZ=0 EndX=125.5 EndY=65.1827 EndZ=0
    g9: LineSegment [constr] StartX=104.5 StartY=65.1827 StartZ=0 EndX=93.5 EndY=65.1827 EndZ=0
    g10: LineSegment StartX=93.5 StartY=65.1827 StartZ=0 EndX=88.5 EndY=65.1827 EndZ=0
    g11: LineSegment StartX=88.5 StartY=65.1827 StartZ=0 EndX=88.5 EndY=82.1827 EndZ=0
    g12: LineSegment StartX=88.5 StartY=82.1827 StartZ=0 EndX=93.5 EndY=82.1827 EndZ=0
    g13: LineSegment StartX=93.5 StartY=82.1827 StartZ=0 EndX=93.5 EndY=65.1827 EndZ=0
    g14: LineSegment StartX=104.5 StartY=187 StartZ=0 EndX=114.5 EndY=187 EndZ=0
    g15: Circle CenterX=109.5 CenterY=182.5 CenterZ=0 NormalX=0 NormalY=0 NormalZ=1 AngleXU=0 Radius=1.25
    g16: LineSegment [constr] StartX=104.556 StartY=89.8173 StartZ=0 EndX=104.556 EndY=82 EndZ=0
    g17: LineSegment [constr] StartX=114.444 StartY=82.1827 StartZ=0 EndX=114.444 EndY=90.1827 EndZ=0
    g18: Circle CenterX=109.5 CenterY=86 CenterZ=0 NormalX=0 NormalY=0 NormalZ=1 AngleXU=0 Radius=1.25
    g19: LineSegment [constr] StartX=109.5 StartY=86 StartZ=0 EndX=114.5 EndY=86 EndZ=0
    g20: LineSegment [constr] StartX=109.5 StartY=86 StartZ=0 EndX=104.5 EndY=86 EndZ=0
    g21: LineSegment [constr] StartX=109.5 StartY=182.5 StartZ=0 EndX=109.5 EndY=187 EndZ=0
  constraints (61):
    c: Coincident(g0,g1)
    c: Coincident(g1,g2)
    c: Coincident(g2,g3)
    c: Coincident(g3,g0)
    c: Horizontal(g0)
    c: Horizontal(g2)
    c: Vertical(g1)
    c: Vertical(g3)
    c: Coincident(g5,g4)
    c: Horizontal(g4)
    c: Vertical(g5)
    c: Coincident(g6,g7)
    c: Horizontal(g6)
    c: Vertical(g7)
    c: Coincident(g8,g4)
    c: Coincident(g8,g0)
    c: Horizontal(g8)
    c: Equal(g0,g4)
    c: DistanceX(g0,g0) = 5
    c: DistanceX(g0) = 130.5
    c: DistanceX(g8,g8) = 11
    c: Equal(g6,g4)
    c: Coincident(g9,g6)
    c: Horizontal(g9)
    c: Coincident(g10,g11)
    c: Coincident(g11,g12)
    c: Coincident(g12,g13)
    c: Coincident(g13,g10)
    c: Horizontal(g10)
    c: Horizontal(g12)
    c: Vertical(g11)
    c: Vertical(g13)
    c: Coincident(g10,g9)
    c: Equal(g6,g10)
    c: DistanceY(g7) = 187
    c: DistanceY(g3,g3) = 17
    c: Equal(g13,g1)
    c: Horizontal(g14)
    c: Diameter(g15) = 2.5
    c: Vertical(g16)
    c: Vertical(g17)
    c: Diameter(g18) = 2.5
    c: Symmetric(g16,g17,g18)
    c: PointOnObject(g17,g2)
    c: DistanceY(g17,g17) = 8
    c: DistanceY(g18) = 86
    c: Coincident(g19,g18)
    c: PointOnObject(g19,g5)
    c: Horizontal(g19)
    c: Coincident(g20,g18)
    c: PointOnObject(g20,g7)
    c: Horizontal(g20)
    c: Equal(g19,g20)
    c: Coincident(g21,g15)
    c: Symmetric(g14,g14,g21)
    c: DistanceY(g21,g21) = 4.5
    c: Equal(g9,g8)
    c: Coincident(g6,g4)
    c: Coincident(g14,g7)
    c: Coincident(g14,g5)
    c: Vertical(g21)
FEATURE [Sketcher::SketchObject] Sketch049
  ArcFitTolerance = 1e-06
  AttachmentSupport = -> [XY_Plane013]
  FullyConstrained = false
  MakeInternals = false
  MapMode = 5
  expr: Constraints[29] = <<choices>>.leg_betweens
  expr: Constraints[30] = <<components>>.frame_w - <<components>>.fan_w - <<choices>>.exit_w - <<choices>>.shroud_mb_space - 170 - 14.5 + <<choices>>.leg_betweens
  expr: Constraints[31] = <<choices>>.leg_width + 2 * <<choices>>.leg_clearance
  expr: Constraints[45] = <<choices>>.leg_axis_dist_from_front
  sketch-geometry (21):
    g0: LineSegment [constr] StartX=130.5 StartY=68 StartZ=0 EndX=125.5 EndY=68 EndZ=0
    g1: LineSegment StartX=125.5 StartY=68 StartZ=0 EndX=125.5 EndY=194.23 EndZ=0
    g2: LineSegment [constr] StartX=125.5 StartY=194.23 StartZ=0 EndX=130.5 EndY=194.23 EndZ=0
    g3: LineSegment [constr] StartX=130.5 StartY=194.23 StartZ=0 EndX=130.5 EndY=68 EndZ=0
    g4: LineSegment [constr] StartX=114.5 StartY=68 StartZ=0 EndX=109.5 EndY=68 EndZ=0
    g5: LineSegment [constr] StartX=109.5 StartY=68 StartZ=0 EndX=109.5 EndY=194.23 EndZ=0
    g6: LineSegment [constr] StartX=109.5 StartY=194.23 StartZ=0 EndX=114.5 EndY=194.23 EndZ=0
    g7: LineSegment StartX=114.5 StartY=194.23 StartZ=0 EndX=114.5 EndY=68 EndZ=0
    g8: LineSegment [constr] StartX=109.5 StartY=68 StartZ=0 EndX=104.5 EndY=68 EndZ=0
    g9: LineSegment StartX=104.5 StartY=68 StartZ=0 EndX=104.5 EndY=194.23 EndZ=0
    g10: LineSegment [constr] StartX=104.5 StartY=194.23 StartZ=0 EndX=109.5 EndY=194.23 EndZ=0
    g11: LineSegment [constr] StartX=109.5 StartY=194.23 StartZ=0 EndX=109.5 EndY=68 EndZ=0
    g12: LineSegment StartX=114.5 StartY=68 StartZ=0 EndX=125.5 EndY=68 EndZ=0
    g13: LineSegment StartX=104.5 StartY=68 StartZ=0 EndX=93.5 EndY=68 EndZ=0
    g14: LineSegment [constr] StartX=93.5 StartY=68 StartZ=0 EndX=88.5 EndY=68 EndZ=0
    g15: LineSegment [constr] StartX=88.5 StartY=68 StartZ=0 EndX=88.5 EndY=194.23 EndZ=0
    g16: LineSegment [constr] StartX=88.5 StartY=194.23 StartZ=0 EndX=93.5 EndY=194.23 EndZ=0
    g17: LineSegment StartX=93.5 StartY=194.23 StartZ=0 EndX=93.5 EndY=68 EndZ=0
    g18: GeomPoint X=77.5 Y=75 Z=0
    g19: LineSegment StartX=93.5 StartY=194.23 StartZ=0 EndX=104.5 EndY=194.23 EndZ=0
    g20: LineSegment StartX=114.5 StartY=194.23 StartZ=0 EndX=125.5 EndY=194.23 EndZ=0
  constraints (56):
    c: Coincident(g0,g1)
    c: Coincident(g1,g2)
    c: Coincident(g2,g3)
    c: Coincident(g3,g0)
    c: Horizontal(g0)
    c: Horizontal(g2)
    c: Vertical(g1)
    c: Vertical(g3)
    c: Coincident(g4,g5)
    c: Coincident(g5,g6)
    c: Coincident(g6,g7)
    c: Coincident(g7,g4)
    c: Horizontal(g4)
    c: Horizontal(g6)
    c: Vertical(g5)
    c: Vertical(g7)
    c: Coincident(g8,g9)
    c: Coincident(g9,g10)
    c: Coincident(g10,g11)
    c: Coincident(g11,g8)
    c: Horizontal(g8)
    c: Horizontal(g10)
    c: Vertical(g9)
    c: Vertical(g11)
    c: Coincident(g12,g4)
    c: Coincident(g12,g0)
    c: Horizontal(g12)
    c: Equal(g0,g4)
    c: Equal(g11,g5)
    c: DistanceX(g0,g0) = 5
    c: DistanceX(g0) = 130.5
    c: DistanceX(g12,g12) = 11
    c: Equal(g8,g4)
    c: Coincident(g13,g8)
    c: Horizontal(g13)
    c: Coincident(g14,g15)
    c: Coincident(g15,g16)
    c: Coincident(g16,g17)
    c: Coincident(g17,g14)
    c: Horizontal(g14)
    c: Horizontal(g16)
    c: Vertical(g15)
    c: Vertical(g17)
    c: Coincident(g14,g13)
    c: Equal(g8,g14)
    c: DistanceY(g18) = 75
    c: Equal(g17,g1)
    c: Distance(g18,g13) = 7
    c: Coincident(g19,g16)
    c: Coincident(g19,g9)
    c: Coincident(g20,g6)
    c: Coincident(g20,g1)
    c: Horizontal(g19)
    c: DistanceY(g16) = 194.23
    c: Equal(g13,g12)
    c: Coincident(g8,g4)
FEATURE [PartDesign::Plane] DatumPlane007
  AttachmentOffset = pos=(0,0,109.5) rot=(0,0,1;0rad)
  AttachmentSupport = -> [YZ_Plane013]
  Length = 277.061
  MapMode = 5
  Placement = pos=(109.5,0,0) rot=(0.57735,0.57735,0.57735;2.0944rad)
  ResizeMode = 0
  Width = 72.561
FEATURE [Sketcher::SketchObject] Sketch050
  ArcFitTolerance = 1e-06
  AttachmentSupport = -> [DatumPlane007]
  FullyConstrained = false
  MakeInternals = false
  MapMode = 5
  Placement = pos=(109.5,0,0) rot=(0.57735,0.57735,0.57735;2.0944rad)
  expr: Constraints[33] = <<choices>>.leg_axle_hole_dia
  expr: Constraints[77] = <<choices>>.leg_axle_hole_dia / 2
  expr: Constraints[78] = <<choices>>.leg_axis_dist_from_front
  expr: Constraints[8] = <<choices>>.leg_bracket_slot_end_dist_from_front - <<choices>>.leg_bracket_slot_start_dist_from_front - 1
  expr: Constraints[9] = <<choices>>.leg_bracket_slot_end_dist_from_front + 0.5 * <<choices>>.leg_axle_hole_dia + 1
  sketch-geometry (29):
    g0: LineSegment StartX=173.6 StartY=7.5 StartZ=0 EndX=173.6 EndY=12.5 EndZ=0
    g1: LineSegment [constr] StartX=173.6 StartY=12.5 StartZ=0 EndX=112.764 EndY=12.5 EndZ=0
    g2: LineSegment StartX=119.6 StartY=12.5 StartZ=0 EndX=119.6 EndY=7.5 EndZ=0
    g3: LineSegment [constr] StartX=119.6 StartY=7.5 StartZ=0 EndX=173.6 EndY=7.5 EndZ=0
    g4: LineSegment StartX=173.6 StartY=12.5 StartZ=0 EndX=168.4 EndY=12.5 EndZ=0
    g5: LineSegment StartX=168.4 StartY=12.5 StartZ=0 EndX=164.6 EndY=7.5 EndZ=0
    g6: LineSegment StartX=164.6 StartY=7.5 StartZ=0 EndX=164.6 EndY=12.5 EndZ=0
    g7: LineSegment StartX=164.6 StartY=12.5 StartZ=0 EndX=159.4 EndY=12.5 EndZ=0
    g8: LineSegment StartX=159.4 StartY=12.5 StartZ=0 EndX=155.6 EndY=7.5 EndZ=0
    g9: LineSegment StartX=155.6 StartY=7.5 StartZ=0 EndX=155.6 EndY=12.5 EndZ=0
    g10: LineSegment StartX=155.6 StartY=12.5 StartZ=0 EndX=150.4 EndY=12.5 EndZ=0
    g11: LineSegment StartX=150.4 StartY=12.5 StartZ=0 EndX=146.6 EndY=7.5 EndZ=0
    g12: LineSegment StartX=146.6 StartY=7.5 StartZ=0 EndX=146.6 EndY=12.5 EndZ=0
    g13: LineSegment StartX=146.6 StartY=12.5 StartZ=0 EndX=141.4 EndY=12.5 EndZ=0
    g14: LineSegment StartX=141.4 StartY=12.5 StartZ=0 EndX=137.6 EndY=7.5 EndZ=0
    g15: LineSegment StartX=137.6 StartY=7.5 StartZ=0 EndX=137.6 EndY=12.5 EndZ=0
    g16: LineSegment StartX=137.6 StartY=12.5 StartZ=0 EndX=132.4 EndY=12.5 EndZ=0
    g17: LineSegment StartX=132.4 StartY=12.5 StartZ=0 EndX=128.6 EndY=7.5 EndZ=0
    g18: LineSegment StartX=128.6 StartY=7.5 StartZ=0 EndX=128.6 EndY=12.5 EndZ=0
    g19: LineSegment StartX=128.6 StartY=12.5 StartZ=0 EndX=123.4 EndY=12.5 EndZ=0
    g20: LineSegment StartX=123.4 StartY=12.5 StartZ=0 EndX=119.6 EndY=7.5 EndZ=0
    g21: LineSegment StartX=119.6 StartY=12.5 StartZ=0 EndX=107 EndY=12.5 EndZ=0
    g22: LineSegment StartX=107 StartY=12.5 StartZ=0 EndX=107 EndY=-4.82574 EndZ=0
    g23: LineSegment StartX=107 StartY=-4.82574 StartZ=0 EndX=173.6 EndY=-4.82574 EndZ=0
    g24: LineSegment StartX=173.6 StartY=-4.82574 StartZ=0 EndX=173.6 EndY=7.5 EndZ=0
    g25: ArcOfCircle CenterX=75 CenterY=5.87086 CenterZ=0 NormalX=0 NormalY=0 NormalZ=1 AngleXU=0 Radius=2.6 StartAngle=2e-16 EndAngle=3.14159
    g26: ArcOfCircle CenterX=75 CenterY=-13.8999 CenterZ=0 NormalX=0 NormalY=0 NormalZ=1 AngleXU=0 Radius=2.6 StartAngle=3.14159 EndAngle=6.28319
    g27: LineSegment StartX=77.6 StartY=5.87086 StartZ=0 EndX=77.6 EndY=-13.8999 EndZ=0
    g28: LineSegment StartX=72.4 StartY=5.87086 StartZ=0 EndX=72.4 EndY=-13.8999 EndZ=0
  constraints (79):
    c: Vertical(g0)
    c: Coincident(g1,g0)
    c: Horizontal(g1)
    c: PointOnObject(g2,g1)
    c: Vertical(g2)
    c: Coincident(g3,g2)
    c: Coincident(g3,g0)
    c: Horizontal(g3)
    c: DistanceX(g2,g0) = 54
    c: DistanceX(g0) = 173.6
    c: Coincident(g0,g4)
    c: PointOnObject(g4,g1)
    c: Coincident(g4,g5)
    c: PointOnObject(g5,g3)
    c: Coincident(g5,g6)
    c: PointOnObject(g6,g1)
    c: Vertical(g6)
    c: Coincident(g6,g7)
    c: PointOnObject(g7,g1)
    c: Coincident(g7,g8)
    c: PointOnObject(g8,g3)
    c: Coincident(g8,g9)
    c: PointOnObject(g9,g1)
    c: Vertical(g9)
    c: Coincident(g9,g10)
    c: PointOnObject(g10,g1)
    c: Coincident(g10,g11)
    c: PointOnObject(g11,g3)
    c: Coincident(g11,g12)
    c: Coincident(g12,g13)
    c: PointOnObject(g13,g1)
    c: Coincident(g13,g14)
    c: Vertical(g12)
    c: DistanceX(g4,g4) = 5.2
    c: Equal(g4,g7)
    c: Equal(g7,g10)
    c: Equal(g10,g13)
    c: Equal(g5,g8)
    c: Equal(g8,g11)
    c: Equal(g11,g14)
    c: Coincident(g14,g15)
    c: PointOnObject(g15,g1)
    c: Vertical(g15)
    c: Coincident(g15,g16)
    c: PointOnObject(g16,g1)
    c: Coincident(g16,g17)
    c: Coincident(g17,g18)
    c: PointOnObject(g18,g1)
    c: Vertical(g18)
    c: Coincident(g18,g19)
    c: PointOnObject(g19,g1)
    c: Coincident(g19,g20)
    c: Coincident(g20,g2)
    c: Coincident(g2,g21)
    c: PointOnObject(g21,g1)
    c: Coincident(g21,g22)
    c: Vertical(g22)
    c: Coincident(g22,g23)
    c: Horizontal(g23)
    c: Coincident(g23,g24)
    c: Coincident(g24,g0)
    c: Vertical(g24)
    c: Equal(g19,g16)
    c: Equal(g16,g13)
    c: Equal(g20,g17)
    c: Equal(g17,g14)
    c: PointOnObject(g14,g3)
    c: PointOnObject(g17,g3)
    c: DistanceY(g5) = 7.5
    c: Horizontal(g13)
    c: DistanceY(g0) = 12.5
    c: Tangent(g25,g27) = 1.5708
    c: Tangent(g25,g28) = -1.5708
    c: Tangent(g26,g27) = 1.5708
    c: Tangent(g26,g28) = -1.5708
    c: Equal(g25,g26)
    c: Vertical(g27)
    c: Radius(g25) = 2.6
    c: DistanceX(g25) = 75
FEATURE [Sketcher::SketchObject] Sketch051
  ArcFitTolerance = 1e-06
  AttachmentSupport = -> [DatumPlane007]
  FullyConstrained = true
  MakeInternals = false
  MapMode = 5
  Placement = pos=(109.5,0,0) rot=(0.57735,0.57735,0.57735;2.0944rad)
  expr: Constraints[0] = <<choices>>.leg_axle_hole_dia
  expr: Constraints[2] = <<choices>>.leg_axis_dist_from_front
  sketch-geometry (1):
    g0: Circle CenterX=75 CenterY=5 CenterZ=0 NormalX=0 NormalY=0 NormalZ=1 AngleXU=0 Radius=2.6
  constraints (3):
    c: Diameter(g0) = 5.2
    c: DistanceY(g0) = 5
    c: DistanceX(g0) = 75
FEATURE [PartDesign::Plane] DatumPlane008
  AttachmentOffset = pos=(0,0,26) rot=(0,0,1;0rad)
  AttachmentSupport = -> [DatumPlane007]
  Length = 277.061
  MapMode = 5
  Placement = pos=(135.5,0,0) rot=(0.57735,0.57735,0.57735;2.0944rad)
  ResizeMode = 0
  Width = 72.561
FEATURE [Sketcher::SketchObject] Sketch052
  ArcFitTolerance = 1e-06
  AttachmentSupport = -> [DatumPlane008]
  FullyConstrained = false
  MakeInternals = false
  MapMode = 5
  Placement = pos=(135.5,0,0) rot=(0.57735,0.57735,0.57735;2.0944rad)
  expr: Constraints[6] = <<choices>>.leg_axle_hole_dia / 2
  expr: Constraints[8] = <<choices>>.leg_axis_dist_from_front
  sketch-geometry (4):
    g0: ArcOfCircle CenterX=75 CenterY=5 CenterZ=0 NormalX=0 NormalY=0 NormalZ=1 AngleXU=0 Radius=2.6 StartAngle=3.14159 EndAngle=6.28319
    g1: ArcOfCircle CenterX=75 CenterY=26.5817 CenterZ=0 NormalX=0 NormalY=0 NormalZ=1 AngleXU=0 Radius=2.6 StartAngle=0 EndAngle=3.14159
    g2: LineSegment StartX=72.4 StartY=5 StartZ=0 EndX=72.4 EndY=26.5817 EndZ=0
    g3: LineSegment StartX=77.6 StartY=5 StartZ=0 EndX=77.6 EndY=26.5817 EndZ=0
  constraints (9):
    c: Tangent(g0,g2) = 1.5708
    c: Tangent(g0,g3) = -1.5708
    c: Tangent(g1,g2) = 1.5708
    c: Tangent(g1,g3) = -1.5708
    c: Equal(g0,g1)
    c: Vertical(g2)
    c: Radius(g1) = 2.6
    c: DistanceY(g0) = 5
    c: DistanceX(g0) = 75
FEATURE [PartDesign::Plane] DatumPlane009
  AttachmentOffset = pos=(0,0,20) rot=(0,0,1;0rad)
  AttachmentSupport = -> [XY_Plane013]
  Length = 463.812
  MapMode = 5
  Placement = pos=(0,0,20) rot=(0,0,1;0rad)
  ResizeMode = 0
  Width = 318.312
  expr: .AttachmentOffset.Base.z = <<choices>>.base_max_thickness
FEATURE [Sketcher::SketchObject] Sketch053
  ArcFitTolerance = 1e-06
  AttachmentSupport = -> [DatumPlane009]
  FullyConstrained = false
  MakeInternals = false
  MapMode = 5
  Placement = pos=(0,0,20) rot=(0,0,1;0rad)
  sketch-geometry (4):
    g0: LineSegment StartX=60 StartY=78.4987 StartZ=0 EndX=60 EndY=68.7712 EndZ=0
    g1: LineSegment StartX=60 StartY=68.7712 StartZ=0 EndX=137.287 EndY=68.7712 EndZ=0
    g2: LineSegment StartX=137.287 StartY=68.7712 StartZ=0 EndX=137.287 EndY=78.4987 EndZ=0
    g3: LineSegment StartX=137.287 StartY=78.4987 StartZ=0 EndX=60 EndY=78.4987 EndZ=0
  constraints (9):
    c: Coincident(g0,g1)
    c: Coincident(g1,g2)
    c: Coincident(g2,g3)
    c: Coincident(g3,g0)
    c: Vertical(g0)
    c: Vertical(g2)
    c: Horizontal(g1)
    c: Horizontal(g3)
    c: DistanceX(g0) = 60
FEATURE [PartDesign::Pocket] Pocket022
  BaseFeature = -> Fillet001
  Direction = (0,0,-1)
  Length = 17.6
  Length2 = 5
  Profile = -> Sketch053
  ReferenceAxis = -> Sketch053 [N_Axis]
  Refine = true
  Suppressed = false
  Type = 0
  expr: Length = <<choices>>.base_max_thickness - 2.4
FEATURE [PartDesign::Pocket] Pocket023
  BaseFeature = -> Pocket022
  Direction = (0,0,-1)
  Length = 15
  Length2 = 5
  Profile = -> Sketch049 [Edge3,Edge1,Edge5,Edge7,Edge6,Edge4,Edge2,Edge8]
  ReferenceAxis = -> Sketch049 [N_Axis]
  Refine = true
  Reversed = true
  Suppressed = false
  Type = 0
FEATURE [PartDesign::Pad] Pad025
  BaseFeature = -> Pocket023
  Direction = (0,0,1)
  Length = 15
  Length2 = 10
  Profile = -> Sketch048
  ReferenceAxis = -> Sketch048 [N_Axis]
  Refine = true
  Suppressed = false
  Type = 0
FEATURE [Sketcher::SketchObject] Sketch054
  ArcFitTolerance = 1e-06
  AttachmentSupport = -> [XY_Plane013]
  FullyConstrained = false
  MakeInternals = false
  MapMode = 5
  sketch-geometry (4):
    g0: LineSegment StartX=95.1754 StartY=192.602 StartZ=0 EndX=95.1754 EndY=67 EndZ=0
    g1: LineSegment StartX=95.1754 StartY=67 StartZ=0 EndX=114.794 EndY=67 EndZ=0
    g2: LineSegment StartX=114.794 StartY=67 StartZ=0 EndX=114.794 EndY=192.602 EndZ=0
    g3: LineSegment StartX=114.794 StartY=192.602 StartZ=0 EndX=95.1754 EndY=192.602 EndZ=0
  constraints (9):
    c: Coincident(g0,g1)
    c: Coincident(g1,g2)
    c: Coincident(g2,g3)
    c: Coincident(g3,g0)
    c: Vertical(g0)
    c: Vertical(g2)
    c: Horizontal(g1)
    c: Horizontal(g3)
    c: DistanceY(g0) = 67
FEATURE [Sketcher::SketchObject] Sketch055
  ArcFitTolerance = 1e-06
  AttachmentSupport = -> [XY_Plane029]
  FullyConstrained = false
  MakeInternals = false
  MapMode = 5
  expr: Constraints[10] = <<components>>.m3_hole
  sketch-geometry (8):
    g0: LineSegment StartX=532.782 StartY=-279.207 StartZ=0 EndX=532.782 EndY=-400.207 EndZ=0
    g1: LineSegment StartX=532.782 StartY=-400.207 StartZ=0 EndX=542.782 EndY=-400.207 EndZ=0
    g2: LineSegment StartX=542.782 StartY=-400.207 StartZ=0 EndX=542.782 EndY=-279.207 EndZ=0
    g3: LineSegment StartX=542.782 StartY=-279.207 StartZ=0 EndX=532.782 EndY=-279.207 EndZ=0
    g4: LineSegment [constr] StartX=542.782 StartY=-290.207 StartZ=0 EndX=532.782 EndY=-290.207 EndZ=0
    g5: Circle CenterX=537.782 CenterY=-381.209 CenterZ=0 NormalX=0 NormalY=0 NormalZ=1 AngleXU=0 Radius=1.75
    g6: Circle CenterX=537.782 CenterY=-284.707 CenterZ=0 NormalX=0 NormalY=0 NormalZ=1 AngleXU=0 Radius=1.75
    g7: LineSegment [constr] StartX=537.782 StartY=-284.707 StartZ=0 EndX=537.782 EndY=-381.209 EndZ=0
  constraints (19):
    c: Coincident(g0,g1)
    c: Coincident(g1,g2)
    c: Coincident(g2,g3)
    c: Coincident(g3,g0)
    c: Vertical(g0)
    c: Vertical(g2)
    c: Horizontal(g1)
    c: Horizontal(g3)
    c: Horizontal(g4)
    c: Equal(g5,g6)
    c: Diameter(g6) = 3.5
    c: Coincident(g7,g6)
    c: Coincident(g7,g5)
    c: DistanceX(g4,g4) = 10
    c: Distance(g4,g3) = 11
    c: Symmetric(g4,g4,g7)
    c: DistanceY(g2,g2) = 121
    c: PointOnObject(g4,g2)
    c: PointOnObject(g4,g0)
FEATURE [PartDesign::Pad] Pad026
  Direction = (0,0,1)
  Length = 5
  Length2 = 10
  Profile = -> Sketch055
  ReferenceAxis = -> Sketch055 [N_Axis]
  Refine = true
  Suppressed = false
  Type = 0
FEATURE [Sketcher::SketchObject] Sketch056
  ArcFitTolerance = 1e-06
  AttachmentSupport = -> [YZ_Plane029]
  FullyConstrained = false
  MakeInternals = false
  MapMode = 5
  Placement = pos=(0,0,0) rot=(0.57735,0.57735,0.57735;2.0944rad)
  expr: Constraints[0] = <<choices>>.leg_axle_hole_dia
  expr: Constraints[8] = <<choices>>.leg_axle_hole_dia / 2
  sketch-geometry (5):
    g0: Circle CenterX=-392.256 CenterY=5 CenterZ=0 NormalX=0 NormalY=0 NormalZ=1 AngleXU=0 Radius=2.6
    g1: ArcOfCircle CenterX=-357.458 CenterY=5 CenterZ=0 NormalX=0 NormalY=0 NormalZ=1 AngleXU=0 Radius=2.6 StartAngle=1.5708 EndAngle=4.71239
    g2: ArcOfCircle CenterX=-296.003 CenterY=5 CenterZ=0 NormalX=0 NormalY=0 NormalZ=1 AngleXU=0 Radius=2.6 StartAngle=4.71239 EndAngle=7.85398
    g3: LineSegment StartX=-357.458 StartY=7.6 StartZ=0 EndX=-296.003 EndY=7.6 EndZ=0
    g4: LineSegment StartX=-357.458 StartY=2.4 StartZ=0 EndX=-296.003 EndY=2.4 EndZ=0
  constraints (10):
    c: Diameter(g0) = 5.2
    c: DistanceY(g0) = 5
    c: Tangent(g1,g3) = 1.5708
    c: Tangent(g1,g4) = -1.5708
    c: Tangent(g2,g3) = 1.5708
    c: Tangent(g2,g4) = -1.5708
    c: Equal(g1,g2)
    c: Horizontal(g3)
    c: Radius(g2) = 2.6
    c: DistanceY(g2) = 5
FEATURE [PartDesign::Pocket] Pocket026
  BaseFeature = -> Pad026
  Direction = (-1,0,0)
  Length = 5
  Length2 = 5
  Midplane = true
  Profile = -> Sketch056
  ReferenceAxis = -> Sketch056 [N_Axis]
  Refine = true
  Suppressed = false
  Type = 1
FEATURE [PartDesign::Chamfer] Chamfer002
  Angle = 45
  Base = -> Pocket026 [Edge15,Edge14]
  BaseFeature = -> Pocket026
  ChamferType = 0
  FlipDirection = false
  Refine = true
  Size = 1.75
  Size2 = 1
  SupportTransform = false
  Suppressed = false
  UseAllEdges = false
FEATURE [PartDesign::Body] Body013
  AllowCompound = false
  Group = -> [Sketch055,Pad026,Sketch056,Pocket026,Chamfer002]
  Origin = -> Origin029
  Tip = -> Chamfer002
FEATURE [App::Part] Part013  label="LEG_CLAMP"
  Group = -> [Body013]
  Origin = -> Origin028
FEATURE [Sketcher::SketchObject] Sketch057
  ArcFitTolerance = 1e-06
  AttachmentSupport = -> [XY_Plane031]
  FullyConstrained = false
  MakeInternals = false
  MapMode = 5
  expr: Constraints[10] = <<components>>.frame_h
  expr: Constraints[21] = <<choices>>.mb_front_edge_gap
  expr: Constraints[25] = 10.16 + 22.86
  expr: Constraints[27] = <<components>>.fan_w + <<choices>>.exit_w + <<choices>>.shroud_mb_space
  expr: Constraints[37] = <<components>>.fan_w
  expr: Constraints[38] = <<components>>.fan_h * 4 + 3 * <<choices>>.fan_gap
  expr: Constraints[40] = <<choices>>.exit_w
  expr: Constraints[71] = <<components>>.fan_h + <<choices>>.fan_gap
  expr: Constraints[9] = <<components>>.frame_w
  sketch-geometry (28):
    g0: LineSegment [constr] StartX=0 StartY=0 StartZ=0 EndX=375 EndY=0 EndZ=0
    g1: LineSegment [constr] StartX=375 StartY=0 StartZ=0 EndX=375 EndY=229.5 EndZ=0
    g2: LineSegment [constr] StartX=375 StartY=229.5 StartZ=0 EndX=0 EndY=229.5 EndZ=0
    g3: LineSegment [constr] StartX=0 StartY=229.5 StartZ=0 EndX=0 EndY=0 EndZ=0
    g4: LineSegment [constr] StartX=140 StartY=180 StartZ=0 EndX=140 EndY=10 EndZ=0
    g5: LineSegment [constr] StartX=140 StartY=10 StartZ=0 EndX=310 EndY=10 EndZ=0
    g6: LineSegment [constr] StartX=310 StartY=10 StartZ=0 EndX=310 EndY=180 EndZ=0
    g7: LineSegment [constr] StartX=310 StartY=180 StartZ=0 EndX=140 EndY=180 EndZ=0
    g8: LineSegment [constr] StartX=303.65 StartY=146.98 StartZ=0 EndX=303.65 EndY=10 EndZ=0
    g9: Circle CenterX=303.65 CenterY=146.98 CenterZ=0 NormalX=0 NormalY=0 NormalZ=1 AngleXU=0 Radius=1.75
    g10: LineSegment [constr] StartX=339 StartY=4 StartZ=0 EndX=356 EndY=4 EndZ=0
    g11: LineSegment [constr] StartX=356 StartY=4 StartZ=0 EndX=356 EndY=210 EndZ=0
    g12: LineSegment [constr] StartX=356 StartY=210 StartZ=0 EndX=339 EndY=210 EndZ=0
    g13: LineSegment [constr] StartX=339 StartY=210 StartZ=0 EndX=339 EndY=4 EndZ=0
    g14: LineSegment [constr] StartX=183 StartY=132 StartZ=0 EndX=183 EndY=52 EndZ=0
    g15: LineSegment [constr] StartX=183 StartY=52 StartZ=0 EndX=293 EndY=52 EndZ=0
    g16: LineSegment [constr] StartX=293 StartY=52 StartZ=0 EndX=293 EndY=132 EndZ=0
    g17: LineSegment [constr] StartX=293 StartY=132 StartZ=0 EndX=183 EndY=132 EndZ=0
    g18: LineSegment StartX=273.053 StartY=132 StartZ=0 EndX=286 EndY=132 EndZ=0
    g19: LineSegment StartX=286 StartY=132 StartZ=0 EndX=309.823 EndY=145.872 EndZ=0
    g20: LineSegment StartX=309.823 StartY=145.872 StartZ=0 EndX=339 EndY=158 EndZ=0
    g21: LineSegment StartX=339 StartY=158 StartZ=0 EndX=356 EndY=158 EndZ=0
    g22: LineSegment StartX=356 StartY=158 StartZ=0 EndX=356 EndY=4 EndZ=0
    g23: LineSegment StartX=356 StartY=4 StartZ=0 EndX=339 EndY=4 EndZ=0
    g24: LineSegment StartX=339 StartY=4 StartZ=0 EndX=309.823 EndY=36.5092 EndZ=0
    g25: LineSegment StartX=309.823 StartY=36.5092 StartZ=0 EndX=286 EndY=52 EndZ=0
    g26: LineSegment StartX=286 StartY=52 StartZ=0 EndX=273.053 EndY=52 EndZ=0
    g27: LineSegment StartX=273.053 StartY=52 StartZ=0 EndX=273.053 EndY=132 EndZ=0
  constraints (76):
    c: Coincident(g0,g1)
    c: Coincident(g1,g2)
    c: Coincident(g2,g3)
    c: Coincident(g3,g0)
    c: Horizontal(g0)
    c: Horizontal(g2)
    c: Vertical(g1)
    c: Vertical(g3)
    c: Coincident(g0,g-1)
    c: DistanceX(g2,g2) = 375
    c: DistanceY(g1,g1) = 229.5
    c: Coincident(g4,g5)
    c: Coincident(g5,g6)
    c: Coincident(g6,g7)
    c: Coincident(g7,g4)
    c: Vertical(g4)
    c: Vertical(g6)
    c: Horizontal(g5)
    c: Horizontal(g7)
    c: Distance(g4,g6) = 170
    c: Distance(g5,g7) = 170
    c: DistanceY(g5) = 10
    c: Vertical(g8)
    c: PointOnObject(g8,g5)
    c: Distance(g8,g6) = 6.35
    c: Distance(g8,g7) = 33.02
    c: Diameter(g9) = 3.5
    c: Distance(g5,g1) = 65
    c: Coincident(g9,g8)
    c: Coincident(g10,g11)
    c: Coincident(g11,g12)
    c: Coincident(g12,g13)
    c: Coincident(g13,g10)
    c: Horizontal(g10)
    c: Horizontal(g12)
    c: Vertical(g11)
    c: Vertical(g13)
    c: DistanceX(g12,g12) = 17
    c: DistanceY(g13,g13) = 206
    c: DistanceY(g10) = 4
    c: Distance(g10,g1) = 19
    c: Coincident(g14,g15)
    c: Coincident(g15,g16)
    c: Coincident(g16,g17)
    c: Coincident(g17,g14)
    c: Vertical(g14)
    c: Vertical(g16)
    c: Horizontal(g15)
    c: Horizontal(g17)
    c: Distance(g14,g16) = 110
    c: Distance(g15,g17) = 80
    c: Distance(g15,g6) = 17
    c: Distance(g15,g5) = 42
    c: Horizontal(g18)
    c: Coincident(g18,g19)
    c: Coincident(g19,g20)
    c: PointOnObject(g20,g13)
    c: Coincident(g20,g21)
    c: PointOnObject(g21,g11)
    c: Horizontal(g21)
    c: Coincident(g21,g22)
    c: Coincident(g22,g10)
    c: Coincident(g22,g23)
    c: Coincident(g23,g10)
    c: Coincident(g23,g24)
    c: Coincident(g24,g25)
    c: Coincident(g25,g26)
    c: Horizontal(g26)
    c: Coincident(g26,g27)
    c: Coincident(g27,g18)
    c: Vertical(g27)
    c: Distance(g20,g12) = 52
    c: PointOnObject(g25,g15)
    c: PointOnObject(g18,g17)
    c: Equal(g18,g26)
    c: Distance(g18,g6) = 24
FEATURE [PartDesign::Plane] DatumPlane010
  AttachmentOffset = pos=(0,0,340) rot=(0,0,1;0rad)
  AttachmentSupport = -> [YZ_Plane031]
  Length = 262.721
  MapMode = 5
  Placement = pos=(340,0,0) rot=(0.57735,0.57735,0.57735;2.0944rad)
  ResizeMode = 0
  Width = 109.471
  expr: .AttachmentOffset.Base.z = <<components>>.frame_w - <<choices>>.exit_w - <<components>>.fan_w + 1
FEATURE [PartDesign::Plane] DatumPlane011
  AttachmentOffset = pos=(0,0,313) rot=(0,0,1;0rad)
  AttachmentSupport = -> [YZ_Plane031]
  Length = 262.721
  MapMode = 5
  Placement = pos=(313,0,0) rot=(0.57735,0.57735,0.57735;2.0944rad)
  ResizeMode = 0
  Width = 109.471
  expr: .AttachmentOffset.Base.z = <<components>>.frame_w - <<choices>>.exit_w - <<components>>.fan_w - <<choices>>.shroud_mb_space + 3
FEATURE [PartDesign::Plane] DatumPlane012
  AttachmentOffset = pos=(0,0,286) rot=(0,0,1;0rad)
  AttachmentSupport = -> [YZ_Plane031]
  Length = 262.721
  MapMode = 5
  Placement = pos=(286,0,0) rot=(0.57735,0.57735,0.57735;2.0944rad)
  ResizeMode = 0
  Width = 109.471
  expr: .AttachmentOffset.Base.z = <<components>>.frame_w - <<choices>>.exit_w - <<components>>.fan_w - <<choices>>.shroud_mb_space - 24
FEATURE [PartDesign::Plane] DatumPlane013
  AttachmentOffset = pos=(0,0,276) rot=(0,0,1;0rad)
  AttachmentSupport = -> [YZ_Plane031]
  Length = 262.721
  MapMode = 5
  Placement = pos=(276,0,0) rot=(0.57735,0.57735,0.57735;2.0944rad)
  ResizeMode = 0
  Width = 109.471
  expr: .AttachmentOffset.Base.z = <<components>>.frame_w - <<choices>>.exit_w - <<components>>.fan_w - <<choices>>.shroud_mb_space - 24 - 10
FEATURE [Sketcher::SketchObject] Sketch058
  ArcFitTolerance = 1e-06
  AttachmentSupport = -> [DatumPlane012]
  FullyConstrained = true
  MakeInternals = false
  MapMode = 5
  Placement = pos=(286,0,0) rot=(0.57735,0.57735,0.57735;2.0944rad)
  expr: Constraints[16] = <<choices>>.shroud_wall_thickness
  sketch-geometry (8):
    g0: LineSegment StartX=49 StartY=12 StartZ=0 EndX=49 EndY=45 EndZ=0
    g1: LineSegment StartX=49 StartY=45 StartZ=0 EndX=135 EndY=45 EndZ=0
    g2: LineSegment StartX=135 StartY=45 StartZ=0 EndX=135 EndY=19 EndZ=0
    g3: LineSegment StartX=135 StartY=19 StartZ=0 EndX=132 EndY=19 EndZ=0
    g4: LineSegment StartX=132 StartY=19 StartZ=0 EndX=132 EndY=42 EndZ=0
    g5: LineSegment StartX=132 StartY=42 StartZ=0 EndX=52 EndY=42 EndZ=0
    g6: LineSegment StartX=52 StartY=42 StartZ=0 EndX=52 EndY=12 EndZ=0
    g7: LineSegment StartX=52 StartY=12 StartZ=0 EndX=49 EndY=12 EndZ=0
  constraints (24):
    c: Vertical(g0)
    c: Coincident(g0,g1)
    c: Horizontal(g1)
    c: Coincident(g1,g2)
    c: Vertical(g2)
    c: Coincident(g2,g3)
    c: Horizontal(g3)
    c: Coincident(g3,g4)
    c: Vertical(g4)
    c: Coincident(g4,g5)
    c: Horizontal(g5)
    c: Coincident(g5,g6)
    c: Vertical(g6)
    c: Coincident(g6,g7)
    c: Coincident(g7,g0)
    c: Horizontal(g7)
    c: DistanceX(g3,g3) = 3
    c: Equal(g7,g3)
    c: DistanceY(g5) = 42
    c: DistanceY(g6,g6) = 30
    c: DistanceY(g4,g4) = 23
    c: DistanceX(g5) = 52
    c: DistanceX(g5,g5) = 80
    c: Distance(g5,g1) = 3
FEATURE [Sketcher::SketchObject] Sketch059
  ArcFitTolerance = 1e-06
  AttachmentSupport = -> [DatumPlane012]
  FullyConstrained = true
  MakeInternals = false
  MapMode = 5
  Placement = pos=(286,0,0) rot=(0.57735,0.57735,0.57735;2.0944rad)
  expr: Constraints[16] = <<choices>>.shroud_wall_thickness
  sketch-geometry (8):
    g0: LineSegment StartX=49 StartY=12 StartZ=0 EndX=49 EndY=45 EndZ=0
    g1: LineSegment StartX=49 StartY=45 StartZ=0 EndX=135 EndY=45 EndZ=0
    g2: LineSegment StartX=135 StartY=45 StartZ=0 EndX=135 EndY=19 EndZ=0
    g3: LineSegment StartX=135 StartY=19 StartZ=0 EndX=132 EndY=19 EndZ=0
    g4: LineSegment StartX=132 StartY=19 StartZ=0 EndX=132 EndY=42 EndZ=0
    g5: LineSegment StartX=132 StartY=42 StartZ=0 EndX=52 EndY=42 EndZ=0
    g6: LineSegment StartX=52 StartY=42 StartZ=0 EndX=52 EndY=12 EndZ=0
    g7: LineSegment StartX=52 StartY=12 StartZ=0 EndX=49 EndY=12 EndZ=0
  constraints (24):
    c: Vertical(g0)
    c: Coincident(g0,g1)
    c: Horizontal(g1)
    c: Coincident(g1,g2)
    c: Vertical(g2)
    c: Coincident(g2,g3)
    c: Horizontal(g3)
    c: Coincident(g3,g4)
    c: Vertical(g4)
    c: Coincident(g4,g5)
    c: Horizontal(g5)
    c: Coincident(g5,g6)
    c: Vertical(g6)
    c: Coincident(g6,g7)
    c: Coincident(g7,g0)
    c: Horizontal(g7)
    c: DistanceX(g3,g3) = 3
    c: Equal(g7,g3)
    c: DistanceY(g5) = 42
    c: DistanceY(g6,g6) = 30
    c: DistanceY(g4,g4) = 23
    c: DistanceX(g5) = 52
    c: DistanceX(g5,g5) = 80
    c: Distance(g0,g5) = 3
FEATURE [PartDesign::Pad] Pad027
  Direction = (1,0,0)
  Length = 12
  Length2 = 10
  Placement = pos=(286,0,0) rot=(0.57735,0.57735,0.57735;2.0944rad)
  Profile = -> Sketch058
  ReferenceAxis = -> Sketch058 [N_Axis]
  Refine = true
  Reversed = true
  Suppressed = false
  Type = 0
FEATURE [Sketcher::SketchObject] Sketch060
  ArcFitTolerance = 1e-06
  AttachmentSupport = -> [DatumPlane011]
  FullyConstrained = false
  MakeInternals = false
  MapMode = 5
  Placement = pos=(313,0,0) rot=(0.57735,0.57735,0.57735;2.0944rad)
  expr: Constraints[17] = <<choices>>.shroud_wall_thickness
  expr: Constraints[25] = <<choices>>.exit_height + 3 - <<choices>>.base_under_mb_thickness - 2
  sketch-geometry (9):
    g0: LineSegment StartX=41 StartY=12 StartZ=0 EndX=41 EndY=47 EndZ=0
    g1: LineSegment StartX=41 StartY=47 StartZ=0 EndX=143 EndY=47 EndZ=0
    g2: LineSegment StartX=143 StartY=47 StartZ=0 EndX=143 EndY=19 EndZ=0
    g3: LineSegment StartX=143 StartY=19 StartZ=0 EndX=146 EndY=19 EndZ=0
    g4: LineSegment StartX=146 StartY=19 StartZ=0 EndX=146 EndY=54.75 EndZ=0
    g5: LineSegment StartX=146 StartY=54.75 StartZ=0 EndX=38 EndY=54.75 EndZ=0
    g6: LineSegment StartX=38 StartY=54.75 StartZ=0 EndX=38 EndY=12 EndZ=0
    g7: LineSegment StartX=38 StartY=12 StartZ=0 EndX=41 EndY=12 EndZ=0
    g8: LineSegment [constr] StartX=0 StartY=42 StartZ=0 EndX=33 EndY=42 EndZ=0
  constraints (27):
    c: Vertical(g0)
    c: Coincident(g0,g1)
    c: Horizontal(g1)
    c: Coincident(g1,g2)
    c: Vertical(g2)
    c: Coincident(g2,g3)
    c: Horizontal(g3)
    c: Coincident(g3,g4)
    c: Vertical(g4)
    c: Coincident(g4,g5)
    c: Horizontal(g5)
    c: Coincident(g5,g6)
    c: Vertical(g6)
    c: Coincident(g6,g7)
    c: Coincident(g7,g0)
    c: Horizontal(g7)
    c: Equal(g7,g3)
    c: DistanceX(g3,g3) = 3
    c: PointOnObject(g8,g-2)
    c: Horizontal(g8)
    c: DistanceY(g8) = 42
    c: Distance(g6,g8) = 30
    c: Distance(g2,g8) = 23
    c: DistanceX(g0) = 41
    c: DistanceX(g2) = 143
    c: DistanceY(g5) = 54.75
    c: Distance(g0,g8) = 5
FEATURE [Sketcher::SketchObject] Sketch061
  ArcFitTolerance = 1e-06
  AttachmentSupport = -> [DatumPlane011]
  FullyConstrained = false
  MakeInternals = false
  MapMode = 5
  Placement = pos=(313,0,0) rot=(0.57735,0.57735,0.57735;2.0944rad)
  expr: Constraints[13] = <<choices>>.shroud_wall_thickness
  expr: Constraints[19] = <<choices>>.exit_height + 3 - <<choices>>.base_under_mb_thickness - 2
  sketch-geometry (20):
    g0: LineSegment StartX=41 StartY=0 StartZ=0 EndX=41 EndY=45.7422 EndZ=0
    g1: LineSegment StartX=42.2578 StartY=47 StartZ=0 EndX=141.742 EndY=47 EndZ=0
    g2: LineSegment [constr] StartX=143 StartY=45.7422 StartZ=0 EndX=143 EndY=0 EndZ=0
    g3: LineSegment [constr] StartX=143 StartY=0 StartZ=0 EndX=146 EndY=0 EndZ=0
    g4: LineSegment [constr] StartX=146 StartY=0 StartZ=0 EndX=146 EndY=53.4922 EndZ=0
    g5: LineSegment StartX=144.742 StartY=54.75 StartZ=0 EndX=39.2578 EndY=54.75 EndZ=0
    g6: LineSegment StartX=38 StartY=53.4922 StartZ=0 EndX=38 EndY=0 EndZ=0
    g7: LineSegment StartX=38 StartY=0 StartZ=0 EndX=41 EndY=0 EndZ=0
    g8: LineSegment [constr] StartX=0 StartY=42 StartZ=0 EndX=33 EndY=42 EndZ=0
    g9: ArcOfCircle CenterX=39.2578 CenterY=53.4922 CenterZ=0 NormalX=0 NormalY=0 NormalZ=1 AngleXU=0 Radius=1.25784 StartAngle=1.5708 EndAngle=3.14159
    g10: GeomPoint [constr] X=38 Y=54.75 Z=0
    g11: ArcOfCircle [constr] CenterX=144.742 CenterY=53.4922 CenterZ=0 NormalX=0 NormalY=0 NormalZ=1 AngleXU=0 Radius=1.25784 StartAngle=-9e-16 EndAngle=1.5708
    g12: GeomPoint [constr] X=146 Y=54.75 Z=0
    g13: ArcOfCircle [constr] CenterX=141.742 CenterY=45.7422 CenterZ=0 NormalX=0 NormalY=0 NormalZ=1 AngleXU=0 Radius=1.25784 StartAngle=-1.8e-15 EndAngle=1.5708
    g14: GeomPoint [constr] X=143 Y=47 Z=0
    g15: ArcOfCircle CenterX=42.2578 CenterY=45.7422 CenterZ=0 NormalX=0 NormalY=0 NormalZ=1 AngleXU=0 Radius=1.25784 StartAngle=1.5708 EndAngle=3.14159
    g16: GeomPoint [constr] X=41 Y=47 Z=0
    g17: LineSegment StartX=141.742 StartY=47 StartZ=0 EndX=154.715 EndY=47 EndZ=0
    g18: LineSegment StartX=154.715 StartY=47 StartZ=0 EndX=154.715 EndY=54.75 EndZ=0
    g19: LineSegment StartX=154.715 StartY=54.75 StartZ=0 EndX=144.742 EndY=54.75 EndZ=0
  constraints (49):
    c: Vertical(g0)
    c: Horizontal(g1)
    c: Vertical(g2)
    c: Coincident(g2,g3)
    c: Horizontal(g3)
    c: Coincident(g3,g4)
    c: Vertical(g4)
    c: Horizontal(g5)
    c: Vertical(g6)
    c: Coincident(g6,g7)
    c: Coincident(g7,g0)
    c: Horizontal(g7)
    c: Equal(g7,g3)
    c: DistanceX(g3,g3) = 3
    c: PointOnObject(g8,g-2)
    c: Horizontal(g8)
    c: DistanceY(g8) = 42
    c: DistanceX(g0) = 41
    c: DistanceX(g2) = 143
    c: DistanceY(g10) = 54.75
    c: PointOnObject(g3,g-1)
    c: PointOnObject(g0,g-1)
    c: PointOnObject(g10,g5)
    c: PointOnObject(g10,g6)
    c: Tangent(g5,g9) = -1.5708
    c: Tangent(g6,g9) = -1.5708
    c: PointOnObject(g12,g4)
    c: PointOnObject(g12,g5)
    c: Tangent(g4,g11) = -1.5708
    c: Tangent(g5,g11) = -1.5708
    c: PointOnObject(g14,g1)
    c: PointOnObject(g14,g2)
    c: Tangent(g1,g13) = 1.5708
    c: Tangent(g2,g13) = 1.5708
    c: PointOnObject(g16,g0)
    c: PointOnObject(g16,g1)
    c: Tangent(g0,g15) = 1.5708
    c: Tangent(g1,g15) = 1.5708
    c: Equal(g15,g9)
    c: Equal(g9,g11)
    c: Equal(g11,g13)
    c: Distance(g1,g8) = 5
    c: Coincident(g1,g17)
    c: Horizontal(g17)
    c: Coincident(g17,g18)
    c: Vertical(g18)
    c: Coincident(g18,g19)
    c: Coincident(g19,g5)
    c: Horizontal(g19)
FEATURE [PartDesign::AdditiveLoft] AdditiveLoft001
  BaseFeature = -> Pad027
  Closed = false
  Placement = pos=(286,0,0) rot=(0.57735,0.57735,0.57735;2.0944rad)
  Profile = -> Sketch060
  Refine = true
  Ruled = false
  Sections = -> [Sketch059]
  Suppressed = false
FEATURE [Sketcher::SketchObject] Sketch062
  ArcFitTolerance = 1e-06
  AttachmentSupport = -> [DatumPlane010]
  FullyConstrained = true
  MakeInternals = false
  MapMode = 5
  Placement = pos=(340,0,0) rot=(0.57735,0.57735,0.57735;2.0944rad)
  expr: Constraints[14] = <<choices>>.exit_height + 3 - <<choices>>.base_under_mb_thickness
  expr: Constraints[17] = <<components>>.fan_h + 4
  sketch-geometry (19):
    g0: LineSegment StartX=3.2 StartY=0 StartZ=0 EndX=3.2 EndY=33.75 EndZ=0
    g1: LineSegment StartX=26.2 StartY=56.75 StartZ=0 EndX=187 EndY=56.75 EndZ=0
    g2: LineSegment [constr] StartX=210 StartY=33.75 StartZ=0 EndX=210 EndY=0 EndZ=0
    g3: LineSegment [constr] StartX=210 StartY=0 StartZ=0 EndX=208 EndY=0 EndZ=0
    g4: LineSegment [constr] StartX=208 StartY=0 StartZ=0 EndX=208 EndY=29 EndZ=0
    g5: LineSegment StartX=183 StartY=54 StartZ=0 EndX=30 EndY=54 EndZ=0
    g6: LineSegment StartX=5 StartY=29 StartZ=0 EndX=5 EndY=0 EndZ=0
    g7: LineSegment StartX=5 StartY=0 StartZ=0 EndX=3.2 EndY=0 EndZ=0
    g8: ArcOfCircle CenterX=30 CenterY=29 CenterZ=0 NormalX=0 NormalY=0 NormalZ=1 AngleXU=0 Radius=25 StartAngle=1.5708 EndAngle=3.14159
    g9: GeomPoint [constr] X=5 Y=54 Z=0
    g10: ArcOfCircle [constr] CenterX=183 CenterY=29 CenterZ=0 NormalX=0 NormalY=0 NormalZ=1 AngleXU=0 Radius=25 StartAngle=0 EndAngle=1.5708
    g11: GeomPoint [constr] X=208 Y=54 Z=0
    g12: ArcOfCircle CenterX=26.2 CenterY=33.75 CenterZ=0 NormalX=0 NormalY=0 NormalZ=1 AngleXU=0 Radius=23 StartAngle=1.5708 EndAngle=3.14159
    g13: GeomPoint [constr] X=3.2 Y=56.75 Z=0
    g14: ArcOfCircle [constr] CenterX=187 CenterY=33.75 CenterZ=0 NormalX=0 NormalY=0 NormalZ=1 AngleXU=0 Radius=23 StartAngle=0 EndAngle=1.5708
    g15: GeomPoint [constr] X=210 Y=56.75 Z=0
    g16: LineSegment StartX=183 StartY=54 StartZ=0 EndX=210 EndY=54 EndZ=0
    g17: LineSegment StartX=210 StartY=54 StartZ=0 EndX=210 EndY=56.75 EndZ=0
    g18: LineSegment StartX=210 StartY=56.75 StartZ=0 EndX=187 EndY=56.75 EndZ=0
  constraints (48):
    c: PointOnObject(g0,g-1)
    c: Vertical(g0)
    c: Horizontal(g1)
    c: PointOnObject(g2,g-1)
    c: Vertical(g2)
    c: Coincident(g2,g3)
    c: PointOnObject(g3,g-1)
    c: Coincident(g3,g4)
    c: Vertical(g4)
    c: Horizontal(g5)
    c: PointOnObject(g6,g-1)
    c: Vertical(g6)
    c: Coincident(g6,g7)
    c: Coincident(g7,g0)
    c: DistanceY(g13) = 56.75
    c: DistanceX(g0) = 3.2
    c: DistanceX(g6) = 5
    c: DistanceY(g9) = 54
    c: DistanceX(g3) = 208
    c: PointOnObject(g9,g5)
    c: PointOnObject(g9,g6)
    c: Tangent(g5,g8) = -1.5708
    c: Tangent(g6,g8) = -1.5708
    c: DistanceX(g3,g3) = 2
    c: PointOnObject(g11,g4)
    c: PointOnObject(g11,g5)
    c: Tangent(g4,g10) = -1.5708
    c: Tangent(g5,g10) = -1.5708
    c: Equal(g8,g10)
    c: PointOnObject(g13,g0)
    c: PointOnObject(g13,g1)
    c: Tangent(g0,g12) = 1.5708
    c: Tangent(g1,g12) = 1.5708
    c: PointOnObject(g15,g1)
    c: PointOnObject(g15,g2)
    c: Tangent(g1,g14) = 1.5708
    c: Tangent(g2,g14) = 1.5708
    c: Equal(g14,g12)
    c: Radius(g12) = 23
    c: Radius(g8) = 25
    c: Coincident(g5,g16)
    c: Horizontal(g16)
    c: Coincident(g16,g17)
    c: Vertical(g17)
    c: Coincident(g17,g18)
    c: Coincident(g18,g1)
    c: Horizontal(g18)
    c: PointOnObject(g16,g2)
FEATURE [PartDesign::AdditiveLoft] AdditiveLoft002
  BaseFeature = -> AdditiveLoft001
  Closed = false
  Placement = pos=(286,0,0) rot=(0.57735,0.57735,0.57735;2.0944rad)
  Profile = -> Sketch062
  Refine = true
  Ruled = false
  Sections = -> [Sketch061]
  Suppressed = false
FEATURE [PartDesign::Plane] DatumPlane014
  AttachmentOffset = pos=(0,0,8) rot=(0,0,1;0rad)
  AttachmentSupport = -> [XY_Plane031]
  Length = 424.115
  MapMode = 5
  Placement = pos=(0,0,8) rot=(0,0,1;0rad)
  ResizeMode = 0
  Width = 293.615
FEATURE [Sketcher::SketchObject] Sketch063
  ArcFitTolerance = 1e-06
  AttachmentSupport = -> [DatumPlane014]
  FullyConstrained = false
  MakeInternals = false
  MapMode = 5
  Placement = pos=(0,0,8) rot=(0,0,1;0rad)
  expr: Constraints[0] = <<components>>.m3_hole
  expr: Constraints[6] = 2 + <<components>>.m3_hole / 2
  sketch-geometry (5):
    g0: Circle CenterX=303.65 CenterY=146.98 CenterZ=0 NormalX=0 NormalY=0 NormalZ=1 AngleXU=0 Radius=1.75
    g1: ArcOfCircle CenterX=303.65 CenterY=146.98 CenterZ=0 NormalX=0 NormalY=0 NormalZ=1 AngleXU=0 Radius=3.75 StartAngle=1.38735 EndAngle=4.15092
    g2: LineSegment StartX=304.334 StartY=150.667 StartZ=0 EndX=319.712 EndY=147.814 EndZ=0
    g3: LineSegment StartX=301.653 StartY=143.806 StartZ=0 EndX=305.391 EndY=141.455 EndZ=0
    g4: LineSegment StartX=305.391 StartY=141.455 StartZ=0 EndX=319.712 EndY=147.814 EndZ=0
  constraints (9):
    c: Diameter(g0) = 3.5
    c: DistanceX(g0) = 303.65
    c: DistanceY(g0) = 146.98
    c: Tangent(g1,g2) = 1.5708
    c: Tangent(g1,g3) = -1.5708
    c: Coincident(g1,g0)
    c: Radius(g1) = 3.75
    c: Coincident(g4,g2)
    c: Coincident(g3,g4)
FEATURE [App::Link] MOTHERBOARD  label="MOTHERBOARD001"
  LinkPlacement = pos=(513.746,-370.323,122.905) rot=(0.075569,0.096295,0.99248;0.012724rad)
  LinkedObject = -> Part002
  Placement = pos=(513.746,-370.323,122.905) rot=(0.075569,0.096295,0.99248;0.012724rad)
FEATURE [App::FeaturePython] Joint004  label="Fixed001"  # Assembly joint (typed FeaturePython)
  Activated = true
  AngleMax = 0
  AngleMin = 0
  Detach1 = false
  Detach2 = false
  Distance = 0
  Distance2 = 0
  EnableAngleMax = false
  EnableAngleMin = false
  EnableLengthMax = false
  EnableLengthMin = false
  JointType = 0 (Fixed)
  LengthMax = 0
  LengthMin = 0
  Placement1 = pos=(6.35,4.8997,0) rot=(0,0,1;0rad)
  Placement2 = pos=(146.35,14.8997,7.25) rot=(0,0,1;0rad)
  Reference1 = -> Assembly [MOTHERBOARD.Body002.Edge16,MOTHERBOARD.Body002.Edge16]
  Reference2 = -> Assembly [BASE.Body006.Edge1130,BASE.Body006.Edge1130]
FEATURE [PartDesign::Pad] Pad029
  BaseFeature = -> Pad022
  Direction = (0,0,1)
  Length = 5
  Length2 = 10
  Profile = -> Sketch010
  ReferenceAxis = -> Sketch010 [N_Axis]
  Refine = true
  Reversed = true
  Suppressed = false
  Type = 0
FEATURE [PartDesign::Body] Body002
  AllowCompound = false
  Group = -> [Sketch004,Pad004,Sketch010,Pad007,Sketch042,Pad022,Pad029]
  Origin = -> Origin005
  Placement = pos=(59,-86,-131) rot=(0,0,1;0rad)
  Tip = -> Pad029
FEATURE [App::Part] Part002  label="MOTHERBOARD"
  Group = -> [Body002]
  Origin = -> Origin004
FEATURE [Sketcher::SketchObject] Sketch064
  ArcFitTolerance = 1e-06
  AttachmentSupport = -> [YZ_Plane018]
  FullyConstrained = true
  MakeInternals = false
  MapMode = 5
  Placement = pos=(0,0,0) rot=(0.57735,0.57735,0.57735;2.0944rad)
  expr: Constraints[24] = <<choices>>.leg_bracket_axis_dist
  expr: Constraints[6] = <<choices>>.leg_bracket_length
  sketch-geometry (11):
    g0: LineSegment StartX=42.5 StartY=5.3 StartZ=0 EndX=95 EndY=5.3 EndZ=0
    g1: LineSegment StartX=42.5 StartY=-5.3 StartZ=0 EndX=95 EndY=-5.3 EndZ=0
    g2: ArcOfCircle [constr] CenterX=95 CenterY=-1e-15 CenterZ=0 NormalX=0 NormalY=0 NormalZ=1 AngleXU=0 Radius=5.3 StartAngle=4.71239 EndAngle=6.28318
    g3: ArcOfCircle CenterX=95 CenterY=-1e-15 CenterZ=0 NormalX=0 NormalY=0 NormalZ=1 AngleXU=0 Radius=5.3 StartAngle=6.28318 EndAngle=7.85398
    g4: LineSegment StartX=100.3 StartY=-2.87042e-05 StartZ=0 EndX=100.3 EndY=-5.3 EndZ=0
    g5: LineSegment StartX=100.3 StartY=-5.3 StartZ=0 EndX=95 EndY=-5.3 EndZ=0
    g6: ArcOfCircle CenterX=42.5 CenterY=0 CenterZ=0 NormalX=0 NormalY=0 NormalZ=1 AngleXU=0 Radius=5.3 StartAngle=1.5708 EndAngle=3.14159
    g7: ArcOfCircle [constr] CenterX=42.5 CenterY=0 CenterZ=0 NormalX=0 NormalY=0 NormalZ=1 AngleXU=0 Radius=5.3 StartAngle=3.14159 EndAngle=4.71239
    g8: LineSegment StartX=42.5 StartY=-5.3 StartZ=0 EndX=37.2 EndY=-5.3 EndZ=0
    g9: LineSegment StartX=37.2 StartY=-5.3 StartZ=0 EndX=37.2 EndY=9e-16 EndZ=0
    g10: Circle CenterX=42.5 CenterY=0 CenterZ=0 NormalX=0 NormalY=0 NormalZ=1 AngleXU=0 Radius=2.5
  constraints (27):
    c: Tangent(g6,g0) = 1.5708
    c: Tangent(g7,g1) = -1.5708
    c: Tangent(g3,g0) = 1.5708
    c: Tangent(g2,g1) = -1.5708
    c: Horizontal(g1)
    c: PointOnObject(g6,g-1)
    c: DistanceX(g0,g0) = 52.5
    c: Coincident(g2,g3)
    c: Coincident(g2,g3)
    c: Coincident(g2,g4)
    c: Coincident(g4,g5)
    c: Coincident(g5,g1)
    c: Horizontal(g5)
    c: Vertical(g4)
    c: Tangent(g4,g3)
    c: Coincident(g6,g7)
    c: Coincident(g6,g7)
    c: Radius(g6) = 5.3
    c: Equal(g6,g2)
    c: Coincident(g1,g8)
    c: Horizontal(g8)
    c: Coincident(g8,g9)
    c: Vertical(g9)
    c: Tangent(g9,g6) = 1.5708
    c: DistanceX(g6) = 42.5
    c: Coincident(g10,g6)
    c: Diameter(g10) = 5
FEATURE [PartDesign::Pocket] Pocket027
  BaseFeature = -> Pad015
  Direction = (-1,0,0)
  Length = 5
  Length2 = 5
  Placement = pos=(0,0,0) rot=(1,1,1;2.0944rad)
  Profile = -> Sketch064
  ReferenceAxis = -> Sketch064 [N_Axis]
  Refine = true
  Reversed = true
  Suppressed = false
  Type = 0
FEATURE [Sketcher::SketchObject] Sketch065
  ArcFitTolerance = 1e-06
  AttachmentSupport = -> [YZ_Plane020]
  FullyConstrained = true
  MakeInternals = false
  MapMode = 5
  Placement = pos=(0,0,0) rot=(0.57735,0.57735,0.57735;2.0944rad)
  expr: Constraints[6] = <<choices>>.leg_bracket_axis_dist
  expr: Constraints[7] = <<choices>>.leg_bracket_length
  sketch-geometry (11):
    g0: LineSegment StartX=42.5 StartY=5.3 StartZ=0 EndX=95 EndY=5.3 EndZ=0
    g1: LineSegment StartX=42.5 StartY=-5.3 StartZ=0 EndX=95 EndY=-5.3 EndZ=0
    g2: ArcOfCircle CenterX=42.5 CenterY=0 CenterZ=0 NormalX=0 NormalY=0 NormalZ=1 AngleXU=0 Radius=5.3 StartAngle=1.5708 EndAngle=3.14159
    g3: ArcOfCircle [constr] CenterX=42.5 CenterY=0 CenterZ=0 NormalX=0 NormalY=0 NormalZ=1 AngleXU=0 Radius=5.3 StartAngle=3.14159 EndAngle=4.71239
    g4: ArcOfCircle [constr] CenterX=95 CenterY=4.6e-15 CenterZ=0 NormalX=0 NormalY=0 NormalZ=1 AngleXU=0 Radius=5.3 StartAngle=4.71239 EndAngle=6.28318
    g5: ArcOfCircle CenterX=95 CenterY=4.6e-15 CenterZ=0 NormalX=0 NormalY=0 NormalZ=1 AngleXU=0 Radius=5.3 StartAngle=6.28318 EndAngle=7.85398
    g6: LineSegment StartX=37.2 StartY=6e-16 StartZ=0 EndX=37.2 EndY=-5.3 EndZ=0
    g7: LineSegment StartX=37.2 StartY=-5.3 StartZ=0 EndX=42.5 EndY=-5.3 EndZ=0
    g8: LineSegment StartX=100.3 StartY=-2.31368e-05 StartZ=0 EndX=100.3 EndY=-5.3 EndZ=0
    g9: LineSegment StartX=100.3 StartY=-5.3 StartZ=0 EndX=95 EndY=-5.3 EndZ=0
    g10: Circle CenterX=42.5 CenterY=0 CenterZ=0 NormalX=0 NormalY=0 NormalZ=1 AngleXU=0 Radius=2.5
  constraints (27):
    c: Tangent(g2,g0) = 1.5708
    c: Tangent(g3,g1) = -1.5708
    c: Tangent(g5,g0) = 1.5708
    c: Tangent(g4,g1) = -1.5708
    c: Horizontal(g1)
    c: PointOnObject(g2,g-1)
    c: DistanceX(g2) = 42.5
    c: DistanceX(g1,g1) = 52.5
    c: Coincident(g2,g3)
    c: Coincident(g2,g3)
    c: Coincident(g4,g5)
    c: Coincident(g4,g5)
    c: Radius(g4) = 5.3
    c: Equal(g2,g4)
    c: Tangent(g2,g6) = -1.5708
    c: Coincident(g6,g7)
    c: Coincident(g7,g1)
    c: Horizontal(g7)
    c: Vertical(g6)
    c: Coincident(g4,g8)
    c: Coincident(g8,g9)
    c: Coincident(g9,g1)
    c: Horizontal(g9)
    c: Vertical(g8)
    c: Tangent(g8,g5)
    c: Coincident(g10,g2)
    c: Diameter(g10) = 5
FEATURE [PartDesign::Pad] Pad030
  Direction = (1,0,0)
  Length = 10
  Length2 = 10
  Placement = pos=(0,0,0) rot=(1,1,1;2.0944rad)
  Profile = -> Sketch031 [Edge1,Edge4,Edge2,Edge5,Edge3,Edge7]
  ReferenceAxis = -> Sketch031 [N_Axis]
  Refine = true
  Reversed = true
  Suppressed = false
  Type = 0
  expr: Length = <<choices>>.leg_width
FEATURE [PartDesign::Pocket] Pocket029
  BaseFeature = -> Pad030
  Direction = (-1,0,0)
  Length = 5
  Length2 = 5
  Placement = pos=(0,0,0) rot=(1,1,1;2.0944rad)
  Profile = -> Sketch065
  ReferenceAxis = -> Sketch065 [N_Axis]
  Refine = true
  Suppressed = false
  Type = 0
FEATURE [App::Link] PSU  label="PSU001"
  LinkPlacement = pos=(438.654,-454.164,4.66713) rot=(0.075569,0.096295,0.99248;0.012724rad)
  LinkedObject = -> Part
  Placement = pos=(438.654,-454.164,4.66713) rot=(0.075569,0.096295,0.99248;0.012724rad)
FEATURE [App::Link] GPU  label="GPU001"
  LinkPlacement = pos=(509.664,-440.688,9.46321) rot=(0,0,1;0rad)
  LinkedObject = -> Part004
  Placement = pos=(509.664,-440.688,9.46321) rot=(0,0,1;0rad)
FEATURE [App::FeaturePython] Joint  label="Fixed"  # Assembly joint (typed FeaturePython)
  Activated = true
  AngleMax = 0
  AngleMin = 0
  Detach1 = false
  Detach2 = false
  Distance = 0
  Distance2 = 0
  EnableAngleMax = false
  EnableAngleMin = false
  EnableLengthMax = false
  EnableLengthMin = false
  JointType = 0 (Fixed)
  LengthMax = 0
  LengthMin = 0
  Placement1 = pos=(44.15,13,0) rot=(0,0,1;0rad)
  Placement2 = pos=(49.15,26,20) rot=(1,0,0;3.14159rad)
  Reference1 = -> Assembly [PSU.Body.Edge15,PSU.Body.Edge15]
  Reference2 = -> Assembly [BASE.Body006.Edge1143,BASE.Body006.Edge1143]
FEATURE [PartDesign::Chamfer] Chamfer
  Angle = 45
  Base = -> Pocket029 [Edge24]
  BaseFeature = -> Pocket029
  ChamferType = 0
  FlipDirection = false
  Placement = pos=(0,0,0) rot=(1,1,1;2.0944rad)
  Refine = true
  Size = 1.75
  Size2 = 1
  SupportTransform = false
  Suppressed = false
  UseAllEdges = false
FEATURE [PartDesign::Chamfer] Chamfer003
  Angle = 45
  Base = -> Pad017 [Edge17]
  BaseFeature = -> Pad017
  ChamferType = 0
  FlipDirection = false
  Placement = pos=(0,0,0) rot=(1,1,1;2.0944rad)
  Refine = true
  Size = 1.75
  Size2 = 1
  SupportTransform = false
  Suppressed = false
  UseAllEdges = false
FEATURE [PartDesign::Body] Body010
  AllowCompound = false
  Group = -> [Sketch032,Pad017,Chamfer003]
  Origin = -> Origin022
  Tip = -> Chamfer003
FEATURE [App::Part] Part010  label="LEG_BRACKET"
  Group = -> [Body010]
  Origin = -> Origin021
FEATURE [Sketcher::SketchObject] Sketch066
  ArcFitTolerance = 1e-06
  AttachmentSupport = -> [YZ_Plane033]
  FullyConstrained = true
  MakeInternals = false
  MapMode = 5
  Placement = pos=(0,0,0) rot=(0.57735,0.57735,0.57735;2.0944rad)
  expr: Constraints[11] = <<components>>.m3_threadhole
  expr: Constraints[8] = <<choices>>.leg_bracket_length
  sketch-geometry (6):
    g0: ArcOfCircle CenterX=0 CenterY=0 CenterZ=0 NormalX=0 NormalY=0 NormalZ=1 AngleXU=0 Radius=5 StartAngle=1.5708 EndAngle=4.71239
    g1: ArcOfCircle CenterX=52.5 CenterY=1e-16 CenterZ=0 NormalX=0 NormalY=0 NormalZ=1 AngleXU=0 Radius=5 StartAngle=4.71239 EndAngle=7.85398
    g2: LineSegment StartX=-8e-16 StartY=5 StartZ=0 EndX=52.5 EndY=5 EndZ=0
    g3: LineSegment StartX=-9e-16 StartY=-5 StartZ=0 EndX=52.5 EndY=-5 EndZ=0
    g4: Circle CenterX=0 CenterY=0 CenterZ=0 NormalX=0 NormalY=0 NormalZ=1 AngleXU=0 Radius=1.25
    g5: Circle CenterX=52.5 CenterY=1e-16 CenterZ=0 NormalX=0 NormalY=0 NormalZ=1 AngleXU=0 Radius=2.65
  constraints (13):
    c: Tangent(g0,g2) = 1.5708
    c: Tangent(g0,g3) = -1.5708
    c: Tangent(g1,g2) = 1.5708
    c: Tangent(g1,g3) = -1.5708
    c: Equal(g0,g1)
    c: Horizontal(g3)
    c: Coincident(g0,g-1)
    c: Radius(g1) = 5
    c: DistanceX(g1) = 52.5
    c: Coincident(g4,g0)
    c: Coincident(g5,g1)
    c: Diameter(g4) = 2.5
    c: Diameter(g5) = 5.3
FEATURE [PartDesign::Pad] Pad031
  Direction = (1,0,0)
  Length = 4.8
  Length2 = 10
  Placement = pos=(0,0,0) rot=(1,1,1;2.0944rad)
  Profile = -> Sketch066
  ReferenceAxis = -> Sketch066 [N_Axis]
  Refine = true
  Suppressed = false
  Type = 0
FEATURE [PartDesign::Body] Body015
  AllowCompound = false
  Group = -> [Sketch066,Pad031]
  Origin = -> Origin033
  Tip = -> Pad031
FEATURE [App::Part] Part015  label="LEG_BRACKET_B"
  Group = -> [Body015]
  Origin = -> Origin032
FEATURE [Sketcher::SketchObject] Sketch067
  ArcFitTolerance = 1e-06
  AttachmentSupport = -> [XY_Plane013]
  FullyConstrained = true
  MakeInternals = false
  MapMode = 5
  sketch-geometry (28):
    g0: LineSegment [constr] StartX=15.85 StartY=26 StartZ=0 EndX=49.15 EndY=26 EndZ=0
    g1: LineSegment [constr] StartX=49.15 StartY=26 StartZ=0 EndX=49.15 EndY=170 EndZ=0
    g2: LineSegment [constr] StartX=49.15 StartY=170 StartZ=0 EndX=15.85 EndY=170 EndZ=0
    g3: LineSegment [constr] StartX=15.85 StartY=170 StartZ=0 EndX=15.85 EndY=26 EndZ=0
    g4: LineSegment StartX=19.1 StartY=173.25 StartZ=0 EndX=19.1 EndY=166.75 EndZ=0
    g5: LineSegment StartX=19.1 StartY=166.75 StartZ=0 EndX=12.6 EndY=166.75 EndZ=0
    g6: LineSegment StartX=12.6 StartY=166.75 StartZ=0 EndX=12.6 EndY=173.25 EndZ=0
    g7: LineSegment StartX=12.6 StartY=173.25 StartZ=0 EndX=19.1 EndY=173.25 EndZ=0
    g8: GeomPoint [constr] X=15.85 Y=170 Z=0
    g9: LineSegment StartX=45.9 StartY=173.25 StartZ=0 EndX=45.9 EndY=166.75 EndZ=0
    g10: LineSegment StartX=45.9 StartY=166.75 StartZ=0 EndX=52.4 EndY=166.75 EndZ=0
    g11: LineSegment StartX=52.4 StartY=166.75 StartZ=0 EndX=52.4 EndY=173.25 EndZ=0
    g12: LineSegment StartX=52.4 StartY=173.25 StartZ=0 EndX=45.9 EndY=173.25 EndZ=0
    g13: GeomPoint [constr] X=49.15 Y=170 Z=0
    g14: LineSegment StartX=45.9 StartY=22.75 StartZ=0 EndX=52.4 EndY=22.75 EndZ=0
    g15: LineSegment StartX=52.4 StartY=22.75 StartZ=0 EndX=52.4 EndY=29.25 EndZ=0
    g16: LineSegment StartX=52.4 StartY=29.25 StartZ=0 EndX=45.9 EndY=29.25 EndZ=0
    g17: LineSegment StartX=45.9 StartY=29.25 StartZ=0 EndX=45.9 EndY=22.75 EndZ=0
    g18: GeomPoint [constr] X=49.15 Y=26 Z=0
    g19: LineSegment StartX=19.1 StartY=22.75 StartZ=0 EndX=12.6 EndY=22.75 EndZ=0
    g20: LineSegment StartX=12.6 StartY=22.75 StartZ=0 EndX=12.6 EndY=29.25 EndZ=0
    g21: LineSegment StartX=12.6 StartY=29.25 StartZ=0 EndX=19.1 EndY=29.25 EndZ=0
    g22: LineSegment StartX=19.1 StartY=29.25 StartZ=0 EndX=19.1 EndY=22.75 EndZ=0
    g23: GeomPoint [constr] X=15.85 Y=26 Z=0
    g24: LineSegment StartX=0 StartY=5 StartZ=0 EndX=9 EndY=5 EndZ=0
    g25: LineSegment StartX=9 StartY=5 StartZ=0 EndX=9 EndY=11 EndZ=0
    g26: LineSegment StartX=9 StartY=11 StartZ=0 EndX=0 EndY=11 EndZ=0
    g27: LineSegment StartX=0 StartY=11 StartZ=0 EndX=0 EndY=5 EndZ=0
  constraints (72):
    c: Coincident(g0,g1)
    c: Coincident(g1,g2)
    c: Coincident(g2,g3)
    c: Coincident(g3,g0)
    c: Horizontal(g0)
    c: Horizontal(g2)
    c: Vertical(g1)
    c: Vertical(g3)
    c: Coincident(g4,g5)
    c: Coincident(g5,g6)
    c: Coincident(g6,g7)
    c: Coincident(g7,g4)
    c: Vertical(g4)
    c: Vertical(g6)
    c: Horizontal(g5)
    c: Horizontal(g7)
    c: Symmetric(g6,g4,g8)
    c: Coincident(g8,g2)
    c: Coincident(g9,g10)
    c: Coincident(g10,g11)
    c: Coincident(g11,g12)
    c: Coincident(g12,g9)
    c: Vertical(g9)
    c: Vertical(g11)
    c: Horizontal(g10)
    c: Horizontal(g12)
    c: Symmetric(g11,g9,g13)
    c: Coincident(g13,g1)
    c: Coincident(g14,g15)
    c: Coincident(g15,g16)
    c: Coincident(g16,g17)
    c: Coincident(g17,g14)
    c: Horizontal(g14)
    c: Horizontal(g16)
    c: Vertical(g15)
    c: Vertical(g17)
    c: Symmetric(g16,g14,g18)
    c: Coincident(g18,g0)
    c: Coincident(g19,g20)
    c: Coincident(g20,g21)
    c: Coincident(g21,g22)
    c: Coincident(g22,g19)
    c: Horizontal(g19)
    c: Horizontal(g21)
    c: Vertical(g20)
    c: Vertical(g22)
    c: Symmetric(g21,g19,g23)
    c: Coincident(g23,g0)
    c: Equal(g21,g5)
    c: Equal(g5,g6)
    c: Equal(g6,g10)
    c: Equal(g10,g22)
    c: Equal(g22,g17)
    c: Equal(g17,g16)
    c: Equal(g16,g11)
    c: DistanceX(g12,g12) = 6.5
    c: DistanceY(g3,g3) = 144
    c: DistanceX(g0,g0) = 33.3
    c: DistanceY(g0) = 26
    c: DistanceX(g0) = 15.85
    c: Coincident(g24,g25)
    c: Coincident(g25,g26)
    c: Coincident(g26,g27)
    c: Coincident(g27,g24)
    c: Horizontal(g24)
    c: Horizontal(g26)
    c: Vertical(g25)
    c: Vertical(g27)
    c: Distance(g25,g27) = 9
    c: Distance(g24,g26) = 6
    c: PointOnObject(g24,g-2)
    c: DistanceY(g24) = 5
FEATURE [PartDesign::Plane] DatumPlane015
  AttachmentOffset = pos=(0,0,20) rot=(0,0,1;0rad)
  AttachmentSupport = -> [XY_Plane035]
  Length = 120.269
  MapMode = 5
  Placement = pos=(0,0,20) rot=(0,0,1;0rad)
  ResizeMode = 0
  Width = 284.769
  expr: .AttachmentOffset.Base.z = <<choices>>.base_max_thickness
FEATURE [Sketcher::SketchObject] Sketch068
  ArcFitTolerance = 1e-06
  AttachmentSupport = -> [DatumPlane015]
  FullyConstrained = false
  MakeInternals = false
  MapMode = 5
  Placement = pos=(0,0,20) rot=(0,0,1;0rad)
  expr: Constraints[22] = <<choices>>.corner
  expr: Constraints[23] = <<components>>.m3_hole
  expr: Constraints[24] = <<choices>>.screwhole_edge_margin
  expr: Constraints[26] = <<choices>>.screwhole_edge_margin
  expr: Constraints[7] = <<components>>.frame_h
  sketch-geometry (31):
    g0: LineSegment StartX=1 StartY=0 StartZ=0 EndX=65 EndY=0 EndZ=0
    g1: LineSegment [constr] StartX=65 StartY=0 StartZ=0 EndX=65 EndY=228.5 EndZ=0
    g2: LineSegment StartX=64 StartY=229.5 StartZ=0 EndX=1 EndY=229.5 EndZ=0
    g3: LineSegment StartX=0 StartY=228.5 StartZ=0 EndX=0 EndY=1 EndZ=0
    g4: ArcOfCircle CenterX=1 CenterY=228.5 CenterZ=0 NormalX=0 NormalY=0 NormalZ=1 AngleXU=0 Radius=1 StartAngle=1.5708 EndAngle=3.14159
    g5: GeomPoint [constr] X=0 Y=229.5 Z=0
    g6: ArcOfCircle CenterX=64 CenterY=228.5 CenterZ=0 NormalX=0 NormalY=0 NormalZ=1 AngleXU=0 Radius=1 StartAngle=-1.33e-14 EndAngle=1.5708
    g7: GeomPoint [constr] X=65 Y=229.5 Z=0
    g8: ArcOfCircle CenterX=1 CenterY=1 CenterZ=0 NormalX=0 NormalY=0 NormalZ=1 AngleXU=0 Radius=1 StartAngle=3.14159 EndAngle=4.71239
    g9: GeomPoint [constr] X=0 Y=0 Z=0
    g10: Circle CenterX=5 CenterY=8 CenterZ=0 NormalX=0 NormalY=0 NormalZ=1 AngleXU=0 Radius=1.75
    g11: Circle CenterX=5 CenterY=221.5 CenterZ=0 NormalX=0 NormalY=0 NormalZ=1 AngleXU=0 Radius=1.75
    g12: LineSegment StartX=65 StartY=228.5 StartZ=0 EndX=65 EndY=186 EndZ=0
    g13: LineSegment StartX=65 StartY=186 StartZ=0 EndX=3 EndY=186 EndZ=0
    g14: LineSegment StartX=3 StartY=186 StartZ=0 EndX=3 EndY=12 EndZ=0
    g15: LineSegment StartX=65 StartY=0 StartZ=0 EndX=65 EndY=3 EndZ=0
    g16: LineSegment StartX=65 StartY=3 StartZ=0 EndX=9 EndY=3 EndZ=0
    g17: LineSegment StartX=9 StartY=3 StartZ=0 EndX=9 EndY=12 EndZ=0
    g18: LineSegment StartX=9 StartY=12 StartZ=0 EndX=3 EndY=12 EndZ=0
    g19: LineSegment StartX=3 StartY=192 StartZ=0 EndX=40.5999 EndY=192 EndZ=0
    g20: LineSegment StartX=62 StartY=213.4 StartZ=0 EndX=62 EndY=216.254 EndZ=0
    g21: LineSegment StartX=51.754 StartY=226.5 StartZ=0 EndX=10 EndY=226.5 EndZ=0
    g22: LineSegment StartX=10 StartY=226.5 StartZ=0 EndX=10 EndY=216.5 EndZ=0
    g23: LineSegment StartX=10 StartY=216.5 StartZ=0 EndX=3 EndY=216.5 EndZ=0
    g24: LineSegment StartX=3 StartY=216.5 StartZ=0 EndX=3 EndY=192 EndZ=0
    g25: ArcOfCircle [constr] CenterX=51.754 CenterY=216.254 CenterZ=0 NormalX=0 NormalY=0 NormalZ=1 AngleXU=0 Radius=10.246 StartAngle=3e-16 EndAngle=1.5708
    g26: GeomPoint [constr] X=62 Y=226.5 Z=0
    g27: LineSegment StartX=62 StartY=216.254 StartZ=0 EndX=51.754 EndY=226.5 EndZ=0
    g28: ArcOfCircle [constr] CenterX=40.5999 CenterY=213.4 CenterZ=0 NormalX=0 NormalY=0 NormalZ=1 AngleXU=0 Radius=21.4001 StartAngle=4.71239 EndAngle=6.28319
    g29: GeomPoint [constr] X=62 Y=192 Z=0
    g30: LineSegment StartX=40.5999 StartY=192 StartZ=0 EndX=62 EndY=213.4 EndZ=0
  constraints (77):
    c: Coincident(g0,g1)
    c: Horizontal(g0)
    c: Horizontal(g2)
    c: Vertical(g1)
    c: Vertical(g3)
    c: Distance(g1,g9) = 65
    c: Coincident(g9,g-1)
    c: DistanceY(g9,g5) = 229.5
    c: PointOnObject(g5,g2)
    c: PointOnObject(g5,g3)
    c: Tangent(g2,g4) = -1.5708
    c: Tangent(g3,g4) = -1.5708
    c: PointOnObject(g7,g1)
    c: PointOnObject(g7,g2)
    c: Tangent(g1,g6) = -1.5708
    c: Tangent(g2,g6) = -1.5708
    c: PointOnObject(g9,g3)
    c: PointOnObject(g9,g0)
    c: Tangent(g3,g8) = -1.5708
    c: Tangent(g0,g8) = -1.5708
    c: Equal(g8,g4)
    c: Equal(g4,g6)
    c: Radius(g4) = 1
    c: Diameter(g10) = 3.5
    c: DistanceX(g10) = 5
    c: DistanceY(g10) = 8
    c: DistanceX(g11) = 5
    c: Distance(g11,g2) = 8
    c: Equal(g10,g11)
    c: Coincident(g12,g1)
    c: PointOnObject(g12,g1)
    c: Coincident(g13,g12)
    c: Horizontal(g13)
    c: Coincident(g14,g13)
    c: Vertical(g14)
    c: Distance(g15) = 3
    c: Coincident(g15,g0)
    c: PointOnObject(g15,g1)
    c: Coincident(g16,g15)
    c: Horizontal(g16)
    c: Coincident(g17,g16)
    c: Vertical(g17)
    c: Coincident(g18,g17)
    c: Horizontal(g18)
    c: Coincident(g14,g18)
    c: DistanceY(g14) = 12
    c: DistanceX(g17) = 9
    c: Horizontal(g19)
    c: Vertical(g20)
    c: Horizontal(g21)
    c: Coincident(g21,g22)
    c: Vertical(g22)
    c: Coincident(g22,g23)
    c: Horizontal(g23)
    c: Coincident(g23,g24)
    c: Coincident(g24,g19)
    c: Vertical(g24)
    c: Distance(g21,g2) = 3
    c: DistanceX(g22) = 10
    c: Distance(g22,g2) = 13
    c: DistanceX(g19) = 3
    c: Distance(g29,g12) = 3
    c: Distance(g13,g3) = 3
    c: Distance(g13,g19) = 6
    c: DistanceY(g13) = 186
    c: PointOnObject(g26,g21)
    c: PointOnObject(g26,g20)
    c: Tangent(g21,g25) = -1.5708
    c: Tangent(g20,g25) = -1.5708
    c: Coincident(g27,g21)
    c: Coincident(g27,g20)
    c: PointOnObject(g29,g19)
    c: PointOnObject(g29,g20)
    c: Tangent(g19,g28) = -1.5708
    c: Tangent(g20,g28) = -1.5708
    c: Coincident(g30,g19)
    c: Coincident(g30,g20)
FEATURE [PartDesign::Pad] Pad032
  Direction = (0,0,1)
  Length = 38
  Length2 = 10
  Placement = pos=(0,0,20) rot=(0,0,1;0rad)
  Profile = -> Sketch068
  ReferenceAxis = -> Sketch068 [N_Axis]
  Refine = true
  Suppressed = false
  Type = 0
  expr: Length = <<choices>>.exit_height - <<choices>>.base_max_thickness + 3
FEATURE [Sketcher::SketchObject] Sketch069
  ArcFitTolerance = 1e-06
  AttachmentSupport = -> [DatumPlane015]
  FullyConstrained = true
  MakeInternals = false
  MapMode = 5
  Placement = pos=(0,0,20) rot=(0,0,1;0rad)
  expr: Constraints[10] = <<components>>.m3_hole
  expr: Constraints[12] = <<components>>.frame_h - 8
  expr: Constraints[7] = <<components>>.frame_h - 3
  sketch-geometry (13):
    g0: LineSegment StartX=0 StartY=226.5 StartZ=0 EndX=0 EndY=188 EndZ=0
    g1: LineSegment StartX=10 StartY=226.5 StartZ=0 EndX=0 EndY=226.5 EndZ=0
    g2: Circle CenterX=5 CenterY=221.5 CenterZ=0 NormalX=0 NormalY=0 NormalZ=1 AngleXU=0 Radius=1.75
    g3: LineSegment [constr] StartX=10 StartY=188 StartZ=0 EndX=10 EndY=216.5 EndZ=0
    g4: LineSegment StartX=0 StartY=188 StartZ=0 EndX=3 EndY=188 EndZ=0
    g5: LineSegment [constr] StartX=3 StartY=188 StartZ=0 EndX=10 EndY=188 EndZ=0
    g6: LineSegment StartX=10 StartY=216.5 StartZ=0 EndX=3 EndY=216.5 EndZ=0
    g7: LineSegment StartX=3 StartY=216.5 StartZ=0 EndX=3 EndY=188 EndZ=0
    g8: LineSegment StartX=10 StartY=216.5 StartZ=0 EndX=10 EndY=224.5 EndZ=0
    g9: LineSegment [constr] StartX=10 StartY=224.5 StartZ=0 EndX=10 EndY=226.5 EndZ=0
    g10: LineSegment StartX=10 StartY=224.5 StartZ=0 EndX=55 EndY=224.5 EndZ=0
    g11: LineSegment StartX=55 StartY=224.5 StartZ=0 EndX=55 EndY=226.5 EndZ=0
    g12: LineSegment StartX=55 StartY=226.5 StartZ=0 EndX=10 EndY=226.5 EndZ=0
  constraints (37):
    c: Coincident(g0,g4)
    c: Coincident(g5,g3)
    c: Coincident(g9,g1)
    c: Coincident(g1,g0)
    c: Vertical(g0)
    c: Horizontal(g1)
    c: PointOnObject(g0,g-2)
    c: DistanceY(g0) = 226.5
    c: DistanceX(g1,g1) = 10
    c: DistanceY(g0) = 188
    c: Diameter(g2) = 3.5
    c: DistanceX(g2) = 5
    c: DistanceY(g2) = 221.5
    c: Coincident(g3,g8)
    c: Vertical(g3)
    c: Coincident(g4,g5)
    c: Horizontal(g4)
    c: Horizontal(g5)
    c: Coincident(g3,g6)
    c: Horizontal(g6)
    c: Coincident(g6,g7)
    c: Coincident(g7,g4)
    c: Vertical(g7)
    c: DistanceX(g4,g4) = 3
    c: DistanceY(g8,g9) = 10
    c: Coincident(g8,g9)
    c: Vertical(g8)
    c: Vertical(g9)
    c: Coincident(g8,g10)
    c: Horizontal(g10)
    c: Coincident(g10,g11)
    c: Vertical(g11)
    c: Coincident(g11,g12)
    c: Coincident(g12,g1)
    c: Horizontal(g12)
    c: DistanceY(g11,g11) = 2
    c: DistanceX(g11) = 55
FEATURE [PartDesign::Pad] Pad033
  BaseFeature = -> Pad032
  Direction = (0,0,1)
  Length = 17
  Length2 = 10
  Placement = pos=(0,0,20) rot=(0,0,1;0rad)
  Profile = -> Sketch069
  ReferenceAxis = -> Sketch069 [N_Axis]
  Refine = true
  Reversed = true
  Suppressed = false
  Type = 0
  expr: Length = <<choices>>.base_max_thickness - 3
FEATURE [Sketcher::SketchObject] Sketch070
  ArcFitTolerance = 1e-06
  AttachmentSupport = -> [YZ_Plane035]
  FullyConstrained = true
  MakeInternals = false
  MapMode = 5
  Placement = pos=(0,0,0) rot=(0.57735,0.57735,0.57735;2.0944rad)
  expr: Constraints[1] = <<components>>.m3_hole
  sketch-geometry (16):
    g0: Circle CenterX=204.62 CenterY=50 CenterZ=0 NormalX=0 NormalY=0 NormalZ=1 AngleXU=0 Radius=1.75
    g1: Circle CenterX=204.62 CenterY=10 CenterZ=0 NormalX=0 NormalY=0 NormalZ=1 AngleXU=0 Radius=1.75
    g2: LineSegment [constr] StartX=204.62 StartY=50 StartZ=0 EndX=204.62 EndY=10 EndZ=0
    g3: LineSegment StartX=194.62 StartY=14.55 StartZ=0 EndX=214.62 EndY=14.55 EndZ=0
    g4: LineSegment StartX=215.62 StartY=15.55 StartZ=0 EndX=215.62 EndY=44.45 EndZ=0
    g5: LineSegment StartX=214.62 StartY=45.45 StartZ=0 EndX=194.62 EndY=45.45 EndZ=0
    g6: LineSegment StartX=193.62 StartY=44.45 StartZ=0 EndX=193.62 EndY=15.55 EndZ=0
    g7: GeomPoint [constr] X=204.62 Y=30 Z=0
    g8: ArcOfCircle CenterX=194.62 CenterY=44.45 CenterZ=0 NormalX=0 NormalY=0 NormalZ=1 AngleXU=0 Radius=1 StartAngle=1.5708 EndAngle=3.14159
    g9: GeomPoint [constr] X=193.62 Y=45.45 Z=0
    g10: ArcOfCircle CenterX=194.62 CenterY=15.55 CenterZ=0 NormalX=0 NormalY=0 NormalZ=1 AngleXU=0 Radius=1 StartAngle=3.14159 EndAngle=4.71239
    g11: GeomPoint [constr] X=193.62 Y=14.55 Z=0
    g12: ArcOfCircle CenterX=214.62 CenterY=15.55 CenterZ=0 NormalX=0 NormalY=0 NormalZ=1 AngleXU=0 Radius=1 StartAngle=4.71239 EndAngle=6.28319
    g13: GeomPoint [constr] X=215.62 Y=14.55 Z=0
    g14: ArcOfCircle CenterX=214.62 CenterY=44.45 CenterZ=0 NormalX=0 NormalY=0 NormalZ=1 AngleXU=0 Radius=1 StartAngle=-3.6e-15 EndAngle=1.5708
    g15: GeomPoint [constr] X=215.62 Y=45.45 Z=0
  constraints (36):
    c: Equal(g0,g1)
    c: Diameter(g0) = 3.5
    c: Coincident(g2,g0)
    c: Coincident(g2,g1)
    c: Vertical(g2)
    c: DistanceY(g2,g2) = 40
    c: Horizontal(g3)
    c: Horizontal(g5)
    c: Vertical(g4)
    c: Vertical(g6)
    c: Symmetric(g15,g11,g7)
    c: Distance(g13,g11) = 22
    c: Distance(g11,g9) = 30.9
    c: Symmetric(g2,g2,g7)
    c: DistanceY(g1) = 10
    c: PointOnObject(g9,g5)
    c: PointOnObject(g9,g6)
    c: Tangent(g5,g8) = -1.5708
    c: Tangent(g6,g8) = -1.5708
    c: PointOnObject(g11,g6)
    c: PointOnObject(g11,g3)
    c: Tangent(g6,g10) = -1.5708
    c: Tangent(g3,g10) = -1.5708
    c: PointOnObject(g13,g3)
    c: PointOnObject(g13,g4)
    c: Tangent(g3,g12) = -1.5708
    c: Tangent(g4,g12) = -1.5708
    c: PointOnObject(g15,g4)
    c: PointOnObject(g15,g5)
    c: Tangent(g4,g14) = -1.5708
    c: Tangent(g5,g14) = -1.5708
    c: DistanceX(g7) = 204.62
    c: Equal(g12,g14)
    c: Equal(g14,g8)
    c: Equal(g8,g10)
    c: Radius(g10) = 1
FEATURE [App::Link] EXIT_DUCT  label="EXIT_DUCT001"
  LinkPlacement = pos=(789.769,-462.714,-12.7734) rot=(0.075569,0.096295,0.99248;0.012724rad)
  LinkedObject = -> Part007
  Placement = pos=(789.769,-462.714,-12.7734) rot=(0.075569,0.096295,0.99248;0.012724rad)
FEATURE [PartDesign::Plane] DatumPlane016
  AttachmentOffset = pos=(0,0,-10) rot=(0,0,1;0rad)
  AttachmentSupport = -> [XY_Plane007]
  Length = 463.812
  MapMode = 5
  Placement = pos=(0,0,-10) rot=(0,0,1;0rad)
  ResizeMode = 0
  Width = 318.312
FEATURE [Sketcher::SketchObject] Sketch071
  ArcFitTolerance = 1e-06
  AttachmentSupport = -> [DatumPlane016]
  FullyConstrained = true
  MakeInternals = false
  MapMode = 5
  Placement = pos=(0,0,-10) rot=(0,0,1;0rad)
  expr: Constraints[10] = <<components>>.frame_h
  expr: Constraints[30] = <<components>>.m3_threadhole
  expr: Constraints[43] = 188 + 8
  expr: Constraints[54] = <<components>>.m3_threadhole
  expr: Constraints[9] = <<components>>.frame_w
  sketch-geometry (22):
    g0: LineSegment [constr] StartX=0 StartY=0 StartZ=0 EndX=375 EndY=0 EndZ=0
    g1: LineSegment [constr] StartX=375 StartY=0 StartZ=0 EndX=375 EndY=229.5 EndZ=0
    g2: LineSegment [constr] StartX=375 StartY=229.5 StartZ=0 EndX=0 EndY=229.5 EndZ=0
    g3: LineSegment [constr] StartX=0 StartY=229.5 StartZ=0 EndX=0 EndY=0 EndZ=0
    g4: LineSegment [constr] StartX=5 StartY=8 StartZ=0 EndX=370 EndY=8 EndZ=0
    g5: LineSegment [constr] StartX=370 StartY=8 StartZ=0 EndX=370 EndY=221.5 EndZ=0
    g6: LineSegment [constr] StartX=370 StartY=221.5 StartZ=0 EndX=5 EndY=221.5 EndZ=0
    g7: LineSegment [constr] StartX=5 StartY=221.5 StartZ=0 EndX=5 EndY=8 EndZ=0
    g8: Circle CenterX=5 CenterY=221.5 CenterZ=0 NormalX=0 NormalY=0 NormalZ=1 AngleXU=0 Radius=1.25
    g9: Circle CenterX=5 CenterY=8 CenterZ=0 NormalX=0 NormalY=0 NormalZ=1 AngleXU=0 Radius=1.25
    g10: Circle CenterX=370 CenterY=8 CenterZ=0 NormalX=0 NormalY=0 NormalZ=1 AngleXU=0 Radius=1.25
    g11: Circle CenterX=370 CenterY=221.5 CenterZ=0 NormalX=0 NormalY=0 NormalZ=1 AngleXU=0 Radius=1.25
    g12: Circle CenterX=370 CenterY=114.75 CenterZ=0 NormalX=0 NormalY=0 NormalZ=1 AngleXU=0 Radius=1.25
    g13: LineSegment [constr] StartX=5 StartY=196 StartZ=0 EndX=370 EndY=196 EndZ=0
    g14: GeomPoint [constr] X=187.5 Y=196 Z=0
    g15: LineSegment [constr] StartX=162.5 StartY=196 StartZ=0 EndX=212.5 EndY=196 EndZ=0
    g16: Circle CenterX=162.5 CenterY=196 CenterZ=0 NormalX=0 NormalY=0 NormalZ=1 AngleXU=0 Radius=1.25
    g17: Circle CenterX=212.5 CenterY=196 CenterZ=0 NormalX=0 NormalY=0 NormalZ=1 AngleXU=0 Radius=1.25
    g18: Circle CenterX=90 CenterY=196 CenterZ=0 NormalX=0 NormalY=0 NormalZ=1 AngleXU=0 Radius=1.25
    g19: Circle CenterX=285 CenterY=196 CenterZ=0 NormalX=0 NormalY=0 NormalZ=1 AngleXU=0 Radius=1.25
    g20: Circle CenterX=187.5 CenterY=5 CenterZ=0 NormalX=0 NormalY=0 NormalZ=1 AngleXU=0 Radius=1.25
    g21: LineSegment [constr] StartX=187.5 StartY=0 StartZ=0 EndX=187.5 EndY=5 EndZ=0
  constraints (55):
    c: Coincident(g0,g1)
    c: Coincident(g1,g2)
    c: Coincident(g2,g3)
    c: Coincident(g3,g0)
    c: Horizontal(g0)
    c: Horizontal(g2)
    c: Vertical(g1)
    c: Vertical(g3)
    c: Coincident(g0,g-1)
    c: DistanceX(g2,g2) = 375
    c: DistanceY(g1,g1) = 229.5
    c: Coincident(g4,g5)
    c: Coincident(g5,g6)
    c: Coincident(g6,g7)
    c: Coincident(g7,g4)
    c: Horizontal(g4)
    c: Horizontal(g6)
    c: Vertical(g5)
    c: Vertical(g7)
    c: DistanceX(g4) = 5
    c: DistanceY(g4) = 8
    c: Distance(g6,g2) = 8
    c: Distance(g5,g1) = 5
    c: Coincident(g8,g6)
    c: Coincident(g9,g4)
    c: Coincident(g10,g4)
    c: Coincident(g11,g5)
    c: Equal(g11,g8)
    c: Equal(g8,g9)
    c: Equal(g9,g10)
    c: Diameter(g10) = 2.5
    c: Symmetric(g5,g5,g12)
    c: Equal(g12,g10)
    c: PointOnObject(g13,g7)
    c: PointOnObject(g13,g5)
    c: Horizontal(g13)
    c: Symmetric(g13,g13,g14)
    c: PointOnObject(g15,g13)
    c: Symmetric(g15,g15,g14)
    c: Coincident(g16,g15)
    c: Coincident(g17,g15)
    c: Equal(g17,g16)
    c: Equal(g16,g8)
    c: DistanceY(g14) = 196
    c: DistanceX(g15,g15) = 50
    c: PointOnObject(g18,g13)
    c: Equal(g19,g18)
    c: Equal(g18,g17)
    c: Symmetric(g18,g19,g14)
    c: DistanceX(g18) = 90
    c: Symmetric(g0,g0,g21)
    c: Coincident(g21,g20)
    c: Vertical(g21)
    c: DistanceY(g21,g21) = 5
    c: Diameter(g20) = 2.5
FEATURE [PartDesign::Pocket] Pocket032
  BaseFeature = -> Pocket002
  Direction = (0,0,-1)
  Length = 5
  Length2 = 5
  Profile = -> Sketch071
  ReferenceAxis = -> Sketch071 [N_Axis]
  Refine = true
  Reversed = true
  Suppressed = false
  Type = 0
FEATURE [PartDesign::Body] Body003
  AllowCompound = false
  Group = -> [Sketch006,Pad006,Sketch007,Pocket,Sketch008,Pocket001,Sketch009,Pocket002,DatumPlane016,Sketch071,Pocket032]
  Origin = -> Origin007
  Tip = -> Pocket032
FEATURE [App::Part] Part003  label="FRAME"
  Group = -> [Body003]
  Origin = -> Origin006
FEATURE [PartDesign::Plane] DatumPlane017
  AttachmentOffset = pos=(0,0,-229.5) rot=(0,0,1;0rad)
  AttachmentSupport = -> [XZ_Plane035]
  Length = 107.286
  MapMode = 5
  Placement = pos=(0,229.5,-5.1e-14) rot=(1,0,0;1.5708rad)
  ResizeMode = 0
  Width = 100.286
  expr: .AttachmentOffset.Base.z = -<<components>>.frame_h
FEATURE [PartDesign::Plane] DatumPlane018
  AttachmentOffset = pos=(0,0,-188) rot=(0,0,1;0rad)
  AttachmentSupport = -> [XZ_Plane035]
  Length = 107.286
  MapMode = 5
  Placement = pos=(0,188,-4.17e-14) rot=(1,0,0;1.5708rad)
  ResizeMode = 0
  Width = 100.286
FEATURE [Sketcher::SketchObject] Sketch072
  ArcFitTolerance = 1e-06
  AttachmentSupport = -> [DatumPlane017]
  FullyConstrained = true
  MakeInternals = false
  MapMode = 5
  Placement = pos=(0,229.5,-5.1e-14) rot=(1,0,0;1.5708rad)
  expr: Constraints[1] = 65 / 2
  expr: Constraints[2] = (<<choices>>.exit_height - <<choices>>.base_max_thickness) * 0.5 + <<choices>>.base_max_thickness + 7.5
  sketch-geometry (1):
    g0: Circle CenterX=32.5 CenterY=45 CenterZ=0 NormalX=0 NormalY=0 NormalZ=1 AngleXU=0 Radius=8.15
  constraints (3):
    c: Diameter(g0) = 16.3
    c: DistanceX(g-1,g0) = 32.5
    c: DistanceY(g0) = 45
FEATURE [PartDesign::Pad] Pad034
  BaseFeature = -> Pad033
  Direction = (0,0,1)
  Length = 3
  Length2 = 10
  Placement = pos=(0,0,20) rot=(0,0,1;0rad)
  Profile = -> Sketch069
  ReferenceAxis = -> Sketch069 [N_Axis]
  Refine = true
  Suppressed = false
  Type = 0
FEATURE [PartDesign::Pocket] Pocket031
  BaseFeature = -> Pad034
  Direction = (-1,0,0)
  Length = 5
  Length2 = 5
  Placement = pos=(0,0,20) rot=(0,0,1;0rad)
  Profile = -> Sketch070
  ReferenceAxis = -> Sketch070 [N_Axis]
  Refine = true
  Reversed = true
  Suppressed = false
  Type = 0
FEATURE [PartDesign::Pocket] Pocket033
  BaseFeature = -> Pocket031
  Direction = (0,1,-2e-16)
  Length = 5
  Length2 = 5
  Placement = pos=(0,0,20) rot=(0,0,1;0rad)
  Profile = -> Sketch072
  ReferenceAxis = -> Sketch072 [N_Axis]
  Refine = true
  Reversed = true
  Suppressed = false
  Type = 0
FEATURE [Sketcher::SketchObject] Sketch073
  ArcFitTolerance = 1e-06
  AttachmentSupport = -> [DatumPlane018]
  FullyConstrained = false
  MakeInternals = false
  MapMode = 5
  Placement = pos=(0,188,-4.17e-14) rot=(1,0,0;1.5708rad)
  sketch-geometry (5):
    g0: LineSegment StartX=8.21147 StartY=51.4718 StartZ=0 EndX=8.21147 EndY=26.7757 EndZ=0
    g1: LineSegment StartX=8.21147 StartY=26.7757 StartZ=0 EndX=41.1685 EndY=26.7757 EndZ=0
    g2: LineSegment StartX=41.1685 StartY=26.7757 StartZ=0 EndX=57.8674 EndY=40.0932 EndZ=0
    g3: LineSegment StartX=57.8674 StartY=40.0932 StartZ=0 EndX=40.5009 EndY=51.4718 EndZ=0
    g4: LineSegment StartX=40.5009 StartY=51.4718 StartZ=0 EndX=8.21147 EndY=51.4718 EndZ=0
  constraints (8):
    c: Vertical(g0)
    c: Coincident(g0,g1)
    c: Horizontal(g1)
    c: Coincident(g1,g2)
    c: Coincident(g2,g3)
    c: Coincident(g3,g4)
    c: Horizontal(g4)
    c: Coincident(g4,g0)
FEATURE [PartDesign::Pocket] Pocket034
  BaseFeature = -> Pocket033
  Direction = (0,1,-2e-16)
  Length = 33
  Length2 = 5
  Midplane = true
  Placement = pos=(0,0,20) rot=(0,0,1;0rad)
  Profile = -> Sketch073
  ReferenceAxis = -> Sketch073 [N_Axis]
  Refine = true
  Suppressed = false
  Type = 0
FEATURE [PartDesign::Chamfer] Chamfer007
  Angle = 45
  Base = -> Pocket034 [Edge72,Edge81]
  BaseFeature = -> Pocket034
  ChamferType = 0
  FlipDirection = false
  Placement = pos=(0,0,20) rot=(0,0,1;0rad)
  Refine = true
  Size = 1.75
  Size2 = 1
  SupportTransform = false
  Suppressed = false
  UseAllEdges = false
FEATURE [Sketcher::SketchObject] Sketch074
  ArcFitTolerance = 1e-06
  AttachmentSupport = -> [XZ_Plane037]
  FullyConstrained = true
  MakeInternals = false
  MapMode = 5
  Placement = pos=(0,0,0) rot=(1,0,0;1.5708rad)
  expr: Constraints[10] = <<choices>>.exit_height + 3 - <<choices>>.base_max_thickness
  expr: Constraints[9] = <<components>>.frame_w - 2 * 65
  sketch-geometry (4):
    g0: LineSegment StartX=0 StartY=0 StartZ=0 EndX=245 EndY=0 EndZ=0
    g1: LineSegment StartX=245 StartY=0 StartZ=0 EndX=245 EndY=38 EndZ=0
    g2: LineSegment StartX=245 StartY=38 StartZ=0 EndX=0 EndY=38 EndZ=0
    g3: LineSegment StartX=0 StartY=38 StartZ=0 EndX=0 EndY=0 EndZ=0
  constraints (11):
    c: Coincident(g0,g1)
    c: Coincident(g1,g2)
    c: Coincident(g2,g3)
    c: Coincident(g3,g0)
    c: Horizontal(g0)
    c: Horizontal(g2)
    c: Vertical(g1)
    c: Vertical(g3)
    c: Coincident(g0,g-1)
    c: DistanceX(g2,g2) = 245
    c: DistanceY(g1,g1) = 38
FEATURE [PartDesign::Pad] Pad035
  Direction = (0,-1,2e-16)
  Length = 3
  Length2 = 10
  Placement = pos=(0,0,0) rot=(1,0,0;1.5708rad)
  Profile = -> Sketch074
  ReferenceAxis = -> Sketch074 [N_Axis]
  Refine = true
  Suppressed = false
  Type = 0
FEATURE [Sketcher::SketchObject] Sketch075
  ArcFitTolerance = 1e-06
  AttachmentSupport = -> [XZ_Plane037]
  FullyConstrained = false
  MakeInternals = false
  MapMode = 5
  Placement = pos=(0,0,0) rot=(1,0,0;1.5708rad)
  expr: Constraints[10] = 5 + <<components>>.frame_w - 2 * 65
  expr: Constraints[7] = <<choices>>.exit_height + 3 - <<choices>>.base_max_thickness
  expr: Constraints[9] = -<<choices>>.base_max_thickness + <<choices>>.base_under_mb_thickness + 0.5
  sketch-geometry (14):
    g0: LineSegment StartX=-5 StartY=38 StartZ=0 EndX=-5 EndY=-18.25 EndZ=0
    g1: LineSegment StartX=250 StartY=-18.25 StartZ=0 EndX=250 EndY=38 EndZ=0
    g2: LineSegment StartX=250 StartY=38 StartZ=0 EndX=-5 EndY=38 EndZ=0
    g3: LineSegment [constr] StartX=112.5 StartY=-28.25 StartZ=0 EndX=132.5 EndY=-28.25 EndZ=0
    g4: LineSegment StartX=132.5 StartY=-8.25 StartZ=0 EndX=112.5 EndY=-8.25 EndZ=0
    g5: GeomPoint [constr] X=122.5 Y=-18.25 Z=0
    g6: LineSegment StartX=112.5 StartY=-8.25 StartZ=0 EndX=112.5 EndY=-18.25 EndZ=0
    g7: LineSegment [constr] StartX=112.5 StartY=-18.25 StartZ=0 EndX=112.5 EndY=-28.25 EndZ=0
    g8: LineSegment [constr] StartX=132.5 StartY=-28.25 StartZ=0 EndX=132.5 EndY=-18.25 EndZ=0
    g9: LineSegment StartX=132.5 StartY=-18.25 StartZ=0 EndX=132.5 EndY=-8.25 EndZ=0
    g10: LineSegment [constr] StartX=122.5 StartY=-18.25 StartZ=0 EndX=132.5 EndY=-18.25 EndZ=0
    g11: LineSegment StartX=132.5 StartY=-18.25 StartZ=0 EndX=250 EndY=-18.25 EndZ=0
    g12: LineSegment StartX=-5 StartY=-18.25 StartZ=0 EndX=112.5 EndY=-18.25 EndZ=0
    g13: LineSegment [constr] StartX=112.5 StartY=-18.25 StartZ=0 EndX=122.5 EndY=-18.25 EndZ=0
  constraints (36):
    c: Coincident(g0,g12)
    c: Coincident(g11,g1)
    c: Coincident(g1,g2)
    c: Coincident(g2,g0)
    c: Vertical(g0)
    c: Vertical(g1)
    c: Horizontal(g2)
    c: DistanceY(g0) = 38
    c: DistanceX(g0) = -5
    c: DistanceY(g0) = -18.25
    c: DistanceX(g1) = 250
    c: Coincident(g3,g8)
    c: Coincident(g9,g4)
    c: Coincident(g4,g6)
    c: Coincident(g7,g3)
    c: Horizontal(g3)
    c: Horizontal(g4)
    c: Symmetric(g4,g3,g5)
    c: Distance(g8,g7) = 20
    c: Distance(g3,g4) = 20
    c: Symmetric(g12,g11,g5)
    c: Coincident(g6,g7)
    c: Vertical(g6)
    c: Vertical(g7)
    c: Coincident(g8,g9)
    c: Vertical(g8)
    c: Vertical(g9)
    c: Coincident(g13,g10)
    c: Coincident(g10,g11)
    c: Horizontal(g10)
    c: Horizontal(g11)
    c: Coincident(g8,g10)
    c: Coincident(g12,g13)
    c: Horizontal(g12)
    c: Horizontal(g13)
    c: Coincident(g12,g6)
FEATURE [PartDesign::Pad] Pad036
  BaseFeature = -> Pad035
  Direction = (0,-1,2e-16)
  Length = 2
  Length2 = 10
  Placement = pos=(0,0,0) rot=(1,0,0;1.5708rad)
  Profile = -> Sketch075
  ReferenceAxis = -> Sketch075 [N_Axis]
  Refine = true
  Reversed = true
  Suppressed = false
  Type = 0
FEATURE [App::Link] LEFT_END  label="LEFT_END001"
  LinkPlacement = pos=(433.794,-467.207,-15.3394) rot=(0.075569,0.096295,0.99248;0.012724rad)
  LinkedObject = -> Part016
  Placement = pos=(433.794,-467.207,-15.3394) rot=(0.075569,0.096295,0.99248;0.012724rad)
FEATURE [App::Link] FRONT_VENT  label="FRONT_VENT001"
  LinkPlacement = pos=(498.776,-463.405,4.63429) rot=(0.075569,0.096295,0.99248;0.012724rad)
  LinkedObject = -> Part017
  Placement = pos=(498.776,-463.405,4.63429) rot=(0.075569,0.096295,0.99248;0.012724rad)
FEATURE [App::Link] FRAME  label="FRAME001"
  LinkPlacement = pos=(433.878,-467.272,52.6606) rot=(0.075569,0.096295,0.99248;0.012724rad)
  LinkedObject = -> Part003
  Placement = pos=(433.878,-467.272,52.6606) rot=(0.075569,0.096295,0.99248;0.012724rad)
FEATURE [App::Link] SCREEN  label="SCREEN001"
  LinkPlacement = pos=(436.831,-463.683,51.1604) rot=(0.075569,0.096295,0.99248;0.012724rad)
  LinkedObject = -> Part001
  Placement = pos=(436.831,-463.683,51.1604) rot=(0.075569,0.096295,0.99248;0.012724rad)
FEATURE [App::FeaturePython] Joint012  label="Fixed009"  # Assembly joint (typed FeaturePython)
  Activated = true
  AngleMax = 0
  AngleMin = 0
  Detach1 = false
  Detach2 = false
  Distance = 0
  Distance2 = 0
  EnableAngleMax = false
  EnableAngleMin = false
  EnableLengthMax = false
  EnableLengthMin = false
  JointType = 0 (Fixed)
  LengthMax = 0
  LengthMin = 0
  Placement1 = pos=(4.95e-13,111.2,-1.5) rot=(-0.57735,-0.57735,0.57735;4.18879rad)
  Placement2 = pos=(3,114.75,-3) rot=(-0.57735,-0.57735,0.57735;4.18879rad)
  Reference1 = -> Assembly [SCREEN.Body001.Edge11,SCREEN.Body001.Edge11]
  Reference2 = -> Assembly [FRAME.Body003.Edge65,FRAME.Body003.Edge65]
FEATURE [Sketcher::SketchObject] Sketch076
  ArcFitTolerance = 1e-06
  AttachmentSupport = -> [XY_Plane031]
  FullyConstrained = false
  MakeInternals = false
  MapMode = 5
  expr: Constraints[16] = <<choices>>.shroud_base_screw_x
  expr: Constraints[17] = <<choices>>.shroud_base_screw_y1
  expr: Constraints[18] = <<choices>>.shroud_base_screw_y2
  expr: Constraints[9] = <<components>>.m3_hole
  sketch-geometry (8):
    g0: LineSegment StartX=340 StartY=208 StartZ=0 EndX=340 EndY=3.76862 EndZ=0
    g1: LineSegment StartX=340 StartY=3.76862 StartZ=0 EndX=325 EndY=20.5494 EndZ=0
    g2: LineSegment StartX=325 StartY=20.5494 StartZ=0 EndX=325 EndY=196.984 EndZ=0
    g3: LineSegment StartX=325 StartY=196.984 StartZ=0 EndX=340 EndY=208 EndZ=0
    g4: Circle CenterX=332.5 CenterY=40 CenterZ=0 NormalX=0 NormalY=0 NormalZ=1 AngleXU=0 Radius=1.75
    g5: Circle CenterX=332.5 CenterY=120 CenterZ=0 NormalX=0 NormalY=0 NormalZ=1 AngleXU=0 Radius=1.75
    g6: LineSegment [constr] StartX=332.5 StartY=120 StartZ=0 EndX=332.5 EndY=40 EndZ=0
    g7: LineSegment [constr] StartX=332.5 StartY=40 StartZ=0 EndX=332.5 EndY=0 EndZ=0
  constraints (20):
    c: Vertical(g0)
    c: Coincident(g0,g1)
    c: Coincident(g1,g2)
    c: Vertical(g2)
    c: Coincident(g2,g3)
    c: Coincident(g3,g0)
    c: DistanceX(g0) = 340
    c: DistanceX(g2) = 325
    c: Equal(g5,g4)
    c: Diameter(g5) = 3.5
    c: Coincident(g6,g5)
    c: Coincident(g6,g4)
    c: Vertical(g6)
    c: Coincident(g7,g4)
    c: PointOnObject(g7,g-1)
    c: Vertical(g7)
    c: DistanceX(g7) = 332.5
    c: DistanceY(g4) = 40
    c: DistanceY(g5) = 120
    c: DistanceY(g0) = 208
FEATURE [PartDesign::Pad] Pad037
  BaseFeature = -> AdditiveLoft002
  Direction = (0,0,1)
  Length = 2
  Length2 = 10
  Placement = pos=(286,0,0) rot=(0.57735,0.57735,0.57735;2.0944rad)
  Profile = -> Sketch076
  ReferenceAxis = -> Sketch076 [N_Axis]
  Refine = true
  Suppressed = false
  Type = 0
FEATURE [PartDesign::Chamfer] Chamfer008
  Angle = 45
  Base = -> Pad037 [Edge94,Edge93]
  BaseFeature = -> Pad037
  ChamferType = 0
  FlipDirection = false
  Placement = pos=(286,0,0) rot=(0.57735,0.57735,0.57735;2.0944rad)
  Refine = true
  Size = 1.7
  Size2 = 1
  SupportTransform = false
  Suppressed = false
  UseAllEdges = false
FEATURE [PartDesign::Plane] DatumPlane019
  AttachmentOffset = pos=(0,0,-160) rot=(0,0,1;0rad)
  AttachmentSupport = -> [XZ_Plane009]
  Length = 106.638
  MapMode = 5
  Placement = pos=(0,160,-3.55e-14) rot=(1,0,0;1.5708rad)
  ResizeMode = 0
  Width = 63.6382
  expr: .AttachmentOffset.Base.z = -<<components>>.gpu_h
FEATURE [Sketcher::SketchObject] Sketch077  label="this will be the end sockets sketch"
  ArcFitTolerance = 1e-06
  AttachmentSupport = -> [DatumPlane019]
  FullyConstrained = false
  MakeInternals = false
  MapMode = 5
  Placement = pos=(0,160,-3.55e-14) rot=(1,0,0;1.5708rad)
  expr: Constraints[18] = <<components>>.m3_hole
  sketch-geometry (11):
    g0: LineSegment StartX=22.9359 StartY=12.1138 StartZ=0 EndX=39.5359 EndY=12.1138 EndZ=0
    g1: LineSegment StartX=39.5359 StartY=12.1138 StartZ=0 EndX=39.5359 EndY=6.11381 EndZ=0
    g2: LineSegment StartX=39.5359 StartY=6.11381 StartZ=0 EndX=36.2624 EndY=5.21381 EndZ=0
    g3: LineSegment StartX=36.2624 StartY=5.21381 StartZ=0 EndX=26.2095 EndY=5.21381 EndZ=0
    g4: LineSegment StartX=26.2095 StartY=5.21381 StartZ=0 EndX=22.9359 EndY=6.11381 EndZ=0
    g5: LineSegment StartX=22.9359 StartY=6.11381 StartZ=0 EndX=22.9359 EndY=12.1138 EndZ=0
    g6: LineSegment [constr] StartX=31.2359 StartY=12.1138 StartZ=0 EndX=31.2359 EndY=14.49 EndZ=0
    g7: Circle CenterX=31.2359 CenterY=14.49 CenterZ=0 NormalX=0 NormalY=0 NormalZ=1 AngleXU=0 Radius=1.75
    g8: LineSegment [constr] StartX=31.2359 StartY=14.49 StartZ=0 EndX=52.2359 EndY=14.49 EndZ=0
    g9: Circle CenterX=52.2359 CenterY=14.49 CenterZ=0 NormalX=0 NormalY=0 NormalZ=1 AngleXU=0 Radius=1.75
    g10: LineSegment [constr] StartX=52.2359 StartY=14.49 StartZ=0 EndX=66.2359 EndY=14.49 EndZ=0
  constraints (27):
    c: Horizontal(g0)
    c: Coincident(g0,g1)
    c: Vertical(g1)
    c: Coincident(g1,g2)
    c: Coincident(g2,g3)
    c: Coincident(g3,g4)
    c: Coincident(g4,g5)
    c: Coincident(g5,g0)
    c: Vertical(g5)
    c: Horizontal(g3)
    c: Distance(g3,g0) = 6.9
    c: DistanceX(g0,g0) = 16.6
    c: DistanceY(g1,g1) = 6
    c: Equal(g5,g1)
    c: Equal(g4,g2)
    c: Symmetric(g0,g0,g6)
    c: Vertical(g6)
    c: Coincident(g7,g6)
    c: Diameter(g7) = 3.5
    c: Distance(g8) = 21
    c: Coincident(g8,g6)
    c: Horizontal(g8)
    c: Coincident(g9,g8)
    c: Equal(g9,g7)
    c: Coincident(g10,g8)
    c: Horizontal(g10)
    c: DistanceX(g10,g10) = 14
FEATURE [PartDesign::Body] Body004
  AllowCompound = false
  Group = -> [Sketch011,Pad009,DatumPlane019,Sketch077]
  Origin = -> Origin009
  Tip = -> Pad009
FEATURE [App::Part] Part004  label="GPU"
  Group = -> [Body004]
  Origin = -> Origin008
FEATURE [Sketcher::SketchObject] Sketch078
  ArcFitTolerance = 1e-06
  AttachmentSupport = -> [XY_Plane013]
  FullyConstrained = true
  MakeInternals = false
  MapMode = 5
  expr: Constraints[2] = <<choices>>.leg_bracket_slot_end_dist_from_front + 10 + 1 + 5 + 1
  expr: Constraints[4] = <<components>>.m3_threadhole
  sketch-geometry (17):
    g0: LineSegment StartX=114.5 StartY=187 StartZ=0 EndX=114.5 EndY=178 EndZ=0
    g1: LineSegment StartX=104.5 StartY=178 StartZ=0 EndX=104.5 EndY=187 EndZ=0
    g2: LineSegment StartX=104.5 StartY=187 StartZ=0 EndX=114.5 EndY=187 EndZ=0
    g3: Circle CenterX=109.5 CenterY=182.5 CenterZ=0 NormalX=0 NormalY=0 NormalZ=1 AngleXU=0 Radius=1.25
    g4: LineSegment [constr] StartX=109.5 StartY=182.5 StartZ=0 EndX=109.5 EndY=187 EndZ=0
    g5: LineSegment [constr] StartX=104.5 StartY=178 StartZ=0 EndX=114.5 EndY=178 EndZ=0
    g6: LineSegment StartX=125.5 StartY=187 StartZ=0 EndX=125.5 EndY=178 EndZ=0
    g7: LineSegment [constr] StartX=125.5 StartY=178 StartZ=0 EndX=135.5 EndY=178 EndZ=0
    g8: LineSegment [constr] StartX=135.5 StartY=178 StartZ=0 EndX=135.5 EndY=187 EndZ=0
    g9: LineSegment [constr] StartX=135.5 StartY=187 StartZ=0 EndX=125.5 EndY=187 EndZ=0
    g10: Circle CenterX=130.5 CenterY=182.5 CenterZ=0 NormalX=0 NormalY=0 NormalZ=1 AngleXU=0 Radius=1.25
    g11: LineSegment StartX=125.5 StartY=187 StartZ=0 EndX=135 EndY=187 EndZ=0
    g12: LineSegment StartX=135 StartY=187 StartZ=0 EndX=135 EndY=178 EndZ=0
    g13: LineSegment StartX=135 StartY=178 StartZ=0 EndX=125.5 EndY=178 EndZ=0
    g14: LineSegment StartX=104.5 StartY=178 StartZ=0 EndX=104.5 EndY=163 EndZ=0
    g15: LineSegment StartX=104.5 StartY=163 StartZ=0 EndX=114.5 EndY=163 EndZ=0
    g16: LineSegment StartX=114.5 StartY=163 StartZ=0 EndX=114.5 EndY=178 EndZ=0
  constraints (47):
    c: Vertical(g0)
    c: Vertical(g1)
    c: DistanceY(g1) = 187
    c: Horizontal(g2)
    c: Diameter(g3) = 2.5
    c: Coincident(g4,g3)
    c: Symmetric(g2,g2,g4)
    c: DistanceY(g4,g4) = 4.5
    c: Coincident(g2,g1)
    c: Coincident(g2,g0)
    c: Vertical(g4)
    c: Coincident(g5,g1)
    c: Coincident(g5,g0)
    c: Horizontal(g5)
    c: DistanceX(g1) = 104.5
    c: DistanceX(g5,g5) = 10
    c: DistanceY(g0,g0) = 9
    c: Coincident(g6,g7)
    c: Coincident(g7,g8)
    c: Coincident(g8,g9)
    c: Coincident(g9,g6)
    c: Vertical(g6)
    c: Vertical(g8)
    c: Horizontal(g7)
    c: Horizontal(g9)
    c: PointOnObject(g6,g2)
    c: PointOnObject(g0,g7)
    c: Distance(g6,g0) = 11
    c: Symmetric(g6,g7,g10)
    c: Equal(g10,g3)
    c: Equal(g5,g7)
    c: Coincident(g6,g11)
    c: PointOnObject(g11,g9)
    c: Coincident(g11,g12)
    c: PointOnObject(g12,g7)
    c: Vertical(g12)
    c: Coincident(g12,g13)
    c: Coincident(g13,g6)
    c: Distance(g12,g8) = 0.5
    c: Coincident(g1,g14)
    c: Vertical(g14)
    c: Coincident(g14,g15)
    c: Horizontal(g15)
    c: Coincident(g15,g16)
    c: Coincident(g16,g0)
    c: Vertical(g16)
    c: Distance(g15,g2) = 24
FEATURE [PartDesign::Pad] Pad038
  BaseFeature = -> Pad025
  Direction = (0,0,1)
  Length = 20
  Length2 = 10
  Profile = -> Sketch078
  ReferenceAxis = -> Sketch078 [N_Axis]
  Refine = true
  Suppressed = false
  Type = 0
  expr: Length = <<choices>>.base_max_thickness
FEATURE [PartDesign::Pocket] Pocket019
  BaseFeature = -> Pad038
  Direction = (-1,0,0)
  Length = 10
  Length2 = 5
  Midplane = true
  Profile = -> Sketch050
  ReferenceAxis = -> Sketch050 [N_Axis]
  Refine = true
  Suppressed = false
  Type = 0
FEATURE [PartDesign::Pocket] Pocket020
  BaseFeature = -> Pocket019
  Direction = (-1,0,0)
  Length = 62
  Length2 = 5
  Midplane = true
  Profile = -> Sketch051
  ReferenceAxis = -> Sketch051 [N_Axis]
  Refine = true
  Suppressed = false
  Type = 0
FEATURE [PartDesign::Pocket] Pocket021
  BaseFeature = -> Pocket020
  Direction = (-1,0,0)
  Length = 30
  Length2 = 5
  Midplane = true
  Profile = -> Sketch052
  ReferenceAxis = -> Sketch052 [N_Axis]
  Refine = true
  Suppressed = false
  Type = 0
FEATURE [PartDesign::Mirrored] Mirrored001
  BaseFeature = -> Pocket021
  MirrorPlane = -> DatumPlane007
  Originals = -> [Pocket021]
  Refine = true
  Suppressed = false
  TransformMode = 0
FEATURE [PartDesign::Pocket] Pocket025
  BaseFeature = -> Mirrored001
  Direction = (0,0,-1)
  Length = 5
  Length2 = 5
  Profile = -> Sketch054
  ReferenceAxis = -> Sketch054 [N_Axis]
  Refine = true
  Reversed = true
  Suppressed = false
  Type = 0
FEATURE [PartDesign::Pocket] Pocket030
  BaseFeature = -> Pocket025
  Direction = (0,0,-1)
  Length = 18
  Length2 = 5
  Profile = -> Sketch067
  ReferenceAxis = -> Sketch067 [N_Axis]
  Refine = true
  Reversed = true
  Suppressed = false
  Type = 0
FEATURE [Sketcher::SketchObject] Sketch079
  ArcFitTolerance = 1e-06
  AttachmentSupport = -> [XY_Plane039]
  FullyConstrained = false
  MakeInternals = false
  MapMode = 5
  expr: Constraints[18] = <<components>>.m3_insert_r
  sketch-geometry (26):
    g0: LineSegment StartX=496.422 StartY=-278.414 StartZ=0 EndX=496.557 EndY=-289.648 EndZ=0
    g1: LineSegment StartX=577.825 StartY=-280.368 StartZ=0 EndX=584.414 EndY=-280.288 EndZ=0
    g2: LineSegment StartX=584.414 StartY=-280.288 StartZ=0 EndX=584.391 EndY=-278.351 EndZ=0
    g3: LineSegment StartX=583.379 StartY=-277.363 StartZ=0 EndX=496.422 EndY=-278.414 EndZ=0
    g4: ArcOfCircle CenterX=583.391 CenterY=-278.363 CenterZ=0 NormalX=0 NormalY=0 NormalZ=1 AngleXU=0 Radius=1 StartAngle=0.012082 EndAngle=1.58288
    g5: GeomPoint [constr] X=584.378 Y=-277.351 Z=0
    g6: Circle CenterX=561.991 CenterY=-283.107 CenterZ=0 NormalX=0 NormalY=0 NormalZ=1 AngleXU=0 Radius=1.75
    g7: Circle CenterX=540.95 CenterY=-283.354 CenterZ=0 NormalX=0 NormalY=0 NormalZ=1 AngleXU=0 Radius=1.75
    g8: LineSegment [constr] StartX=567.426 StartY=-288.792 StartZ=0 EndX=567.462 EndY=-291.792 EndZ=0
    g9: Circle CenterX=567.462 CenterY=-291.792 CenterZ=0 NormalX=0 NormalY=0 NormalZ=1 AngleXU=0 Radius=2.25
    g10: LineSegment [constr] StartX=567.426 StartY=-288.792 StartZ=0 EndX=567.39 EndY=-285.805 EndZ=0
    g11: LineSegment [constr] StartX=567.39 StartY=-285.805 StartZ=0 EndX=567.366 EndY=-283.805 EndZ=0
    g12: LineSegment [constr] StartX=567.39 StartY=-285.805 StartZ=0 EndX=571.544 EndY=-285.755 EndZ=0
    g13: LineSegment [constr] StartX=577.925 StartY=-288.665 StartZ=0 EndX=577.885 EndY=-285.369 EndZ=0
    g14: LineSegment StartX=577.885 StartY=-285.369 StartZ=0 EndX=577.825 EndY=-280.368 EndZ=0
    g15: LineSegment [constr] StartX=572.498 StartY=-288.731 StartZ=0 EndX=577.925 EndY=-288.665 EndZ=0
    g16: LineSegment StartX=577.885 StartY=-285.369 StartZ=0 EndX=572.498 EndY=-286.538 EndZ=0
    g17: LineSegment StartX=572.498 StartY=-286.538 StartZ=0 EndX=572.498 EndY=-288.731 EndZ=0
    g18: LineSegment StartX=572.498 StartY=-288.731 StartZ=0 EndX=572.615 EndY=-298.391 EndZ=0
    g19: LineSegment StartX=572.615 StartY=-298.391 StartZ=0 EndX=557.218 EndY=-298.577 EndZ=0
    g20: LineSegment [constr] StartX=496.557 StartY=-289.648 StartZ=0 EndX=557.102 EndY=-288.917 EndZ=0
    g21: LineSegment [constr] StartX=557.102 StartY=-288.917 StartZ=0 EndX=572.498 EndY=-288.731 EndZ=0
    g22: LineSegment StartX=496.557 StartY=-289.648 StartZ=0 EndX=496.557 EndY=-295.02 EndZ=0
    g23: LineSegment StartX=496.557 StartY=-295.02 StartZ=0 EndX=557.175 EndY=-295.02 EndZ=0
    g24: LineSegment StartX=557.218 StartY=-298.577 StartZ=0 EndX=557.175 EndY=-295.02 EndZ=0
    g25: LineSegment [constr] StartX=557.175 StartY=-295.02 StartZ=0 EndX=557.102 EndY=-288.917 EndZ=0
  constraints (61):
    c: Coincident(g0,g20)
    c: Coincident(g15,g13)
    c: Coincident(g14,g1)
    c: Coincident(g1,g2)
    c: Coincident(g3,g0)
    c: Perpendicular(g3,g0)
    c: PointOnObject(g5,g2)
    c: PointOnObject(g5,g3)
    c: Tangent(g2,g4) = -1.5708
    c: Tangent(g3,g4) = -1.5708
    c: Radius(g4) = 1
    c: Perpendicular(g1,g2)
    c: Perpendicular(g2,g3)
    c: Diameter(g6) = 3.5
    c: Diameter(g7) = 3.5
    c: DistanceX(g15) = 577.925
    c: DistanceY(g15) = -288.665
    c: Coincident(g9,g8)
    c: Diameter(g9) = 4.5
    c: Coincident(g10,g8)
    c: Coincident(g10,g11)
    c: Parallel(g10,g8)
    c: Parallel(g11,g8)
    c: Coincident(g12,g10)
    c: Perpendicular(g10,g12)
    c: Distance(g11) = 2
    c: Distance(g8) = 3
    c: Coincident(g13,g14)
    c: Perpendicular(g13,g1)
    c: Perpendicular(g14,g1)
    c: Distance(g8,g13) = 10.5
    c: Coincident(g21,g15)
    c: Perpendicular(g0,g15)
    c: Coincident(g13,g16)
    c: Coincident(g16,g17)
    c: Coincident(g17,g21)
    c: Vertical(g17)
    c: Coincident(g17,g18)
    c: Coincident(g18,g19)
    c: Coincident(g19,g24)
    c: Coincident(g20,g21)
    c: Perpendicular(g0,g20)
    c: Perpendicular(g0,g21)
    c: PointOnObject(g8,g20)
    c: Perpendicular(g20,g8)
    c: Coincident(g20,g25)
    c: DistanceX(g0) = 496.422
    c: DistanceY(g0) = -278.414
    c: Perpendicular(g18,g15)
    c: Perpendicular(g18,g19)
    c: Coincident(g0,g22)
    c: Vertical(g22)
    c: Coincident(g22,g23)
    c: Horizontal(g23)
    c: Coincident(g24,g25)
    c: Perpendicular(g24,g20)
    c: Perpendicular(g25,g20)
    c: Coincident(g24,g23)
    c: DistanceX(g0) = 496.557
    c: DistanceX(g19) = 557.218
    c: DistanceY(g19) = -298.577
FEATURE [PartDesign::Pad] Pad039
  Direction = (0,0,1)
  Length = 3
  Length2 = 10
  Profile = -> Sketch079
  ReferenceAxis = -> Sketch079 [N_Axis]
  Refine = true
  Suppressed = false
  Type = 0
FEATURE [Sketcher::SketchObject] Sketch080
  ArcFitTolerance = 1e-06
  AttachmentSupport = -> [XY_Plane039]
  FullyConstrained = false
  MakeInternals = false
  MapMode = 5
  expr: Constraints[1] = <<components>>.m3_insert_r
  expr: Constraints[2] = <<components>>.m3_insert_r + 4
  sketch-geometry (5):
    g0: Circle CenterX=567.5 CenterY=-291.8 CenterZ=0 NormalX=0 NormalY=0 NormalZ=1 AngleXU=0 Radius=2.25
    g1: Circle CenterX=567.5 CenterY=-291.8 CenterZ=0 NormalX=0 NormalY=0 NormalZ=1 AngleXU=0 Radius=4.25
    g2: Circle CenterX=513.5 CenterY=-291.8 CenterZ=0 NormalX=0 NormalY=0 NormalZ=1 AngleXU=0 Radius=2.25
    g3: Circle CenterX=513.5 CenterY=-291.8 CenterZ=0 NormalX=0 NormalY=0 NormalZ=1 AngleXU=0 Radius=4.25
    g4: LineSegment [constr] StartX=567.5 StartY=-291.8 StartZ=0 EndX=486.353 EndY=-291.8 EndZ=0
  constraints (12):
    c: Coincident(g1,g0)
    c: Diameter(g0) = 4.5
    c: Diameter(g1) = 8.5
    c: DistanceX(g0) = 567.5
    c: DistanceY(g0) = -291.8
    c: Coincident(g3,g2)
    c: Equal(g2,g0)
    c: Equal(g3,g1)
    c: Distance(g0,g2) = 54
    c: Coincident(g4,g0)
    c: Horizontal(g4)
    c: PointOnObject(g2,g4)
FEATURE [PartDesign::Pad] Pad040
  BaseFeature = -> Pad039
  Direction = (0,0,1)
  Length = 18
  Length2 = 10
  Profile = -> Sketch080
  ReferenceAxis = -> Sketch080 [N_Axis]
  Refine = true
  Suppressed = false
  Type = 0
FEATURE [Sketcher::SketchObject] Sketch081
  ArcFitTolerance = 1e-06
  AttachmentSupport = -> [XY_Plane039]
  FullyConstrained = false
  MakeInternals = false
  MapMode = 5
  sketch-geometry (15):
    g0: LineSegment StartX=584.414 StartY=-280.301 StartZ=0 EndX=584.394 EndY=-278.452 EndZ=0
    g1: LineSegment StartX=583.383 StartY=-277.463 StartZ=0 EndX=496.422 EndY=-278.414 EndZ=0
    g2: ArcOfCircle CenterX=583.394 CenterY=-278.463 CenterZ=0 NormalX=0 NormalY=0 NormalZ=1 AngleXU=0 Radius=1 StartAngle=0.0109358 EndAngle=1.58173
    g3: GeomPoint [constr] X=584.383 Y=-277.452 Z=0
    g4: LineSegment StartX=496.422 StartY=-278.414 StartZ=0 EndX=496.465 EndY=-281.514 EndZ=0
    g5: LineSegment [constr] StartX=496.465 StartY=-281.514 StartZ=0 EndX=500.406 EndY=-281.46 EndZ=0
    g6: LineSegment StartX=496.465 StartY=-281.514 StartZ=0 EndX=492.964 EndY=-281.563 EndZ=0
    g7: LineSegment StartX=492.964 StartY=-281.563 StartZ=0 EndX=493.008 EndY=-284.801 EndZ=0
    g8: LineSegment StartX=493.008 StartY=-284.801 StartZ=0 EndX=500.451 EndY=-284.698 EndZ=0
    g9: LineSegment StartX=500.451 StartY=-284.698 StartZ=0 EndX=500.406 EndY=-281.46 EndZ=0
    g10: LineSegment StartX=500.406 StartY=-281.46 StartZ=0 EndX=518.146 EndY=-281.215 EndZ=0
    g11: LineSegment StartX=518.146 StartY=-281.215 StartZ=0 EndX=537.146 EndY=-280.953 EndZ=0
    g12: LineSegment StartX=537.146 StartY=-280.953 StartZ=0 EndX=544.404 EndY=-280.853 EndZ=0
    g13: LineSegment StartX=544.404 StartY=-280.853 StartZ=0 EndX=556.056 EndY=-280.692 EndZ=0
    g14: LineSegment StartX=556.056 StartY=-280.692 StartZ=0 EndX=584.414 EndY=-280.301 EndZ=0
  constraints (37):
    c: PointOnObject(g3,g0)
    c: PointOnObject(g3,g1)
    c: Tangent(g0,g2) = -1.5708
    c: Tangent(g1,g2) = -1.5708
    c: Radius(g2) = 1
    c: Perpendicular(g0,g1)
    c: DistanceX(g1) = 496.422
    c: DistanceY(g1) = -278.414
    c: DistanceX(g0) = 584.414
    c: DistanceY(g0) = -280.301
    c: Coincident(g1,g4)
    c: Coincident(g4,g5)
    c: Coincident(g5,g10)
    c: Coincident(g4,g6)
    c: Coincident(g6,g7)
    c: Coincident(g7,g8)
    c: Coincident(g8,g9)
    c: Coincident(g9,g5)
    c: Perpendicular(g8,g9)
    c: Perpendicular(g8,g7)
    c: Perpendicular(g6,g7)
    c: Perpendicular(g4,g6)
    c: DistanceX(g8) = 500.451
    c: DistanceY(g8) = -284.698
    c: Coincident(g14,g0)
    c: Coincident(g10,g11)
    c: Perpendicular(g10,g9)
    c: Parallel(g5,g10)
    c: Coincident(g11,g12)
    c: Perpendicular(g11,g9)
    c: Coincident(g12,g13)
    c: Perpendicular(g12,g9)
    c: Coincident(g13,g14)
    c: Perpendicular(g13,g9)
    c: Perpendicular(g14,g9)
    c: DistanceY(g5) = -281.46
    c: DistanceX(g11,g11) = 19
FEATURE [PartDesign::Pad] Pad041
  BaseFeature = -> Pad040
  Direction = (0,0,1)
  Length = 38
  Length2 = 10
  Profile = -> Sketch081
  ReferenceAxis = -> Sketch081 [N_Axis]
  Refine = true
  Suppressed = false
  Type = 0
  expr: Length = <<choices>>.exit_height + 3 - <<choices>>.base_max_thickness
FEATURE [PartDesign::Plane] DatumPlane020
  AttachmentOffset = pos=(0,0,3) rot=(0,0,1;0rad)
  AttachmentSupport = -> [XY_Plane039]
  Length = 698.227
  MapMode = 5
  Placement = pos=(0,0,3) rot=(0,0,1;0rad)
  ResizeMode = 0
  Width = 412.39
FEATURE [Sketcher::SketchObject] Sketch082
  ArcFitTolerance = 1e-06
  AttachmentSupport = -> [DatumPlane020]
  FullyConstrained = false
  MakeInternals = false
  MapMode = 5
  Placement = pos=(0,0,3) rot=(0,0,1;0rad)
  sketch-geometry (2):
    g0: Circle CenterX=562.014 CenterY=-283.062 CenterZ=0 NormalX=0 NormalY=0 NormalZ=1 AngleXU=0 Radius=3
    g1: Circle CenterX=540.918 CenterY=-283.394 CenterZ=0 NormalX=0 NormalY=0 NormalZ=1 AngleXU=0 Radius=3
  constraints (2):
    c: Diameter(g0) = 6
    c: Equal(g0,g1)
FEATURE [Sketcher::SketchObject] Sketch084
  ArcFitTolerance = 1e-06
  AttachmentSupport = -> [XY_Plane039]
  FullyConstrained = false
  MakeInternals = false
  MapMode = 5
  sketch-geometry (4):
    g0: LineSegment StartX=567.72 StartY=-289.014 StartZ=0 EndX=571.009 EndY=-289.014 EndZ=0
    g1: LineSegment StartX=571.009 StartY=-289.014 StartZ=0 EndX=571.009 EndY=-279.004 EndZ=0
    g2: LineSegment StartX=571.009 StartY=-279.004 StartZ=0 EndX=567.72 EndY=-279.004 EndZ=0
    g3: LineSegment StartX=567.72 StartY=-279.004 StartZ=0 EndX=567.72 EndY=-289.014 EndZ=0
  constraints (8):
    c: Coincident(g0,g1)
    c: Coincident(g1,g2)
    c: Coincident(g2,g3)
    c: Coincident(g3,g0)
    c: Horizontal(g0)
    c: Horizontal(g2)
    c: Vertical(g1)
    c: Vertical(g3)
FEATURE [App::Link] GPU_bracket  label="GPU_bracket001"
  LinkPlacement = pos=(541.006,-283.358,4.70402) rot=(0.18755,0.24333,-0.951638;0.00507rad)
  LinkedObject = -> Part018
  Placement = pos=(541.006,-283.358,4.70402) rot=(0.18755,0.24333,-0.951638;0.00507rad)
FEATURE [App::FeaturePython] Joint014  label="Fixed011"  # Assembly joint (typed FeaturePython)
  Activated = true
  AngleMax = 0
  AngleMin = 0
  Detach1 = false
  Detach2 = false
  Distance = 0
  Distance2 = 0
  EnableAngleMax = false
  EnableAngleMin = false
  EnableLengthMax = false
  EnableLengthMin = false
  JointType = 0 (Fixed)
  LengthMax = 0
  LengthMin = 0
  Offset2 = pos=(0,0,0) rot=(0,0,-1;0.017453rad)
  Placement2 = pos=(109.5,182.5,20) rot=(0,0,-1;0.017453rad)
  Reference1 = -> Assembly [GPU_bracket.Body018.?Edge71,GPU_bracket.Body018.?Edge71]
  Reference2 = -> Assembly [BASE.Body006.Edge1061,BASE.Body006.Edge1061]
FEATURE [Sketcher::SketchObject] Sketch085
  ArcFitTolerance = 1e-06
  AttachmentSupport = -> [XY_Plane041]
  FullyConstrained = false
  MakeInternals = false
  MapMode = 5
  expr: Constraints[18] = <<components>>.m3_hole
  expr: Constraints[9] = <<components>>.frame_w - 2 * 65
  sketch-geometry (10):
    g0: LineSegment StartX=65 StartY=-236.705 StartZ=0 EndX=65 EndY=-250.705 EndZ=0
    g1: LineSegment StartX=65 StartY=-250.705 StartZ=0 EndX=310 EndY=-250.705 EndZ=0
    g2: LineSegment StartX=310 StartY=-250.705 StartZ=0 EndX=310 EndY=-236.705 EndZ=0
    g3: LineSegment StartX=310 StartY=-236.705 StartZ=0 EndX=65 EndY=-236.705 EndZ=0
    g4: LineSegment [constr] StartX=65 StartY=-243.705 StartZ=0 EndX=310 EndY=-243.705 EndZ=0
    g5: GeomPoint X=187.5 Y=-243.705 Z=0
    g6: Circle CenterX=162.5 CenterY=-243.705 CenterZ=0 NormalX=0 NormalY=0 NormalZ=1 AngleXU=0 Radius=1.75
    g7: Circle CenterX=90 CenterY=-243.705 CenterZ=0 NormalX=0 NormalY=0 NormalZ=1 AngleXU=0 Radius=1.75
    g8: Circle CenterX=212.5 CenterY=-243.705 CenterZ=0 NormalX=0 NormalY=0 NormalZ=1 AngleXU=0 Radius=1.75
    g9: Circle CenterX=285 CenterY=-243.705 CenterZ=0 NormalX=0 NormalY=0 NormalZ=1 AngleXU=0 Radius=1.75
  constraints (25):
    c: Coincident(g0,g1)
    c: Coincident(g1,g2)
    c: Coincident(g2,g3)
    c: Coincident(g3,g0)
    c: Vertical(g0)
    c: Vertical(g2)
    c: Horizontal(g1)
    c: Horizontal(g3)
    c: DistanceX(g0) = 65
    c: DistanceX(g3,g3) = 245
    c: PointOnObject(g4,g0)
    c: Horizontal(g4)
    c: Symmetric(g4,g4,g5)
    c: PointOnObject(g6,g4)
    c: PointOnObject(g7,g4)
    c: Equal(g7,g6)
    c: Equal(g6,g8)
    c: Equal(g8,g9)
    c: Diameter(g7) = 3.5
    c: DistanceY(g2,g2) = 14
    c: Symmetric(g2,g2,g4)
    c: DistanceX(g7) = 90
    c: Symmetric(g7,g9,g5)
    c: Symmetric(g8,g6,g5)
    c: Distance(g6,g8) = 50
FEATURE [PartDesign::Pad] Pad043
  Direction = (0,0,1)
  Length = 7
  Length2 = 10
  Profile = -> Sketch085
  ReferenceAxis = -> Sketch085 [N_Axis]
  Refine = true
  Suppressed = false
  Type = 0
FEATURE [PartDesign::Chamfer] Chamfer010
  Angle = 45
  Base = -> Pad043 [Edge23,Edge14,Edge17,Edge20]
  BaseFeature = -> Pad043
  ChamferType = 0
  FlipDirection = false
  Refine = true
  Size = 2
  Size2 = 1
  SupportTransform = false
  Suppressed = false
  UseAllEdges = false
FEATURE [App::Link] top_back_cover001  label="top back cover001"
  LinkPlacement = pos=(453.219,-20.274,39.5631) rot=(0.075569,0.096295,0.99248;0.012724rad)
  LinkedObject = -> Part019
  Placement = pos=(453.219,-20.274,39.5631) rot=(0.075569,0.096295,0.99248;0.012724rad)
FEATURE [App::Link] top_back_cover002  label="Unnamed"
FEATURE [App::FeaturePython] Joint015  label="Fixed012"  # Assembly joint (typed FeaturePython)
  Activated = true
  AngleMax = 0
  AngleMin = 0
  Detach1 = false
  Detach2 = false
  Distance = 0
  Distance2 = 0
  EnableAngleMax = false
  EnableAngleMin = false
  EnableLengthMax = false
  EnableLengthMin = false
  JointType = 0 (Fixed)
  LengthMax = 0
  LengthMin = 0
  Placement1 = pos=(65,-250.705,3.5) rot=(0,0,1;0rad)
  Placement2 = pos=(90,196,-10) rot=(0,0,1;0rad)
  Reference1 = -> Assembly [top_back_cover001.Body019.Edge21,top_back_cover001.Body019.Edge21]
  Reference2 = -> Assembly [FRAME.Body003.Edge41,FRAME.Body003.Edge41]
FEATURE [Sketcher::SketchObject] Sketch086
  ArcFitTolerance = 1e-06
  AttachmentSupport = -> [XY_Plane041]
  FullyConstrained = false
  MakeInternals = false
  MapMode = 5
  sketch-geometry (4):
    g0: LineSegment StartX=309.981 StartY=-253.638 StartZ=0 EndX=309.981 EndY=-250.638 EndZ=0
    g1: LineSegment StartX=309.981 StartY=-250.638 StartZ=0 EndX=154.072 EndY=-250.638 EndZ=0
    g2: LineSegment StartX=154.072 StartY=-250.638 StartZ=0 EndX=154.072 EndY=-253.638 EndZ=0
    g3: LineSegment StartX=154.072 StartY=-253.638 StartZ=0 EndX=309.981 EndY=-253.638 EndZ=0
  constraints (9):
    c: Coincident(g0,g1)
    c: Coincident(g1,g2)
    c: Coincident(g2,g3)
    c: Coincident(g3,g0)
    c: Vertical(g0)
    c: Vertical(g2)
    c: Horizontal(g1)
    c: Horizontal(g3)
    c: DistanceY(g2,g2) = 3
FEATURE [PartDesign::Pad] Pad044
  BaseFeature = -> Chamfer010
  Direction = (0,0,1)
  Length = 7
  Length2 = 10
  Profile = -> Sketch086
  ReferenceAxis = -> Sketch086 [N_Axis]
  Refine = true
  Suppressed = false
  Type = 0
FEATURE [App::Link] LEG_CLAMP  label="LEG_CLAMP001"
  LinkPlacement = pos=(-0.353101,-5.44651,-14.3643) rot=(0.075569,0.096295,0.99248;0.012724rad)
  LinkedObject = -> Part013
  Placement = pos=(-0.353101,-5.44651,-14.3643) rot=(0.075569,0.096295,0.99248;0.012724rad)
FEATURE [App::FeaturePython] Joint016  label="Fixed013"  # Assembly joint (typed FeaturePython)
  Activated = true
  AngleMax = 0
  AngleMin = 0
  Detach1 = false
  Detach2 = false
  Distance = 0
  Distance2 = 0
  EnableAngleMax = false
  EnableAngleMin = false
  EnableLengthMax = false
  EnableLengthMin = false
  JointType = 0 (Fixed)
  LengthMax = 0
  LengthMin = 0
  Placement1 = pos=(537.782,-284.707,5) rot=(0,0,1;0rad)
  Placement2 = pos=(109.5,182.5,5) rot=(1,0,0;3.14159rad)
  Reference1 = -> Assembly [LEG_CLAMP.Body013.Edge39,LEG_CLAMP.Body013.Edge39]
  Reference2 = -> Assembly [BASE.Body006.Edge534,BASE.Body006.Edge534]
FEATURE [Sketcher::SketchObject] Sketch087
  ArcFitTolerance = 1e-06
  AttachmentSupport = -> [XY_Plane037]
  FullyConstrained = true
  MakeInternals = false
  MapMode = 5
  expr: Constraints[2] = 245 / 2
  sketch-geometry (1):
    g0: Circle CenterX=122.5 CenterY=2 CenterZ=0 NormalX=0 NormalY=0 NormalZ=1 AngleXU=0 Radius=1.75
  constraints (3):
    c: Diameter(g0) = 3.5
    c: DistanceY(g0) = 2
    c: DistanceX(g0) = 122.5
FEATURE [PartDesign::Pocket] Pocket037
  BaseFeature = -> Pad036
  Direction = (0,0,-1)
  Length = 5
  Length2 = 5
  Midplane = true
  Placement = pos=(0,0,0) rot=(1,0,0;1.5708rad)
  Profile = -> Sketch087
  ReferenceAxis = -> Sketch087 [N_Axis]
  Refine = true
  Suppressed = false
  Type = 1
FEATURE [PartDesign::Body] Body017
  AllowCompound = false
  Group = -> [Sketch074,Pad035,Sketch075,Pad036,Sketch087,Pocket037]
  Origin = -> Origin037
  Tip = -> Pocket037
FEATURE [App::Part] Part017  label="FRONT_VENT"
  Group = -> [Body017]
  Origin = -> Origin036
FEATURE [App::Link] FAN_SHROUD  label="FAN_SHROUD001"
  LinkPlacement = pos=(433.796,-467.208,-13.8394) rot=(0.075569,0.096295,0.99248;0.012724rad)
  LinkedObject = -> Part014
  Placement = pos=(433.796,-467.208,-13.8394) rot=(0.075569,0.096295,0.99248;0.012724rad)
FEATURE [Sketcher::SketchObject] Sketch088
  ArcFitTolerance = 1e-06
  AttachmentSupport = -> [DatumPlane009]
  FullyConstrained = false
  MakeInternals = false
  MapMode = 5
  Placement = pos=(0,0,20) rot=(0,0,1;0rad)
  sketch-geometry (4):
    g0: LineSegment StartX=59.1897 StartY=34.0906 StartZ=0 EndX=59.1897 EndY=18.1571 EndZ=0
    g1: LineSegment StartX=59.1897 StartY=18.1571 StartZ=0 EndX=117.928 EndY=18.1571 EndZ=0
    g2: LineSegment StartX=117.928 StartY=18.1571 StartZ=0 EndX=117.928 EndY=34.0906 EndZ=0
    g3: LineSegment StartX=117.928 StartY=34.0906 StartZ=0 EndX=59.1897 EndY=34.0906 EndZ=0
  constraints (8):
    c: Coincident(g0,g1)
    c: Coincident(g1,g2)
    c: Coincident(g2,g3)
    c: Coincident(g3,g0)
    c: Vertical(g0)
    c: Vertical(g2)
    c: Horizontal(g1)
    c: Horizontal(g3)
FEATURE [PartDesign::Pad] Pad045
  BaseFeature = -> Pocket030
  Direction = (0,0,1)
  Length = 2
  Length2 = 10
  Profile = -> Sketch088
  ReferenceAxis = -> Sketch088 [N_Axis]
  Refine = true
  Reversed = true
  Suppressed = false
  Type = 0
FEATURE [PartDesign::Body] Body006
  AllowCompound = false
  Group = -> [Sketch014,Pad011,Sketch016,Pad013,Sketch017,Pad014,Sketch018,Pocket004,Sketch019,Pocket005,Sketch020,Pocket006,Pocket007,Sketch021,LinearPattern,DatumPlane001,Sketch035,Pad020,Sketch045,Pad024,Sketch046,Pocket012,Chamfer001,Fillet001,Pocket022,Pocket023,Sketch054,Sketch048,Pad025,Sketch049,DatumPlane007,Sketch050,Pad038,Pocket019,Sketch051,Pocket020,DatumPlane008,Sketch052,Pocket021,Mirrored001,+8 more]
  Origin = -> Origin013
  Tip = -> Pad045
FEATURE [App::Part] Part006  label="BASE"
  Group = -> [Body006]
  Origin = -> Origin012
FEATURE [PartDesign::Pocket] Pocket038
  BaseFeature = -> Mirrored
  Direction = (-1,0,0)
  Length = 5
  Length2 = 5
  Profile = -> Sketch028
  ReferenceAxis = -> Sketch028 [N_Axis]
  Refine = true
  Suppressed = false
  Type = 1
FEATURE [Sketcher::SketchObject] Sketch089
  ArcFitTolerance = 1e-06
  AttachmentSupport = -> [YZ_Plane015]
  FullyConstrained = true
  MakeInternals = false
  MapMode = 5
  Placement = pos=(0,0,0) rot=(0.57735,0.57735,0.57735;2.0944rad)
  sketch-geometry (8):
    g0: LineSegment StartX=229.5 StartY=19 StartZ=0 EndX=229.5 EndY=21.3 EndZ=0
    g1: LineSegment StartX=226.8 StartY=24 StartZ=0 EndX=226.2 EndY=24 EndZ=0
    g2: LineSegment StartX=223.5 StartY=21.3 StartZ=0 EndX=223.5 EndY=19 EndZ=0
    g3: LineSegment StartX=223.5 StartY=19 StartZ=0 EndX=229.5 EndY=19 EndZ=0
    g4: ArcOfCircle CenterX=226.8 CenterY=21.3 CenterZ=0 NormalX=0 NormalY=0 NormalZ=1 AngleXU=0 Radius=2.7 StartAngle=0 EndAngle=1.5708
    g5: GeomPoint [constr] X=229.5 Y=24 Z=0
    g6: ArcOfCircle CenterX=226.2 CenterY=21.3 CenterZ=0 NormalX=0 NormalY=0 NormalZ=1 AngleXU=0 Radius=2.7 StartAngle=1.5708 EndAngle=3.14159
    g7: GeomPoint [constr] X=223.5 Y=24 Z=0
  constraints (20):
    c: Coincident(g2,g3)
    c: Coincident(g3,g0)
    c: Vertical(g0)
    c: Vertical(g2)
    c: Horizontal(g1)
    c: Horizontal(g3)
    c: DistanceX(g0) = 229.5
    c: DistanceY(g0) = 19
    c: PointOnObject(g5,g0)
    c: PointOnObject(g5,g1)
    c: Tangent(g0,g4) = -1.5708
    c: Tangent(g1,g4) = -1.5708
    c: PointOnObject(g7,g1)
    c: PointOnObject(g7,g2)
    c: Tangent(g1,g6) = -1.5708
    c: Tangent(g2,g6) = -1.5708
    c: Equal(g4,g6)
    c: DistanceY(g1) = 24
    c: DistanceY(g0) = 21.3
    c: DistanceX(g3,g3) = 6
FEATURE [PartDesign::Pad] Pad046
  BaseFeature = -> Pocket038
  Direction = (1,0,0)
  Length = 30
  Length2 = 10
  Midplane = true
  Profile = -> Sketch089
  ReferenceAxis = -> Sketch089 [N_Axis]
  Refine = true
  Suppressed = false
  TaperAngle = -9
  Type = 0
FEATURE [Sketcher::SketchObject] Sketch090
  ArcFitTolerance = 1e-06
  AttachmentSupport = -> [DatumPlane003]
  FullyConstrained = false
  MakeInternals = false
  MapMode = 5
  Placement = pos=(-25,0,0) rot=(0.57735,0.57735,0.57735;2.0944rad)
  expr: Constraints[6] = <<components>>.frame_h
  sketch-geometry (8):
    g0: LineSegment StartX=229.5 StartY=31.8586 StartZ=0 EndX=223.5 EndY=31.8586 EndZ=0
    g1: LineSegment StartX=223.5 StartY=31.8586 StartZ=0 EndX=223.5 EndY=28.7 EndZ=0
    g2: LineSegment StartX=226.2 StartY=26 StartZ=0 EndX=226.8 EndY=26 EndZ=0
    g3: LineSegment StartX=229.5 StartY=28.7 StartZ=0 EndX=229.5 EndY=31.8586 EndZ=0
    g4: ArcOfCircle CenterX=226.8 CenterY=28.7 CenterZ=0 NormalX=0 NormalY=0 NormalZ=1 AngleXU=0 Radius=2.7 StartAngle=4.71239 EndAngle=6.28319
    g5: GeomPoint [constr] X=229.5 Y=26 Z=0
    g6: ArcOfCircle CenterX=226.2 CenterY=28.7 CenterZ=0 NormalX=0 NormalY=0 NormalZ=1 AngleXU=0 Radius=2.7 StartAngle=3.14159 EndAngle=4.71239
    g7: GeomPoint [constr] X=223.5 Y=26 Z=0
  constraints (19):
    c: Coincident(g0,g1)
    c: Coincident(g3,g0)
    c: Horizontal(g0)
    c: Horizontal(g2)
    c: Vertical(g1)
    c: Vertical(g3)
    c: DistanceX(g0) = 229.5
    c: DistanceY(g5) = 26
    c: PointOnObject(g5,g2)
    c: PointOnObject(g5,g3)
    c: Tangent(g2,g4) = -1.5708
    c: Tangent(g3,g4) = -1.5708
    c: PointOnObject(g7,g1)
    c: PointOnObject(g7,g2)
    c: Tangent(g1,g6) = -1.5708
    c: Tangent(g2,g6) = -1.5708
    c: Equal(g6,g4)
    c: DistanceY(g3) = 28.7
    c: DistanceX(g0,g0) = 6
FEATURE [PartDesign::Pad] Pad047
  BaseFeature = -> Pad046
  Direction = (1,0,0)
  Length = 30
  Length2 = 10
  Midplane = true
  Profile = -> Sketch090
  ReferenceAxis = -> Sketch090 [N_Axis]
  Refine = true
  Suppressed = false
  TaperAngle = -9
  Type = 0
FEATURE [PartDesign::LinearPattern] LinearPattern002
  BaseFeature = -> Pad047
  Direction = -> Sketch090 [V_Axis]
  Length = 15
  Mode = 0
  Occurrences = 2
  Offset = 15
  Originals = -> [Pad047,Pad046]
  Refine = true
  Suppressed = false
  TransformMode = 0
FEATURE [PartDesign::Pad] Pad048
  BaseFeature = -> LinearPattern002
  Direction = (1,0,0)
  Length = 4
  Length2 = 10
  Profile = -> Sketch024
  ReferenceAxis = -> Sketch024 [N_Axis]
  Refine = true
  Reversed = true
  Suppressed = false
  Type = 0
FEATURE [PartDesign::Pocket] Pocket039
  BaseFeature = -> Pad048
  Direction = (0,0,-1)
  Length = 8
  Length2 = 5
  Profile = -> Sketch044 [Edge6]
  ReferenceAxis = -> Sketch044 [N_Axis]
  Refine = true
  Reversed = true
  Suppressed = false
  Type = 0
FEATURE [App::FeaturePython] Joint018  label="Fixed015"  # Assembly joint (typed FeaturePython)
  Activated = true
  AngleMax = 0
  AngleMin = 0
  Detach1 = false
  Detach2 = false
  Distance = 0
  Distance2 = 0
  EnableAngleMax = false
  EnableAngleMin = false
  EnableLengthMax = false
  EnableLengthMin = false
  JointType = 0 (Fixed)
  LengthMax = 0
  LengthMin = 0
  Placement1 = pos=(14,8,0) rot=(0,0,1;0rad)
  Placement2 = pos=(370,8,3) rot=(0,0,1;0rad)
  Reference1 = -> Assembly [EXIT_DUCT.Body007.Edge202,EXIT_DUCT.Body007.Edge202]
  Reference2 = -> Assembly [BASE.Body006.Edge445,BASE.Body006.Edge445]
FEATURE [App::FeaturePython] Joint019  label="Fixed016"  # Assembly joint (typed FeaturePython)
  Activated = true
  AngleMax = 0
  AngleMin = 0
  Detach1 = false
  Detach2 = false
  Distance = 0
  Distance2 = 0
  EnableAngleMax = false
  EnableAngleMin = false
  EnableLengthMax = false
  EnableLengthMin = false
  JointType = 0 (Fixed)
  LengthMax = 0
  LengthMin = 0
  Placement1 = pos=(370,8,-10) rot=(0,0,1;0rad)
  Placement2 = pos=(14,8,55) rot=(0,0,1;0rad)
  Reference1 = -> Assembly [FRAME.Body003.Edge39,FRAME.Body003.Edge39]
  Reference2 = -> Assembly [EXIT_DUCT.Body007.Edge226,EXIT_DUCT.Body007.Edge226]
FEATURE [Sketcher::SketchObject] Sketch091
  ArcFitTolerance = 1e-06
  AttachmentSupport = -> [DatumPlane006]
  FullyConstrained = false
  MakeInternals = false
  MapMode = 5
  Placement = pos=(0,0,27.5) rot=(0,0,1;0rad)
  sketch-geometry (6):
    g0: LineSegment StartX=-40.5 StartY=2.95 StartZ=0 EndX=-40.5 EndY=5.35 EndZ=0
    g1: LineSegment StartX=-40.5 StartY=5.35 StartZ=0 EndX=-45.9293 EndY=5.35 EndZ=0
    g2: LineSegment StartX=-45.9293 StartY=5.35 StartZ=0 EndX=-45.9293 EndY=7.35 EndZ=0
    g3: LineSegment StartX=-45.9293 StartY=7.35 StartZ=0 EndX=-38.0085 EndY=7.35 EndZ=0
    g4: LineSegment StartX=-38.0085 StartY=7.35 StartZ=0 EndX=-18.6319 EndY=2.95 EndZ=0
    g5: LineSegment StartX=-18.6319 StartY=2.95 StartZ=0 EndX=-40.5 EndY=2.95 EndZ=0
  constraints (15):
    c: Vertical(g0)
    c: Coincident(g0,g1)
    c: Horizontal(g1)
    c: Coincident(g1,g2)
    c: Vertical(g2)
    c: Coincident(g2,g3)
    c: Horizontal(g3)
    c: Coincident(g3,g4)
    c: Coincident(g4,g5)
    c: Coincident(g5,g0)
    c: Horizontal(g5)
    c: DistanceY(g0) = 2.95
    c: DistanceY(g0,g0) = 2.4
    c: DistanceY(g2,g2) = 2
    c: DistanceX(g0) = -40.5
FEATURE [PartDesign::Pad] Pad049
  BaseFeature = -> Pocket039
  Direction = (0,0,1)
  Length = 25
  Length2 = 10
  Profile = -> Sketch091
  ReferenceAxis = -> Sketch091 [N_Axis]
  Refine = true
  Suppressed = false
  Type = 0
FEATURE [Sketcher::SketchObject] Sketch092
  ArcFitTolerance = 1e-06
  AttachmentSupport = -> [DatumPlane015]
  FullyConstrained = false
  MakeInternals = false
  MapMode = 5
  Placement = pos=(0,0,20) rot=(0,0,1;0rad)
  sketch-geometry (6):
    g0: LineSegment StartX=59.5 StartY=2.95 StartZ=0 EndX=59.5 EndY=5.35 EndZ=0
    g1: LineSegment StartX=59.5 StartY=5.35 StartZ=0 EndX=64.5503 EndY=5.35 EndZ=0
    g2: LineSegment StartX=64.5503 StartY=5.35 StartZ=0 EndX=64.5503 EndY=7.35 EndZ=0
    g3: LineSegment StartX=64.5503 StartY=7.35 StartZ=0 EndX=57.1811 EndY=7.35 EndZ=0
    g4: LineSegment StartX=57.1811 StartY=7.35 StartZ=0 EndX=43.3859 EndY=2.95 EndZ=0
    g5: LineSegment StartX=43.3859 StartY=2.95 StartZ=0 EndX=59.5 EndY=2.95 EndZ=0
  constraints (15):
    c: Vertical(g0)
    c: Coincident(g0,g1)
    c: Horizontal(g1)
    c: Coincident(g1,g2)
    c: Vertical(g2)
    c: Coincident(g2,g3)
    c: Horizontal(g3)
    c: Coincident(g3,g4)
    c: Coincident(g4,g5)
    c: Coincident(g5,g0)
    c: Horizontal(g5)
    c: DistanceY(g0) = 2.95
    c: DistanceX(g0) = 59.5
    c: DistanceY(g0,g0) = 2.4
    c: DistanceY(g2,g2) = 2
FEATURE [PartDesign::Pad] Pad050
  BaseFeature = -> Chamfer007
  Direction = (0,0,1)
  Length = 30
  Length2 = 10
  Placement = pos=(0,0,20) rot=(0,0,1;0rad)
  Profile = -> Sketch092
  ReferenceAxis = -> Sketch092 [N_Axis]
  Refine = true
  Suppressed = false
  Type = 0
FEATURE [PartDesign::Body] Body016
  AllowCompound = false
  Group = -> [DatumPlane015,Sketch068,Pad032,Sketch069,Pad033,Pad034,Sketch070,Pocket031,DatumPlane017,DatumPlane018,Sketch072,Pocket033,Sketch073,Pocket034,Chamfer007,Sketch092,Pad050]
  Origin = -> Origin035
  Tip = -> Pad050
FEATURE [App::Part] Part016  label="LEFT_END"
  Group = -> [Body016]
  Origin = -> Origin034
FEATURE [App::FeaturePython] Joint020  label="Fixed017"  # Assembly joint (typed FeaturePython)
  Activated = true
  AngleMax = 0
  AngleMin = 0
  Detach1 = false
  Detach2 = false
  Distance = 0
  Distance2 = 0
  EnableAngleMax = false
  EnableAngleMin = false
  EnableLengthMax = false
  EnableLengthMin = false
  JointType = 0 (Fixed)
  LengthMax = 0
  LengthMin = 0
  Placement1 = pos=(5,8,20) rot=(0,0,1;0rad)
  Placement2 = pos=(5,8,20) rot=(0,0,1;0rad)
  Reference1 = -> Assembly [LEFT_END.Body016.Edge137,LEFT_END.Body016.Edge137]
  Reference2 = -> Assembly [BASE.Body006.Edge1040,BASE.Body006.Edge1040]
FEATURE [App::FeaturePython] Joint021  label="Fixed018"  # Assembly joint (typed FeaturePython)
  Activated = true
  AngleMax = 0
  AngleMin = 0
  Detach1 = false
  Detach2 = false
  Distance = 0
  Distance2 = 0
  EnableAngleMax = false
  EnableAngleMin = false
  EnableLengthMax = false
  EnableLengthMin = false
  JointType = 0 (Fixed)
  LengthMax = 0
  LengthMin = 0
  Offset2 = pos=(0,0,-50.8) rot=(0,0,1;0rad)
  Placement1 = pos=(187.5,5,7.25) rot=(0,0,1;0rad)
  Placement2 = pos=(122.5,2,-12.8) rot=(0,0,1;0rad)
  Reference1 = -> Assembly [BASE.Body006.Edge1007,BASE.Body006.Edge1007]
  Reference2 = -> Assembly [FRONT_VENT.Body017.Edge23,FRONT_VENT.Body017.Edge23]
FEATURE [PartDesign::Fillet] Fillet002
  Base = -> Pad049 [Edge190]
  BaseFeature = -> Pad049
  Radius = 6
  Refine = true
  SupportTransform = false
  Suppressed = false
  UseAllEdges = false
FEATURE [PartDesign::Body] Body007
  AllowCompound = false
  Group = -> [Sketch015,Pad012,Pad021,Pad023,Fillet,Sketch022,Pocket008,DatumPlane002,Sketch023,Sketch024,Sketch025,SubtractiveLoft,Sketch026,Sketch027,AdditiveLoft,LinearPattern001,Sketch028,Sketch036,DatumPlane003,DatumPlane004,Sketch041,Pocket011,Sketch043,Sketch044,Pocket013,Pocket014,Pocket015,Pocket016,DatumPlane005,Sketch047,Pocket017,DatumPlane006,Mirrored,Pocket038,Sketch089,Pad046,Sketch090,Pad047,+6 more]
  Origin = -> Origin015
  Tip = -> Fillet002
FEATURE [App::Part] Part007  label="EXIT_DUCT"
  Group = -> [Body007]
  Origin = -> Origin014
FEATURE [Sketcher::SketchObject] Sketch093
  ArcFitTolerance = 1e-06
  AttachmentSupport = -> [XY_Plane039]
  FullyConstrained = false
  MakeInternals = false
  MapMode = 5
  sketch-geometry (23):
    g0: LineSegment StartX=584.414 StartY=-280.301 StartZ=0 EndX=584.414 EndY=-279.414 EndZ=0
    g1: LineSegment StartX=583.414 StartY=-278.414 StartZ=0 EndX=496.422 EndY=-278.414 EndZ=0
    g2: ArcOfCircle CenterX=583.414 CenterY=-279.414 CenterZ=0 NormalX=0 NormalY=0 NormalZ=1 AngleXU=0 Radius=1 StartAngle=4.14e-14 EndAngle=1.5708
    g3: GeomPoint [constr] X=584.414 Y=-278.414 Z=0
    g4: LineSegment StartX=496.422 StartY=-278.414 StartZ=0 EndX=496.465 EndY=-281.514 EndZ=0
    g5: LineSegment [constr] StartX=496.465 StartY=-281.514 StartZ=0 EndX=500.406 EndY=-281.46 EndZ=0
    g6: LineSegment StartX=496.465 StartY=-281.514 StartZ=0 EndX=492.964 EndY=-281.563 EndZ=0
    g7: LineSegment StartX=492.964 StartY=-281.563 StartZ=0 EndX=493.008 EndY=-284.801 EndZ=0
    g8: LineSegment StartX=493.008 StartY=-284.801 StartZ=0 EndX=500.451 EndY=-284.698 EndZ=0
    g9: LineSegment [constr] StartX=500.451 StartY=-284.698 StartZ=0 EndX=500.406 EndY=-281.46 EndZ=0
    g10: LineSegment [constr] StartX=500.406 StartY=-281.46 StartZ=0 EndX=518.147 EndY=-281.215 EndZ=0
    g11: LineSegment [constr] StartX=518.147 StartY=-281.215 StartZ=0 EndX=537.147 EndY=-280.953 EndZ=0
    g12: LineSegment [constr] StartX=537.147 StartY=-280.953 StartZ=0 EndX=544.403 EndY=-280.853 EndZ=0
    g13: LineSegment [constr] StartX=544.403 StartY=-280.853 StartZ=0 EndX=572.362 EndY=-280.467 EndZ=0
    g14: LineSegment StartX=572.362 StartY=-280.467 StartZ=0 EndX=584.414 EndY=-280.301 EndZ=0
    g15: LineSegment [constr] StartX=518.147 StartY=-281.215 StartZ=0 EndX=518.147 EndY=-282.853 EndZ=0
    g16: LineSegment StartX=518.147 StartY=-282.853 StartZ=0 EndX=537.147 EndY=-282.853 EndZ=0
    g17: LineSegment [constr] StartX=537.147 StartY=-282.853 StartZ=0 EndX=537.147 EndY=-280.953 EndZ=0
    g18: LineSegment [constr] StartX=544.403 StartY=-280.853 StartZ=0 EndX=544.403 EndY=-282.853 EndZ=0
    g19: LineSegment StartX=544.403 StartY=-282.853 StartZ=0 EndX=572.362 EndY=-282.853 EndZ=0
    g20: LineSegment StartX=572.362 StartY=-282.853 StartZ=0 EndX=572.362 EndY=-280.467 EndZ=0
    g21: LineSegment StartX=500.451 StartY=-284.698 StartZ=0 EndX=518.147 EndY=-282.853 EndZ=0
    g22: LineSegment StartX=537.147 StartY=-282.853 StartZ=0 EndX=544.403 EndY=-282.853 EndZ=0
  constraints (58):
    c: PointOnObject(g3,g0)
    c: PointOnObject(g3,g1)
    c: Tangent(g0,g2) = -1.5708
    c: Tangent(g1,g2) = -1.5708
    c: Radius(g2) = 1
    c: Perpendicular(g0,g1)
    c: DistanceX(g1) = 496.422
    c: DistanceY(g1) = -278.414
    c: DistanceX(g0) = 584.414
    c: DistanceY(g0) = -280.301
    c: Coincident(g1,g4)
    c: Coincident(g4,g5)
    c: Coincident(g5,g10)
    c: Coincident(g4,g6)
    c: Coincident(g6,g7)
    c: Coincident(g7,g8)
    c: Coincident(g8,g9)
    c: Coincident(g9,g5)
    c: Perpendicular(g8,g9)
    c: Perpendicular(g8,g7)
    c: Perpendicular(g6,g7)
    c: Perpendicular(g4,g6)
    c: DistanceX(g8) = 500.451
    c: DistanceY(g8) = -284.698
    c: Coincident(g14,g0)
    c: Coincident(g10,g11)
    c: Perpendicular(g10,g9)
    c: Parallel(g5,g10)
    c: Coincident(g11,g12)
    c: Perpendicular(g11,g9)
    c: Coincident(g12,g13)
    c: Perpendicular(g12,g9)
    c: Coincident(g13,g14)
    c: Perpendicular(g13,g9)
    c: Perpendicular(g14,g9)
    c: DistanceY(g5) = -281.46
    c: Coincident(g10,g15)
    c: Vertical(g15)
    c: Coincident(g15,g16)
    c: Coincident(g16,g17)
    c: Coincident(g17,g11)
    c: Coincident(g12,g18)
    c: Vertical(g18)
    c: Coincident(g18,g19)
    c: Coincident(g19,g20)
    c: Coincident(g20,g13)
    c: Parallel(g19,g16)
    c: Parallel(g16,g1)
    c: Vertical(g17)
    c: DistanceX(g11,g11) = 19
    c: PointOnObject(g16,g19)
    c: DistanceY(g18,g18) = 2
    c: Vertical(g20)
    c: Coincident(g21,g8)
    c: Coincident(g21,g15)
    c: Coincident(g22,g16)
    c: Coincident(g22,g18)
    c: Horizontal(g22)
FEATURE [PartDesign::Pad] Pad051
  BaseFeature = -> Pad041
  Direction = (0,0,1)
  Length = 30
  Length2 = 10
  Profile = -> Sketch093
  ReferenceAxis = -> Sketch093 [N_Axis]
  Refine = true
  Suppressed = false
  Type = 0
FEATURE [PartDesign::Plane] DatumPlane022
  AttachmentOffset = pos=(0,0,31) rot=(0,0,1;0rad)
  AttachmentSupport = -> [DatumPlane020]
  Length = 698.227
  MapMode = 5
  Placement = pos=(0,0,34) rot=(0,0,1;0rad)
  ResizeMode = 0
  Width = 412.39
FEATURE [Sketcher::SketchObject] Sketch095  label="cut at side for ribbon cable"
  ArcFitTolerance = 1e-06
  AttachmentSupport = -> [DatumPlane022]
  FullyConstrained = false
  MakeInternals = false
  MapMode = 5
  Placement = pos=(0,0,34) rot=(0,0,1;0rad)
  sketch-geometry (4):
    g0: LineSegment [constr] StartX=527.467 StartY=-273.043 StartZ=0 EndX=527.467 EndY=-297.368 EndZ=0
    g1: LineSegment [constr] StartX=527.467 StartY=-297.368 StartZ=0 EndX=535.467 EndY=-297.368 EndZ=0
    g2: LineSegment [constr] StartX=535.467 StartY=-297.368 StartZ=0 EndX=535.467 EndY=-273.043 EndZ=0
    g3: LineSegment [constr] StartX=535.467 StartY=-273.043 StartZ=0 EndX=527.467 EndY=-273.043 EndZ=0
  constraints (9):
    c: Coincident(g0,g1)
    c: Coincident(g1,g2)
    c: Coincident(g2,g3)
    c: Coincident(g3,g0)
    c: Vertical(g0)
    c: Vertical(g2)
    c: Horizontal(g1)
    c: Horizontal(g3)
    c: Distance(g0,g2) = 8
FEATURE [PartDesign::Pocket] Pocket041
  BaseFeature = -> Pad051
  Direction = (0,0,-1)
  Length = 10
  Length2 = 5
  Midplane = true
  Profile = -> Sketch079 [Edge15,Edge14]
  ReferenceAxis = -> Sketch079 [N_Axis]
  Refine = true
  Suppressed = false
  Type = 0
FEATURE [PartDesign::Pocket] Pocket035
  BaseFeature = -> Pocket041
  Direction = (0,0,-1)
  Length = 5
  Length2 = 5
  Profile = -> Sketch082
  ReferenceAxis = -> Sketch082 [N_Axis]
  Refine = true
  Reversed = true
  Suppressed = false
  Type = 0
FEATURE [PartDesign::Plane] DatumPlane021
  AttachmentSupport = -> [Pocket035]
  Length = 652.217
  MapMode = 5
  Placement = pos=(3.1038,-283.809,0) rot=(-0.003866,0.707101,0.707101;3.14933rad)
  ResizeMode = 0
  Width = 102.301
FEATURE [Sketcher::SketchObject] Sketch083
  ArcFitTolerance = 1e-06
  AttachmentSupport = -> [DatumPlane021]
  FullyConstrained = true
  MakeInternals = false
  MapMode = 5
  Placement = pos=(3.1038,-283.809,0) rot=(-0.003866,0.707101,0.707101;3.14933rad)
  expr: Constraints[4] = <<components>>.m3_hole - 1.3
  sketch-geometry (15):
    g0: LineSegment [constr] StartX=-549.7 StartY=9.5 StartZ=0 EndX=-528.7 EndY=9.5 EndZ=0
    g1: Circle CenterX=-549.7 CenterY=9.5 CenterZ=0 NormalX=0 NormalY=0 NormalZ=1 AngleXU=0 Radius=1.1
    g2: Circle CenterX=-528.7 CenterY=9.5 CenterZ=0 NormalX=0 NormalY=0 NormalZ=1 AngleXU=0 Radius=1.1
    g3: LineSegment [constr] StartX=-549.7 StartY=9.5 StartZ=0 EndX=-563.7 EndY=9.5 EndZ=0
    g4: LineSegment StartX=-537 StartY=19.2 StartZ=0 EndX=-537 EndY=11.7 EndZ=0
    g5: LineSegment StartX=-537 StartY=11.7 StartZ=0 EndX=-520.4 EndY=11.7 EndZ=0
    g6: LineSegment StartX=-520.4 StartY=11.7 StartZ=0 EndX=-520.4 EndY=19.2 EndZ=0
    g7: LineSegment StartX=-520.4 StartY=19.2 StartZ=0 EndX=-537 EndY=19.2 EndZ=0
    g8: LineSegment [constr] StartX=-528.7 StartY=9.5 StartZ=0 EndX=-528.7 EndY=19.2 EndZ=0
    g9: LineSegment [constr] StartX=-549.7 StartY=9.5 StartZ=0 EndX=-549.7 EndY=15.45 EndZ=0
    g10: LineSegment StartX=-559.2 StartY=11.7 StartZ=0 EndX=-540.2 EndY=11.7 EndZ=0
    g11: LineSegment StartX=-540.2 StartY=11.7 StartZ=0 EndX=-540.2 EndY=19.2 EndZ=0
    g12: LineSegment StartX=-540.2 StartY=19.2 StartZ=0 EndX=-559.2 EndY=19.2 EndZ=0
    g13: LineSegment StartX=-559.2 StartY=19.2 StartZ=0 EndX=-559.2 EndY=11.7 EndZ=0
    g14: GeomPoint [constr] X=-549.7 Y=15.45 Z=0
  constraints (40):
    c: Horizontal(g0)
    c: Coincident(g1,g0)
    c: Coincident(g2,g0)
    c: Equal(g1,g2)
    c: Diameter(g2) = 2.2
    c: Coincident(g3,g0)
    c: Horizontal(g3)
    c: Distance(g3) = 14
    c: Distance(g3,g0) = 35
    c: Coincident(g4,g5)
    c: Coincident(g5,g6)
    c: Coincident(g6,g7)
    c: Coincident(g7,g4)
    c: Vertical(g4)
    c: Vertical(g6)
    c: Horizontal(g5)
    c: Horizontal(g7)
    c: Distance(g4,g6) = 16.6
    c: Distance(g5,g7) = 7.5
    c: Coincident(g8,g0)
    c: Symmetric(g7,g7,g8)
    c: Vertical(g8)
    c: DistanceX(g4) = -537
    c: DistanceY(g4) = 19.2
    c: DistanceY(g3) = 9.5
    c: Coincident(g9,g0)
    c: Vertical(g9)
    c: Coincident(g10,g11)
    c: Coincident(g11,g12)
    c: Coincident(g12,g13)
    c: Coincident(g13,g10)
    c: Horizontal(g10)
    c: Horizontal(g12)
    c: Vertical(g11)
    c: Vertical(g13)
    c: Symmetric(g12,g10,g14)
    c: Distance(g11,g13) = 19
    c: Distance(g10,g12) = 7.5
    c: Coincident(g14,g9)
    c: PointOnObject(g4,g10)
FEATURE [PartDesign::Pocket] Pocket036
  BaseFeature = -> Pocket035
  Direction = (0.0109356,-0.99994,0)
  Length = 7
  Length2 = 5
  Profile = -> Sketch083
  ReferenceAxis = -> Sketch083 [N_Axis]
  Refine = true
  Suppressed = false
  Type = 0
FEATURE [PartDesign::Pad] Pad042
  BaseFeature = -> Pocket036
  Direction = (0,0,1)
  Length = 10
  Length2 = 10
  Profile = -> Sketch084
  ReferenceAxis = -> Sketch084 [N_Axis]
  Refine = true
  Suppressed = false
  Type = 0
FEATURE [Sketcher::SketchObject] Sketch096
  ArcFitTolerance = 1e-06
  AttachmentSupport = -> [DatumPlane021]
  FullyConstrained = false
  MakeInternals = false
  MapMode = 5
  Placement = pos=(3.1038,-283.809,0) rot=(-0.003866,0.707101,0.707101;3.14933rad)
  sketch-geometry (8):
    g0: LineSegment StartX=-568.28 StartY=26.01 StartZ=0 EndX=-568.28 EndY=9 EndZ=0
    g1: LineSegment StartX=-568.28 StartY=9 StartZ=0 EndX=-553.192 EndY=9 EndZ=0
    g2: LineSegment StartX=-509.954 StartY=9 StartZ=0 EndX=-509.954 EndY=26.01 EndZ=0
    g3: LineSegment StartX=-509.954 StartY=26.01 StartZ=0 EndX=-568.28 EndY=26.01 EndZ=0
    g4: ArcOfCircle CenterX=-549.77 CenterY=9 CenterZ=0 NormalX=0 NormalY=0 NormalZ=1 AngleXU=0 Radius=3.42249 StartAngle=3.14159 EndAngle=6.28319
    g5: ArcOfCircle CenterX=-528.77 CenterY=9 CenterZ=0 NormalX=0 NormalY=0 NormalZ=1 AngleXU=0 Radius=3.42249 StartAngle=3.14159 EndAngle=6.28319
    g6: LineSegment StartX=-546.348 StartY=9 StartZ=0 EndX=-532.192 EndY=9 EndZ=0
    g7: LineSegment StartX=-525.348 StartY=9 StartZ=0 EndX=-509.954 EndY=9 EndZ=0
  constraints (26):
    c: Coincident(g0,g1)
    c: Coincident(g7,g2)
    c: Coincident(g2,g3)
    c: Coincident(g3,g0)
    c: Vertical(g0)
    c: Vertical(g2)
    c: Horizontal(g1)
    c: Horizontal(g3)
    c: DistanceX(g0) = -568.28
    c: DistanceY(g0) = 26.01
    c: DistanceY(g0) = 9
    c: PointOnObject(g4,g1)
    c: PointOnObject(g5,g6)
    c: Equal(g5,g4)
    c: PointOnObject(g4,g6)
    c: PointOnObject(g5,g7)
    c: Coincident(g1,g4)
    c: PointOnObject(g6,g4)
    c: Coincident(g6,g5)
    c: PointOnObject(g7,g5)
    c: Horizontal(g6)
    c: DistanceX(g4) = -549.77
    c: DistanceX(g5) = -528.77
    c: Horizontal(g7)
    c: PointOnObject(g5,g6)
    c: PointOnObject(g1,g6)
FEATURE [PartDesign::Pocket] Pocket042
  BaseFeature = -> Pad042
  Direction = (0.0109356,-0.99994,0)
  Length = 3.7
  Length2 = 5
  Profile = -> Sketch096
  ReferenceAxis = -> Sketch096 [N_Axis]
  Refine = true
  Suppressed = false
  Type = 0
FEATURE [PartDesign::Chamfer] Chamfer011
  Angle = 45
  Base = -> Pocket042 [Edge161,Edge163]
  BaseFeature = -> Pocket042
  ChamferType = 0
  FlipDirection = false
  Refine = true
  Size = 0.5
  Size2 = 1
  SupportTransform = false
  Suppressed = false
  UseAllEdges = false
FEATURE [PartDesign::Chamfer] Chamfer012
  Angle = 45
  Base = -> Chamfer011 [Edge19,Edge15]
  BaseFeature = -> Chamfer011
  ChamferType = 0
  FlipDirection = false
  Refine = true
  Size = 2
  Size2 = 1
  SupportTransform = false
  Suppressed = false
  UseAllEdges = false
FEATURE [PartDesign::Chamfer] Chamfer013
  Angle = 45
  Base = -> Chamfer012 [Edge194,Edge198,Edge201,Edge200,Edge196,Edge192,Edge188,Edge190]
  BaseFeature = -> Chamfer012
  ChamferType = 0
  FlipDirection = false
  Refine = true
  Size = 2.4
  Size2 = 1
  SupportTransform = false
  Suppressed = false
  UseAllEdges = false
FEATURE [PartDesign::Chamfer] Chamfer014
  Angle = 45
  Base = -> Chamfer013 [Edge7]
  BaseFeature = -> Chamfer013
  ChamferType = 0
  FlipDirection = false
  Refine = true
  Size = 1.29
  Size2 = 1
  SupportTransform = false
  Suppressed = false
  UseAllEdges = false
FEATURE [PartDesign::Body] Body018
  AllowCompound = false
  Group = -> [Sketch079,Pad039,Sketch080,Pad040,Sketch081,Pad041,Pad051,Pocket041,Sketch082,DatumPlane020,Pocket035,DatumPlane021,Sketch083,Pocket036,Sketch084,Pad042,Pocket042,Sketch093,Chamfer011,Sketch095,DatumPlane022,Sketch096,Chamfer012,Chamfer013,Chamfer014]
  Origin = -> Origin039
  Tip = -> Chamfer014
FEATURE [App::Part] Part018  label="GPU_bracket"
  Group = -> [Body018]
  Origin = -> Origin038
FEATURE [PartDesign::Plane] DatumPlane023
  AttachmentOffset = pos=(0,0,7) rot=(0,0,1;0rad)
  AttachmentSupport = -> [XY_Plane041]
  Length = 396.104
  MapMode = 5
  Placement = pos=(0,0,7) rot=(0,0,1;0rad)
  ResizeMode = 0
  Width = 339.742
FEATURE [Sketcher::SketchObject] Sketch097
  ArcFitTolerance = 1e-06
  AttachmentSupport = -> [DatumPlane023]
  FullyConstrained = false
  MakeInternals = false
  MapMode = 5
  Placement = pos=(0,0,7) rot=(0,0,1;0rad)
  sketch-geometry (4):
    g0: LineSegment StartX=105.345 StartY=-233.638 StartZ=0 EndX=105.345 EndY=-255.638 EndZ=0
    g1: LineSegment StartX=105.345 StartY=-255.638 StartZ=0 EndX=113.345 EndY=-255.638 EndZ=0
    g2: LineSegment StartX=113.345 StartY=-255.638 StartZ=0 EndX=113.345 EndY=-233.638 EndZ=0
    g3: LineSegment StartX=113.345 StartY=-233.638 StartZ=0 EndX=105.345 EndY=-233.638 EndZ=0
  constraints (10):
    c: Coincident(g0,g1)
    c: Coincident(g1,g2)
    c: Coincident(g2,g3)
    c: Coincident(g3,g0)
    c: Vertical(g0)
    c: Vertical(g2)
    c: Horizontal(g1)
    c: Horizontal(g3)
    c: Distance(g0,g2) = 8
    c: Distance(g1,g3) = 22
FEATURE [PartDesign::Pocket] Pocket043
  BaseFeature = -> Pad044
  Direction = (0,0,-1)
  Length = 4
  Length2 = 5
  Profile = -> Sketch097
  ReferenceAxis = -> Sketch097 [N_Axis]
  Refine = true
  Suppressed = false
  Type = 0
FEATURE [PartDesign::Fillet] Fillet003
  Base = -> Pocket043 [Edge27,Edge26]
  BaseFeature = -> Pocket043
  Radius = 3.99
  Refine = true
  SupportTransform = false
  Suppressed = false
  UseAllEdges = false
FEATURE [PartDesign::Body] Body019
  AllowCompound = false
  Group = -> [Sketch085,Pad043,Chamfer010,Sketch086,Pad044,Sketch097,DatumPlane023,Pocket043,Fillet003]
  Origin = -> Origin041
  Tip = -> Fillet003
FEATURE [App::Part] Part019  label="top back cover"
  Group = -> [Body019]
  Origin = -> Origin040
FEATURE [Sketcher::SketchObject] Sketch098
  ArcFitTolerance = 1e-06
  AttachmentSupport = -> [DatumPlane010]
  FullyConstrained = false
  MakeInternals = false
  MapMode = 5
  Placement = pos=(340,0,0) rot=(0.57735,0.57735,0.57735;2.0944rad)
  expr: Constraints[14] = <<choices>>.exit_height + 3 - <<choices>>.base_under_mb_thickness
  expr: Constraints[17] = <<components>>.fan_h + 4
  sketch-geometry (24):
    g0: LineSegment StartX=3.2 StartY=0 StartZ=0 EndX=3.2 EndY=33.75 EndZ=0
    g1: LineSegment StartX=26.2 StartY=56.75 StartZ=0 EndX=209.995 EndY=56.75 EndZ=0
    g2: LineSegment StartX=210 StartY=56.745 StartZ=0 EndX=210 EndY=0 EndZ=0
    g3: LineSegment StartX=210 StartY=0 StartZ=0 EndX=208 EndY=0 EndZ=0
    g4: LineSegment [constr] StartX=208 StartY=0 StartZ=0 EndX=208 EndY=30 EndZ=0
    g5: LineSegment [constr] StartX=184 StartY=54 StartZ=0 EndX=29 EndY=54 EndZ=0
    g6: LineSegment [constr] StartX=5 StartY=30 StartZ=0 EndX=5 EndY=0 EndZ=0
    g7: LineSegment StartX=5 StartY=0 StartZ=0 EndX=3.2 EndY=0 EndZ=0
    g8: ArcOfCircle [constr] CenterX=29 CenterY=30 CenterZ=0 NormalX=0 NormalY=0 NormalZ=1 AngleXU=0 Radius=24 StartAngle=1.5708 EndAngle=3.14159
    g9: GeomPoint [constr] X=5 Y=54 Z=0
    g10: ArcOfCircle [constr] CenterX=184 CenterY=30 CenterZ=0 NormalX=0 NormalY=0 NormalZ=1 AngleXU=0 Radius=24 StartAngle=0 EndAngle=1.5708
    g11: GeomPoint [constr] X=208 Y=54 Z=0
    g12: ArcOfCircle CenterX=26.2 CenterY=33.75 CenterZ=0 NormalX=0 NormalY=0 NormalZ=1 AngleXU=0 Radius=23 StartAngle=1.5708 EndAngle=3.14159
    g13: GeomPoint [constr] X=3.2 Y=56.75 Z=0
    g14: ArcOfCircle CenterX=209.995 CenterY=56.745 CenterZ=0 NormalX=0 NormalY=0 NormalZ=1 AngleXU=0 Radius=0.005 StartAngle=-6.315e-13 EndAngle=1.5708
    g15: GeomPoint [constr] X=210 Y=56.75 Z=0
    g16: LineSegment StartX=5 StartY=0 StartZ=0 EndX=208 EndY=0 EndZ=0
    g17: Circle CenterX=29 CenterY=30 CenterZ=0 NormalX=0 NormalY=0 NormalZ=1 AngleXU=0 Radius=24
    g18: Circle CenterX=184 CenterY=30 CenterZ=0 NormalX=0 NormalY=0 NormalZ=1 AngleXU=0 Radius=24
    g19: Circle CenterX=80.6634 CenterY=29 CenterZ=0 NormalX=0 NormalY=0 NormalZ=1 AngleXU=0 Radius=24
    g20: Circle CenterX=132.327 CenterY=30 CenterZ=0 NormalX=0 NormalY=0 NormalZ=1 AngleXU=0 Radius=24
    g21: LineSegment [constr] StartX=29 StartY=30 StartZ=0 EndX=80.6634 EndY=29 EndZ=0
    g22: LineSegment [constr] StartX=80.6634 StartY=29 StartZ=0 EndX=132.327 EndY=30 EndZ=0
    g23: LineSegment [constr] StartX=132.327 StartY=30 StartZ=0 EndX=184 EndY=30 EndZ=0
  constraints (57):
    c: PointOnObject(g0,g-1)
    c: Vertical(g0)
    c: Horizontal(g1)
    c: PointOnObject(g2,g-1)
    c: Vertical(g2)
    c: Coincident(g2,g3)
    c: PointOnObject(g3,g-1)
    c: Coincident(g3,g4)
    c: Vertical(g4)
    c: Horizontal(g5)
    c: PointOnObject(g6,g-1)
    c: Vertical(g6)
    c: Coincident(g6,g7)
    c: Coincident(g7,g0)
    c: DistanceY(g13) = 56.75
    c: DistanceX(g0) = 3.2
    c: DistanceX(g6) = 5
    c: DistanceY(g9) = 54
    c: DistanceX(g3) = 208
    c: PointOnObject(g9,g5)
    c: PointOnObject(g9,g6)
    c: Tangent(g5,g8) = -1.5708
    c: Tangent(g6,g8) = -1.5708
    c: DistanceX(g3,g3) = 2
    c: PointOnObject(g11,g4)
    c: PointOnObject(g11,g5)
    c: Tangent(g4,g10) = -1.5708
    c: Tangent(g5,g10) = -1.5708
    c: Equal(g8,g10)
    c: PointOnObject(g13,g0)
    c: PointOnObject(g13,g1)
    c: Tangent(g0,g12) = 1.5708
    c: Tangent(g1,g12) = 1.5708
    c: PointOnObject(g15,g1)
    c: PointOnObject(g15,g2)
    c: Tangent(g1,g14) = 1.5708
    c: Tangent(g2,g14) = 1.5708
    c: Radius(g12) = 23
    c: Radius(g8) = 24
    c: Coincident(g16,g6)
    c: Coincident(g16,g3)
    c: Coincident(g17,g8)
    c: Coincident(g18,g10)
    c: Equal(g17,g19)
    c: Equal(g19,g20)
    c: Equal(g20,g18)
    c: Equal(g17,g8)
    c: Coincident(g21,g8)
    c: Coincident(g21,g19)
    c: Coincident(g22,g19)
    c: Coincident(g22,g20)
    c: Coincident(g23,g20)
    c: Coincident(g23,g10)
    c: Horizontal(g23)
    c: Equal(g23,g22)
    c: Equal(g22,g21)
    c: Radius(g14) = 0.005
FEATURE [PartDesign::Pad] Pad052
  BaseFeature = -> Chamfer008
  Direction = (1,0,0)
  Length = 1
  Length2 = 10
  Midplane = true
  Placement = pos=(286,0,0) rot=(0.57735,0.57735,0.57735;2.0944rad)
  Profile = -> Sketch098
  ReferenceAxis = -> Sketch098 [N_Axis]
  Refine = true
  Suppressed = false
  Type = 0
FEATURE [App::FeaturePython] Joint022  label="Fixed019"  # Assembly joint (typed FeaturePython)
  Activated = true
  AngleMax = 0
  AngleMin = 0
  Detach1 = false
  Detach2 = false
  Distance = 0
  Distance2 = 0
  EnableAngleMax = false
  EnableAngleMin = false
  EnableLengthMax = false
  EnableLengthMin = false
  JointType = 0 (Fixed)
  LengthMax = 0
  LengthMin = 0
  Placement1 = pos=(332.5,40,3.411e-13) rot=(0,0,1;0rad)
  Placement2 = pos=(332.5,40,1.5) rot=(0,0,1;0rad)
  Reference1 = -> Assembly [FAN_SHROUD.Body014.Edge27,FAN_SHROUD.Body014.Edge27]
  Reference2 = -> Assembly [BASE.Body006.Edge432,BASE.Body006.Edge432]
FEATURE [Assembly::JointGroup] Joints
  Group = -> [GroundedJoint,Joint004,Joint,Joint012,Joint014,Joint015,Joint016,Joint018,Joint019,Joint020,Joint021,Joint022]
FEATURE [Assembly::AssemblyObject] Assembly
  Group = -> [Joints,BASE,GroundedJoint,MOTHERBOARD,Joint004,PSU,GPU,Joint,EXIT_DUCT,LEFT_END,FRONT_VENT,FRAME,SCREEN,Joint012,GPU_bracket,Joint014,top_back_cover001,Joint015,LEG_CLAMP,Joint016,FAN_SHROUD,Joint018,Joint019,Joint020,Joint021,Joint022]
  Origin = -> Origin027
  Type = Assembly
FEATURE [Sketcher::SketchObject] Sketch099
  ArcFitTolerance = 1e-06
  AttachmentSupport = -> [DatumPlane011]
  FullyConstrained = false
  MakeInternals = false
  MapMode = 5
  Placement = pos=(313,0,0) rot=(0.57735,0.57735,0.57735;2.0944rad)
  sketch-geometry (4):
    g0: LineSegment StartX=144.683 StartY=54.6555 StartZ=0 EndX=144.683 EndY=13.734 EndZ=0
    g1: LineSegment StartX=144.683 StartY=13.734 StartZ=0 EndX=156.349 EndY=13.734 EndZ=0
    g2: LineSegment StartX=156.349 StartY=13.734 StartZ=0 EndX=156.349 EndY=54.6555 EndZ=0
    g3: LineSegment StartX=156.349 StartY=54.6555 StartZ=0 EndX=144.683 EndY=54.6555 EndZ=0
  constraints (8):
    c: Coincident(g0,g1)
    c: Coincident(g1,g2)
    c: Coincident(g2,g3)
    c: Coincident(g3,g0)
    c: Vertical(g0)
    c: Vertical(g2)
    c: Horizontal(g1)
    c: Horizontal(g3)
FEATURE [PartDesign::Pad] Pad053
  BaseFeature = -> Pad052
  Direction = (1,0,0)
  Length = 2
  Length2 = 10
  Placement = pos=(286,0,0) rot=(0.57735,0.57735,0.57735;2.0944rad)
  Profile = -> Sketch099
  ReferenceAxis = -> Sketch099 [N_Axis]
  Refine = true
  Reversed = true
  Suppressed = false
  Type = 0
FEATURE [PartDesign::Body] Body014
  AllowCompound = false
  Group = -> [Sketch057,DatumPlane010,DatumPlane011,DatumPlane012,DatumPlane013,Pad027,Sketch058,Sketch059,Sketch060,Sketch061,AdditiveLoft001,Sketch062,AdditiveLoft002,DatumPlane014,Sketch063,Sketch076,Pad037,Chamfer008,Sketch098,Pad052,Sketch099,Pad053]
  Origin = -> Origin031
  Tip = -> Pad053
FEATURE [App::Part] Part014  label="FAN_SHROUD"
  Group = -> [Body014]
  Origin = -> Origin030
FEATURE [PartDesign::Pocket] Pocket044
  BaseFeature = -> Pocket027
  Direction = (-1,0,0)
  Length = 8
  Length2 = 5
  Placement = pos=(0,0,0) rot=(1,1,1;2.0944rad)
  Profile = -> Sketch030 [Edge6]
  ReferenceAxis = -> Sketch030 [N_Axis]
  Refine = true
  Reversed = true
  Suppressed = false
  Type = 0
  expr: Length = <<choices>>.leg_width - 2
FEATURE [PartDesign::Chamfer] Chamfer015
  Angle = 45
  Base = -> Pocket044 [Edge6,Edge8]
  BaseFeature = -> Pocket044
  ChamferType = 0
  FlipDirection = false
  Placement = pos=(0,0,0) rot=(1,1,1;2.0944rad)
  Refine = true
  Size = 1
  Size2 = 1
  SupportTransform = false
  Suppressed = false
  UseAllEdges = false
FEATURE [PartDesign::Body] Body008
  AllowCompound = false
  Group = -> [Sketch030,Pad015,Sketch064,Pocket027,Pocket044,Chamfer015]
  Origin = -> Origin018
  Tip = -> Chamfer015
FEATURE [App::Part] Part008  label="LEG_A"
  Group = -> [Body008]
  Origin = -> Origin017
FEATURE [PartDesign::Chamfer] Chamfer016
  Angle = 45
  Base = -> Chamfer [Edge21,Edge23]
  BaseFeature = -> Chamfer
  ChamferType = 0
  FlipDirection = false
  Placement = pos=(0,0,0) rot=(1,1,1;2.0944rad)
  Refine = true
  Size = 1
  Size2 = 1
  SupportTransform = false
  Suppressed = false
  UseAllEdges = false
FEATURE [PartDesign::Body] Body009
  AllowCompound = false
  Group = -> [Sketch031,Pad030,Sketch065,Pocket029,Chamfer,Chamfer016]
  Origin = -> Origin020
  Tip = -> Chamfer016
FEATURE [App::Part] Part009  label="LEG_B"
  Group = -> [Body009]
  Origin = -> Origin019
